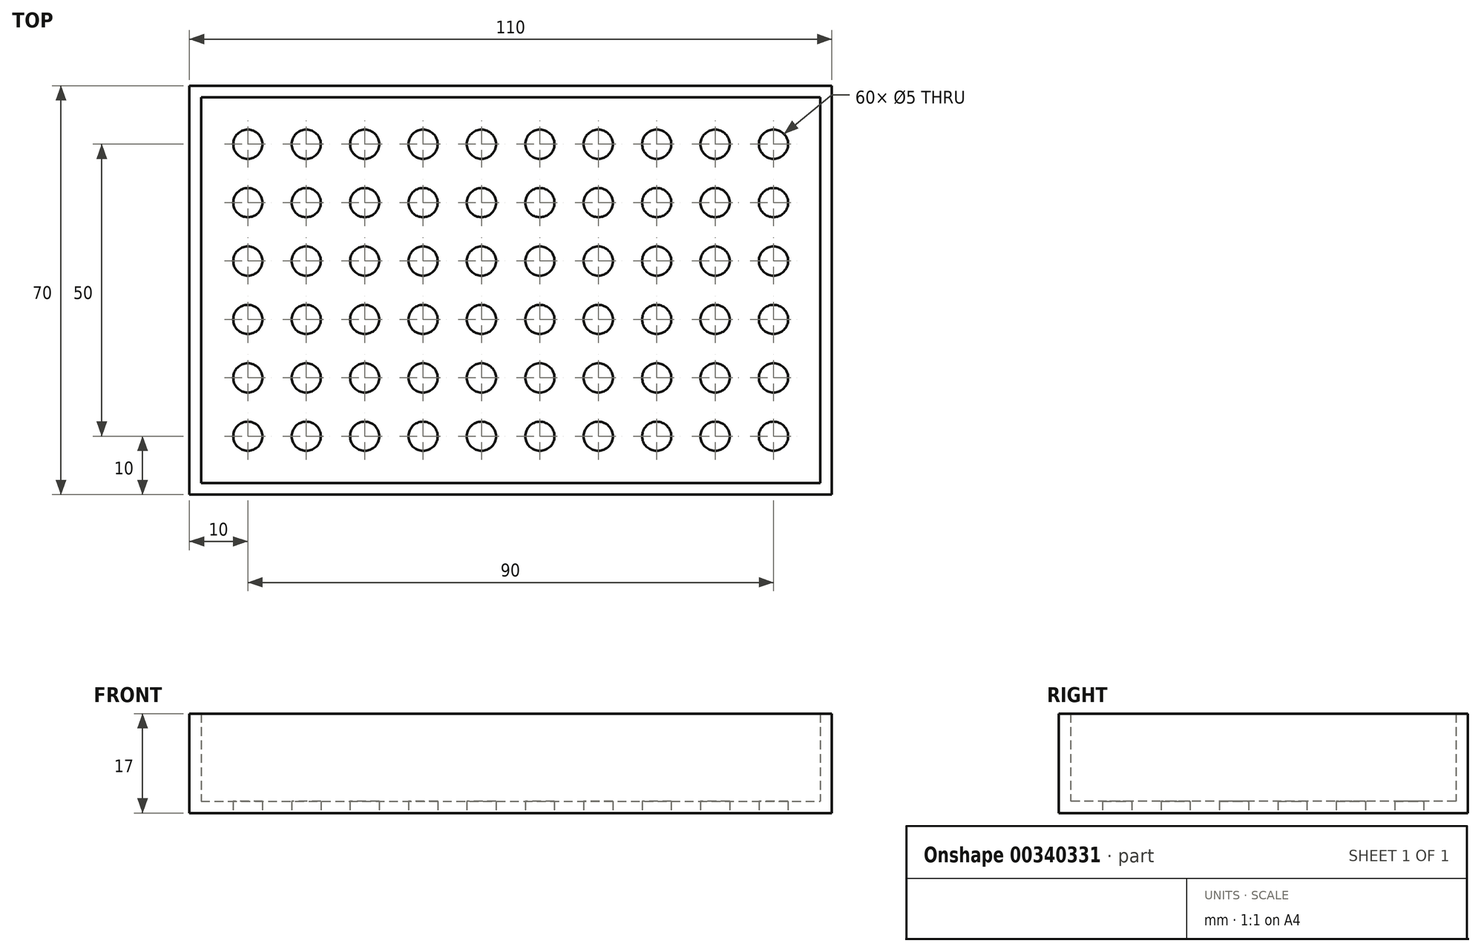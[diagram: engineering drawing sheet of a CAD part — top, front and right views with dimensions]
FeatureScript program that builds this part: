
annotation { "Feature Type Name" : "Feature", "Feature Type Description" : "" }
export const myFeature = defineFeature(function(context is Context, id is Id, definition is map)
    precondition{}
    {
        {
            var Q0;
            Q0=qCreatedBy(makeId("Top.planeOp"),FACE);
            var sketch = newSketch(context, id + "F0", { "sketchPlane" : qUnion([Q0])});
            skLineSegment(sketch, "E0.bottom", {"start": v(-55, 35) * mm, "end": v(55, 35) * mm});
            skLineSegment(sketch, "E0.top", {"start": v(-55, -35) * mm, "end": v(55, -35) * mm});
            skLineSegment(sketch, "E0.left", {"start": v(-55, 35) * mm, "end": v(-55, -35) * mm});
            skLineSegment(sketch, "E0.right", {"start": v(55, 35) * mm, "end": v(55, -35) * mm});
            skCircle(sketch, "E1.1.1.0", {"center": v(-45, -25) * mm, "radius": 2.5 * mm});
            skCircle(sketch, "E1.1.2.0", {"center": v(-45, -15) * mm, "radius": 2.5 * mm});
            skCircle(sketch, "E1.1.3.0", {"center": v(-45, -5) * mm, "radius": 2.5 * mm});
            skCircle(sketch, "E1.1.4.0", {"center": v(-45, 5) * mm, "radius": 2.5 * mm});
            skCircle(sketch, "E1.1.5.0", {"center": v(-45, 15) * mm, "radius": 2.5 * mm});
            skCircle(sketch, "E1.1.6.0", {"center": v(-45, 25) * mm, "radius": 2.5 * mm});
            skCircle(sketch, "E1.2.1.0", {"center": v(-35, -25) * mm, "radius": 2.5 * mm});
            skCircle(sketch, "E1.2.2.0", {"center": v(-35, -15) * mm, "radius": 2.5 * mm});
            skCircle(sketch, "E1.2.3.0", {"center": v(-35, -5) * mm, "radius": 2.5 * mm});
            skCircle(sketch, "E1.2.4.0", {"center": v(-35, 5) * mm, "radius": 2.5 * mm});
            skCircle(sketch, "E1.2.5.0", {"center": v(-35, 15) * mm, "radius": 2.5 * mm});
            skCircle(sketch, "E1.2.6.0", {"center": v(-35, 25) * mm, "radius": 2.5 * mm});
            skCircle(sketch, "E1.3.1.0", {"center": v(-25, -25) * mm, "radius": 2.5 * mm});
            skCircle(sketch, "E1.3.2.0", {"center": v(-25, -15) * mm, "radius": 2.5 * mm});
            skCircle(sketch, "E1.3.3.0", {"center": v(-25, -5) * mm, "radius": 2.5 * mm});
            skCircle(sketch, "E1.3.4.0", {"center": v(-25, 5) * mm, "radius": 2.5 * mm});
            skCircle(sketch, "E1.3.5.0", {"center": v(-25, 15) * mm, "radius": 2.5 * mm});
            skCircle(sketch, "E1.3.6.0", {"center": v(-25, 25) * mm, "radius": 2.5 * mm});
            skCircle(sketch, "E1.4.1.0", {"center": v(-15, -25) * mm, "radius": 2.5 * mm});
            skCircle(sketch, "E1.4.2.0", {"center": v(-15, -15) * mm, "radius": 2.5 * mm});
            skCircle(sketch, "E1.4.3.0", {"center": v(-15, -5) * mm, "radius": 2.5 * mm});
            skCircle(sketch, "E1.4.4.0", {"center": v(-15, 5) * mm, "radius": 2.5 * mm});
            skCircle(sketch, "E1.4.5.0", {"center": v(-15, 15) * mm, "radius": 2.5 * mm});
            skCircle(sketch, "E1.4.6.0", {"center": v(-15, 25) * mm, "radius": 2.5 * mm});
            skCircle(sketch, "E1.5.1.0", {"center": v(-5, -25) * mm, "radius": 2.5 * mm});
            skCircle(sketch, "E1.5.2.0", {"center": v(-5, -15) * mm, "radius": 2.5 * mm});
            skCircle(sketch, "E1.5.3.0", {"center": v(-5, -5) * mm, "radius": 2.5 * mm});
            skCircle(sketch, "E1.5.4.0", {"center": v(-5, 5) * mm, "radius": 2.5 * mm});
            skCircle(sketch, "E1.5.5.0", {"center": v(-5, 15) * mm, "radius": 2.5 * mm});
            skCircle(sketch, "E1.5.6.0", {"center": v(-5, 25) * mm, "radius": 2.5 * mm});
            skCircle(sketch, "E1.6.1.0", {"center": v(5, -25) * mm, "radius": 2.5 * mm});
            skCircle(sketch, "E1.6.2.0", {"center": v(5, -15) * mm, "radius": 2.5 * mm});
            skCircle(sketch, "E1.6.3.0", {"center": v(5, -5) * mm, "radius": 2.5 * mm});
            skCircle(sketch, "E1.6.4.0", {"center": v(5, 5) * mm, "radius": 2.5 * mm});
            skCircle(sketch, "E1.6.5.0", {"center": v(5, 15) * mm, "radius": 2.5 * mm});
            skCircle(sketch, "E1.6.6.0", {"center": v(5, 25) * mm, "radius": 2.5 * mm});
            skCircle(sketch, "E1.7.1.0", {"center": v(15, -25) * mm, "radius": 2.5 * mm});
            skCircle(sketch, "E1.7.2.0", {"center": v(15, -15) * mm, "radius": 2.5 * mm});
            skCircle(sketch, "E1.7.3.0", {"center": v(15, -5) * mm, "radius": 2.5 * mm});
            skCircle(sketch, "E1.7.4.0", {"center": v(15, 5) * mm, "radius": 2.5 * mm});
            skCircle(sketch, "E1.7.5.0", {"center": v(15, 15) * mm, "radius": 2.5 * mm});
            skCircle(sketch, "E1.7.6.0", {"center": v(15, 25) * mm, "radius": 2.5 * mm});
            skCircle(sketch, "E1.8.1.0", {"center": v(25, -25) * mm, "radius": 2.5 * mm});
            skCircle(sketch, "E1.8.2.0", {"center": v(25, -15) * mm, "radius": 2.5 * mm});
            skCircle(sketch, "E1.8.3.0", {"center": v(25, -5) * mm, "radius": 2.5 * mm});
            skCircle(sketch, "E1.8.4.0", {"center": v(25, 5) * mm, "radius": 2.5 * mm});
            skCircle(sketch, "E1.8.5.0", {"center": v(25, 15) * mm, "radius": 2.5 * mm});
            skCircle(sketch, "E1.8.6.0", {"center": v(25, 25) * mm, "radius": 2.5 * mm});
            skCircle(sketch, "E1.9.1.0", {"center": v(35, -25) * mm, "radius": 2.5 * mm});
            skCircle(sketch, "E1.9.2.0", {"center": v(35, -15) * mm, "radius": 2.5 * mm});
            skCircle(sketch, "E1.9.3.0", {"center": v(35, -5) * mm, "radius": 2.5 * mm});
            skCircle(sketch, "E1.9.4.0", {"center": v(35, 5) * mm, "radius": 2.5 * mm});
            skCircle(sketch, "E1.9.5.0", {"center": v(35, 15) * mm, "radius": 2.5 * mm});
            skCircle(sketch, "E1.9.6.0", {"center": v(35, 25) * mm, "radius": 2.5 * mm});
            skLineSegment(sketch, "E1.direction1", {"start": v(-55, -35) * mm, "end": v(-45, -35) * mm, "construction": true});
            skLineSegment(sketch, "E1.direction2", {"start": v(-55, -35) * mm, "end": v(-55, -25) * mm, "construction": true});
            skCircle(sketch, "E2.0.10.1", {"center": v(45, -25) * mm, "radius": 2.5 * mm});
            skCircle(sketch, "E2.0.10.2", {"center": v(45, -15) * mm, "radius": 2.5 * mm});
            skCircle(sketch, "E2.0.10.3", {"center": v(45, -5) * mm, "radius": 2.5 * mm});
            skCircle(sketch, "E2.0.10.4", {"center": v(45, 5) * mm, "radius": 2.5 * mm});
            skCircle(sketch, "E2.0.10.5", {"center": v(45, 15) * mm, "radius": 2.5 * mm});
            skCircle(sketch, "E2.0.10.6", {"center": v(45, 25) * mm, "radius": 2.5 * mm});
            skSolve(sketch);
        }
        {
            var Q0;
            Q0=makeQuery(id+"F0.imprint","IMPRINT",FACE,{"disambiguationData":[TD([[makeQuery(id+"F0.imprint","IMPRINT",EDGE,{"derivedFrom":sQuery(id+"F0.wireOp",EDGE,"E0.bottom")}),-1.0]])]});
            extrude(context, id + "F1", {"entities" : qUnion([Q0]), "depth" : 17 * mm});
        }
        {
            var Q0;
            Q0=makeQuery(id+"F1.opExtrude","CAP_FACE",FACE,{"disambiguationData":[OSD([sQuery(id+"F0.wireOp",EDGE,"E0.bottom"),sQuery(id+"F0.wireOp",EDGE,"E0.top"),sQuery(id+"F0.wireOp",EDGE,"E0.left"),sQuery(id+"F0.wireOp",EDGE,"E0.right"),sQuery(id+"F0.wireOp",EDGE,"E1.1.1.0"),sQuery(id+"F0.wireOp",EDGE,"E1.1.2.0"),sQuery(id+"F0.wireOp",EDGE,"E1.1.3.0"),sQuery(id+"F0.wireOp",EDGE,"E1.1.4.0"),sQuery(id+"F0.wireOp",EDGE,"E1.1.5.0"),sQuery(id+"F0.wireOp",EDGE,"E1.1.6.0"),sQuery(id+"F0.wireOp",EDGE,"E1.2.1.0"),sQuery(id+"F0.wireOp",EDGE,"E1.2.2.0"),sQuery(id+"F0.wireOp",EDGE,"E1.2.3.0"),sQuery(id+"F0.wireOp",EDGE,"E1.2.4.0"),sQuery(id+"F0.wireOp",EDGE,"E1.2.5.0"),sQuery(id+"F0.wireOp",EDGE,"E1.2.6.0"),sQuery(id+"F0.wireOp",EDGE,"E1.3.1.0"),sQuery(id+"F0.wireOp",EDGE,"E1.3.2.0"),sQuery(id+"F0.wireOp",EDGE,"E1.3.3.0"),sQuery(id+"F0.wireOp",EDGE,"E1.3.4.0"),sQuery(id+"F0.wireOp",EDGE,"E1.3.5.0"),sQuery(id+"F0.wireOp",EDGE,"E1.3.6.0"),sQuery(id+"F0.wireOp",EDGE,"E1.4.1.0"),sQuery(id+"F0.wireOp",EDGE,"E1.4.2.0"),sQuery(id+"F0.wireOp",EDGE,"E1.4.3.0"),sQuery(id+"F0.wireOp",EDGE,"E1.4.4.0"),sQuery(id+"F0.wireOp",EDGE,"E1.4.5.0"),sQuery(id+"F0.wireOp",EDGE,"E1.4.6.0"),sQuery(id+"F0.wireOp",EDGE,"E1.5.1.0"),sQuery(id+"F0.wireOp",EDGE,"E1.5.2.0"),sQuery(id+"F0.wireOp",EDGE,"E1.5.3.0"),sQuery(id+"F0.wireOp",EDGE,"E1.5.4.0"),sQuery(id+"F0.wireOp",EDGE,"E1.5.5.0"),sQuery(id+"F0.wireOp",EDGE,"E1.5.6.0"),sQuery(id+"F0.wireOp",EDGE,"E1.6.1.0"),sQuery(id+"F0.wireOp",EDGE,"E1.6.2.0"),sQuery(id+"F0.wireOp",EDGE,"E1.6.3.0"),sQuery(id+"F0.wireOp",EDGE,"E1.6.4.0"),sQuery(id+"F0.wireOp",EDGE,"E1.6.5.0"),sQuery(id+"F0.wireOp",EDGE,"E1.6.6.0"),sQuery(id+"F0.wireOp",EDGE,"E1.7.1.0"),sQuery(id+"F0.wireOp",EDGE,"E1.7.2.0"),sQuery(id+"F0.wireOp",EDGE,"E1.7.3.0"),sQuery(id+"F0.wireOp",EDGE,"E1.7.4.0"),sQuery(id+"F0.wireOp",EDGE,"E1.7.5.0"),sQuery(id+"F0.wireOp",EDGE,"E1.7.6.0"),sQuery(id+"F0.wireOp",EDGE,"E1.8.1.0"),sQuery(id+"F0.wireOp",EDGE,"E1.8.2.0"),sQuery(id+"F0.wireOp",EDGE,"E1.8.3.0"),sQuery(id+"F0.wireOp",EDGE,"E1.8.4.0"),sQuery(id+"F0.wireOp",EDGE,"E1.8.5.0"),sQuery(id+"F0.wireOp",EDGE,"E1.8.6.0"),sQuery(id+"F0.wireOp",EDGE,"E1.9.1.0"),sQuery(id+"F0.wireOp",EDGE,"E1.9.2.0"),sQuery(id+"F0.wireOp",EDGE,"E1.9.3.0"),sQuery(id+"F0.wireOp",EDGE,"E1.9.4.0"),sQuery(id+"F0.wireOp",EDGE,"E1.9.5.0"),sQuery(id+"F0.wireOp",EDGE,"E1.9.6.0"),sQuery(id+"F0.wireOp",EDGE,"E2.0.10.1"),sQuery(id+"F0.wireOp",EDGE,"E2.0.10.2"),sQuery(id+"F0.wireOp",EDGE,"E2.0.10.3"),sQuery(id+"F0.wireOp",EDGE,"E2.0.10.4"),sQuery(id+"F0.wireOp",EDGE,"E2.0.10.5"),sQuery(id+"F0.wireOp",EDGE,"E2.0.10.6")])],"isStart":false});
            shell(context, id + "F2", {"entities" : qUnion([Q0]), "thickness" : 2 * mm});
        }
        {
            var Q0;
            {var subQ0=sQuery(id+"F0.wireOp",EDGE,"E2.0.10.6");var subQ1=sQuery(id+"F0.wireOp",EDGE,"E2.0.10.5");var subQ2=sQuery(id+"F0.wireOp",EDGE,"E2.0.10.4");var subQ3=sQuery(id+"F0.wireOp",EDGE,"E2.0.10.3");var subQ4=sQuery(id+"F0.wireOp",EDGE,"E2.0.10.2");var subQ5=sQuery(id+"F0.wireOp",EDGE,"E2.0.10.1");var subQ6=sQuery(id+"F0.wireOp",EDGE,"E1.9.6.0");var subQ7=sQuery(id+"F0.wireOp",EDGE,"E1.9.5.0");var subQ8=sQuery(id+"F0.wireOp",EDGE,"E1.9.4.0");var subQ9=sQuery(id+"F0.wireOp",EDGE,"E1.9.3.0");var subQ10=sQuery(id+"F0.wireOp",EDGE,"E1.9.2.0");var subQ11=sQuery(id+"F0.wireOp",EDGE,"E1.9.1.0");var subQ12=sQuery(id+"F0.wireOp",EDGE,"E1.8.6.0");var subQ13=sQuery(id+"F0.wireOp",EDGE,"E1.8.5.0");var subQ14=sQuery(id+"F0.wireOp",EDGE,"E1.8.4.0");var subQ15=sQuery(id+"F0.wireOp",EDGE,"E1.8.3.0");var subQ16=sQuery(id+"F0.wireOp",EDGE,"E1.8.2.0");var subQ17=sQuery(id+"F0.wireOp",EDGE,"E1.8.1.0");var subQ18=sQuery(id+"F0.wireOp",EDGE,"E1.7.6.0");var subQ19=sQuery(id+"F0.wireOp",EDGE,"E1.7.5.0");var subQ20=sQuery(id+"F0.wireOp",EDGE,"E1.7.4.0");var subQ21=sQuery(id+"F0.wireOp",EDGE,"E1.7.3.0");var subQ22=sQuery(id+"F0.wireOp",EDGE,"E1.7.2.0");var subQ23=sQuery(id+"F0.wireOp",EDGE,"E1.7.1.0");var subQ24=sQuery(id+"F0.wireOp",EDGE,"E1.6.6.0");var subQ25=sQuery(id+"F0.wireOp",EDGE,"E1.6.5.0");var subQ26=sQuery(id+"F0.wireOp",EDGE,"E1.6.4.0");var subQ27=sQuery(id+"F0.wireOp",EDGE,"E1.6.3.0");var subQ28=sQuery(id+"F0.wireOp",EDGE,"E1.6.2.0");var subQ29=sQuery(id+"F0.wireOp",EDGE,"E1.6.1.0");var subQ30=sQuery(id+"F0.wireOp",EDGE,"E1.5.6.0");var subQ31=sQuery(id+"F0.wireOp",EDGE,"E1.5.5.0");var subQ32=sQuery(id+"F0.wireOp",EDGE,"E1.5.4.0");var subQ33=sQuery(id+"F0.wireOp",EDGE,"E1.5.3.0");var subQ34=sQuery(id+"F0.wireOp",EDGE,"E1.5.2.0");var subQ35=sQuery(id+"F0.wireOp",EDGE,"E1.5.1.0");var subQ36=sQuery(id+"F0.wireOp",EDGE,"E1.4.6.0");var subQ37=sQuery(id+"F0.wireOp",EDGE,"E1.4.5.0");var subQ38=sQuery(id+"F0.wireOp",EDGE,"E1.4.4.0");var subQ39=sQuery(id+"F0.wireOp",EDGE,"E1.4.3.0");var subQ40=sQuery(id+"F0.wireOp",EDGE,"E1.4.2.0");var subQ41=sQuery(id+"F0.wireOp",EDGE,"E1.4.1.0");var subQ42=sQuery(id+"F0.wireOp",EDGE,"E1.3.6.0");var subQ43=sQuery(id+"F0.wireOp",EDGE,"E1.3.5.0");var subQ44=sQuery(id+"F0.wireOp",EDGE,"E1.3.4.0");var subQ45=sQuery(id+"F0.wireOp",EDGE,"E1.3.3.0");var subQ46=sQuery(id+"F0.wireOp",EDGE,"E1.3.2.0");var subQ47=sQuery(id+"F0.wireOp",EDGE,"E1.3.1.0");var subQ48=sQuery(id+"F0.wireOp",EDGE,"E1.2.6.0");var subQ49=sQuery(id+"F0.wireOp",EDGE,"E1.2.5.0");var subQ50=sQuery(id+"F0.wireOp",EDGE,"E1.2.4.0");var subQ51=sQuery(id+"F0.wireOp",EDGE,"E1.2.3.0");var subQ52=sQuery(id+"F0.wireOp",EDGE,"E1.2.2.0");var subQ53=sQuery(id+"F0.wireOp",EDGE,"E1.2.1.0");var subQ54=sQuery(id+"F0.wireOp",EDGE,"E1.1.6.0");var subQ55=sQuery(id+"F0.wireOp",EDGE,"E1.1.5.0");var subQ56=sQuery(id+"F0.wireOp",EDGE,"E1.1.4.0");var subQ57=sQuery(id+"F0.wireOp",EDGE,"E1.1.3.0");var subQ58=sQuery(id+"F0.wireOp",EDGE,"E1.1.2.0");var subQ59=sQuery(id+"F0.wireOp",EDGE,"E1.1.1.0");var subQ60=sQuery(id+"F0.wireOp",EDGE,"E0.right");var subQ61=sQuery(id+"F0.wireOp",EDGE,"E0.left");var subQ62=sQuery(id+"F0.wireOp",EDGE,"E0.top");var subQ63=sQuery(id+"F0.wireOp",EDGE,"E0.bottom");Q0=makeQuery(id+"F2.opShell","OFFSET_FACE",FACE,{"disambiguationData":[OSD([subQ63,subQ62,subQ61,subQ60,subQ59,subQ58,subQ57,subQ56,subQ55,subQ54,subQ53,subQ52,subQ51,subQ50,subQ49,subQ48,subQ47,subQ46,subQ45,subQ44,subQ43,subQ42,subQ41,subQ40,subQ39,subQ38,subQ37,subQ36,subQ35,subQ34,subQ33,subQ32,subQ31,subQ30,subQ29,subQ28,subQ27,subQ26,subQ25,subQ24,subQ23,subQ22,subQ21,subQ20,subQ19,subQ18,subQ17,subQ16,subQ15,subQ14,subQ13,subQ12,subQ11,subQ10,subQ9,subQ8,subQ7,subQ6,subQ5,subQ4,subQ3,subQ2,subQ1,subQ0]),TDD([makeQuery(id+"F1.opExtrude","CAP_FACE",FACE,{"disambiguationData":[OSD([subQ63,subQ62,subQ61,subQ60,subQ59,subQ58,subQ57,subQ56,subQ55,subQ54,subQ53,subQ52,subQ51,subQ50,subQ49,subQ48,subQ47,subQ46,subQ45,subQ44,subQ43,subQ42,subQ41,subQ40,subQ39,subQ38,subQ37,subQ36,subQ35,subQ34,subQ33,subQ32,subQ31,subQ30,subQ29,subQ28,subQ27,subQ26,subQ25,subQ24,subQ23,subQ22,subQ21,subQ20,subQ19,subQ18,subQ17,subQ16,subQ15,subQ14,subQ13,subQ12,subQ11,subQ10,subQ9,subQ8,subQ7,subQ6,subQ5,subQ4,subQ3,subQ2,subQ1,subQ0])],"isStart":false})]),OD(5.0)]});}
            var Q1;
            {var subQ0=sQuery(id+"F0.wireOp",EDGE,"E2.0.10.6");var subQ1=sQuery(id+"F0.wireOp",EDGE,"E2.0.10.5");var subQ2=sQuery(id+"F0.wireOp",EDGE,"E2.0.10.4");var subQ3=sQuery(id+"F0.wireOp",EDGE,"E2.0.10.3");var subQ4=sQuery(id+"F0.wireOp",EDGE,"E2.0.10.2");var subQ5=sQuery(id+"F0.wireOp",EDGE,"E2.0.10.1");var subQ6=sQuery(id+"F0.wireOp",EDGE,"E1.9.6.0");var subQ7=sQuery(id+"F0.wireOp",EDGE,"E1.9.5.0");var subQ8=sQuery(id+"F0.wireOp",EDGE,"E1.9.4.0");var subQ9=sQuery(id+"F0.wireOp",EDGE,"E1.9.3.0");var subQ10=sQuery(id+"F0.wireOp",EDGE,"E1.9.2.0");var subQ11=sQuery(id+"F0.wireOp",EDGE,"E1.9.1.0");var subQ12=sQuery(id+"F0.wireOp",EDGE,"E1.8.6.0");var subQ13=sQuery(id+"F0.wireOp",EDGE,"E1.8.5.0");var subQ14=sQuery(id+"F0.wireOp",EDGE,"E1.8.4.0");var subQ15=sQuery(id+"F0.wireOp",EDGE,"E1.8.3.0");var subQ16=sQuery(id+"F0.wireOp",EDGE,"E1.8.2.0");var subQ17=sQuery(id+"F0.wireOp",EDGE,"E1.8.1.0");var subQ18=sQuery(id+"F0.wireOp",EDGE,"E1.7.6.0");var subQ19=sQuery(id+"F0.wireOp",EDGE,"E1.7.5.0");var subQ20=sQuery(id+"F0.wireOp",EDGE,"E1.7.4.0");var subQ21=sQuery(id+"F0.wireOp",EDGE,"E1.7.3.0");var subQ22=sQuery(id+"F0.wireOp",EDGE,"E1.7.2.0");var subQ23=sQuery(id+"F0.wireOp",EDGE,"E1.7.1.0");var subQ24=sQuery(id+"F0.wireOp",EDGE,"E1.6.6.0");var subQ25=sQuery(id+"F0.wireOp",EDGE,"E1.6.5.0");var subQ26=sQuery(id+"F0.wireOp",EDGE,"E1.6.4.0");var subQ27=sQuery(id+"F0.wireOp",EDGE,"E1.6.3.0");var subQ28=sQuery(id+"F0.wireOp",EDGE,"E1.6.2.0");var subQ29=sQuery(id+"F0.wireOp",EDGE,"E1.6.1.0");var subQ30=sQuery(id+"F0.wireOp",EDGE,"E1.5.6.0");var subQ31=sQuery(id+"F0.wireOp",EDGE,"E1.5.5.0");var subQ32=sQuery(id+"F0.wireOp",EDGE,"E1.5.4.0");var subQ33=sQuery(id+"F0.wireOp",EDGE,"E1.5.3.0");var subQ34=sQuery(id+"F0.wireOp",EDGE,"E1.5.2.0");var subQ35=sQuery(id+"F0.wireOp",EDGE,"E1.5.1.0");var subQ36=sQuery(id+"F0.wireOp",EDGE,"E1.4.6.0");var subQ37=sQuery(id+"F0.wireOp",EDGE,"E1.4.5.0");var subQ38=sQuery(id+"F0.wireOp",EDGE,"E1.4.4.0");var subQ39=sQuery(id+"F0.wireOp",EDGE,"E1.4.3.0");var subQ40=sQuery(id+"F0.wireOp",EDGE,"E1.4.2.0");var subQ41=sQuery(id+"F0.wireOp",EDGE,"E1.4.1.0");var subQ42=sQuery(id+"F0.wireOp",EDGE,"E1.3.6.0");var subQ43=sQuery(id+"F0.wireOp",EDGE,"E1.3.5.0");var subQ44=sQuery(id+"F0.wireOp",EDGE,"E1.3.4.0");var subQ45=sQuery(id+"F0.wireOp",EDGE,"E1.3.3.0");var subQ46=sQuery(id+"F0.wireOp",EDGE,"E1.3.2.0");var subQ47=sQuery(id+"F0.wireOp",EDGE,"E1.3.1.0");var subQ48=sQuery(id+"F0.wireOp",EDGE,"E1.2.6.0");var subQ49=sQuery(id+"F0.wireOp",EDGE,"E1.2.5.0");var subQ50=sQuery(id+"F0.wireOp",EDGE,"E1.2.4.0");var subQ51=sQuery(id+"F0.wireOp",EDGE,"E1.2.3.0");var subQ52=sQuery(id+"F0.wireOp",EDGE,"E1.2.2.0");var subQ53=sQuery(id+"F0.wireOp",EDGE,"E1.2.1.0");var subQ54=sQuery(id+"F0.wireOp",EDGE,"E1.1.6.0");var subQ55=sQuery(id+"F0.wireOp",EDGE,"E1.1.5.0");var subQ56=sQuery(id+"F0.wireOp",EDGE,"E1.1.4.0");var subQ57=sQuery(id+"F0.wireOp",EDGE,"E1.1.3.0");var subQ58=sQuery(id+"F0.wireOp",EDGE,"E1.1.2.0");var subQ59=sQuery(id+"F0.wireOp",EDGE,"E1.1.1.0");var subQ60=sQuery(id+"F0.wireOp",EDGE,"E0.right");var subQ61=sQuery(id+"F0.wireOp",EDGE,"E0.left");var subQ62=sQuery(id+"F0.wireOp",EDGE,"E0.top");var subQ63=sQuery(id+"F0.wireOp",EDGE,"E0.bottom");Q1=makeQuery(id+"F2.opShell","OFFSET_FACE",FACE,{"disambiguationData":[OSD([subQ63,subQ62,subQ61,subQ60,subQ59,subQ58,subQ57,subQ56,subQ55,subQ54,subQ53,subQ52,subQ51,subQ50,subQ49,subQ48,subQ47,subQ46,subQ45,subQ44,subQ43,subQ42,subQ41,subQ40,subQ39,subQ38,subQ37,subQ36,subQ35,subQ34,subQ33,subQ32,subQ31,subQ30,subQ29,subQ28,subQ27,subQ26,subQ25,subQ24,subQ23,subQ22,subQ21,subQ20,subQ19,subQ18,subQ17,subQ16,subQ15,subQ14,subQ13,subQ12,subQ11,subQ10,subQ9,subQ8,subQ7,subQ6,subQ5,subQ4,subQ3,subQ2,subQ1,subQ0]),TDD([makeQuery(id+"F1.opExtrude","CAP_FACE",FACE,{"disambiguationData":[OSD([subQ63,subQ62,subQ61,subQ60,subQ59,subQ58,subQ57,subQ56,subQ55,subQ54,subQ53,subQ52,subQ51,subQ50,subQ49,subQ48,subQ47,subQ46,subQ45,subQ44,subQ43,subQ42,subQ41,subQ40,subQ39,subQ38,subQ37,subQ36,subQ35,subQ34,subQ33,subQ32,subQ31,subQ30,subQ29,subQ28,subQ27,subQ26,subQ25,subQ24,subQ23,subQ22,subQ21,subQ20,subQ19,subQ18,subQ17,subQ16,subQ15,subQ14,subQ13,subQ12,subQ11,subQ10,subQ9,subQ8,subQ7,subQ6,subQ5,subQ4,subQ3,subQ2,subQ1,subQ0])],"isStart":false})]),OD(11.0)]});}
            var Q2;
            {var subQ0=sQuery(id+"F0.wireOp",EDGE,"E2.0.10.6");var subQ1=sQuery(id+"F0.wireOp",EDGE,"E2.0.10.5");var subQ2=sQuery(id+"F0.wireOp",EDGE,"E2.0.10.4");var subQ3=sQuery(id+"F0.wireOp",EDGE,"E2.0.10.3");var subQ4=sQuery(id+"F0.wireOp",EDGE,"E2.0.10.2");var subQ5=sQuery(id+"F0.wireOp",EDGE,"E2.0.10.1");var subQ6=sQuery(id+"F0.wireOp",EDGE,"E1.9.6.0");var subQ7=sQuery(id+"F0.wireOp",EDGE,"E1.9.5.0");var subQ8=sQuery(id+"F0.wireOp",EDGE,"E1.9.4.0");var subQ9=sQuery(id+"F0.wireOp",EDGE,"E1.9.3.0");var subQ10=sQuery(id+"F0.wireOp",EDGE,"E1.9.2.0");var subQ11=sQuery(id+"F0.wireOp",EDGE,"E1.9.1.0");var subQ12=sQuery(id+"F0.wireOp",EDGE,"E1.8.6.0");var subQ13=sQuery(id+"F0.wireOp",EDGE,"E1.8.5.0");var subQ14=sQuery(id+"F0.wireOp",EDGE,"E1.8.4.0");var subQ15=sQuery(id+"F0.wireOp",EDGE,"E1.8.3.0");var subQ16=sQuery(id+"F0.wireOp",EDGE,"E1.8.2.0");var subQ17=sQuery(id+"F0.wireOp",EDGE,"E1.8.1.0");var subQ18=sQuery(id+"F0.wireOp",EDGE,"E1.7.6.0");var subQ19=sQuery(id+"F0.wireOp",EDGE,"E1.7.5.0");var subQ20=sQuery(id+"F0.wireOp",EDGE,"E1.7.4.0");var subQ21=sQuery(id+"F0.wireOp",EDGE,"E1.7.3.0");var subQ22=sQuery(id+"F0.wireOp",EDGE,"E1.7.2.0");var subQ23=sQuery(id+"F0.wireOp",EDGE,"E1.7.1.0");var subQ24=sQuery(id+"F0.wireOp",EDGE,"E1.6.6.0");var subQ25=sQuery(id+"F0.wireOp",EDGE,"E1.6.5.0");var subQ26=sQuery(id+"F0.wireOp",EDGE,"E1.6.4.0");var subQ27=sQuery(id+"F0.wireOp",EDGE,"E1.6.3.0");var subQ28=sQuery(id+"F0.wireOp",EDGE,"E1.6.2.0");var subQ29=sQuery(id+"F0.wireOp",EDGE,"E1.6.1.0");var subQ30=sQuery(id+"F0.wireOp",EDGE,"E1.5.6.0");var subQ31=sQuery(id+"F0.wireOp",EDGE,"E1.5.5.0");var subQ32=sQuery(id+"F0.wireOp",EDGE,"E1.5.4.0");var subQ33=sQuery(id+"F0.wireOp",EDGE,"E1.5.3.0");var subQ34=sQuery(id+"F0.wireOp",EDGE,"E1.5.2.0");var subQ35=sQuery(id+"F0.wireOp",EDGE,"E1.5.1.0");var subQ36=sQuery(id+"F0.wireOp",EDGE,"E1.4.6.0");var subQ37=sQuery(id+"F0.wireOp",EDGE,"E1.4.5.0");var subQ38=sQuery(id+"F0.wireOp",EDGE,"E1.4.4.0");var subQ39=sQuery(id+"F0.wireOp",EDGE,"E1.4.3.0");var subQ40=sQuery(id+"F0.wireOp",EDGE,"E1.4.2.0");var subQ41=sQuery(id+"F0.wireOp",EDGE,"E1.4.1.0");var subQ42=sQuery(id+"F0.wireOp",EDGE,"E1.3.6.0");var subQ43=sQuery(id+"F0.wireOp",EDGE,"E1.3.5.0");var subQ44=sQuery(id+"F0.wireOp",EDGE,"E1.3.4.0");var subQ45=sQuery(id+"F0.wireOp",EDGE,"E1.3.3.0");var subQ46=sQuery(id+"F0.wireOp",EDGE,"E1.3.2.0");var subQ47=sQuery(id+"F0.wireOp",EDGE,"E1.3.1.0");var subQ48=sQuery(id+"F0.wireOp",EDGE,"E1.2.6.0");var subQ49=sQuery(id+"F0.wireOp",EDGE,"E1.2.5.0");var subQ50=sQuery(id+"F0.wireOp",EDGE,"E1.2.4.0");var subQ51=sQuery(id+"F0.wireOp",EDGE,"E1.2.3.0");var subQ52=sQuery(id+"F0.wireOp",EDGE,"E1.2.2.0");var subQ53=sQuery(id+"F0.wireOp",EDGE,"E1.2.1.0");var subQ54=sQuery(id+"F0.wireOp",EDGE,"E1.1.6.0");var subQ55=sQuery(id+"F0.wireOp",EDGE,"E1.1.5.0");var subQ56=sQuery(id+"F0.wireOp",EDGE,"E1.1.4.0");var subQ57=sQuery(id+"F0.wireOp",EDGE,"E1.1.3.0");var subQ58=sQuery(id+"F0.wireOp",EDGE,"E1.1.2.0");var subQ59=sQuery(id+"F0.wireOp",EDGE,"E1.1.1.0");var subQ60=sQuery(id+"F0.wireOp",EDGE,"E0.right");var subQ61=sQuery(id+"F0.wireOp",EDGE,"E0.left");var subQ62=sQuery(id+"F0.wireOp",EDGE,"E0.top");var subQ63=sQuery(id+"F0.wireOp",EDGE,"E0.bottom");Q2=makeQuery(id+"F2.opShell","OFFSET_FACE",FACE,{"disambiguationData":[OSD([subQ63,subQ62,subQ61,subQ60,subQ59,subQ58,subQ57,subQ56,subQ55,subQ54,subQ53,subQ52,subQ51,subQ50,subQ49,subQ48,subQ47,subQ46,subQ45,subQ44,subQ43,subQ42,subQ41,subQ40,subQ39,subQ38,subQ37,subQ36,subQ35,subQ34,subQ33,subQ32,subQ31,subQ30,subQ29,subQ28,subQ27,subQ26,subQ25,subQ24,subQ23,subQ22,subQ21,subQ20,subQ19,subQ18,subQ17,subQ16,subQ15,subQ14,subQ13,subQ12,subQ11,subQ10,subQ9,subQ8,subQ7,subQ6,subQ5,subQ4,subQ3,subQ2,subQ1,subQ0]),TDD([makeQuery(id+"F1.opExtrude","CAP_FACE",FACE,{"disambiguationData":[OSD([subQ63,subQ62,subQ61,subQ60,subQ59,subQ58,subQ57,subQ56,subQ55,subQ54,subQ53,subQ52,subQ51,subQ50,subQ49,subQ48,subQ47,subQ46,subQ45,subQ44,subQ43,subQ42,subQ41,subQ40,subQ39,subQ38,subQ37,subQ36,subQ35,subQ34,subQ33,subQ32,subQ31,subQ30,subQ29,subQ28,subQ27,subQ26,subQ25,subQ24,subQ23,subQ22,subQ21,subQ20,subQ19,subQ18,subQ17,subQ16,subQ15,subQ14,subQ13,subQ12,subQ11,subQ10,subQ9,subQ8,subQ7,subQ6,subQ5,subQ4,subQ3,subQ2,subQ1,subQ0])],"isStart":false})]),OD(17.0)]});}
            var Q3;
            {var subQ0=sQuery(id+"F0.wireOp",EDGE,"E2.0.10.6");var subQ1=sQuery(id+"F0.wireOp",EDGE,"E2.0.10.5");var subQ2=sQuery(id+"F0.wireOp",EDGE,"E2.0.10.4");var subQ3=sQuery(id+"F0.wireOp",EDGE,"E2.0.10.3");var subQ4=sQuery(id+"F0.wireOp",EDGE,"E2.0.10.2");var subQ5=sQuery(id+"F0.wireOp",EDGE,"E2.0.10.1");var subQ6=sQuery(id+"F0.wireOp",EDGE,"E1.9.6.0");var subQ7=sQuery(id+"F0.wireOp",EDGE,"E1.9.5.0");var subQ8=sQuery(id+"F0.wireOp",EDGE,"E1.9.4.0");var subQ9=sQuery(id+"F0.wireOp",EDGE,"E1.9.3.0");var subQ10=sQuery(id+"F0.wireOp",EDGE,"E1.9.2.0");var subQ11=sQuery(id+"F0.wireOp",EDGE,"E1.9.1.0");var subQ12=sQuery(id+"F0.wireOp",EDGE,"E1.8.6.0");var subQ13=sQuery(id+"F0.wireOp",EDGE,"E1.8.5.0");var subQ14=sQuery(id+"F0.wireOp",EDGE,"E1.8.4.0");var subQ15=sQuery(id+"F0.wireOp",EDGE,"E1.8.3.0");var subQ16=sQuery(id+"F0.wireOp",EDGE,"E1.8.2.0");var subQ17=sQuery(id+"F0.wireOp",EDGE,"E1.8.1.0");var subQ18=sQuery(id+"F0.wireOp",EDGE,"E1.7.6.0");var subQ19=sQuery(id+"F0.wireOp",EDGE,"E1.7.5.0");var subQ20=sQuery(id+"F0.wireOp",EDGE,"E1.7.4.0");var subQ21=sQuery(id+"F0.wireOp",EDGE,"E1.7.3.0");var subQ22=sQuery(id+"F0.wireOp",EDGE,"E1.7.2.0");var subQ23=sQuery(id+"F0.wireOp",EDGE,"E1.7.1.0");var subQ24=sQuery(id+"F0.wireOp",EDGE,"E1.6.6.0");var subQ25=sQuery(id+"F0.wireOp",EDGE,"E1.6.5.0");var subQ26=sQuery(id+"F0.wireOp",EDGE,"E1.6.4.0");var subQ27=sQuery(id+"F0.wireOp",EDGE,"E1.6.3.0");var subQ28=sQuery(id+"F0.wireOp",EDGE,"E1.6.2.0");var subQ29=sQuery(id+"F0.wireOp",EDGE,"E1.6.1.0");var subQ30=sQuery(id+"F0.wireOp",EDGE,"E1.5.6.0");var subQ31=sQuery(id+"F0.wireOp",EDGE,"E1.5.5.0");var subQ32=sQuery(id+"F0.wireOp",EDGE,"E1.5.4.0");var subQ33=sQuery(id+"F0.wireOp",EDGE,"E1.5.3.0");var subQ34=sQuery(id+"F0.wireOp",EDGE,"E1.5.2.0");var subQ35=sQuery(id+"F0.wireOp",EDGE,"E1.5.1.0");var subQ36=sQuery(id+"F0.wireOp",EDGE,"E1.4.6.0");var subQ37=sQuery(id+"F0.wireOp",EDGE,"E1.4.5.0");var subQ38=sQuery(id+"F0.wireOp",EDGE,"E1.4.4.0");var subQ39=sQuery(id+"F0.wireOp",EDGE,"E1.4.3.0");var subQ40=sQuery(id+"F0.wireOp",EDGE,"E1.4.2.0");var subQ41=sQuery(id+"F0.wireOp",EDGE,"E1.4.1.0");var subQ42=sQuery(id+"F0.wireOp",EDGE,"E1.3.6.0");var subQ43=sQuery(id+"F0.wireOp",EDGE,"E1.3.5.0");var subQ44=sQuery(id+"F0.wireOp",EDGE,"E1.3.4.0");var subQ45=sQuery(id+"F0.wireOp",EDGE,"E1.3.3.0");var subQ46=sQuery(id+"F0.wireOp",EDGE,"E1.3.2.0");var subQ47=sQuery(id+"F0.wireOp",EDGE,"E1.3.1.0");var subQ48=sQuery(id+"F0.wireOp",EDGE,"E1.2.6.0");var subQ49=sQuery(id+"F0.wireOp",EDGE,"E1.2.5.0");var subQ50=sQuery(id+"F0.wireOp",EDGE,"E1.2.4.0");var subQ51=sQuery(id+"F0.wireOp",EDGE,"E1.2.3.0");var subQ52=sQuery(id+"F0.wireOp",EDGE,"E1.2.2.0");var subQ53=sQuery(id+"F0.wireOp",EDGE,"E1.2.1.0");var subQ54=sQuery(id+"F0.wireOp",EDGE,"E1.1.6.0");var subQ55=sQuery(id+"F0.wireOp",EDGE,"E1.1.5.0");var subQ56=sQuery(id+"F0.wireOp",EDGE,"E1.1.4.0");var subQ57=sQuery(id+"F0.wireOp",EDGE,"E1.1.3.0");var subQ58=sQuery(id+"F0.wireOp",EDGE,"E1.1.2.0");var subQ59=sQuery(id+"F0.wireOp",EDGE,"E1.1.1.0");var subQ60=sQuery(id+"F0.wireOp",EDGE,"E0.right");var subQ61=sQuery(id+"F0.wireOp",EDGE,"E0.left");var subQ62=sQuery(id+"F0.wireOp",EDGE,"E0.top");var subQ63=sQuery(id+"F0.wireOp",EDGE,"E0.bottom");Q3=makeQuery(id+"F2.opShell","OFFSET_FACE",FACE,{"disambiguationData":[OSD([subQ63,subQ62,subQ61,subQ60,subQ59,subQ58,subQ57,subQ56,subQ55,subQ54,subQ53,subQ52,subQ51,subQ50,subQ49,subQ48,subQ47,subQ46,subQ45,subQ44,subQ43,subQ42,subQ41,subQ40,subQ39,subQ38,subQ37,subQ36,subQ35,subQ34,subQ33,subQ32,subQ31,subQ30,subQ29,subQ28,subQ27,subQ26,subQ25,subQ24,subQ23,subQ22,subQ21,subQ20,subQ19,subQ18,subQ17,subQ16,subQ15,subQ14,subQ13,subQ12,subQ11,subQ10,subQ9,subQ8,subQ7,subQ6,subQ5,subQ4,subQ3,subQ2,subQ1,subQ0]),TDD([makeQuery(id+"F1.opExtrude","CAP_FACE",FACE,{"disambiguationData":[OSD([subQ63,subQ62,subQ61,subQ60,subQ59,subQ58,subQ57,subQ56,subQ55,subQ54,subQ53,subQ52,subQ51,subQ50,subQ49,subQ48,subQ47,subQ46,subQ45,subQ44,subQ43,subQ42,subQ41,subQ40,subQ39,subQ38,subQ37,subQ36,subQ35,subQ34,subQ33,subQ32,subQ31,subQ30,subQ29,subQ28,subQ27,subQ26,subQ25,subQ24,subQ23,subQ22,subQ21,subQ20,subQ19,subQ18,subQ17,subQ16,subQ15,subQ14,subQ13,subQ12,subQ11,subQ10,subQ9,subQ8,subQ7,subQ6,subQ5,subQ4,subQ3,subQ2,subQ1,subQ0])],"isStart":false})]),OD(23.0)]});}
            var Q4;
            {var subQ0=sQuery(id+"F0.wireOp",EDGE,"E2.0.10.6");var subQ1=sQuery(id+"F0.wireOp",EDGE,"E2.0.10.5");var subQ2=sQuery(id+"F0.wireOp",EDGE,"E2.0.10.4");var subQ3=sQuery(id+"F0.wireOp",EDGE,"E2.0.10.3");var subQ4=sQuery(id+"F0.wireOp",EDGE,"E2.0.10.2");var subQ5=sQuery(id+"F0.wireOp",EDGE,"E2.0.10.1");var subQ6=sQuery(id+"F0.wireOp",EDGE,"E1.9.6.0");var subQ7=sQuery(id+"F0.wireOp",EDGE,"E1.9.5.0");var subQ8=sQuery(id+"F0.wireOp",EDGE,"E1.9.4.0");var subQ9=sQuery(id+"F0.wireOp",EDGE,"E1.9.3.0");var subQ10=sQuery(id+"F0.wireOp",EDGE,"E1.9.2.0");var subQ11=sQuery(id+"F0.wireOp",EDGE,"E1.9.1.0");var subQ12=sQuery(id+"F0.wireOp",EDGE,"E1.8.6.0");var subQ13=sQuery(id+"F0.wireOp",EDGE,"E1.8.5.0");var subQ14=sQuery(id+"F0.wireOp",EDGE,"E1.8.4.0");var subQ15=sQuery(id+"F0.wireOp",EDGE,"E1.8.3.0");var subQ16=sQuery(id+"F0.wireOp",EDGE,"E1.8.2.0");var subQ17=sQuery(id+"F0.wireOp",EDGE,"E1.8.1.0");var subQ18=sQuery(id+"F0.wireOp",EDGE,"E1.7.6.0");var subQ19=sQuery(id+"F0.wireOp",EDGE,"E1.7.5.0");var subQ20=sQuery(id+"F0.wireOp",EDGE,"E1.7.4.0");var subQ21=sQuery(id+"F0.wireOp",EDGE,"E1.7.3.0");var subQ22=sQuery(id+"F0.wireOp",EDGE,"E1.7.2.0");var subQ23=sQuery(id+"F0.wireOp",EDGE,"E1.7.1.0");var subQ24=sQuery(id+"F0.wireOp",EDGE,"E1.6.6.0");var subQ25=sQuery(id+"F0.wireOp",EDGE,"E1.6.5.0");var subQ26=sQuery(id+"F0.wireOp",EDGE,"E1.6.4.0");var subQ27=sQuery(id+"F0.wireOp",EDGE,"E1.6.3.0");var subQ28=sQuery(id+"F0.wireOp",EDGE,"E1.6.2.0");var subQ29=sQuery(id+"F0.wireOp",EDGE,"E1.6.1.0");var subQ30=sQuery(id+"F0.wireOp",EDGE,"E1.5.6.0");var subQ31=sQuery(id+"F0.wireOp",EDGE,"E1.5.5.0");var subQ32=sQuery(id+"F0.wireOp",EDGE,"E1.5.4.0");var subQ33=sQuery(id+"F0.wireOp",EDGE,"E1.5.3.0");var subQ34=sQuery(id+"F0.wireOp",EDGE,"E1.5.2.0");var subQ35=sQuery(id+"F0.wireOp",EDGE,"E1.5.1.0");var subQ36=sQuery(id+"F0.wireOp",EDGE,"E1.4.6.0");var subQ37=sQuery(id+"F0.wireOp",EDGE,"E1.4.5.0");var subQ38=sQuery(id+"F0.wireOp",EDGE,"E1.4.4.0");var subQ39=sQuery(id+"F0.wireOp",EDGE,"E1.4.3.0");var subQ40=sQuery(id+"F0.wireOp",EDGE,"E1.4.2.0");var subQ41=sQuery(id+"F0.wireOp",EDGE,"E1.4.1.0");var subQ42=sQuery(id+"F0.wireOp",EDGE,"E1.3.6.0");var subQ43=sQuery(id+"F0.wireOp",EDGE,"E1.3.5.0");var subQ44=sQuery(id+"F0.wireOp",EDGE,"E1.3.4.0");var subQ45=sQuery(id+"F0.wireOp",EDGE,"E1.3.3.0");var subQ46=sQuery(id+"F0.wireOp",EDGE,"E1.3.2.0");var subQ47=sQuery(id+"F0.wireOp",EDGE,"E1.3.1.0");var subQ48=sQuery(id+"F0.wireOp",EDGE,"E1.2.6.0");var subQ49=sQuery(id+"F0.wireOp",EDGE,"E1.2.5.0");var subQ50=sQuery(id+"F0.wireOp",EDGE,"E1.2.4.0");var subQ51=sQuery(id+"F0.wireOp",EDGE,"E1.2.3.0");var subQ52=sQuery(id+"F0.wireOp",EDGE,"E1.2.2.0");var subQ53=sQuery(id+"F0.wireOp",EDGE,"E1.2.1.0");var subQ54=sQuery(id+"F0.wireOp",EDGE,"E1.1.6.0");var subQ55=sQuery(id+"F0.wireOp",EDGE,"E1.1.5.0");var subQ56=sQuery(id+"F0.wireOp",EDGE,"E1.1.4.0");var subQ57=sQuery(id+"F0.wireOp",EDGE,"E1.1.3.0");var subQ58=sQuery(id+"F0.wireOp",EDGE,"E1.1.2.0");var subQ59=sQuery(id+"F0.wireOp",EDGE,"E1.1.1.0");var subQ60=sQuery(id+"F0.wireOp",EDGE,"E0.right");var subQ61=sQuery(id+"F0.wireOp",EDGE,"E0.left");var subQ62=sQuery(id+"F0.wireOp",EDGE,"E0.top");var subQ63=sQuery(id+"F0.wireOp",EDGE,"E0.bottom");Q4=makeQuery(id+"F2.opShell","OFFSET_FACE",FACE,{"disambiguationData":[OSD([subQ63,subQ62,subQ61,subQ60,subQ59,subQ58,subQ57,subQ56,subQ55,subQ54,subQ53,subQ52,subQ51,subQ50,subQ49,subQ48,subQ47,subQ46,subQ45,subQ44,subQ43,subQ42,subQ41,subQ40,subQ39,subQ38,subQ37,subQ36,subQ35,subQ34,subQ33,subQ32,subQ31,subQ30,subQ29,subQ28,subQ27,subQ26,subQ25,subQ24,subQ23,subQ22,subQ21,subQ20,subQ19,subQ18,subQ17,subQ16,subQ15,subQ14,subQ13,subQ12,subQ11,subQ10,subQ9,subQ8,subQ7,subQ6,subQ5,subQ4,subQ3,subQ2,subQ1,subQ0]),TDD([makeQuery(id+"F1.opExtrude","CAP_FACE",FACE,{"disambiguationData":[OSD([subQ63,subQ62,subQ61,subQ60,subQ59,subQ58,subQ57,subQ56,subQ55,subQ54,subQ53,subQ52,subQ51,subQ50,subQ49,subQ48,subQ47,subQ46,subQ45,subQ44,subQ43,subQ42,subQ41,subQ40,subQ39,subQ38,subQ37,subQ36,subQ35,subQ34,subQ33,subQ32,subQ31,subQ30,subQ29,subQ28,subQ27,subQ26,subQ25,subQ24,subQ23,subQ22,subQ21,subQ20,subQ19,subQ18,subQ17,subQ16,subQ15,subQ14,subQ13,subQ12,subQ11,subQ10,subQ9,subQ8,subQ7,subQ6,subQ5,subQ4,subQ3,subQ2,subQ1,subQ0])],"isStart":false})]),OD(29.0)]});}
            var Q5;
            {var subQ0=sQuery(id+"F0.wireOp",EDGE,"E2.0.10.6");var subQ1=sQuery(id+"F0.wireOp",EDGE,"E2.0.10.5");var subQ2=sQuery(id+"F0.wireOp",EDGE,"E2.0.10.4");var subQ3=sQuery(id+"F0.wireOp",EDGE,"E2.0.10.3");var subQ4=sQuery(id+"F0.wireOp",EDGE,"E2.0.10.2");var subQ5=sQuery(id+"F0.wireOp",EDGE,"E2.0.10.1");var subQ6=sQuery(id+"F0.wireOp",EDGE,"E1.9.6.0");var subQ7=sQuery(id+"F0.wireOp",EDGE,"E1.9.5.0");var subQ8=sQuery(id+"F0.wireOp",EDGE,"E1.9.4.0");var subQ9=sQuery(id+"F0.wireOp",EDGE,"E1.9.3.0");var subQ10=sQuery(id+"F0.wireOp",EDGE,"E1.9.2.0");var subQ11=sQuery(id+"F0.wireOp",EDGE,"E1.9.1.0");var subQ12=sQuery(id+"F0.wireOp",EDGE,"E1.8.6.0");var subQ13=sQuery(id+"F0.wireOp",EDGE,"E1.8.5.0");var subQ14=sQuery(id+"F0.wireOp",EDGE,"E1.8.4.0");var subQ15=sQuery(id+"F0.wireOp",EDGE,"E1.8.3.0");var subQ16=sQuery(id+"F0.wireOp",EDGE,"E1.8.2.0");var subQ17=sQuery(id+"F0.wireOp",EDGE,"E1.8.1.0");var subQ18=sQuery(id+"F0.wireOp",EDGE,"E1.7.6.0");var subQ19=sQuery(id+"F0.wireOp",EDGE,"E1.7.5.0");var subQ20=sQuery(id+"F0.wireOp",EDGE,"E1.7.4.0");var subQ21=sQuery(id+"F0.wireOp",EDGE,"E1.7.3.0");var subQ22=sQuery(id+"F0.wireOp",EDGE,"E1.7.2.0");var subQ23=sQuery(id+"F0.wireOp",EDGE,"E1.7.1.0");var subQ24=sQuery(id+"F0.wireOp",EDGE,"E1.6.6.0");var subQ25=sQuery(id+"F0.wireOp",EDGE,"E1.6.5.0");var subQ26=sQuery(id+"F0.wireOp",EDGE,"E1.6.4.0");var subQ27=sQuery(id+"F0.wireOp",EDGE,"E1.6.3.0");var subQ28=sQuery(id+"F0.wireOp",EDGE,"E1.6.2.0");var subQ29=sQuery(id+"F0.wireOp",EDGE,"E1.6.1.0");var subQ30=sQuery(id+"F0.wireOp",EDGE,"E1.5.6.0");var subQ31=sQuery(id+"F0.wireOp",EDGE,"E1.5.5.0");var subQ32=sQuery(id+"F0.wireOp",EDGE,"E1.5.4.0");var subQ33=sQuery(id+"F0.wireOp",EDGE,"E1.5.3.0");var subQ34=sQuery(id+"F0.wireOp",EDGE,"E1.5.2.0");var subQ35=sQuery(id+"F0.wireOp",EDGE,"E1.5.1.0");var subQ36=sQuery(id+"F0.wireOp",EDGE,"E1.4.6.0");var subQ37=sQuery(id+"F0.wireOp",EDGE,"E1.4.5.0");var subQ38=sQuery(id+"F0.wireOp",EDGE,"E1.4.4.0");var subQ39=sQuery(id+"F0.wireOp",EDGE,"E1.4.3.0");var subQ40=sQuery(id+"F0.wireOp",EDGE,"E1.4.2.0");var subQ41=sQuery(id+"F0.wireOp",EDGE,"E1.4.1.0");var subQ42=sQuery(id+"F0.wireOp",EDGE,"E1.3.6.0");var subQ43=sQuery(id+"F0.wireOp",EDGE,"E1.3.5.0");var subQ44=sQuery(id+"F0.wireOp",EDGE,"E1.3.4.0");var subQ45=sQuery(id+"F0.wireOp",EDGE,"E1.3.3.0");var subQ46=sQuery(id+"F0.wireOp",EDGE,"E1.3.2.0");var subQ47=sQuery(id+"F0.wireOp",EDGE,"E1.3.1.0");var subQ48=sQuery(id+"F0.wireOp",EDGE,"E1.2.6.0");var subQ49=sQuery(id+"F0.wireOp",EDGE,"E1.2.5.0");var subQ50=sQuery(id+"F0.wireOp",EDGE,"E1.2.4.0");var subQ51=sQuery(id+"F0.wireOp",EDGE,"E1.2.3.0");var subQ52=sQuery(id+"F0.wireOp",EDGE,"E1.2.2.0");var subQ53=sQuery(id+"F0.wireOp",EDGE,"E1.2.1.0");var subQ54=sQuery(id+"F0.wireOp",EDGE,"E1.1.6.0");var subQ55=sQuery(id+"F0.wireOp",EDGE,"E1.1.5.0");var subQ56=sQuery(id+"F0.wireOp",EDGE,"E1.1.4.0");var subQ57=sQuery(id+"F0.wireOp",EDGE,"E1.1.3.0");var subQ58=sQuery(id+"F0.wireOp",EDGE,"E1.1.2.0");var subQ59=sQuery(id+"F0.wireOp",EDGE,"E1.1.1.0");var subQ60=sQuery(id+"F0.wireOp",EDGE,"E0.right");var subQ61=sQuery(id+"F0.wireOp",EDGE,"E0.left");var subQ62=sQuery(id+"F0.wireOp",EDGE,"E0.top");var subQ63=sQuery(id+"F0.wireOp",EDGE,"E0.bottom");Q5=makeQuery(id+"F2.opShell","OFFSET_FACE",FACE,{"disambiguationData":[OSD([subQ63,subQ62,subQ61,subQ60,subQ59,subQ58,subQ57,subQ56,subQ55,subQ54,subQ53,subQ52,subQ51,subQ50,subQ49,subQ48,subQ47,subQ46,subQ45,subQ44,subQ43,subQ42,subQ41,subQ40,subQ39,subQ38,subQ37,subQ36,subQ35,subQ34,subQ33,subQ32,subQ31,subQ30,subQ29,subQ28,subQ27,subQ26,subQ25,subQ24,subQ23,subQ22,subQ21,subQ20,subQ19,subQ18,subQ17,subQ16,subQ15,subQ14,subQ13,subQ12,subQ11,subQ10,subQ9,subQ8,subQ7,subQ6,subQ5,subQ4,subQ3,subQ2,subQ1,subQ0]),TDD([makeQuery(id+"F1.opExtrude","CAP_FACE",FACE,{"disambiguationData":[OSD([subQ63,subQ62,subQ61,subQ60,subQ59,subQ58,subQ57,subQ56,subQ55,subQ54,subQ53,subQ52,subQ51,subQ50,subQ49,subQ48,subQ47,subQ46,subQ45,subQ44,subQ43,subQ42,subQ41,subQ40,subQ39,subQ38,subQ37,subQ36,subQ35,subQ34,subQ33,subQ32,subQ31,subQ30,subQ29,subQ28,subQ27,subQ26,subQ25,subQ24,subQ23,subQ22,subQ21,subQ20,subQ19,subQ18,subQ17,subQ16,subQ15,subQ14,subQ13,subQ12,subQ11,subQ10,subQ9,subQ8,subQ7,subQ6,subQ5,subQ4,subQ3,subQ2,subQ1,subQ0])],"isStart":false})]),OD(35.0)]});}
            var Q6;
            {var subQ0=sQuery(id+"F0.wireOp",EDGE,"E2.0.10.6");var subQ1=sQuery(id+"F0.wireOp",EDGE,"E2.0.10.5");var subQ2=sQuery(id+"F0.wireOp",EDGE,"E2.0.10.4");var subQ3=sQuery(id+"F0.wireOp",EDGE,"E2.0.10.3");var subQ4=sQuery(id+"F0.wireOp",EDGE,"E2.0.10.2");var subQ5=sQuery(id+"F0.wireOp",EDGE,"E2.0.10.1");var subQ6=sQuery(id+"F0.wireOp",EDGE,"E1.9.6.0");var subQ7=sQuery(id+"F0.wireOp",EDGE,"E1.9.5.0");var subQ8=sQuery(id+"F0.wireOp",EDGE,"E1.9.4.0");var subQ9=sQuery(id+"F0.wireOp",EDGE,"E1.9.3.0");var subQ10=sQuery(id+"F0.wireOp",EDGE,"E1.9.2.0");var subQ11=sQuery(id+"F0.wireOp",EDGE,"E1.9.1.0");var subQ12=sQuery(id+"F0.wireOp",EDGE,"E1.8.6.0");var subQ13=sQuery(id+"F0.wireOp",EDGE,"E1.8.5.0");var subQ14=sQuery(id+"F0.wireOp",EDGE,"E1.8.4.0");var subQ15=sQuery(id+"F0.wireOp",EDGE,"E1.8.3.0");var subQ16=sQuery(id+"F0.wireOp",EDGE,"E1.8.2.0");var subQ17=sQuery(id+"F0.wireOp",EDGE,"E1.8.1.0");var subQ18=sQuery(id+"F0.wireOp",EDGE,"E1.7.6.0");var subQ19=sQuery(id+"F0.wireOp",EDGE,"E1.7.5.0");var subQ20=sQuery(id+"F0.wireOp",EDGE,"E1.7.4.0");var subQ21=sQuery(id+"F0.wireOp",EDGE,"E1.7.3.0");var subQ22=sQuery(id+"F0.wireOp",EDGE,"E1.7.2.0");var subQ23=sQuery(id+"F0.wireOp",EDGE,"E1.7.1.0");var subQ24=sQuery(id+"F0.wireOp",EDGE,"E1.6.6.0");var subQ25=sQuery(id+"F0.wireOp",EDGE,"E1.6.5.0");var subQ26=sQuery(id+"F0.wireOp",EDGE,"E1.6.4.0");var subQ27=sQuery(id+"F0.wireOp",EDGE,"E1.6.3.0");var subQ28=sQuery(id+"F0.wireOp",EDGE,"E1.6.2.0");var subQ29=sQuery(id+"F0.wireOp",EDGE,"E1.6.1.0");var subQ30=sQuery(id+"F0.wireOp",EDGE,"E1.5.6.0");var subQ31=sQuery(id+"F0.wireOp",EDGE,"E1.5.5.0");var subQ32=sQuery(id+"F0.wireOp",EDGE,"E1.5.4.0");var subQ33=sQuery(id+"F0.wireOp",EDGE,"E1.5.3.0");var subQ34=sQuery(id+"F0.wireOp",EDGE,"E1.5.2.0");var subQ35=sQuery(id+"F0.wireOp",EDGE,"E1.5.1.0");var subQ36=sQuery(id+"F0.wireOp",EDGE,"E1.4.6.0");var subQ37=sQuery(id+"F0.wireOp",EDGE,"E1.4.5.0");var subQ38=sQuery(id+"F0.wireOp",EDGE,"E1.4.4.0");var subQ39=sQuery(id+"F0.wireOp",EDGE,"E1.4.3.0");var subQ40=sQuery(id+"F0.wireOp",EDGE,"E1.4.2.0");var subQ41=sQuery(id+"F0.wireOp",EDGE,"E1.4.1.0");var subQ42=sQuery(id+"F0.wireOp",EDGE,"E1.3.6.0");var subQ43=sQuery(id+"F0.wireOp",EDGE,"E1.3.5.0");var subQ44=sQuery(id+"F0.wireOp",EDGE,"E1.3.4.0");var subQ45=sQuery(id+"F0.wireOp",EDGE,"E1.3.3.0");var subQ46=sQuery(id+"F0.wireOp",EDGE,"E1.3.2.0");var subQ47=sQuery(id+"F0.wireOp",EDGE,"E1.3.1.0");var subQ48=sQuery(id+"F0.wireOp",EDGE,"E1.2.6.0");var subQ49=sQuery(id+"F0.wireOp",EDGE,"E1.2.5.0");var subQ50=sQuery(id+"F0.wireOp",EDGE,"E1.2.4.0");var subQ51=sQuery(id+"F0.wireOp",EDGE,"E1.2.3.0");var subQ52=sQuery(id+"F0.wireOp",EDGE,"E1.2.2.0");var subQ53=sQuery(id+"F0.wireOp",EDGE,"E1.2.1.0");var subQ54=sQuery(id+"F0.wireOp",EDGE,"E1.1.6.0");var subQ55=sQuery(id+"F0.wireOp",EDGE,"E1.1.5.0");var subQ56=sQuery(id+"F0.wireOp",EDGE,"E1.1.4.0");var subQ57=sQuery(id+"F0.wireOp",EDGE,"E1.1.3.0");var subQ58=sQuery(id+"F0.wireOp",EDGE,"E1.1.2.0");var subQ59=sQuery(id+"F0.wireOp",EDGE,"E1.1.1.0");var subQ60=sQuery(id+"F0.wireOp",EDGE,"E0.right");var subQ61=sQuery(id+"F0.wireOp",EDGE,"E0.left");var subQ62=sQuery(id+"F0.wireOp",EDGE,"E0.top");var subQ63=sQuery(id+"F0.wireOp",EDGE,"E0.bottom");Q6=makeQuery(id+"F2.opShell","OFFSET_FACE",FACE,{"disambiguationData":[OSD([subQ63,subQ62,subQ61,subQ60,subQ59,subQ58,subQ57,subQ56,subQ55,subQ54,subQ53,subQ52,subQ51,subQ50,subQ49,subQ48,subQ47,subQ46,subQ45,subQ44,subQ43,subQ42,subQ41,subQ40,subQ39,subQ38,subQ37,subQ36,subQ35,subQ34,subQ33,subQ32,subQ31,subQ30,subQ29,subQ28,subQ27,subQ26,subQ25,subQ24,subQ23,subQ22,subQ21,subQ20,subQ19,subQ18,subQ17,subQ16,subQ15,subQ14,subQ13,subQ12,subQ11,subQ10,subQ9,subQ8,subQ7,subQ6,subQ5,subQ4,subQ3,subQ2,subQ1,subQ0]),TDD([makeQuery(id+"F1.opExtrude","CAP_FACE",FACE,{"disambiguationData":[OSD([subQ63,subQ62,subQ61,subQ60,subQ59,subQ58,subQ57,subQ56,subQ55,subQ54,subQ53,subQ52,subQ51,subQ50,subQ49,subQ48,subQ47,subQ46,subQ45,subQ44,subQ43,subQ42,subQ41,subQ40,subQ39,subQ38,subQ37,subQ36,subQ35,subQ34,subQ33,subQ32,subQ31,subQ30,subQ29,subQ28,subQ27,subQ26,subQ25,subQ24,subQ23,subQ22,subQ21,subQ20,subQ19,subQ18,subQ17,subQ16,subQ15,subQ14,subQ13,subQ12,subQ11,subQ10,subQ9,subQ8,subQ7,subQ6,subQ5,subQ4,subQ3,subQ2,subQ1,subQ0])],"isStart":false})]),OD(41.0)]});}
            var Q7;
            {var subQ0=sQuery(id+"F0.wireOp",EDGE,"E2.0.10.6");var subQ1=sQuery(id+"F0.wireOp",EDGE,"E2.0.10.5");var subQ2=sQuery(id+"F0.wireOp",EDGE,"E2.0.10.4");var subQ3=sQuery(id+"F0.wireOp",EDGE,"E2.0.10.3");var subQ4=sQuery(id+"F0.wireOp",EDGE,"E2.0.10.2");var subQ5=sQuery(id+"F0.wireOp",EDGE,"E2.0.10.1");var subQ6=sQuery(id+"F0.wireOp",EDGE,"E1.9.6.0");var subQ7=sQuery(id+"F0.wireOp",EDGE,"E1.9.5.0");var subQ8=sQuery(id+"F0.wireOp",EDGE,"E1.9.4.0");var subQ9=sQuery(id+"F0.wireOp",EDGE,"E1.9.3.0");var subQ10=sQuery(id+"F0.wireOp",EDGE,"E1.9.2.0");var subQ11=sQuery(id+"F0.wireOp",EDGE,"E1.9.1.0");var subQ12=sQuery(id+"F0.wireOp",EDGE,"E1.8.6.0");var subQ13=sQuery(id+"F0.wireOp",EDGE,"E1.8.5.0");var subQ14=sQuery(id+"F0.wireOp",EDGE,"E1.8.4.0");var subQ15=sQuery(id+"F0.wireOp",EDGE,"E1.8.3.0");var subQ16=sQuery(id+"F0.wireOp",EDGE,"E1.8.2.0");var subQ17=sQuery(id+"F0.wireOp",EDGE,"E1.8.1.0");var subQ18=sQuery(id+"F0.wireOp",EDGE,"E1.7.6.0");var subQ19=sQuery(id+"F0.wireOp",EDGE,"E1.7.5.0");var subQ20=sQuery(id+"F0.wireOp",EDGE,"E1.7.4.0");var subQ21=sQuery(id+"F0.wireOp",EDGE,"E1.7.3.0");var subQ22=sQuery(id+"F0.wireOp",EDGE,"E1.7.2.0");var subQ23=sQuery(id+"F0.wireOp",EDGE,"E1.7.1.0");var subQ24=sQuery(id+"F0.wireOp",EDGE,"E1.6.6.0");var subQ25=sQuery(id+"F0.wireOp",EDGE,"E1.6.5.0");var subQ26=sQuery(id+"F0.wireOp",EDGE,"E1.6.4.0");var subQ27=sQuery(id+"F0.wireOp",EDGE,"E1.6.3.0");var subQ28=sQuery(id+"F0.wireOp",EDGE,"E1.6.2.0");var subQ29=sQuery(id+"F0.wireOp",EDGE,"E1.6.1.0");var subQ30=sQuery(id+"F0.wireOp",EDGE,"E1.5.6.0");var subQ31=sQuery(id+"F0.wireOp",EDGE,"E1.5.5.0");var subQ32=sQuery(id+"F0.wireOp",EDGE,"E1.5.4.0");var subQ33=sQuery(id+"F0.wireOp",EDGE,"E1.5.3.0");var subQ34=sQuery(id+"F0.wireOp",EDGE,"E1.5.2.0");var subQ35=sQuery(id+"F0.wireOp",EDGE,"E1.5.1.0");var subQ36=sQuery(id+"F0.wireOp",EDGE,"E1.4.6.0");var subQ37=sQuery(id+"F0.wireOp",EDGE,"E1.4.5.0");var subQ38=sQuery(id+"F0.wireOp",EDGE,"E1.4.4.0");var subQ39=sQuery(id+"F0.wireOp",EDGE,"E1.4.3.0");var subQ40=sQuery(id+"F0.wireOp",EDGE,"E1.4.2.0");var subQ41=sQuery(id+"F0.wireOp",EDGE,"E1.4.1.0");var subQ42=sQuery(id+"F0.wireOp",EDGE,"E1.3.6.0");var subQ43=sQuery(id+"F0.wireOp",EDGE,"E1.3.5.0");var subQ44=sQuery(id+"F0.wireOp",EDGE,"E1.3.4.0");var subQ45=sQuery(id+"F0.wireOp",EDGE,"E1.3.3.0");var subQ46=sQuery(id+"F0.wireOp",EDGE,"E1.3.2.0");var subQ47=sQuery(id+"F0.wireOp",EDGE,"E1.3.1.0");var subQ48=sQuery(id+"F0.wireOp",EDGE,"E1.2.6.0");var subQ49=sQuery(id+"F0.wireOp",EDGE,"E1.2.5.0");var subQ50=sQuery(id+"F0.wireOp",EDGE,"E1.2.4.0");var subQ51=sQuery(id+"F0.wireOp",EDGE,"E1.2.3.0");var subQ52=sQuery(id+"F0.wireOp",EDGE,"E1.2.2.0");var subQ53=sQuery(id+"F0.wireOp",EDGE,"E1.2.1.0");var subQ54=sQuery(id+"F0.wireOp",EDGE,"E1.1.6.0");var subQ55=sQuery(id+"F0.wireOp",EDGE,"E1.1.5.0");var subQ56=sQuery(id+"F0.wireOp",EDGE,"E1.1.4.0");var subQ57=sQuery(id+"F0.wireOp",EDGE,"E1.1.3.0");var subQ58=sQuery(id+"F0.wireOp",EDGE,"E1.1.2.0");var subQ59=sQuery(id+"F0.wireOp",EDGE,"E1.1.1.0");var subQ60=sQuery(id+"F0.wireOp",EDGE,"E0.right");var subQ61=sQuery(id+"F0.wireOp",EDGE,"E0.left");var subQ62=sQuery(id+"F0.wireOp",EDGE,"E0.top");var subQ63=sQuery(id+"F0.wireOp",EDGE,"E0.bottom");Q7=makeQuery(id+"F2.opShell","OFFSET_FACE",FACE,{"disambiguationData":[OSD([subQ63,subQ62,subQ61,subQ60,subQ59,subQ58,subQ57,subQ56,subQ55,subQ54,subQ53,subQ52,subQ51,subQ50,subQ49,subQ48,subQ47,subQ46,subQ45,subQ44,subQ43,subQ42,subQ41,subQ40,subQ39,subQ38,subQ37,subQ36,subQ35,subQ34,subQ33,subQ32,subQ31,subQ30,subQ29,subQ28,subQ27,subQ26,subQ25,subQ24,subQ23,subQ22,subQ21,subQ20,subQ19,subQ18,subQ17,subQ16,subQ15,subQ14,subQ13,subQ12,subQ11,subQ10,subQ9,subQ8,subQ7,subQ6,subQ5,subQ4,subQ3,subQ2,subQ1,subQ0]),TDD([makeQuery(id+"F1.opExtrude","CAP_FACE",FACE,{"disambiguationData":[OSD([subQ63,subQ62,subQ61,subQ60,subQ59,subQ58,subQ57,subQ56,subQ55,subQ54,subQ53,subQ52,subQ51,subQ50,subQ49,subQ48,subQ47,subQ46,subQ45,subQ44,subQ43,subQ42,subQ41,subQ40,subQ39,subQ38,subQ37,subQ36,subQ35,subQ34,subQ33,subQ32,subQ31,subQ30,subQ29,subQ28,subQ27,subQ26,subQ25,subQ24,subQ23,subQ22,subQ21,subQ20,subQ19,subQ18,subQ17,subQ16,subQ15,subQ14,subQ13,subQ12,subQ11,subQ10,subQ9,subQ8,subQ7,subQ6,subQ5,subQ4,subQ3,subQ2,subQ1,subQ0])],"isStart":false})]),OD(47.0)]});}
            var Q8;
            {var subQ0=sQuery(id+"F0.wireOp",EDGE,"E2.0.10.6");var subQ1=sQuery(id+"F0.wireOp",EDGE,"E2.0.10.5");var subQ2=sQuery(id+"F0.wireOp",EDGE,"E2.0.10.4");var subQ3=sQuery(id+"F0.wireOp",EDGE,"E2.0.10.3");var subQ4=sQuery(id+"F0.wireOp",EDGE,"E2.0.10.2");var subQ5=sQuery(id+"F0.wireOp",EDGE,"E2.0.10.1");var subQ6=sQuery(id+"F0.wireOp",EDGE,"E1.9.6.0");var subQ7=sQuery(id+"F0.wireOp",EDGE,"E1.9.5.0");var subQ8=sQuery(id+"F0.wireOp",EDGE,"E1.9.4.0");var subQ9=sQuery(id+"F0.wireOp",EDGE,"E1.9.3.0");var subQ10=sQuery(id+"F0.wireOp",EDGE,"E1.9.2.0");var subQ11=sQuery(id+"F0.wireOp",EDGE,"E1.9.1.0");var subQ12=sQuery(id+"F0.wireOp",EDGE,"E1.8.6.0");var subQ13=sQuery(id+"F0.wireOp",EDGE,"E1.8.5.0");var subQ14=sQuery(id+"F0.wireOp",EDGE,"E1.8.4.0");var subQ15=sQuery(id+"F0.wireOp",EDGE,"E1.8.3.0");var subQ16=sQuery(id+"F0.wireOp",EDGE,"E1.8.2.0");var subQ17=sQuery(id+"F0.wireOp",EDGE,"E1.8.1.0");var subQ18=sQuery(id+"F0.wireOp",EDGE,"E1.7.6.0");var subQ19=sQuery(id+"F0.wireOp",EDGE,"E1.7.5.0");var subQ20=sQuery(id+"F0.wireOp",EDGE,"E1.7.4.0");var subQ21=sQuery(id+"F0.wireOp",EDGE,"E1.7.3.0");var subQ22=sQuery(id+"F0.wireOp",EDGE,"E1.7.2.0");var subQ23=sQuery(id+"F0.wireOp",EDGE,"E1.7.1.0");var subQ24=sQuery(id+"F0.wireOp",EDGE,"E1.6.6.0");var subQ25=sQuery(id+"F0.wireOp",EDGE,"E1.6.5.0");var subQ26=sQuery(id+"F0.wireOp",EDGE,"E1.6.4.0");var subQ27=sQuery(id+"F0.wireOp",EDGE,"E1.6.3.0");var subQ28=sQuery(id+"F0.wireOp",EDGE,"E1.6.2.0");var subQ29=sQuery(id+"F0.wireOp",EDGE,"E1.6.1.0");var subQ30=sQuery(id+"F0.wireOp",EDGE,"E1.5.6.0");var subQ31=sQuery(id+"F0.wireOp",EDGE,"E1.5.5.0");var subQ32=sQuery(id+"F0.wireOp",EDGE,"E1.5.4.0");var subQ33=sQuery(id+"F0.wireOp",EDGE,"E1.5.3.0");var subQ34=sQuery(id+"F0.wireOp",EDGE,"E1.5.2.0");var subQ35=sQuery(id+"F0.wireOp",EDGE,"E1.5.1.0");var subQ36=sQuery(id+"F0.wireOp",EDGE,"E1.4.6.0");var subQ37=sQuery(id+"F0.wireOp",EDGE,"E1.4.5.0");var subQ38=sQuery(id+"F0.wireOp",EDGE,"E1.4.4.0");var subQ39=sQuery(id+"F0.wireOp",EDGE,"E1.4.3.0");var subQ40=sQuery(id+"F0.wireOp",EDGE,"E1.4.2.0");var subQ41=sQuery(id+"F0.wireOp",EDGE,"E1.4.1.0");var subQ42=sQuery(id+"F0.wireOp",EDGE,"E1.3.6.0");var subQ43=sQuery(id+"F0.wireOp",EDGE,"E1.3.5.0");var subQ44=sQuery(id+"F0.wireOp",EDGE,"E1.3.4.0");var subQ45=sQuery(id+"F0.wireOp",EDGE,"E1.3.3.0");var subQ46=sQuery(id+"F0.wireOp",EDGE,"E1.3.2.0");var subQ47=sQuery(id+"F0.wireOp",EDGE,"E1.3.1.0");var subQ48=sQuery(id+"F0.wireOp",EDGE,"E1.2.6.0");var subQ49=sQuery(id+"F0.wireOp",EDGE,"E1.2.5.0");var subQ50=sQuery(id+"F0.wireOp",EDGE,"E1.2.4.0");var subQ51=sQuery(id+"F0.wireOp",EDGE,"E1.2.3.0");var subQ52=sQuery(id+"F0.wireOp",EDGE,"E1.2.2.0");var subQ53=sQuery(id+"F0.wireOp",EDGE,"E1.2.1.0");var subQ54=sQuery(id+"F0.wireOp",EDGE,"E1.1.6.0");var subQ55=sQuery(id+"F0.wireOp",EDGE,"E1.1.5.0");var subQ56=sQuery(id+"F0.wireOp",EDGE,"E1.1.4.0");var subQ57=sQuery(id+"F0.wireOp",EDGE,"E1.1.3.0");var subQ58=sQuery(id+"F0.wireOp",EDGE,"E1.1.2.0");var subQ59=sQuery(id+"F0.wireOp",EDGE,"E1.1.1.0");var subQ60=sQuery(id+"F0.wireOp",EDGE,"E0.right");var subQ61=sQuery(id+"F0.wireOp",EDGE,"E0.left");var subQ62=sQuery(id+"F0.wireOp",EDGE,"E0.top");var subQ63=sQuery(id+"F0.wireOp",EDGE,"E0.bottom");Q8=makeQuery(id+"F2.opShell","OFFSET_FACE",FACE,{"disambiguationData":[OSD([subQ63,subQ62,subQ61,subQ60,subQ59,subQ58,subQ57,subQ56,subQ55,subQ54,subQ53,subQ52,subQ51,subQ50,subQ49,subQ48,subQ47,subQ46,subQ45,subQ44,subQ43,subQ42,subQ41,subQ40,subQ39,subQ38,subQ37,subQ36,subQ35,subQ34,subQ33,subQ32,subQ31,subQ30,subQ29,subQ28,subQ27,subQ26,subQ25,subQ24,subQ23,subQ22,subQ21,subQ20,subQ19,subQ18,subQ17,subQ16,subQ15,subQ14,subQ13,subQ12,subQ11,subQ10,subQ9,subQ8,subQ7,subQ6,subQ5,subQ4,subQ3,subQ2,subQ1,subQ0]),TDD([makeQuery(id+"F1.opExtrude","CAP_FACE",FACE,{"disambiguationData":[OSD([subQ63,subQ62,subQ61,subQ60,subQ59,subQ58,subQ57,subQ56,subQ55,subQ54,subQ53,subQ52,subQ51,subQ50,subQ49,subQ48,subQ47,subQ46,subQ45,subQ44,subQ43,subQ42,subQ41,subQ40,subQ39,subQ38,subQ37,subQ36,subQ35,subQ34,subQ33,subQ32,subQ31,subQ30,subQ29,subQ28,subQ27,subQ26,subQ25,subQ24,subQ23,subQ22,subQ21,subQ20,subQ19,subQ18,subQ17,subQ16,subQ15,subQ14,subQ13,subQ12,subQ11,subQ10,subQ9,subQ8,subQ7,subQ6,subQ5,subQ4,subQ3,subQ2,subQ1,subQ0])],"isStart":false})]),OD(53.0)]});}
            var Q9;
            {var subQ0=sQuery(id+"F0.wireOp",EDGE,"E2.0.10.6");var subQ1=sQuery(id+"F0.wireOp",EDGE,"E2.0.10.5");var subQ2=sQuery(id+"F0.wireOp",EDGE,"E2.0.10.4");var subQ3=sQuery(id+"F0.wireOp",EDGE,"E2.0.10.3");var subQ4=sQuery(id+"F0.wireOp",EDGE,"E2.0.10.2");var subQ5=sQuery(id+"F0.wireOp",EDGE,"E2.0.10.1");var subQ6=sQuery(id+"F0.wireOp",EDGE,"E1.9.6.0");var subQ7=sQuery(id+"F0.wireOp",EDGE,"E1.9.5.0");var subQ8=sQuery(id+"F0.wireOp",EDGE,"E1.9.4.0");var subQ9=sQuery(id+"F0.wireOp",EDGE,"E1.9.3.0");var subQ10=sQuery(id+"F0.wireOp",EDGE,"E1.9.2.0");var subQ11=sQuery(id+"F0.wireOp",EDGE,"E1.9.1.0");var subQ12=sQuery(id+"F0.wireOp",EDGE,"E1.8.6.0");var subQ13=sQuery(id+"F0.wireOp",EDGE,"E1.8.5.0");var subQ14=sQuery(id+"F0.wireOp",EDGE,"E1.8.4.0");var subQ15=sQuery(id+"F0.wireOp",EDGE,"E1.8.3.0");var subQ16=sQuery(id+"F0.wireOp",EDGE,"E1.8.2.0");var subQ17=sQuery(id+"F0.wireOp",EDGE,"E1.8.1.0");var subQ18=sQuery(id+"F0.wireOp",EDGE,"E1.7.6.0");var subQ19=sQuery(id+"F0.wireOp",EDGE,"E1.7.5.0");var subQ20=sQuery(id+"F0.wireOp",EDGE,"E1.7.4.0");var subQ21=sQuery(id+"F0.wireOp",EDGE,"E1.7.3.0");var subQ22=sQuery(id+"F0.wireOp",EDGE,"E1.7.2.0");var subQ23=sQuery(id+"F0.wireOp",EDGE,"E1.7.1.0");var subQ24=sQuery(id+"F0.wireOp",EDGE,"E1.6.6.0");var subQ25=sQuery(id+"F0.wireOp",EDGE,"E1.6.5.0");var subQ26=sQuery(id+"F0.wireOp",EDGE,"E1.6.4.0");var subQ27=sQuery(id+"F0.wireOp",EDGE,"E1.6.3.0");var subQ28=sQuery(id+"F0.wireOp",EDGE,"E1.6.2.0");var subQ29=sQuery(id+"F0.wireOp",EDGE,"E1.6.1.0");var subQ30=sQuery(id+"F0.wireOp",EDGE,"E1.5.6.0");var subQ31=sQuery(id+"F0.wireOp",EDGE,"E1.5.5.0");var subQ32=sQuery(id+"F0.wireOp",EDGE,"E1.5.4.0");var subQ33=sQuery(id+"F0.wireOp",EDGE,"E1.5.3.0");var subQ34=sQuery(id+"F0.wireOp",EDGE,"E1.5.2.0");var subQ35=sQuery(id+"F0.wireOp",EDGE,"E1.5.1.0");var subQ36=sQuery(id+"F0.wireOp",EDGE,"E1.4.6.0");var subQ37=sQuery(id+"F0.wireOp",EDGE,"E1.4.5.0");var subQ38=sQuery(id+"F0.wireOp",EDGE,"E1.4.4.0");var subQ39=sQuery(id+"F0.wireOp",EDGE,"E1.4.3.0");var subQ40=sQuery(id+"F0.wireOp",EDGE,"E1.4.2.0");var subQ41=sQuery(id+"F0.wireOp",EDGE,"E1.4.1.0");var subQ42=sQuery(id+"F0.wireOp",EDGE,"E1.3.6.0");var subQ43=sQuery(id+"F0.wireOp",EDGE,"E1.3.5.0");var subQ44=sQuery(id+"F0.wireOp",EDGE,"E1.3.4.0");var subQ45=sQuery(id+"F0.wireOp",EDGE,"E1.3.3.0");var subQ46=sQuery(id+"F0.wireOp",EDGE,"E1.3.2.0");var subQ47=sQuery(id+"F0.wireOp",EDGE,"E1.3.1.0");var subQ48=sQuery(id+"F0.wireOp",EDGE,"E1.2.6.0");var subQ49=sQuery(id+"F0.wireOp",EDGE,"E1.2.5.0");var subQ50=sQuery(id+"F0.wireOp",EDGE,"E1.2.4.0");var subQ51=sQuery(id+"F0.wireOp",EDGE,"E1.2.3.0");var subQ52=sQuery(id+"F0.wireOp",EDGE,"E1.2.2.0");var subQ53=sQuery(id+"F0.wireOp",EDGE,"E1.2.1.0");var subQ54=sQuery(id+"F0.wireOp",EDGE,"E1.1.6.0");var subQ55=sQuery(id+"F0.wireOp",EDGE,"E1.1.5.0");var subQ56=sQuery(id+"F0.wireOp",EDGE,"E1.1.4.0");var subQ57=sQuery(id+"F0.wireOp",EDGE,"E1.1.3.0");var subQ58=sQuery(id+"F0.wireOp",EDGE,"E1.1.2.0");var subQ59=sQuery(id+"F0.wireOp",EDGE,"E1.1.1.0");var subQ60=sQuery(id+"F0.wireOp",EDGE,"E0.right");var subQ61=sQuery(id+"F0.wireOp",EDGE,"E0.left");var subQ62=sQuery(id+"F0.wireOp",EDGE,"E0.top");var subQ63=sQuery(id+"F0.wireOp",EDGE,"E0.bottom");Q9=makeQuery(id+"F2.opShell","OFFSET_FACE",FACE,{"disambiguationData":[OSD([subQ63,subQ62,subQ61,subQ60,subQ59,subQ58,subQ57,subQ56,subQ55,subQ54,subQ53,subQ52,subQ51,subQ50,subQ49,subQ48,subQ47,subQ46,subQ45,subQ44,subQ43,subQ42,subQ41,subQ40,subQ39,subQ38,subQ37,subQ36,subQ35,subQ34,subQ33,subQ32,subQ31,subQ30,subQ29,subQ28,subQ27,subQ26,subQ25,subQ24,subQ23,subQ22,subQ21,subQ20,subQ19,subQ18,subQ17,subQ16,subQ15,subQ14,subQ13,subQ12,subQ11,subQ10,subQ9,subQ8,subQ7,subQ6,subQ5,subQ4,subQ3,subQ2,subQ1,subQ0]),TDD([makeQuery(id+"F1.opExtrude","CAP_FACE",FACE,{"disambiguationData":[OSD([subQ63,subQ62,subQ61,subQ60,subQ59,subQ58,subQ57,subQ56,subQ55,subQ54,subQ53,subQ52,subQ51,subQ50,subQ49,subQ48,subQ47,subQ46,subQ45,subQ44,subQ43,subQ42,subQ41,subQ40,subQ39,subQ38,subQ37,subQ36,subQ35,subQ34,subQ33,subQ32,subQ31,subQ30,subQ29,subQ28,subQ27,subQ26,subQ25,subQ24,subQ23,subQ22,subQ21,subQ20,subQ19,subQ18,subQ17,subQ16,subQ15,subQ14,subQ13,subQ12,subQ11,subQ10,subQ9,subQ8,subQ7,subQ6,subQ5,subQ4,subQ3,subQ2,subQ1,subQ0])],"isStart":false})]),OD(59.0)]});}
            var Q10;
            {var subQ0=sQuery(id+"F0.wireOp",EDGE,"E2.0.10.6");var subQ1=sQuery(id+"F0.wireOp",EDGE,"E2.0.10.5");var subQ2=sQuery(id+"F0.wireOp",EDGE,"E2.0.10.4");var subQ3=sQuery(id+"F0.wireOp",EDGE,"E2.0.10.3");var subQ4=sQuery(id+"F0.wireOp",EDGE,"E2.0.10.2");var subQ5=sQuery(id+"F0.wireOp",EDGE,"E2.0.10.1");var subQ6=sQuery(id+"F0.wireOp",EDGE,"E1.9.6.0");var subQ7=sQuery(id+"F0.wireOp",EDGE,"E1.9.5.0");var subQ8=sQuery(id+"F0.wireOp",EDGE,"E1.9.4.0");var subQ9=sQuery(id+"F0.wireOp",EDGE,"E1.9.3.0");var subQ10=sQuery(id+"F0.wireOp",EDGE,"E1.9.2.0");var subQ11=sQuery(id+"F0.wireOp",EDGE,"E1.9.1.0");var subQ12=sQuery(id+"F0.wireOp",EDGE,"E1.8.6.0");var subQ13=sQuery(id+"F0.wireOp",EDGE,"E1.8.5.0");var subQ14=sQuery(id+"F0.wireOp",EDGE,"E1.8.4.0");var subQ15=sQuery(id+"F0.wireOp",EDGE,"E1.8.3.0");var subQ16=sQuery(id+"F0.wireOp",EDGE,"E1.8.2.0");var subQ17=sQuery(id+"F0.wireOp",EDGE,"E1.8.1.0");var subQ18=sQuery(id+"F0.wireOp",EDGE,"E1.7.6.0");var subQ19=sQuery(id+"F0.wireOp",EDGE,"E1.7.5.0");var subQ20=sQuery(id+"F0.wireOp",EDGE,"E1.7.4.0");var subQ21=sQuery(id+"F0.wireOp",EDGE,"E1.7.3.0");var subQ22=sQuery(id+"F0.wireOp",EDGE,"E1.7.2.0");var subQ23=sQuery(id+"F0.wireOp",EDGE,"E1.7.1.0");var subQ24=sQuery(id+"F0.wireOp",EDGE,"E1.6.6.0");var subQ25=sQuery(id+"F0.wireOp",EDGE,"E1.6.5.0");var subQ26=sQuery(id+"F0.wireOp",EDGE,"E1.6.4.0");var subQ27=sQuery(id+"F0.wireOp",EDGE,"E1.6.3.0");var subQ28=sQuery(id+"F0.wireOp",EDGE,"E1.6.2.0");var subQ29=sQuery(id+"F0.wireOp",EDGE,"E1.6.1.0");var subQ30=sQuery(id+"F0.wireOp",EDGE,"E1.5.6.0");var subQ31=sQuery(id+"F0.wireOp",EDGE,"E1.5.5.0");var subQ32=sQuery(id+"F0.wireOp",EDGE,"E1.5.4.0");var subQ33=sQuery(id+"F0.wireOp",EDGE,"E1.5.3.0");var subQ34=sQuery(id+"F0.wireOp",EDGE,"E1.5.2.0");var subQ35=sQuery(id+"F0.wireOp",EDGE,"E1.5.1.0");var subQ36=sQuery(id+"F0.wireOp",EDGE,"E1.4.6.0");var subQ37=sQuery(id+"F0.wireOp",EDGE,"E1.4.5.0");var subQ38=sQuery(id+"F0.wireOp",EDGE,"E1.4.4.0");var subQ39=sQuery(id+"F0.wireOp",EDGE,"E1.4.3.0");var subQ40=sQuery(id+"F0.wireOp",EDGE,"E1.4.2.0");var subQ41=sQuery(id+"F0.wireOp",EDGE,"E1.4.1.0");var subQ42=sQuery(id+"F0.wireOp",EDGE,"E1.3.6.0");var subQ43=sQuery(id+"F0.wireOp",EDGE,"E1.3.5.0");var subQ44=sQuery(id+"F0.wireOp",EDGE,"E1.3.4.0");var subQ45=sQuery(id+"F0.wireOp",EDGE,"E1.3.3.0");var subQ46=sQuery(id+"F0.wireOp",EDGE,"E1.3.2.0");var subQ47=sQuery(id+"F0.wireOp",EDGE,"E1.3.1.0");var subQ48=sQuery(id+"F0.wireOp",EDGE,"E1.2.6.0");var subQ49=sQuery(id+"F0.wireOp",EDGE,"E1.2.5.0");var subQ50=sQuery(id+"F0.wireOp",EDGE,"E1.2.4.0");var subQ51=sQuery(id+"F0.wireOp",EDGE,"E1.2.3.0");var subQ52=sQuery(id+"F0.wireOp",EDGE,"E1.2.2.0");var subQ53=sQuery(id+"F0.wireOp",EDGE,"E1.2.1.0");var subQ54=sQuery(id+"F0.wireOp",EDGE,"E1.1.6.0");var subQ55=sQuery(id+"F0.wireOp",EDGE,"E1.1.5.0");var subQ56=sQuery(id+"F0.wireOp",EDGE,"E1.1.4.0");var subQ57=sQuery(id+"F0.wireOp",EDGE,"E1.1.3.0");var subQ58=sQuery(id+"F0.wireOp",EDGE,"E1.1.2.0");var subQ59=sQuery(id+"F0.wireOp",EDGE,"E1.1.1.0");var subQ60=sQuery(id+"F0.wireOp",EDGE,"E0.right");var subQ61=sQuery(id+"F0.wireOp",EDGE,"E0.left");var subQ62=sQuery(id+"F0.wireOp",EDGE,"E0.top");var subQ63=sQuery(id+"F0.wireOp",EDGE,"E0.bottom");Q10=makeQuery(id+"F2.opShell","OFFSET_FACE",FACE,{"disambiguationData":[OSD([subQ63,subQ62,subQ61,subQ60,subQ59,subQ58,subQ57,subQ56,subQ55,subQ54,subQ53,subQ52,subQ51,subQ50,subQ49,subQ48,subQ47,subQ46,subQ45,subQ44,subQ43,subQ42,subQ41,subQ40,subQ39,subQ38,subQ37,subQ36,subQ35,subQ34,subQ33,subQ32,subQ31,subQ30,subQ29,subQ28,subQ27,subQ26,subQ25,subQ24,subQ23,subQ22,subQ21,subQ20,subQ19,subQ18,subQ17,subQ16,subQ15,subQ14,subQ13,subQ12,subQ11,subQ10,subQ9,subQ8,subQ7,subQ6,subQ5,subQ4,subQ3,subQ2,subQ1,subQ0]),TDD([makeQuery(id+"F1.opExtrude","CAP_FACE",FACE,{"disambiguationData":[OSD([subQ63,subQ62,subQ61,subQ60,subQ59,subQ58,subQ57,subQ56,subQ55,subQ54,subQ53,subQ52,subQ51,subQ50,subQ49,subQ48,subQ47,subQ46,subQ45,subQ44,subQ43,subQ42,subQ41,subQ40,subQ39,subQ38,subQ37,subQ36,subQ35,subQ34,subQ33,subQ32,subQ31,subQ30,subQ29,subQ28,subQ27,subQ26,subQ25,subQ24,subQ23,subQ22,subQ21,subQ20,subQ19,subQ18,subQ17,subQ16,subQ15,subQ14,subQ13,subQ12,subQ11,subQ10,subQ9,subQ8,subQ7,subQ6,subQ5,subQ4,subQ3,subQ2,subQ1,subQ0])],"isStart":false})]),OD(58.0)]});}
            var Q11;
            {var subQ0=sQuery(id+"F0.wireOp",EDGE,"E2.0.10.6");var subQ1=sQuery(id+"F0.wireOp",EDGE,"E2.0.10.5");var subQ2=sQuery(id+"F0.wireOp",EDGE,"E2.0.10.4");var subQ3=sQuery(id+"F0.wireOp",EDGE,"E2.0.10.3");var subQ4=sQuery(id+"F0.wireOp",EDGE,"E2.0.10.2");var subQ5=sQuery(id+"F0.wireOp",EDGE,"E2.0.10.1");var subQ6=sQuery(id+"F0.wireOp",EDGE,"E1.9.6.0");var subQ7=sQuery(id+"F0.wireOp",EDGE,"E1.9.5.0");var subQ8=sQuery(id+"F0.wireOp",EDGE,"E1.9.4.0");var subQ9=sQuery(id+"F0.wireOp",EDGE,"E1.9.3.0");var subQ10=sQuery(id+"F0.wireOp",EDGE,"E1.9.2.0");var subQ11=sQuery(id+"F0.wireOp",EDGE,"E1.9.1.0");var subQ12=sQuery(id+"F0.wireOp",EDGE,"E1.8.6.0");var subQ13=sQuery(id+"F0.wireOp",EDGE,"E1.8.5.0");var subQ14=sQuery(id+"F0.wireOp",EDGE,"E1.8.4.0");var subQ15=sQuery(id+"F0.wireOp",EDGE,"E1.8.3.0");var subQ16=sQuery(id+"F0.wireOp",EDGE,"E1.8.2.0");var subQ17=sQuery(id+"F0.wireOp",EDGE,"E1.8.1.0");var subQ18=sQuery(id+"F0.wireOp",EDGE,"E1.7.6.0");var subQ19=sQuery(id+"F0.wireOp",EDGE,"E1.7.5.0");var subQ20=sQuery(id+"F0.wireOp",EDGE,"E1.7.4.0");var subQ21=sQuery(id+"F0.wireOp",EDGE,"E1.7.3.0");var subQ22=sQuery(id+"F0.wireOp",EDGE,"E1.7.2.0");var subQ23=sQuery(id+"F0.wireOp",EDGE,"E1.7.1.0");var subQ24=sQuery(id+"F0.wireOp",EDGE,"E1.6.6.0");var subQ25=sQuery(id+"F0.wireOp",EDGE,"E1.6.5.0");var subQ26=sQuery(id+"F0.wireOp",EDGE,"E1.6.4.0");var subQ27=sQuery(id+"F0.wireOp",EDGE,"E1.6.3.0");var subQ28=sQuery(id+"F0.wireOp",EDGE,"E1.6.2.0");var subQ29=sQuery(id+"F0.wireOp",EDGE,"E1.6.1.0");var subQ30=sQuery(id+"F0.wireOp",EDGE,"E1.5.6.0");var subQ31=sQuery(id+"F0.wireOp",EDGE,"E1.5.5.0");var subQ32=sQuery(id+"F0.wireOp",EDGE,"E1.5.4.0");var subQ33=sQuery(id+"F0.wireOp",EDGE,"E1.5.3.0");var subQ34=sQuery(id+"F0.wireOp",EDGE,"E1.5.2.0");var subQ35=sQuery(id+"F0.wireOp",EDGE,"E1.5.1.0");var subQ36=sQuery(id+"F0.wireOp",EDGE,"E1.4.6.0");var subQ37=sQuery(id+"F0.wireOp",EDGE,"E1.4.5.0");var subQ38=sQuery(id+"F0.wireOp",EDGE,"E1.4.4.0");var subQ39=sQuery(id+"F0.wireOp",EDGE,"E1.4.3.0");var subQ40=sQuery(id+"F0.wireOp",EDGE,"E1.4.2.0");var subQ41=sQuery(id+"F0.wireOp",EDGE,"E1.4.1.0");var subQ42=sQuery(id+"F0.wireOp",EDGE,"E1.3.6.0");var subQ43=sQuery(id+"F0.wireOp",EDGE,"E1.3.5.0");var subQ44=sQuery(id+"F0.wireOp",EDGE,"E1.3.4.0");var subQ45=sQuery(id+"F0.wireOp",EDGE,"E1.3.3.0");var subQ46=sQuery(id+"F0.wireOp",EDGE,"E1.3.2.0");var subQ47=sQuery(id+"F0.wireOp",EDGE,"E1.3.1.0");var subQ48=sQuery(id+"F0.wireOp",EDGE,"E1.2.6.0");var subQ49=sQuery(id+"F0.wireOp",EDGE,"E1.2.5.0");var subQ50=sQuery(id+"F0.wireOp",EDGE,"E1.2.4.0");var subQ51=sQuery(id+"F0.wireOp",EDGE,"E1.2.3.0");var subQ52=sQuery(id+"F0.wireOp",EDGE,"E1.2.2.0");var subQ53=sQuery(id+"F0.wireOp",EDGE,"E1.2.1.0");var subQ54=sQuery(id+"F0.wireOp",EDGE,"E1.1.6.0");var subQ55=sQuery(id+"F0.wireOp",EDGE,"E1.1.5.0");var subQ56=sQuery(id+"F0.wireOp",EDGE,"E1.1.4.0");var subQ57=sQuery(id+"F0.wireOp",EDGE,"E1.1.3.0");var subQ58=sQuery(id+"F0.wireOp",EDGE,"E1.1.2.0");var subQ59=sQuery(id+"F0.wireOp",EDGE,"E1.1.1.0");var subQ60=sQuery(id+"F0.wireOp",EDGE,"E0.right");var subQ61=sQuery(id+"F0.wireOp",EDGE,"E0.left");var subQ62=sQuery(id+"F0.wireOp",EDGE,"E0.top");var subQ63=sQuery(id+"F0.wireOp",EDGE,"E0.bottom");Q11=makeQuery(id+"F2.opShell","OFFSET_FACE",FACE,{"disambiguationData":[OSD([subQ63,subQ62,subQ61,subQ60,subQ59,subQ58,subQ57,subQ56,subQ55,subQ54,subQ53,subQ52,subQ51,subQ50,subQ49,subQ48,subQ47,subQ46,subQ45,subQ44,subQ43,subQ42,subQ41,subQ40,subQ39,subQ38,subQ37,subQ36,subQ35,subQ34,subQ33,subQ32,subQ31,subQ30,subQ29,subQ28,subQ27,subQ26,subQ25,subQ24,subQ23,subQ22,subQ21,subQ20,subQ19,subQ18,subQ17,subQ16,subQ15,subQ14,subQ13,subQ12,subQ11,subQ10,subQ9,subQ8,subQ7,subQ6,subQ5,subQ4,subQ3,subQ2,subQ1,subQ0]),TDD([makeQuery(id+"F1.opExtrude","CAP_FACE",FACE,{"disambiguationData":[OSD([subQ63,subQ62,subQ61,subQ60,subQ59,subQ58,subQ57,subQ56,subQ55,subQ54,subQ53,subQ52,subQ51,subQ50,subQ49,subQ48,subQ47,subQ46,subQ45,subQ44,subQ43,subQ42,subQ41,subQ40,subQ39,subQ38,subQ37,subQ36,subQ35,subQ34,subQ33,subQ32,subQ31,subQ30,subQ29,subQ28,subQ27,subQ26,subQ25,subQ24,subQ23,subQ22,subQ21,subQ20,subQ19,subQ18,subQ17,subQ16,subQ15,subQ14,subQ13,subQ12,subQ11,subQ10,subQ9,subQ8,subQ7,subQ6,subQ5,subQ4,subQ3,subQ2,subQ1,subQ0])],"isStart":false})]),OD(52.0)]});}
            var Q12;
            {var subQ0=sQuery(id+"F0.wireOp",EDGE,"E2.0.10.6");var subQ1=sQuery(id+"F0.wireOp",EDGE,"E2.0.10.5");var subQ2=sQuery(id+"F0.wireOp",EDGE,"E2.0.10.4");var subQ3=sQuery(id+"F0.wireOp",EDGE,"E2.0.10.3");var subQ4=sQuery(id+"F0.wireOp",EDGE,"E2.0.10.2");var subQ5=sQuery(id+"F0.wireOp",EDGE,"E2.0.10.1");var subQ6=sQuery(id+"F0.wireOp",EDGE,"E1.9.6.0");var subQ7=sQuery(id+"F0.wireOp",EDGE,"E1.9.5.0");var subQ8=sQuery(id+"F0.wireOp",EDGE,"E1.9.4.0");var subQ9=sQuery(id+"F0.wireOp",EDGE,"E1.9.3.0");var subQ10=sQuery(id+"F0.wireOp",EDGE,"E1.9.2.0");var subQ11=sQuery(id+"F0.wireOp",EDGE,"E1.9.1.0");var subQ12=sQuery(id+"F0.wireOp",EDGE,"E1.8.6.0");var subQ13=sQuery(id+"F0.wireOp",EDGE,"E1.8.5.0");var subQ14=sQuery(id+"F0.wireOp",EDGE,"E1.8.4.0");var subQ15=sQuery(id+"F0.wireOp",EDGE,"E1.8.3.0");var subQ16=sQuery(id+"F0.wireOp",EDGE,"E1.8.2.0");var subQ17=sQuery(id+"F0.wireOp",EDGE,"E1.8.1.0");var subQ18=sQuery(id+"F0.wireOp",EDGE,"E1.7.6.0");var subQ19=sQuery(id+"F0.wireOp",EDGE,"E1.7.5.0");var subQ20=sQuery(id+"F0.wireOp",EDGE,"E1.7.4.0");var subQ21=sQuery(id+"F0.wireOp",EDGE,"E1.7.3.0");var subQ22=sQuery(id+"F0.wireOp",EDGE,"E1.7.2.0");var subQ23=sQuery(id+"F0.wireOp",EDGE,"E1.7.1.0");var subQ24=sQuery(id+"F0.wireOp",EDGE,"E1.6.6.0");var subQ25=sQuery(id+"F0.wireOp",EDGE,"E1.6.5.0");var subQ26=sQuery(id+"F0.wireOp",EDGE,"E1.6.4.0");var subQ27=sQuery(id+"F0.wireOp",EDGE,"E1.6.3.0");var subQ28=sQuery(id+"F0.wireOp",EDGE,"E1.6.2.0");var subQ29=sQuery(id+"F0.wireOp",EDGE,"E1.6.1.0");var subQ30=sQuery(id+"F0.wireOp",EDGE,"E1.5.6.0");var subQ31=sQuery(id+"F0.wireOp",EDGE,"E1.5.5.0");var subQ32=sQuery(id+"F0.wireOp",EDGE,"E1.5.4.0");var subQ33=sQuery(id+"F0.wireOp",EDGE,"E1.5.3.0");var subQ34=sQuery(id+"F0.wireOp",EDGE,"E1.5.2.0");var subQ35=sQuery(id+"F0.wireOp",EDGE,"E1.5.1.0");var subQ36=sQuery(id+"F0.wireOp",EDGE,"E1.4.6.0");var subQ37=sQuery(id+"F0.wireOp",EDGE,"E1.4.5.0");var subQ38=sQuery(id+"F0.wireOp",EDGE,"E1.4.4.0");var subQ39=sQuery(id+"F0.wireOp",EDGE,"E1.4.3.0");var subQ40=sQuery(id+"F0.wireOp",EDGE,"E1.4.2.0");var subQ41=sQuery(id+"F0.wireOp",EDGE,"E1.4.1.0");var subQ42=sQuery(id+"F0.wireOp",EDGE,"E1.3.6.0");var subQ43=sQuery(id+"F0.wireOp",EDGE,"E1.3.5.0");var subQ44=sQuery(id+"F0.wireOp",EDGE,"E1.3.4.0");var subQ45=sQuery(id+"F0.wireOp",EDGE,"E1.3.3.0");var subQ46=sQuery(id+"F0.wireOp",EDGE,"E1.3.2.0");var subQ47=sQuery(id+"F0.wireOp",EDGE,"E1.3.1.0");var subQ48=sQuery(id+"F0.wireOp",EDGE,"E1.2.6.0");var subQ49=sQuery(id+"F0.wireOp",EDGE,"E1.2.5.0");var subQ50=sQuery(id+"F0.wireOp",EDGE,"E1.2.4.0");var subQ51=sQuery(id+"F0.wireOp",EDGE,"E1.2.3.0");var subQ52=sQuery(id+"F0.wireOp",EDGE,"E1.2.2.0");var subQ53=sQuery(id+"F0.wireOp",EDGE,"E1.2.1.0");var subQ54=sQuery(id+"F0.wireOp",EDGE,"E1.1.6.0");var subQ55=sQuery(id+"F0.wireOp",EDGE,"E1.1.5.0");var subQ56=sQuery(id+"F0.wireOp",EDGE,"E1.1.4.0");var subQ57=sQuery(id+"F0.wireOp",EDGE,"E1.1.3.0");var subQ58=sQuery(id+"F0.wireOp",EDGE,"E1.1.2.0");var subQ59=sQuery(id+"F0.wireOp",EDGE,"E1.1.1.0");var subQ60=sQuery(id+"F0.wireOp",EDGE,"E0.right");var subQ61=sQuery(id+"F0.wireOp",EDGE,"E0.left");var subQ62=sQuery(id+"F0.wireOp",EDGE,"E0.top");var subQ63=sQuery(id+"F0.wireOp",EDGE,"E0.bottom");Q12=makeQuery(id+"F2.opShell","OFFSET_FACE",FACE,{"disambiguationData":[OSD([subQ63,subQ62,subQ61,subQ60,subQ59,subQ58,subQ57,subQ56,subQ55,subQ54,subQ53,subQ52,subQ51,subQ50,subQ49,subQ48,subQ47,subQ46,subQ45,subQ44,subQ43,subQ42,subQ41,subQ40,subQ39,subQ38,subQ37,subQ36,subQ35,subQ34,subQ33,subQ32,subQ31,subQ30,subQ29,subQ28,subQ27,subQ26,subQ25,subQ24,subQ23,subQ22,subQ21,subQ20,subQ19,subQ18,subQ17,subQ16,subQ15,subQ14,subQ13,subQ12,subQ11,subQ10,subQ9,subQ8,subQ7,subQ6,subQ5,subQ4,subQ3,subQ2,subQ1,subQ0]),TDD([makeQuery(id+"F1.opExtrude","CAP_FACE",FACE,{"disambiguationData":[OSD([subQ63,subQ62,subQ61,subQ60,subQ59,subQ58,subQ57,subQ56,subQ55,subQ54,subQ53,subQ52,subQ51,subQ50,subQ49,subQ48,subQ47,subQ46,subQ45,subQ44,subQ43,subQ42,subQ41,subQ40,subQ39,subQ38,subQ37,subQ36,subQ35,subQ34,subQ33,subQ32,subQ31,subQ30,subQ29,subQ28,subQ27,subQ26,subQ25,subQ24,subQ23,subQ22,subQ21,subQ20,subQ19,subQ18,subQ17,subQ16,subQ15,subQ14,subQ13,subQ12,subQ11,subQ10,subQ9,subQ8,subQ7,subQ6,subQ5,subQ4,subQ3,subQ2,subQ1,subQ0])],"isStart":false})]),OD(46.0)]});}
            var Q13;
            {var subQ0=sQuery(id+"F0.wireOp",EDGE,"E2.0.10.6");var subQ1=sQuery(id+"F0.wireOp",EDGE,"E2.0.10.5");var subQ2=sQuery(id+"F0.wireOp",EDGE,"E2.0.10.4");var subQ3=sQuery(id+"F0.wireOp",EDGE,"E2.0.10.3");var subQ4=sQuery(id+"F0.wireOp",EDGE,"E2.0.10.2");var subQ5=sQuery(id+"F0.wireOp",EDGE,"E2.0.10.1");var subQ6=sQuery(id+"F0.wireOp",EDGE,"E1.9.6.0");var subQ7=sQuery(id+"F0.wireOp",EDGE,"E1.9.5.0");var subQ8=sQuery(id+"F0.wireOp",EDGE,"E1.9.4.0");var subQ9=sQuery(id+"F0.wireOp",EDGE,"E1.9.3.0");var subQ10=sQuery(id+"F0.wireOp",EDGE,"E1.9.2.0");var subQ11=sQuery(id+"F0.wireOp",EDGE,"E1.9.1.0");var subQ12=sQuery(id+"F0.wireOp",EDGE,"E1.8.6.0");var subQ13=sQuery(id+"F0.wireOp",EDGE,"E1.8.5.0");var subQ14=sQuery(id+"F0.wireOp",EDGE,"E1.8.4.0");var subQ15=sQuery(id+"F0.wireOp",EDGE,"E1.8.3.0");var subQ16=sQuery(id+"F0.wireOp",EDGE,"E1.8.2.0");var subQ17=sQuery(id+"F0.wireOp",EDGE,"E1.8.1.0");var subQ18=sQuery(id+"F0.wireOp",EDGE,"E1.7.6.0");var subQ19=sQuery(id+"F0.wireOp",EDGE,"E1.7.5.0");var subQ20=sQuery(id+"F0.wireOp",EDGE,"E1.7.4.0");var subQ21=sQuery(id+"F0.wireOp",EDGE,"E1.7.3.0");var subQ22=sQuery(id+"F0.wireOp",EDGE,"E1.7.2.0");var subQ23=sQuery(id+"F0.wireOp",EDGE,"E1.7.1.0");var subQ24=sQuery(id+"F0.wireOp",EDGE,"E1.6.6.0");var subQ25=sQuery(id+"F0.wireOp",EDGE,"E1.6.5.0");var subQ26=sQuery(id+"F0.wireOp",EDGE,"E1.6.4.0");var subQ27=sQuery(id+"F0.wireOp",EDGE,"E1.6.3.0");var subQ28=sQuery(id+"F0.wireOp",EDGE,"E1.6.2.0");var subQ29=sQuery(id+"F0.wireOp",EDGE,"E1.6.1.0");var subQ30=sQuery(id+"F0.wireOp",EDGE,"E1.5.6.0");var subQ31=sQuery(id+"F0.wireOp",EDGE,"E1.5.5.0");var subQ32=sQuery(id+"F0.wireOp",EDGE,"E1.5.4.0");var subQ33=sQuery(id+"F0.wireOp",EDGE,"E1.5.3.0");var subQ34=sQuery(id+"F0.wireOp",EDGE,"E1.5.2.0");var subQ35=sQuery(id+"F0.wireOp",EDGE,"E1.5.1.0");var subQ36=sQuery(id+"F0.wireOp",EDGE,"E1.4.6.0");var subQ37=sQuery(id+"F0.wireOp",EDGE,"E1.4.5.0");var subQ38=sQuery(id+"F0.wireOp",EDGE,"E1.4.4.0");var subQ39=sQuery(id+"F0.wireOp",EDGE,"E1.4.3.0");var subQ40=sQuery(id+"F0.wireOp",EDGE,"E1.4.2.0");var subQ41=sQuery(id+"F0.wireOp",EDGE,"E1.4.1.0");var subQ42=sQuery(id+"F0.wireOp",EDGE,"E1.3.6.0");var subQ43=sQuery(id+"F0.wireOp",EDGE,"E1.3.5.0");var subQ44=sQuery(id+"F0.wireOp",EDGE,"E1.3.4.0");var subQ45=sQuery(id+"F0.wireOp",EDGE,"E1.3.3.0");var subQ46=sQuery(id+"F0.wireOp",EDGE,"E1.3.2.0");var subQ47=sQuery(id+"F0.wireOp",EDGE,"E1.3.1.0");var subQ48=sQuery(id+"F0.wireOp",EDGE,"E1.2.6.0");var subQ49=sQuery(id+"F0.wireOp",EDGE,"E1.2.5.0");var subQ50=sQuery(id+"F0.wireOp",EDGE,"E1.2.4.0");var subQ51=sQuery(id+"F0.wireOp",EDGE,"E1.2.3.0");var subQ52=sQuery(id+"F0.wireOp",EDGE,"E1.2.2.0");var subQ53=sQuery(id+"F0.wireOp",EDGE,"E1.2.1.0");var subQ54=sQuery(id+"F0.wireOp",EDGE,"E1.1.6.0");var subQ55=sQuery(id+"F0.wireOp",EDGE,"E1.1.5.0");var subQ56=sQuery(id+"F0.wireOp",EDGE,"E1.1.4.0");var subQ57=sQuery(id+"F0.wireOp",EDGE,"E1.1.3.0");var subQ58=sQuery(id+"F0.wireOp",EDGE,"E1.1.2.0");var subQ59=sQuery(id+"F0.wireOp",EDGE,"E1.1.1.0");var subQ60=sQuery(id+"F0.wireOp",EDGE,"E0.right");var subQ61=sQuery(id+"F0.wireOp",EDGE,"E0.left");var subQ62=sQuery(id+"F0.wireOp",EDGE,"E0.top");var subQ63=sQuery(id+"F0.wireOp",EDGE,"E0.bottom");Q13=makeQuery(id+"F2.opShell","OFFSET_FACE",FACE,{"disambiguationData":[OSD([subQ63,subQ62,subQ61,subQ60,subQ59,subQ58,subQ57,subQ56,subQ55,subQ54,subQ53,subQ52,subQ51,subQ50,subQ49,subQ48,subQ47,subQ46,subQ45,subQ44,subQ43,subQ42,subQ41,subQ40,subQ39,subQ38,subQ37,subQ36,subQ35,subQ34,subQ33,subQ32,subQ31,subQ30,subQ29,subQ28,subQ27,subQ26,subQ25,subQ24,subQ23,subQ22,subQ21,subQ20,subQ19,subQ18,subQ17,subQ16,subQ15,subQ14,subQ13,subQ12,subQ11,subQ10,subQ9,subQ8,subQ7,subQ6,subQ5,subQ4,subQ3,subQ2,subQ1,subQ0]),TDD([makeQuery(id+"F1.opExtrude","CAP_FACE",FACE,{"disambiguationData":[OSD([subQ63,subQ62,subQ61,subQ60,subQ59,subQ58,subQ57,subQ56,subQ55,subQ54,subQ53,subQ52,subQ51,subQ50,subQ49,subQ48,subQ47,subQ46,subQ45,subQ44,subQ43,subQ42,subQ41,subQ40,subQ39,subQ38,subQ37,subQ36,subQ35,subQ34,subQ33,subQ32,subQ31,subQ30,subQ29,subQ28,subQ27,subQ26,subQ25,subQ24,subQ23,subQ22,subQ21,subQ20,subQ19,subQ18,subQ17,subQ16,subQ15,subQ14,subQ13,subQ12,subQ11,subQ10,subQ9,subQ8,subQ7,subQ6,subQ5,subQ4,subQ3,subQ2,subQ1,subQ0])],"isStart":false})]),OD(40.0)]});}
            var Q14;
            {var subQ0=sQuery(id+"F0.wireOp",EDGE,"E2.0.10.6");var subQ1=sQuery(id+"F0.wireOp",EDGE,"E2.0.10.5");var subQ2=sQuery(id+"F0.wireOp",EDGE,"E2.0.10.4");var subQ3=sQuery(id+"F0.wireOp",EDGE,"E2.0.10.3");var subQ4=sQuery(id+"F0.wireOp",EDGE,"E2.0.10.2");var subQ5=sQuery(id+"F0.wireOp",EDGE,"E2.0.10.1");var subQ6=sQuery(id+"F0.wireOp",EDGE,"E1.9.6.0");var subQ7=sQuery(id+"F0.wireOp",EDGE,"E1.9.5.0");var subQ8=sQuery(id+"F0.wireOp",EDGE,"E1.9.4.0");var subQ9=sQuery(id+"F0.wireOp",EDGE,"E1.9.3.0");var subQ10=sQuery(id+"F0.wireOp",EDGE,"E1.9.2.0");var subQ11=sQuery(id+"F0.wireOp",EDGE,"E1.9.1.0");var subQ12=sQuery(id+"F0.wireOp",EDGE,"E1.8.6.0");var subQ13=sQuery(id+"F0.wireOp",EDGE,"E1.8.5.0");var subQ14=sQuery(id+"F0.wireOp",EDGE,"E1.8.4.0");var subQ15=sQuery(id+"F0.wireOp",EDGE,"E1.8.3.0");var subQ16=sQuery(id+"F0.wireOp",EDGE,"E1.8.2.0");var subQ17=sQuery(id+"F0.wireOp",EDGE,"E1.8.1.0");var subQ18=sQuery(id+"F0.wireOp",EDGE,"E1.7.6.0");var subQ19=sQuery(id+"F0.wireOp",EDGE,"E1.7.5.0");var subQ20=sQuery(id+"F0.wireOp",EDGE,"E1.7.4.0");var subQ21=sQuery(id+"F0.wireOp",EDGE,"E1.7.3.0");var subQ22=sQuery(id+"F0.wireOp",EDGE,"E1.7.2.0");var subQ23=sQuery(id+"F0.wireOp",EDGE,"E1.7.1.0");var subQ24=sQuery(id+"F0.wireOp",EDGE,"E1.6.6.0");var subQ25=sQuery(id+"F0.wireOp",EDGE,"E1.6.5.0");var subQ26=sQuery(id+"F0.wireOp",EDGE,"E1.6.4.0");var subQ27=sQuery(id+"F0.wireOp",EDGE,"E1.6.3.0");var subQ28=sQuery(id+"F0.wireOp",EDGE,"E1.6.2.0");var subQ29=sQuery(id+"F0.wireOp",EDGE,"E1.6.1.0");var subQ30=sQuery(id+"F0.wireOp",EDGE,"E1.5.6.0");var subQ31=sQuery(id+"F0.wireOp",EDGE,"E1.5.5.0");var subQ32=sQuery(id+"F0.wireOp",EDGE,"E1.5.4.0");var subQ33=sQuery(id+"F0.wireOp",EDGE,"E1.5.3.0");var subQ34=sQuery(id+"F0.wireOp",EDGE,"E1.5.2.0");var subQ35=sQuery(id+"F0.wireOp",EDGE,"E1.5.1.0");var subQ36=sQuery(id+"F0.wireOp",EDGE,"E1.4.6.0");var subQ37=sQuery(id+"F0.wireOp",EDGE,"E1.4.5.0");var subQ38=sQuery(id+"F0.wireOp",EDGE,"E1.4.4.0");var subQ39=sQuery(id+"F0.wireOp",EDGE,"E1.4.3.0");var subQ40=sQuery(id+"F0.wireOp",EDGE,"E1.4.2.0");var subQ41=sQuery(id+"F0.wireOp",EDGE,"E1.4.1.0");var subQ42=sQuery(id+"F0.wireOp",EDGE,"E1.3.6.0");var subQ43=sQuery(id+"F0.wireOp",EDGE,"E1.3.5.0");var subQ44=sQuery(id+"F0.wireOp",EDGE,"E1.3.4.0");var subQ45=sQuery(id+"F0.wireOp",EDGE,"E1.3.3.0");var subQ46=sQuery(id+"F0.wireOp",EDGE,"E1.3.2.0");var subQ47=sQuery(id+"F0.wireOp",EDGE,"E1.3.1.0");var subQ48=sQuery(id+"F0.wireOp",EDGE,"E1.2.6.0");var subQ49=sQuery(id+"F0.wireOp",EDGE,"E1.2.5.0");var subQ50=sQuery(id+"F0.wireOp",EDGE,"E1.2.4.0");var subQ51=sQuery(id+"F0.wireOp",EDGE,"E1.2.3.0");var subQ52=sQuery(id+"F0.wireOp",EDGE,"E1.2.2.0");var subQ53=sQuery(id+"F0.wireOp",EDGE,"E1.2.1.0");var subQ54=sQuery(id+"F0.wireOp",EDGE,"E1.1.6.0");var subQ55=sQuery(id+"F0.wireOp",EDGE,"E1.1.5.0");var subQ56=sQuery(id+"F0.wireOp",EDGE,"E1.1.4.0");var subQ57=sQuery(id+"F0.wireOp",EDGE,"E1.1.3.0");var subQ58=sQuery(id+"F0.wireOp",EDGE,"E1.1.2.0");var subQ59=sQuery(id+"F0.wireOp",EDGE,"E1.1.1.0");var subQ60=sQuery(id+"F0.wireOp",EDGE,"E0.right");var subQ61=sQuery(id+"F0.wireOp",EDGE,"E0.left");var subQ62=sQuery(id+"F0.wireOp",EDGE,"E0.top");var subQ63=sQuery(id+"F0.wireOp",EDGE,"E0.bottom");Q14=makeQuery(id+"F2.opShell","OFFSET_FACE",FACE,{"disambiguationData":[OSD([subQ63,subQ62,subQ61,subQ60,subQ59,subQ58,subQ57,subQ56,subQ55,subQ54,subQ53,subQ52,subQ51,subQ50,subQ49,subQ48,subQ47,subQ46,subQ45,subQ44,subQ43,subQ42,subQ41,subQ40,subQ39,subQ38,subQ37,subQ36,subQ35,subQ34,subQ33,subQ32,subQ31,subQ30,subQ29,subQ28,subQ27,subQ26,subQ25,subQ24,subQ23,subQ22,subQ21,subQ20,subQ19,subQ18,subQ17,subQ16,subQ15,subQ14,subQ13,subQ12,subQ11,subQ10,subQ9,subQ8,subQ7,subQ6,subQ5,subQ4,subQ3,subQ2,subQ1,subQ0]),TDD([makeQuery(id+"F1.opExtrude","CAP_FACE",FACE,{"disambiguationData":[OSD([subQ63,subQ62,subQ61,subQ60,subQ59,subQ58,subQ57,subQ56,subQ55,subQ54,subQ53,subQ52,subQ51,subQ50,subQ49,subQ48,subQ47,subQ46,subQ45,subQ44,subQ43,subQ42,subQ41,subQ40,subQ39,subQ38,subQ37,subQ36,subQ35,subQ34,subQ33,subQ32,subQ31,subQ30,subQ29,subQ28,subQ27,subQ26,subQ25,subQ24,subQ23,subQ22,subQ21,subQ20,subQ19,subQ18,subQ17,subQ16,subQ15,subQ14,subQ13,subQ12,subQ11,subQ10,subQ9,subQ8,subQ7,subQ6,subQ5,subQ4,subQ3,subQ2,subQ1,subQ0])],"isStart":false})]),OD(34.0)]});}
            var Q15;
            {var subQ0=sQuery(id+"F0.wireOp",EDGE,"E2.0.10.6");var subQ1=sQuery(id+"F0.wireOp",EDGE,"E2.0.10.5");var subQ2=sQuery(id+"F0.wireOp",EDGE,"E2.0.10.4");var subQ3=sQuery(id+"F0.wireOp",EDGE,"E2.0.10.3");var subQ4=sQuery(id+"F0.wireOp",EDGE,"E2.0.10.2");var subQ5=sQuery(id+"F0.wireOp",EDGE,"E2.0.10.1");var subQ6=sQuery(id+"F0.wireOp",EDGE,"E1.9.6.0");var subQ7=sQuery(id+"F0.wireOp",EDGE,"E1.9.5.0");var subQ8=sQuery(id+"F0.wireOp",EDGE,"E1.9.4.0");var subQ9=sQuery(id+"F0.wireOp",EDGE,"E1.9.3.0");var subQ10=sQuery(id+"F0.wireOp",EDGE,"E1.9.2.0");var subQ11=sQuery(id+"F0.wireOp",EDGE,"E1.9.1.0");var subQ12=sQuery(id+"F0.wireOp",EDGE,"E1.8.6.0");var subQ13=sQuery(id+"F0.wireOp",EDGE,"E1.8.5.0");var subQ14=sQuery(id+"F0.wireOp",EDGE,"E1.8.4.0");var subQ15=sQuery(id+"F0.wireOp",EDGE,"E1.8.3.0");var subQ16=sQuery(id+"F0.wireOp",EDGE,"E1.8.2.0");var subQ17=sQuery(id+"F0.wireOp",EDGE,"E1.8.1.0");var subQ18=sQuery(id+"F0.wireOp",EDGE,"E1.7.6.0");var subQ19=sQuery(id+"F0.wireOp",EDGE,"E1.7.5.0");var subQ20=sQuery(id+"F0.wireOp",EDGE,"E1.7.4.0");var subQ21=sQuery(id+"F0.wireOp",EDGE,"E1.7.3.0");var subQ22=sQuery(id+"F0.wireOp",EDGE,"E1.7.2.0");var subQ23=sQuery(id+"F0.wireOp",EDGE,"E1.7.1.0");var subQ24=sQuery(id+"F0.wireOp",EDGE,"E1.6.6.0");var subQ25=sQuery(id+"F0.wireOp",EDGE,"E1.6.5.0");var subQ26=sQuery(id+"F0.wireOp",EDGE,"E1.6.4.0");var subQ27=sQuery(id+"F0.wireOp",EDGE,"E1.6.3.0");var subQ28=sQuery(id+"F0.wireOp",EDGE,"E1.6.2.0");var subQ29=sQuery(id+"F0.wireOp",EDGE,"E1.6.1.0");var subQ30=sQuery(id+"F0.wireOp",EDGE,"E1.5.6.0");var subQ31=sQuery(id+"F0.wireOp",EDGE,"E1.5.5.0");var subQ32=sQuery(id+"F0.wireOp",EDGE,"E1.5.4.0");var subQ33=sQuery(id+"F0.wireOp",EDGE,"E1.5.3.0");var subQ34=sQuery(id+"F0.wireOp",EDGE,"E1.5.2.0");var subQ35=sQuery(id+"F0.wireOp",EDGE,"E1.5.1.0");var subQ36=sQuery(id+"F0.wireOp",EDGE,"E1.4.6.0");var subQ37=sQuery(id+"F0.wireOp",EDGE,"E1.4.5.0");var subQ38=sQuery(id+"F0.wireOp",EDGE,"E1.4.4.0");var subQ39=sQuery(id+"F0.wireOp",EDGE,"E1.4.3.0");var subQ40=sQuery(id+"F0.wireOp",EDGE,"E1.4.2.0");var subQ41=sQuery(id+"F0.wireOp",EDGE,"E1.4.1.0");var subQ42=sQuery(id+"F0.wireOp",EDGE,"E1.3.6.0");var subQ43=sQuery(id+"F0.wireOp",EDGE,"E1.3.5.0");var subQ44=sQuery(id+"F0.wireOp",EDGE,"E1.3.4.0");var subQ45=sQuery(id+"F0.wireOp",EDGE,"E1.3.3.0");var subQ46=sQuery(id+"F0.wireOp",EDGE,"E1.3.2.0");var subQ47=sQuery(id+"F0.wireOp",EDGE,"E1.3.1.0");var subQ48=sQuery(id+"F0.wireOp",EDGE,"E1.2.6.0");var subQ49=sQuery(id+"F0.wireOp",EDGE,"E1.2.5.0");var subQ50=sQuery(id+"F0.wireOp",EDGE,"E1.2.4.0");var subQ51=sQuery(id+"F0.wireOp",EDGE,"E1.2.3.0");var subQ52=sQuery(id+"F0.wireOp",EDGE,"E1.2.2.0");var subQ53=sQuery(id+"F0.wireOp",EDGE,"E1.2.1.0");var subQ54=sQuery(id+"F0.wireOp",EDGE,"E1.1.6.0");var subQ55=sQuery(id+"F0.wireOp",EDGE,"E1.1.5.0");var subQ56=sQuery(id+"F0.wireOp",EDGE,"E1.1.4.0");var subQ57=sQuery(id+"F0.wireOp",EDGE,"E1.1.3.0");var subQ58=sQuery(id+"F0.wireOp",EDGE,"E1.1.2.0");var subQ59=sQuery(id+"F0.wireOp",EDGE,"E1.1.1.0");var subQ60=sQuery(id+"F0.wireOp",EDGE,"E0.right");var subQ61=sQuery(id+"F0.wireOp",EDGE,"E0.left");var subQ62=sQuery(id+"F0.wireOp",EDGE,"E0.top");var subQ63=sQuery(id+"F0.wireOp",EDGE,"E0.bottom");Q15=makeQuery(id+"F2.opShell","OFFSET_FACE",FACE,{"disambiguationData":[OSD([subQ63,subQ62,subQ61,subQ60,subQ59,subQ58,subQ57,subQ56,subQ55,subQ54,subQ53,subQ52,subQ51,subQ50,subQ49,subQ48,subQ47,subQ46,subQ45,subQ44,subQ43,subQ42,subQ41,subQ40,subQ39,subQ38,subQ37,subQ36,subQ35,subQ34,subQ33,subQ32,subQ31,subQ30,subQ29,subQ28,subQ27,subQ26,subQ25,subQ24,subQ23,subQ22,subQ21,subQ20,subQ19,subQ18,subQ17,subQ16,subQ15,subQ14,subQ13,subQ12,subQ11,subQ10,subQ9,subQ8,subQ7,subQ6,subQ5,subQ4,subQ3,subQ2,subQ1,subQ0]),TDD([makeQuery(id+"F1.opExtrude","CAP_FACE",FACE,{"disambiguationData":[OSD([subQ63,subQ62,subQ61,subQ60,subQ59,subQ58,subQ57,subQ56,subQ55,subQ54,subQ53,subQ52,subQ51,subQ50,subQ49,subQ48,subQ47,subQ46,subQ45,subQ44,subQ43,subQ42,subQ41,subQ40,subQ39,subQ38,subQ37,subQ36,subQ35,subQ34,subQ33,subQ32,subQ31,subQ30,subQ29,subQ28,subQ27,subQ26,subQ25,subQ24,subQ23,subQ22,subQ21,subQ20,subQ19,subQ18,subQ17,subQ16,subQ15,subQ14,subQ13,subQ12,subQ11,subQ10,subQ9,subQ8,subQ7,subQ6,subQ5,subQ4,subQ3,subQ2,subQ1,subQ0])],"isStart":false})]),OD(28.0)]});}
            var Q16;
            {var subQ0=sQuery(id+"F0.wireOp",EDGE,"E2.0.10.6");var subQ1=sQuery(id+"F0.wireOp",EDGE,"E2.0.10.5");var subQ2=sQuery(id+"F0.wireOp",EDGE,"E2.0.10.4");var subQ3=sQuery(id+"F0.wireOp",EDGE,"E2.0.10.3");var subQ4=sQuery(id+"F0.wireOp",EDGE,"E2.0.10.2");var subQ5=sQuery(id+"F0.wireOp",EDGE,"E2.0.10.1");var subQ6=sQuery(id+"F0.wireOp",EDGE,"E1.9.6.0");var subQ7=sQuery(id+"F0.wireOp",EDGE,"E1.9.5.0");var subQ8=sQuery(id+"F0.wireOp",EDGE,"E1.9.4.0");var subQ9=sQuery(id+"F0.wireOp",EDGE,"E1.9.3.0");var subQ10=sQuery(id+"F0.wireOp",EDGE,"E1.9.2.0");var subQ11=sQuery(id+"F0.wireOp",EDGE,"E1.9.1.0");var subQ12=sQuery(id+"F0.wireOp",EDGE,"E1.8.6.0");var subQ13=sQuery(id+"F0.wireOp",EDGE,"E1.8.5.0");var subQ14=sQuery(id+"F0.wireOp",EDGE,"E1.8.4.0");var subQ15=sQuery(id+"F0.wireOp",EDGE,"E1.8.3.0");var subQ16=sQuery(id+"F0.wireOp",EDGE,"E1.8.2.0");var subQ17=sQuery(id+"F0.wireOp",EDGE,"E1.8.1.0");var subQ18=sQuery(id+"F0.wireOp",EDGE,"E1.7.6.0");var subQ19=sQuery(id+"F0.wireOp",EDGE,"E1.7.5.0");var subQ20=sQuery(id+"F0.wireOp",EDGE,"E1.7.4.0");var subQ21=sQuery(id+"F0.wireOp",EDGE,"E1.7.3.0");var subQ22=sQuery(id+"F0.wireOp",EDGE,"E1.7.2.0");var subQ23=sQuery(id+"F0.wireOp",EDGE,"E1.7.1.0");var subQ24=sQuery(id+"F0.wireOp",EDGE,"E1.6.6.0");var subQ25=sQuery(id+"F0.wireOp",EDGE,"E1.6.5.0");var subQ26=sQuery(id+"F0.wireOp",EDGE,"E1.6.4.0");var subQ27=sQuery(id+"F0.wireOp",EDGE,"E1.6.3.0");var subQ28=sQuery(id+"F0.wireOp",EDGE,"E1.6.2.0");var subQ29=sQuery(id+"F0.wireOp",EDGE,"E1.6.1.0");var subQ30=sQuery(id+"F0.wireOp",EDGE,"E1.5.6.0");var subQ31=sQuery(id+"F0.wireOp",EDGE,"E1.5.5.0");var subQ32=sQuery(id+"F0.wireOp",EDGE,"E1.5.4.0");var subQ33=sQuery(id+"F0.wireOp",EDGE,"E1.5.3.0");var subQ34=sQuery(id+"F0.wireOp",EDGE,"E1.5.2.0");var subQ35=sQuery(id+"F0.wireOp",EDGE,"E1.5.1.0");var subQ36=sQuery(id+"F0.wireOp",EDGE,"E1.4.6.0");var subQ37=sQuery(id+"F0.wireOp",EDGE,"E1.4.5.0");var subQ38=sQuery(id+"F0.wireOp",EDGE,"E1.4.4.0");var subQ39=sQuery(id+"F0.wireOp",EDGE,"E1.4.3.0");var subQ40=sQuery(id+"F0.wireOp",EDGE,"E1.4.2.0");var subQ41=sQuery(id+"F0.wireOp",EDGE,"E1.4.1.0");var subQ42=sQuery(id+"F0.wireOp",EDGE,"E1.3.6.0");var subQ43=sQuery(id+"F0.wireOp",EDGE,"E1.3.5.0");var subQ44=sQuery(id+"F0.wireOp",EDGE,"E1.3.4.0");var subQ45=sQuery(id+"F0.wireOp",EDGE,"E1.3.3.0");var subQ46=sQuery(id+"F0.wireOp",EDGE,"E1.3.2.0");var subQ47=sQuery(id+"F0.wireOp",EDGE,"E1.3.1.0");var subQ48=sQuery(id+"F0.wireOp",EDGE,"E1.2.6.0");var subQ49=sQuery(id+"F0.wireOp",EDGE,"E1.2.5.0");var subQ50=sQuery(id+"F0.wireOp",EDGE,"E1.2.4.0");var subQ51=sQuery(id+"F0.wireOp",EDGE,"E1.2.3.0");var subQ52=sQuery(id+"F0.wireOp",EDGE,"E1.2.2.0");var subQ53=sQuery(id+"F0.wireOp",EDGE,"E1.2.1.0");var subQ54=sQuery(id+"F0.wireOp",EDGE,"E1.1.6.0");var subQ55=sQuery(id+"F0.wireOp",EDGE,"E1.1.5.0");var subQ56=sQuery(id+"F0.wireOp",EDGE,"E1.1.4.0");var subQ57=sQuery(id+"F0.wireOp",EDGE,"E1.1.3.0");var subQ58=sQuery(id+"F0.wireOp",EDGE,"E1.1.2.0");var subQ59=sQuery(id+"F0.wireOp",EDGE,"E1.1.1.0");var subQ60=sQuery(id+"F0.wireOp",EDGE,"E0.right");var subQ61=sQuery(id+"F0.wireOp",EDGE,"E0.left");var subQ62=sQuery(id+"F0.wireOp",EDGE,"E0.top");var subQ63=sQuery(id+"F0.wireOp",EDGE,"E0.bottom");Q16=makeQuery(id+"F2.opShell","OFFSET_FACE",FACE,{"disambiguationData":[OSD([subQ63,subQ62,subQ61,subQ60,subQ59,subQ58,subQ57,subQ56,subQ55,subQ54,subQ53,subQ52,subQ51,subQ50,subQ49,subQ48,subQ47,subQ46,subQ45,subQ44,subQ43,subQ42,subQ41,subQ40,subQ39,subQ38,subQ37,subQ36,subQ35,subQ34,subQ33,subQ32,subQ31,subQ30,subQ29,subQ28,subQ27,subQ26,subQ25,subQ24,subQ23,subQ22,subQ21,subQ20,subQ19,subQ18,subQ17,subQ16,subQ15,subQ14,subQ13,subQ12,subQ11,subQ10,subQ9,subQ8,subQ7,subQ6,subQ5,subQ4,subQ3,subQ2,subQ1,subQ0]),TDD([makeQuery(id+"F1.opExtrude","CAP_FACE",FACE,{"disambiguationData":[OSD([subQ63,subQ62,subQ61,subQ60,subQ59,subQ58,subQ57,subQ56,subQ55,subQ54,subQ53,subQ52,subQ51,subQ50,subQ49,subQ48,subQ47,subQ46,subQ45,subQ44,subQ43,subQ42,subQ41,subQ40,subQ39,subQ38,subQ37,subQ36,subQ35,subQ34,subQ33,subQ32,subQ31,subQ30,subQ29,subQ28,subQ27,subQ26,subQ25,subQ24,subQ23,subQ22,subQ21,subQ20,subQ19,subQ18,subQ17,subQ16,subQ15,subQ14,subQ13,subQ12,subQ11,subQ10,subQ9,subQ8,subQ7,subQ6,subQ5,subQ4,subQ3,subQ2,subQ1,subQ0])],"isStart":false})]),OD(22.0)]});}
            var Q17;
            {var subQ0=sQuery(id+"F0.wireOp",EDGE,"E2.0.10.6");var subQ1=sQuery(id+"F0.wireOp",EDGE,"E2.0.10.5");var subQ2=sQuery(id+"F0.wireOp",EDGE,"E2.0.10.4");var subQ3=sQuery(id+"F0.wireOp",EDGE,"E2.0.10.3");var subQ4=sQuery(id+"F0.wireOp",EDGE,"E2.0.10.2");var subQ5=sQuery(id+"F0.wireOp",EDGE,"E2.0.10.1");var subQ6=sQuery(id+"F0.wireOp",EDGE,"E1.9.6.0");var subQ7=sQuery(id+"F0.wireOp",EDGE,"E1.9.5.0");var subQ8=sQuery(id+"F0.wireOp",EDGE,"E1.9.4.0");var subQ9=sQuery(id+"F0.wireOp",EDGE,"E1.9.3.0");var subQ10=sQuery(id+"F0.wireOp",EDGE,"E1.9.2.0");var subQ11=sQuery(id+"F0.wireOp",EDGE,"E1.9.1.0");var subQ12=sQuery(id+"F0.wireOp",EDGE,"E1.8.6.0");var subQ13=sQuery(id+"F0.wireOp",EDGE,"E1.8.5.0");var subQ14=sQuery(id+"F0.wireOp",EDGE,"E1.8.4.0");var subQ15=sQuery(id+"F0.wireOp",EDGE,"E1.8.3.0");var subQ16=sQuery(id+"F0.wireOp",EDGE,"E1.8.2.0");var subQ17=sQuery(id+"F0.wireOp",EDGE,"E1.8.1.0");var subQ18=sQuery(id+"F0.wireOp",EDGE,"E1.7.6.0");var subQ19=sQuery(id+"F0.wireOp",EDGE,"E1.7.5.0");var subQ20=sQuery(id+"F0.wireOp",EDGE,"E1.7.4.0");var subQ21=sQuery(id+"F0.wireOp",EDGE,"E1.7.3.0");var subQ22=sQuery(id+"F0.wireOp",EDGE,"E1.7.2.0");var subQ23=sQuery(id+"F0.wireOp",EDGE,"E1.7.1.0");var subQ24=sQuery(id+"F0.wireOp",EDGE,"E1.6.6.0");var subQ25=sQuery(id+"F0.wireOp",EDGE,"E1.6.5.0");var subQ26=sQuery(id+"F0.wireOp",EDGE,"E1.6.4.0");var subQ27=sQuery(id+"F0.wireOp",EDGE,"E1.6.3.0");var subQ28=sQuery(id+"F0.wireOp",EDGE,"E1.6.2.0");var subQ29=sQuery(id+"F0.wireOp",EDGE,"E1.6.1.0");var subQ30=sQuery(id+"F0.wireOp",EDGE,"E1.5.6.0");var subQ31=sQuery(id+"F0.wireOp",EDGE,"E1.5.5.0");var subQ32=sQuery(id+"F0.wireOp",EDGE,"E1.5.4.0");var subQ33=sQuery(id+"F0.wireOp",EDGE,"E1.5.3.0");var subQ34=sQuery(id+"F0.wireOp",EDGE,"E1.5.2.0");var subQ35=sQuery(id+"F0.wireOp",EDGE,"E1.5.1.0");var subQ36=sQuery(id+"F0.wireOp",EDGE,"E1.4.6.0");var subQ37=sQuery(id+"F0.wireOp",EDGE,"E1.4.5.0");var subQ38=sQuery(id+"F0.wireOp",EDGE,"E1.4.4.0");var subQ39=sQuery(id+"F0.wireOp",EDGE,"E1.4.3.0");var subQ40=sQuery(id+"F0.wireOp",EDGE,"E1.4.2.0");var subQ41=sQuery(id+"F0.wireOp",EDGE,"E1.4.1.0");var subQ42=sQuery(id+"F0.wireOp",EDGE,"E1.3.6.0");var subQ43=sQuery(id+"F0.wireOp",EDGE,"E1.3.5.0");var subQ44=sQuery(id+"F0.wireOp",EDGE,"E1.3.4.0");var subQ45=sQuery(id+"F0.wireOp",EDGE,"E1.3.3.0");var subQ46=sQuery(id+"F0.wireOp",EDGE,"E1.3.2.0");var subQ47=sQuery(id+"F0.wireOp",EDGE,"E1.3.1.0");var subQ48=sQuery(id+"F0.wireOp",EDGE,"E1.2.6.0");var subQ49=sQuery(id+"F0.wireOp",EDGE,"E1.2.5.0");var subQ50=sQuery(id+"F0.wireOp",EDGE,"E1.2.4.0");var subQ51=sQuery(id+"F0.wireOp",EDGE,"E1.2.3.0");var subQ52=sQuery(id+"F0.wireOp",EDGE,"E1.2.2.0");var subQ53=sQuery(id+"F0.wireOp",EDGE,"E1.2.1.0");var subQ54=sQuery(id+"F0.wireOp",EDGE,"E1.1.6.0");var subQ55=sQuery(id+"F0.wireOp",EDGE,"E1.1.5.0");var subQ56=sQuery(id+"F0.wireOp",EDGE,"E1.1.4.0");var subQ57=sQuery(id+"F0.wireOp",EDGE,"E1.1.3.0");var subQ58=sQuery(id+"F0.wireOp",EDGE,"E1.1.2.0");var subQ59=sQuery(id+"F0.wireOp",EDGE,"E1.1.1.0");var subQ60=sQuery(id+"F0.wireOp",EDGE,"E0.right");var subQ61=sQuery(id+"F0.wireOp",EDGE,"E0.left");var subQ62=sQuery(id+"F0.wireOp",EDGE,"E0.top");var subQ63=sQuery(id+"F0.wireOp",EDGE,"E0.bottom");Q17=makeQuery(id+"F2.opShell","OFFSET_FACE",FACE,{"disambiguationData":[OSD([subQ63,subQ62,subQ61,subQ60,subQ59,subQ58,subQ57,subQ56,subQ55,subQ54,subQ53,subQ52,subQ51,subQ50,subQ49,subQ48,subQ47,subQ46,subQ45,subQ44,subQ43,subQ42,subQ41,subQ40,subQ39,subQ38,subQ37,subQ36,subQ35,subQ34,subQ33,subQ32,subQ31,subQ30,subQ29,subQ28,subQ27,subQ26,subQ25,subQ24,subQ23,subQ22,subQ21,subQ20,subQ19,subQ18,subQ17,subQ16,subQ15,subQ14,subQ13,subQ12,subQ11,subQ10,subQ9,subQ8,subQ7,subQ6,subQ5,subQ4,subQ3,subQ2,subQ1,subQ0]),TDD([makeQuery(id+"F1.opExtrude","CAP_FACE",FACE,{"disambiguationData":[OSD([subQ63,subQ62,subQ61,subQ60,subQ59,subQ58,subQ57,subQ56,subQ55,subQ54,subQ53,subQ52,subQ51,subQ50,subQ49,subQ48,subQ47,subQ46,subQ45,subQ44,subQ43,subQ42,subQ41,subQ40,subQ39,subQ38,subQ37,subQ36,subQ35,subQ34,subQ33,subQ32,subQ31,subQ30,subQ29,subQ28,subQ27,subQ26,subQ25,subQ24,subQ23,subQ22,subQ21,subQ20,subQ19,subQ18,subQ17,subQ16,subQ15,subQ14,subQ13,subQ12,subQ11,subQ10,subQ9,subQ8,subQ7,subQ6,subQ5,subQ4,subQ3,subQ2,subQ1,subQ0])],"isStart":false})]),OD(16.0)]});}
            var Q18;
            {var subQ0=sQuery(id+"F0.wireOp",EDGE,"E2.0.10.6");var subQ1=sQuery(id+"F0.wireOp",EDGE,"E2.0.10.5");var subQ2=sQuery(id+"F0.wireOp",EDGE,"E2.0.10.4");var subQ3=sQuery(id+"F0.wireOp",EDGE,"E2.0.10.3");var subQ4=sQuery(id+"F0.wireOp",EDGE,"E2.0.10.2");var subQ5=sQuery(id+"F0.wireOp",EDGE,"E2.0.10.1");var subQ6=sQuery(id+"F0.wireOp",EDGE,"E1.9.6.0");var subQ7=sQuery(id+"F0.wireOp",EDGE,"E1.9.5.0");var subQ8=sQuery(id+"F0.wireOp",EDGE,"E1.9.4.0");var subQ9=sQuery(id+"F0.wireOp",EDGE,"E1.9.3.0");var subQ10=sQuery(id+"F0.wireOp",EDGE,"E1.9.2.0");var subQ11=sQuery(id+"F0.wireOp",EDGE,"E1.9.1.0");var subQ12=sQuery(id+"F0.wireOp",EDGE,"E1.8.6.0");var subQ13=sQuery(id+"F0.wireOp",EDGE,"E1.8.5.0");var subQ14=sQuery(id+"F0.wireOp",EDGE,"E1.8.4.0");var subQ15=sQuery(id+"F0.wireOp",EDGE,"E1.8.3.0");var subQ16=sQuery(id+"F0.wireOp",EDGE,"E1.8.2.0");var subQ17=sQuery(id+"F0.wireOp",EDGE,"E1.8.1.0");var subQ18=sQuery(id+"F0.wireOp",EDGE,"E1.7.6.0");var subQ19=sQuery(id+"F0.wireOp",EDGE,"E1.7.5.0");var subQ20=sQuery(id+"F0.wireOp",EDGE,"E1.7.4.0");var subQ21=sQuery(id+"F0.wireOp",EDGE,"E1.7.3.0");var subQ22=sQuery(id+"F0.wireOp",EDGE,"E1.7.2.0");var subQ23=sQuery(id+"F0.wireOp",EDGE,"E1.7.1.0");var subQ24=sQuery(id+"F0.wireOp",EDGE,"E1.6.6.0");var subQ25=sQuery(id+"F0.wireOp",EDGE,"E1.6.5.0");var subQ26=sQuery(id+"F0.wireOp",EDGE,"E1.6.4.0");var subQ27=sQuery(id+"F0.wireOp",EDGE,"E1.6.3.0");var subQ28=sQuery(id+"F0.wireOp",EDGE,"E1.6.2.0");var subQ29=sQuery(id+"F0.wireOp",EDGE,"E1.6.1.0");var subQ30=sQuery(id+"F0.wireOp",EDGE,"E1.5.6.0");var subQ31=sQuery(id+"F0.wireOp",EDGE,"E1.5.5.0");var subQ32=sQuery(id+"F0.wireOp",EDGE,"E1.5.4.0");var subQ33=sQuery(id+"F0.wireOp",EDGE,"E1.5.3.0");var subQ34=sQuery(id+"F0.wireOp",EDGE,"E1.5.2.0");var subQ35=sQuery(id+"F0.wireOp",EDGE,"E1.5.1.0");var subQ36=sQuery(id+"F0.wireOp",EDGE,"E1.4.6.0");var subQ37=sQuery(id+"F0.wireOp",EDGE,"E1.4.5.0");var subQ38=sQuery(id+"F0.wireOp",EDGE,"E1.4.4.0");var subQ39=sQuery(id+"F0.wireOp",EDGE,"E1.4.3.0");var subQ40=sQuery(id+"F0.wireOp",EDGE,"E1.4.2.0");var subQ41=sQuery(id+"F0.wireOp",EDGE,"E1.4.1.0");var subQ42=sQuery(id+"F0.wireOp",EDGE,"E1.3.6.0");var subQ43=sQuery(id+"F0.wireOp",EDGE,"E1.3.5.0");var subQ44=sQuery(id+"F0.wireOp",EDGE,"E1.3.4.0");var subQ45=sQuery(id+"F0.wireOp",EDGE,"E1.3.3.0");var subQ46=sQuery(id+"F0.wireOp",EDGE,"E1.3.2.0");var subQ47=sQuery(id+"F0.wireOp",EDGE,"E1.3.1.0");var subQ48=sQuery(id+"F0.wireOp",EDGE,"E1.2.6.0");var subQ49=sQuery(id+"F0.wireOp",EDGE,"E1.2.5.0");var subQ50=sQuery(id+"F0.wireOp",EDGE,"E1.2.4.0");var subQ51=sQuery(id+"F0.wireOp",EDGE,"E1.2.3.0");var subQ52=sQuery(id+"F0.wireOp",EDGE,"E1.2.2.0");var subQ53=sQuery(id+"F0.wireOp",EDGE,"E1.2.1.0");var subQ54=sQuery(id+"F0.wireOp",EDGE,"E1.1.6.0");var subQ55=sQuery(id+"F0.wireOp",EDGE,"E1.1.5.0");var subQ56=sQuery(id+"F0.wireOp",EDGE,"E1.1.4.0");var subQ57=sQuery(id+"F0.wireOp",EDGE,"E1.1.3.0");var subQ58=sQuery(id+"F0.wireOp",EDGE,"E1.1.2.0");var subQ59=sQuery(id+"F0.wireOp",EDGE,"E1.1.1.0");var subQ60=sQuery(id+"F0.wireOp",EDGE,"E0.right");var subQ61=sQuery(id+"F0.wireOp",EDGE,"E0.left");var subQ62=sQuery(id+"F0.wireOp",EDGE,"E0.top");var subQ63=sQuery(id+"F0.wireOp",EDGE,"E0.bottom");Q18=makeQuery(id+"F2.opShell","OFFSET_FACE",FACE,{"disambiguationData":[OSD([subQ63,subQ62,subQ61,subQ60,subQ59,subQ58,subQ57,subQ56,subQ55,subQ54,subQ53,subQ52,subQ51,subQ50,subQ49,subQ48,subQ47,subQ46,subQ45,subQ44,subQ43,subQ42,subQ41,subQ40,subQ39,subQ38,subQ37,subQ36,subQ35,subQ34,subQ33,subQ32,subQ31,subQ30,subQ29,subQ28,subQ27,subQ26,subQ25,subQ24,subQ23,subQ22,subQ21,subQ20,subQ19,subQ18,subQ17,subQ16,subQ15,subQ14,subQ13,subQ12,subQ11,subQ10,subQ9,subQ8,subQ7,subQ6,subQ5,subQ4,subQ3,subQ2,subQ1,subQ0]),TDD([makeQuery(id+"F1.opExtrude","CAP_FACE",FACE,{"disambiguationData":[OSD([subQ63,subQ62,subQ61,subQ60,subQ59,subQ58,subQ57,subQ56,subQ55,subQ54,subQ53,subQ52,subQ51,subQ50,subQ49,subQ48,subQ47,subQ46,subQ45,subQ44,subQ43,subQ42,subQ41,subQ40,subQ39,subQ38,subQ37,subQ36,subQ35,subQ34,subQ33,subQ32,subQ31,subQ30,subQ29,subQ28,subQ27,subQ26,subQ25,subQ24,subQ23,subQ22,subQ21,subQ20,subQ19,subQ18,subQ17,subQ16,subQ15,subQ14,subQ13,subQ12,subQ11,subQ10,subQ9,subQ8,subQ7,subQ6,subQ5,subQ4,subQ3,subQ2,subQ1,subQ0])],"isStart":false})]),OD(10.0)]});}
            var Q19;
            {var subQ0=sQuery(id+"F0.wireOp",EDGE,"E2.0.10.6");var subQ1=sQuery(id+"F0.wireOp",EDGE,"E2.0.10.5");var subQ2=sQuery(id+"F0.wireOp",EDGE,"E2.0.10.4");var subQ3=sQuery(id+"F0.wireOp",EDGE,"E2.0.10.3");var subQ4=sQuery(id+"F0.wireOp",EDGE,"E2.0.10.2");var subQ5=sQuery(id+"F0.wireOp",EDGE,"E2.0.10.1");var subQ6=sQuery(id+"F0.wireOp",EDGE,"E1.9.6.0");var subQ7=sQuery(id+"F0.wireOp",EDGE,"E1.9.5.0");var subQ8=sQuery(id+"F0.wireOp",EDGE,"E1.9.4.0");var subQ9=sQuery(id+"F0.wireOp",EDGE,"E1.9.3.0");var subQ10=sQuery(id+"F0.wireOp",EDGE,"E1.9.2.0");var subQ11=sQuery(id+"F0.wireOp",EDGE,"E1.9.1.0");var subQ12=sQuery(id+"F0.wireOp",EDGE,"E1.8.6.0");var subQ13=sQuery(id+"F0.wireOp",EDGE,"E1.8.5.0");var subQ14=sQuery(id+"F0.wireOp",EDGE,"E1.8.4.0");var subQ15=sQuery(id+"F0.wireOp",EDGE,"E1.8.3.0");var subQ16=sQuery(id+"F0.wireOp",EDGE,"E1.8.2.0");var subQ17=sQuery(id+"F0.wireOp",EDGE,"E1.8.1.0");var subQ18=sQuery(id+"F0.wireOp",EDGE,"E1.7.6.0");var subQ19=sQuery(id+"F0.wireOp",EDGE,"E1.7.5.0");var subQ20=sQuery(id+"F0.wireOp",EDGE,"E1.7.4.0");var subQ21=sQuery(id+"F0.wireOp",EDGE,"E1.7.3.0");var subQ22=sQuery(id+"F0.wireOp",EDGE,"E1.7.2.0");var subQ23=sQuery(id+"F0.wireOp",EDGE,"E1.7.1.0");var subQ24=sQuery(id+"F0.wireOp",EDGE,"E1.6.6.0");var subQ25=sQuery(id+"F0.wireOp",EDGE,"E1.6.5.0");var subQ26=sQuery(id+"F0.wireOp",EDGE,"E1.6.4.0");var subQ27=sQuery(id+"F0.wireOp",EDGE,"E1.6.3.0");var subQ28=sQuery(id+"F0.wireOp",EDGE,"E1.6.2.0");var subQ29=sQuery(id+"F0.wireOp",EDGE,"E1.6.1.0");var subQ30=sQuery(id+"F0.wireOp",EDGE,"E1.5.6.0");var subQ31=sQuery(id+"F0.wireOp",EDGE,"E1.5.5.0");var subQ32=sQuery(id+"F0.wireOp",EDGE,"E1.5.4.0");var subQ33=sQuery(id+"F0.wireOp",EDGE,"E1.5.3.0");var subQ34=sQuery(id+"F0.wireOp",EDGE,"E1.5.2.0");var subQ35=sQuery(id+"F0.wireOp",EDGE,"E1.5.1.0");var subQ36=sQuery(id+"F0.wireOp",EDGE,"E1.4.6.0");var subQ37=sQuery(id+"F0.wireOp",EDGE,"E1.4.5.0");var subQ38=sQuery(id+"F0.wireOp",EDGE,"E1.4.4.0");var subQ39=sQuery(id+"F0.wireOp",EDGE,"E1.4.3.0");var subQ40=sQuery(id+"F0.wireOp",EDGE,"E1.4.2.0");var subQ41=sQuery(id+"F0.wireOp",EDGE,"E1.4.1.0");var subQ42=sQuery(id+"F0.wireOp",EDGE,"E1.3.6.0");var subQ43=sQuery(id+"F0.wireOp",EDGE,"E1.3.5.0");var subQ44=sQuery(id+"F0.wireOp",EDGE,"E1.3.4.0");var subQ45=sQuery(id+"F0.wireOp",EDGE,"E1.3.3.0");var subQ46=sQuery(id+"F0.wireOp",EDGE,"E1.3.2.0");var subQ47=sQuery(id+"F0.wireOp",EDGE,"E1.3.1.0");var subQ48=sQuery(id+"F0.wireOp",EDGE,"E1.2.6.0");var subQ49=sQuery(id+"F0.wireOp",EDGE,"E1.2.5.0");var subQ50=sQuery(id+"F0.wireOp",EDGE,"E1.2.4.0");var subQ51=sQuery(id+"F0.wireOp",EDGE,"E1.2.3.0");var subQ52=sQuery(id+"F0.wireOp",EDGE,"E1.2.2.0");var subQ53=sQuery(id+"F0.wireOp",EDGE,"E1.2.1.0");var subQ54=sQuery(id+"F0.wireOp",EDGE,"E1.1.6.0");var subQ55=sQuery(id+"F0.wireOp",EDGE,"E1.1.5.0");var subQ56=sQuery(id+"F0.wireOp",EDGE,"E1.1.4.0");var subQ57=sQuery(id+"F0.wireOp",EDGE,"E1.1.3.0");var subQ58=sQuery(id+"F0.wireOp",EDGE,"E1.1.2.0");var subQ59=sQuery(id+"F0.wireOp",EDGE,"E1.1.1.0");var subQ60=sQuery(id+"F0.wireOp",EDGE,"E0.right");var subQ61=sQuery(id+"F0.wireOp",EDGE,"E0.left");var subQ62=sQuery(id+"F0.wireOp",EDGE,"E0.top");var subQ63=sQuery(id+"F0.wireOp",EDGE,"E0.bottom");Q19=makeQuery(id+"F2.opShell","OFFSET_FACE",FACE,{"disambiguationData":[OSD([subQ63,subQ62,subQ61,subQ60,subQ59,subQ58,subQ57,subQ56,subQ55,subQ54,subQ53,subQ52,subQ51,subQ50,subQ49,subQ48,subQ47,subQ46,subQ45,subQ44,subQ43,subQ42,subQ41,subQ40,subQ39,subQ38,subQ37,subQ36,subQ35,subQ34,subQ33,subQ32,subQ31,subQ30,subQ29,subQ28,subQ27,subQ26,subQ25,subQ24,subQ23,subQ22,subQ21,subQ20,subQ19,subQ18,subQ17,subQ16,subQ15,subQ14,subQ13,subQ12,subQ11,subQ10,subQ9,subQ8,subQ7,subQ6,subQ5,subQ4,subQ3,subQ2,subQ1,subQ0]),TDD([makeQuery(id+"F1.opExtrude","CAP_FACE",FACE,{"disambiguationData":[OSD([subQ63,subQ62,subQ61,subQ60,subQ59,subQ58,subQ57,subQ56,subQ55,subQ54,subQ53,subQ52,subQ51,subQ50,subQ49,subQ48,subQ47,subQ46,subQ45,subQ44,subQ43,subQ42,subQ41,subQ40,subQ39,subQ38,subQ37,subQ36,subQ35,subQ34,subQ33,subQ32,subQ31,subQ30,subQ29,subQ28,subQ27,subQ26,subQ25,subQ24,subQ23,subQ22,subQ21,subQ20,subQ19,subQ18,subQ17,subQ16,subQ15,subQ14,subQ13,subQ12,subQ11,subQ10,subQ9,subQ8,subQ7,subQ6,subQ5,subQ4,subQ3,subQ2,subQ1,subQ0])],"isStart":false})]),OD(4.0)]});}
            var Q20;
            {var subQ0=sQuery(id+"F0.wireOp",EDGE,"E2.0.10.6");var subQ1=sQuery(id+"F0.wireOp",EDGE,"E2.0.10.5");var subQ2=sQuery(id+"F0.wireOp",EDGE,"E2.0.10.4");var subQ3=sQuery(id+"F0.wireOp",EDGE,"E2.0.10.3");var subQ4=sQuery(id+"F0.wireOp",EDGE,"E2.0.10.2");var subQ5=sQuery(id+"F0.wireOp",EDGE,"E2.0.10.1");var subQ6=sQuery(id+"F0.wireOp",EDGE,"E1.9.6.0");var subQ7=sQuery(id+"F0.wireOp",EDGE,"E1.9.5.0");var subQ8=sQuery(id+"F0.wireOp",EDGE,"E1.9.4.0");var subQ9=sQuery(id+"F0.wireOp",EDGE,"E1.9.3.0");var subQ10=sQuery(id+"F0.wireOp",EDGE,"E1.9.2.0");var subQ11=sQuery(id+"F0.wireOp",EDGE,"E1.9.1.0");var subQ12=sQuery(id+"F0.wireOp",EDGE,"E1.8.6.0");var subQ13=sQuery(id+"F0.wireOp",EDGE,"E1.8.5.0");var subQ14=sQuery(id+"F0.wireOp",EDGE,"E1.8.4.0");var subQ15=sQuery(id+"F0.wireOp",EDGE,"E1.8.3.0");var subQ16=sQuery(id+"F0.wireOp",EDGE,"E1.8.2.0");var subQ17=sQuery(id+"F0.wireOp",EDGE,"E1.8.1.0");var subQ18=sQuery(id+"F0.wireOp",EDGE,"E1.7.6.0");var subQ19=sQuery(id+"F0.wireOp",EDGE,"E1.7.5.0");var subQ20=sQuery(id+"F0.wireOp",EDGE,"E1.7.4.0");var subQ21=sQuery(id+"F0.wireOp",EDGE,"E1.7.3.0");var subQ22=sQuery(id+"F0.wireOp",EDGE,"E1.7.2.0");var subQ23=sQuery(id+"F0.wireOp",EDGE,"E1.7.1.0");var subQ24=sQuery(id+"F0.wireOp",EDGE,"E1.6.6.0");var subQ25=sQuery(id+"F0.wireOp",EDGE,"E1.6.5.0");var subQ26=sQuery(id+"F0.wireOp",EDGE,"E1.6.4.0");var subQ27=sQuery(id+"F0.wireOp",EDGE,"E1.6.3.0");var subQ28=sQuery(id+"F0.wireOp",EDGE,"E1.6.2.0");var subQ29=sQuery(id+"F0.wireOp",EDGE,"E1.6.1.0");var subQ30=sQuery(id+"F0.wireOp",EDGE,"E1.5.6.0");var subQ31=sQuery(id+"F0.wireOp",EDGE,"E1.5.5.0");var subQ32=sQuery(id+"F0.wireOp",EDGE,"E1.5.4.0");var subQ33=sQuery(id+"F0.wireOp",EDGE,"E1.5.3.0");var subQ34=sQuery(id+"F0.wireOp",EDGE,"E1.5.2.0");var subQ35=sQuery(id+"F0.wireOp",EDGE,"E1.5.1.0");var subQ36=sQuery(id+"F0.wireOp",EDGE,"E1.4.6.0");var subQ37=sQuery(id+"F0.wireOp",EDGE,"E1.4.5.0");var subQ38=sQuery(id+"F0.wireOp",EDGE,"E1.4.4.0");var subQ39=sQuery(id+"F0.wireOp",EDGE,"E1.4.3.0");var subQ40=sQuery(id+"F0.wireOp",EDGE,"E1.4.2.0");var subQ41=sQuery(id+"F0.wireOp",EDGE,"E1.4.1.0");var subQ42=sQuery(id+"F0.wireOp",EDGE,"E1.3.6.0");var subQ43=sQuery(id+"F0.wireOp",EDGE,"E1.3.5.0");var subQ44=sQuery(id+"F0.wireOp",EDGE,"E1.3.4.0");var subQ45=sQuery(id+"F0.wireOp",EDGE,"E1.3.3.0");var subQ46=sQuery(id+"F0.wireOp",EDGE,"E1.3.2.0");var subQ47=sQuery(id+"F0.wireOp",EDGE,"E1.3.1.0");var subQ48=sQuery(id+"F0.wireOp",EDGE,"E1.2.6.0");var subQ49=sQuery(id+"F0.wireOp",EDGE,"E1.2.5.0");var subQ50=sQuery(id+"F0.wireOp",EDGE,"E1.2.4.0");var subQ51=sQuery(id+"F0.wireOp",EDGE,"E1.2.3.0");var subQ52=sQuery(id+"F0.wireOp",EDGE,"E1.2.2.0");var subQ53=sQuery(id+"F0.wireOp",EDGE,"E1.2.1.0");var subQ54=sQuery(id+"F0.wireOp",EDGE,"E1.1.6.0");var subQ55=sQuery(id+"F0.wireOp",EDGE,"E1.1.5.0");var subQ56=sQuery(id+"F0.wireOp",EDGE,"E1.1.4.0");var subQ57=sQuery(id+"F0.wireOp",EDGE,"E1.1.3.0");var subQ58=sQuery(id+"F0.wireOp",EDGE,"E1.1.2.0");var subQ59=sQuery(id+"F0.wireOp",EDGE,"E1.1.1.0");var subQ60=sQuery(id+"F0.wireOp",EDGE,"E0.right");var subQ61=sQuery(id+"F0.wireOp",EDGE,"E0.left");var subQ62=sQuery(id+"F0.wireOp",EDGE,"E0.top");var subQ63=sQuery(id+"F0.wireOp",EDGE,"E0.bottom");Q20=makeQuery(id+"F2.opShell","OFFSET_FACE",FACE,{"disambiguationData":[OSD([subQ63,subQ62,subQ61,subQ60,subQ59,subQ58,subQ57,subQ56,subQ55,subQ54,subQ53,subQ52,subQ51,subQ50,subQ49,subQ48,subQ47,subQ46,subQ45,subQ44,subQ43,subQ42,subQ41,subQ40,subQ39,subQ38,subQ37,subQ36,subQ35,subQ34,subQ33,subQ32,subQ31,subQ30,subQ29,subQ28,subQ27,subQ26,subQ25,subQ24,subQ23,subQ22,subQ21,subQ20,subQ19,subQ18,subQ17,subQ16,subQ15,subQ14,subQ13,subQ12,subQ11,subQ10,subQ9,subQ8,subQ7,subQ6,subQ5,subQ4,subQ3,subQ2,subQ1,subQ0]),TDD([makeQuery(id+"F1.opExtrude","CAP_FACE",FACE,{"disambiguationData":[OSD([subQ63,subQ62,subQ61,subQ60,subQ59,subQ58,subQ57,subQ56,subQ55,subQ54,subQ53,subQ52,subQ51,subQ50,subQ49,subQ48,subQ47,subQ46,subQ45,subQ44,subQ43,subQ42,subQ41,subQ40,subQ39,subQ38,subQ37,subQ36,subQ35,subQ34,subQ33,subQ32,subQ31,subQ30,subQ29,subQ28,subQ27,subQ26,subQ25,subQ24,subQ23,subQ22,subQ21,subQ20,subQ19,subQ18,subQ17,subQ16,subQ15,subQ14,subQ13,subQ12,subQ11,subQ10,subQ9,subQ8,subQ7,subQ6,subQ5,subQ4,subQ3,subQ2,subQ1,subQ0])],"isStart":false})]),OD(3.0)]});}
            var Q21;
            {var subQ0=sQuery(id+"F0.wireOp",EDGE,"E2.0.10.6");var subQ1=sQuery(id+"F0.wireOp",EDGE,"E2.0.10.5");var subQ2=sQuery(id+"F0.wireOp",EDGE,"E2.0.10.4");var subQ3=sQuery(id+"F0.wireOp",EDGE,"E2.0.10.3");var subQ4=sQuery(id+"F0.wireOp",EDGE,"E2.0.10.2");var subQ5=sQuery(id+"F0.wireOp",EDGE,"E2.0.10.1");var subQ6=sQuery(id+"F0.wireOp",EDGE,"E1.9.6.0");var subQ7=sQuery(id+"F0.wireOp",EDGE,"E1.9.5.0");var subQ8=sQuery(id+"F0.wireOp",EDGE,"E1.9.4.0");var subQ9=sQuery(id+"F0.wireOp",EDGE,"E1.9.3.0");var subQ10=sQuery(id+"F0.wireOp",EDGE,"E1.9.2.0");var subQ11=sQuery(id+"F0.wireOp",EDGE,"E1.9.1.0");var subQ12=sQuery(id+"F0.wireOp",EDGE,"E1.8.6.0");var subQ13=sQuery(id+"F0.wireOp",EDGE,"E1.8.5.0");var subQ14=sQuery(id+"F0.wireOp",EDGE,"E1.8.4.0");var subQ15=sQuery(id+"F0.wireOp",EDGE,"E1.8.3.0");var subQ16=sQuery(id+"F0.wireOp",EDGE,"E1.8.2.0");var subQ17=sQuery(id+"F0.wireOp",EDGE,"E1.8.1.0");var subQ18=sQuery(id+"F0.wireOp",EDGE,"E1.7.6.0");var subQ19=sQuery(id+"F0.wireOp",EDGE,"E1.7.5.0");var subQ20=sQuery(id+"F0.wireOp",EDGE,"E1.7.4.0");var subQ21=sQuery(id+"F0.wireOp",EDGE,"E1.7.3.0");var subQ22=sQuery(id+"F0.wireOp",EDGE,"E1.7.2.0");var subQ23=sQuery(id+"F0.wireOp",EDGE,"E1.7.1.0");var subQ24=sQuery(id+"F0.wireOp",EDGE,"E1.6.6.0");var subQ25=sQuery(id+"F0.wireOp",EDGE,"E1.6.5.0");var subQ26=sQuery(id+"F0.wireOp",EDGE,"E1.6.4.0");var subQ27=sQuery(id+"F0.wireOp",EDGE,"E1.6.3.0");var subQ28=sQuery(id+"F0.wireOp",EDGE,"E1.6.2.0");var subQ29=sQuery(id+"F0.wireOp",EDGE,"E1.6.1.0");var subQ30=sQuery(id+"F0.wireOp",EDGE,"E1.5.6.0");var subQ31=sQuery(id+"F0.wireOp",EDGE,"E1.5.5.0");var subQ32=sQuery(id+"F0.wireOp",EDGE,"E1.5.4.0");var subQ33=sQuery(id+"F0.wireOp",EDGE,"E1.5.3.0");var subQ34=sQuery(id+"F0.wireOp",EDGE,"E1.5.2.0");var subQ35=sQuery(id+"F0.wireOp",EDGE,"E1.5.1.0");var subQ36=sQuery(id+"F0.wireOp",EDGE,"E1.4.6.0");var subQ37=sQuery(id+"F0.wireOp",EDGE,"E1.4.5.0");var subQ38=sQuery(id+"F0.wireOp",EDGE,"E1.4.4.0");var subQ39=sQuery(id+"F0.wireOp",EDGE,"E1.4.3.0");var subQ40=sQuery(id+"F0.wireOp",EDGE,"E1.4.2.0");var subQ41=sQuery(id+"F0.wireOp",EDGE,"E1.4.1.0");var subQ42=sQuery(id+"F0.wireOp",EDGE,"E1.3.6.0");var subQ43=sQuery(id+"F0.wireOp",EDGE,"E1.3.5.0");var subQ44=sQuery(id+"F0.wireOp",EDGE,"E1.3.4.0");var subQ45=sQuery(id+"F0.wireOp",EDGE,"E1.3.3.0");var subQ46=sQuery(id+"F0.wireOp",EDGE,"E1.3.2.0");var subQ47=sQuery(id+"F0.wireOp",EDGE,"E1.3.1.0");var subQ48=sQuery(id+"F0.wireOp",EDGE,"E1.2.6.0");var subQ49=sQuery(id+"F0.wireOp",EDGE,"E1.2.5.0");var subQ50=sQuery(id+"F0.wireOp",EDGE,"E1.2.4.0");var subQ51=sQuery(id+"F0.wireOp",EDGE,"E1.2.3.0");var subQ52=sQuery(id+"F0.wireOp",EDGE,"E1.2.2.0");var subQ53=sQuery(id+"F0.wireOp",EDGE,"E1.2.1.0");var subQ54=sQuery(id+"F0.wireOp",EDGE,"E1.1.6.0");var subQ55=sQuery(id+"F0.wireOp",EDGE,"E1.1.5.0");var subQ56=sQuery(id+"F0.wireOp",EDGE,"E1.1.4.0");var subQ57=sQuery(id+"F0.wireOp",EDGE,"E1.1.3.0");var subQ58=sQuery(id+"F0.wireOp",EDGE,"E1.1.2.0");var subQ59=sQuery(id+"F0.wireOp",EDGE,"E1.1.1.0");var subQ60=sQuery(id+"F0.wireOp",EDGE,"E0.right");var subQ61=sQuery(id+"F0.wireOp",EDGE,"E0.left");var subQ62=sQuery(id+"F0.wireOp",EDGE,"E0.top");var subQ63=sQuery(id+"F0.wireOp",EDGE,"E0.bottom");Q21=makeQuery(id+"F2.opShell","OFFSET_FACE",FACE,{"disambiguationData":[OSD([subQ63,subQ62,subQ61,subQ60,subQ59,subQ58,subQ57,subQ56,subQ55,subQ54,subQ53,subQ52,subQ51,subQ50,subQ49,subQ48,subQ47,subQ46,subQ45,subQ44,subQ43,subQ42,subQ41,subQ40,subQ39,subQ38,subQ37,subQ36,subQ35,subQ34,subQ33,subQ32,subQ31,subQ30,subQ29,subQ28,subQ27,subQ26,subQ25,subQ24,subQ23,subQ22,subQ21,subQ20,subQ19,subQ18,subQ17,subQ16,subQ15,subQ14,subQ13,subQ12,subQ11,subQ10,subQ9,subQ8,subQ7,subQ6,subQ5,subQ4,subQ3,subQ2,subQ1,subQ0]),TDD([makeQuery(id+"F1.opExtrude","CAP_FACE",FACE,{"disambiguationData":[OSD([subQ63,subQ62,subQ61,subQ60,subQ59,subQ58,subQ57,subQ56,subQ55,subQ54,subQ53,subQ52,subQ51,subQ50,subQ49,subQ48,subQ47,subQ46,subQ45,subQ44,subQ43,subQ42,subQ41,subQ40,subQ39,subQ38,subQ37,subQ36,subQ35,subQ34,subQ33,subQ32,subQ31,subQ30,subQ29,subQ28,subQ27,subQ26,subQ25,subQ24,subQ23,subQ22,subQ21,subQ20,subQ19,subQ18,subQ17,subQ16,subQ15,subQ14,subQ13,subQ12,subQ11,subQ10,subQ9,subQ8,subQ7,subQ6,subQ5,subQ4,subQ3,subQ2,subQ1,subQ0])],"isStart":false})]),OD(9.0)]});}
            var Q22;
            {var subQ0=sQuery(id+"F0.wireOp",EDGE,"E2.0.10.6");var subQ1=sQuery(id+"F0.wireOp",EDGE,"E2.0.10.5");var subQ2=sQuery(id+"F0.wireOp",EDGE,"E2.0.10.4");var subQ3=sQuery(id+"F0.wireOp",EDGE,"E2.0.10.3");var subQ4=sQuery(id+"F0.wireOp",EDGE,"E2.0.10.2");var subQ5=sQuery(id+"F0.wireOp",EDGE,"E2.0.10.1");var subQ6=sQuery(id+"F0.wireOp",EDGE,"E1.9.6.0");var subQ7=sQuery(id+"F0.wireOp",EDGE,"E1.9.5.0");var subQ8=sQuery(id+"F0.wireOp",EDGE,"E1.9.4.0");var subQ9=sQuery(id+"F0.wireOp",EDGE,"E1.9.3.0");var subQ10=sQuery(id+"F0.wireOp",EDGE,"E1.9.2.0");var subQ11=sQuery(id+"F0.wireOp",EDGE,"E1.9.1.0");var subQ12=sQuery(id+"F0.wireOp",EDGE,"E1.8.6.0");var subQ13=sQuery(id+"F0.wireOp",EDGE,"E1.8.5.0");var subQ14=sQuery(id+"F0.wireOp",EDGE,"E1.8.4.0");var subQ15=sQuery(id+"F0.wireOp",EDGE,"E1.8.3.0");var subQ16=sQuery(id+"F0.wireOp",EDGE,"E1.8.2.0");var subQ17=sQuery(id+"F0.wireOp",EDGE,"E1.8.1.0");var subQ18=sQuery(id+"F0.wireOp",EDGE,"E1.7.6.0");var subQ19=sQuery(id+"F0.wireOp",EDGE,"E1.7.5.0");var subQ20=sQuery(id+"F0.wireOp",EDGE,"E1.7.4.0");var subQ21=sQuery(id+"F0.wireOp",EDGE,"E1.7.3.0");var subQ22=sQuery(id+"F0.wireOp",EDGE,"E1.7.2.0");var subQ23=sQuery(id+"F0.wireOp",EDGE,"E1.7.1.0");var subQ24=sQuery(id+"F0.wireOp",EDGE,"E1.6.6.0");var subQ25=sQuery(id+"F0.wireOp",EDGE,"E1.6.5.0");var subQ26=sQuery(id+"F0.wireOp",EDGE,"E1.6.4.0");var subQ27=sQuery(id+"F0.wireOp",EDGE,"E1.6.3.0");var subQ28=sQuery(id+"F0.wireOp",EDGE,"E1.6.2.0");var subQ29=sQuery(id+"F0.wireOp",EDGE,"E1.6.1.0");var subQ30=sQuery(id+"F0.wireOp",EDGE,"E1.5.6.0");var subQ31=sQuery(id+"F0.wireOp",EDGE,"E1.5.5.0");var subQ32=sQuery(id+"F0.wireOp",EDGE,"E1.5.4.0");var subQ33=sQuery(id+"F0.wireOp",EDGE,"E1.5.3.0");var subQ34=sQuery(id+"F0.wireOp",EDGE,"E1.5.2.0");var subQ35=sQuery(id+"F0.wireOp",EDGE,"E1.5.1.0");var subQ36=sQuery(id+"F0.wireOp",EDGE,"E1.4.6.0");var subQ37=sQuery(id+"F0.wireOp",EDGE,"E1.4.5.0");var subQ38=sQuery(id+"F0.wireOp",EDGE,"E1.4.4.0");var subQ39=sQuery(id+"F0.wireOp",EDGE,"E1.4.3.0");var subQ40=sQuery(id+"F0.wireOp",EDGE,"E1.4.2.0");var subQ41=sQuery(id+"F0.wireOp",EDGE,"E1.4.1.0");var subQ42=sQuery(id+"F0.wireOp",EDGE,"E1.3.6.0");var subQ43=sQuery(id+"F0.wireOp",EDGE,"E1.3.5.0");var subQ44=sQuery(id+"F0.wireOp",EDGE,"E1.3.4.0");var subQ45=sQuery(id+"F0.wireOp",EDGE,"E1.3.3.0");var subQ46=sQuery(id+"F0.wireOp",EDGE,"E1.3.2.0");var subQ47=sQuery(id+"F0.wireOp",EDGE,"E1.3.1.0");var subQ48=sQuery(id+"F0.wireOp",EDGE,"E1.2.6.0");var subQ49=sQuery(id+"F0.wireOp",EDGE,"E1.2.5.0");var subQ50=sQuery(id+"F0.wireOp",EDGE,"E1.2.4.0");var subQ51=sQuery(id+"F0.wireOp",EDGE,"E1.2.3.0");var subQ52=sQuery(id+"F0.wireOp",EDGE,"E1.2.2.0");var subQ53=sQuery(id+"F0.wireOp",EDGE,"E1.2.1.0");var subQ54=sQuery(id+"F0.wireOp",EDGE,"E1.1.6.0");var subQ55=sQuery(id+"F0.wireOp",EDGE,"E1.1.5.0");var subQ56=sQuery(id+"F0.wireOp",EDGE,"E1.1.4.0");var subQ57=sQuery(id+"F0.wireOp",EDGE,"E1.1.3.0");var subQ58=sQuery(id+"F0.wireOp",EDGE,"E1.1.2.0");var subQ59=sQuery(id+"F0.wireOp",EDGE,"E1.1.1.0");var subQ60=sQuery(id+"F0.wireOp",EDGE,"E0.right");var subQ61=sQuery(id+"F0.wireOp",EDGE,"E0.left");var subQ62=sQuery(id+"F0.wireOp",EDGE,"E0.top");var subQ63=sQuery(id+"F0.wireOp",EDGE,"E0.bottom");Q22=makeQuery(id+"F2.opShell","OFFSET_FACE",FACE,{"disambiguationData":[OSD([subQ63,subQ62,subQ61,subQ60,subQ59,subQ58,subQ57,subQ56,subQ55,subQ54,subQ53,subQ52,subQ51,subQ50,subQ49,subQ48,subQ47,subQ46,subQ45,subQ44,subQ43,subQ42,subQ41,subQ40,subQ39,subQ38,subQ37,subQ36,subQ35,subQ34,subQ33,subQ32,subQ31,subQ30,subQ29,subQ28,subQ27,subQ26,subQ25,subQ24,subQ23,subQ22,subQ21,subQ20,subQ19,subQ18,subQ17,subQ16,subQ15,subQ14,subQ13,subQ12,subQ11,subQ10,subQ9,subQ8,subQ7,subQ6,subQ5,subQ4,subQ3,subQ2,subQ1,subQ0]),TDD([makeQuery(id+"F1.opExtrude","CAP_FACE",FACE,{"disambiguationData":[OSD([subQ63,subQ62,subQ61,subQ60,subQ59,subQ58,subQ57,subQ56,subQ55,subQ54,subQ53,subQ52,subQ51,subQ50,subQ49,subQ48,subQ47,subQ46,subQ45,subQ44,subQ43,subQ42,subQ41,subQ40,subQ39,subQ38,subQ37,subQ36,subQ35,subQ34,subQ33,subQ32,subQ31,subQ30,subQ29,subQ28,subQ27,subQ26,subQ25,subQ24,subQ23,subQ22,subQ21,subQ20,subQ19,subQ18,subQ17,subQ16,subQ15,subQ14,subQ13,subQ12,subQ11,subQ10,subQ9,subQ8,subQ7,subQ6,subQ5,subQ4,subQ3,subQ2,subQ1,subQ0])],"isStart":false})]),OD(15.0)]});}
            var Q23;
            {var subQ0=sQuery(id+"F0.wireOp",EDGE,"E2.0.10.6");var subQ1=sQuery(id+"F0.wireOp",EDGE,"E2.0.10.5");var subQ2=sQuery(id+"F0.wireOp",EDGE,"E2.0.10.4");var subQ3=sQuery(id+"F0.wireOp",EDGE,"E2.0.10.3");var subQ4=sQuery(id+"F0.wireOp",EDGE,"E2.0.10.2");var subQ5=sQuery(id+"F0.wireOp",EDGE,"E2.0.10.1");var subQ6=sQuery(id+"F0.wireOp",EDGE,"E1.9.6.0");var subQ7=sQuery(id+"F0.wireOp",EDGE,"E1.9.5.0");var subQ8=sQuery(id+"F0.wireOp",EDGE,"E1.9.4.0");var subQ9=sQuery(id+"F0.wireOp",EDGE,"E1.9.3.0");var subQ10=sQuery(id+"F0.wireOp",EDGE,"E1.9.2.0");var subQ11=sQuery(id+"F0.wireOp",EDGE,"E1.9.1.0");var subQ12=sQuery(id+"F0.wireOp",EDGE,"E1.8.6.0");var subQ13=sQuery(id+"F0.wireOp",EDGE,"E1.8.5.0");var subQ14=sQuery(id+"F0.wireOp",EDGE,"E1.8.4.0");var subQ15=sQuery(id+"F0.wireOp",EDGE,"E1.8.3.0");var subQ16=sQuery(id+"F0.wireOp",EDGE,"E1.8.2.0");var subQ17=sQuery(id+"F0.wireOp",EDGE,"E1.8.1.0");var subQ18=sQuery(id+"F0.wireOp",EDGE,"E1.7.6.0");var subQ19=sQuery(id+"F0.wireOp",EDGE,"E1.7.5.0");var subQ20=sQuery(id+"F0.wireOp",EDGE,"E1.7.4.0");var subQ21=sQuery(id+"F0.wireOp",EDGE,"E1.7.3.0");var subQ22=sQuery(id+"F0.wireOp",EDGE,"E1.7.2.0");var subQ23=sQuery(id+"F0.wireOp",EDGE,"E1.7.1.0");var subQ24=sQuery(id+"F0.wireOp",EDGE,"E1.6.6.0");var subQ25=sQuery(id+"F0.wireOp",EDGE,"E1.6.5.0");var subQ26=sQuery(id+"F0.wireOp",EDGE,"E1.6.4.0");var subQ27=sQuery(id+"F0.wireOp",EDGE,"E1.6.3.0");var subQ28=sQuery(id+"F0.wireOp",EDGE,"E1.6.2.0");var subQ29=sQuery(id+"F0.wireOp",EDGE,"E1.6.1.0");var subQ30=sQuery(id+"F0.wireOp",EDGE,"E1.5.6.0");var subQ31=sQuery(id+"F0.wireOp",EDGE,"E1.5.5.0");var subQ32=sQuery(id+"F0.wireOp",EDGE,"E1.5.4.0");var subQ33=sQuery(id+"F0.wireOp",EDGE,"E1.5.3.0");var subQ34=sQuery(id+"F0.wireOp",EDGE,"E1.5.2.0");var subQ35=sQuery(id+"F0.wireOp",EDGE,"E1.5.1.0");var subQ36=sQuery(id+"F0.wireOp",EDGE,"E1.4.6.0");var subQ37=sQuery(id+"F0.wireOp",EDGE,"E1.4.5.0");var subQ38=sQuery(id+"F0.wireOp",EDGE,"E1.4.4.0");var subQ39=sQuery(id+"F0.wireOp",EDGE,"E1.4.3.0");var subQ40=sQuery(id+"F0.wireOp",EDGE,"E1.4.2.0");var subQ41=sQuery(id+"F0.wireOp",EDGE,"E1.4.1.0");var subQ42=sQuery(id+"F0.wireOp",EDGE,"E1.3.6.0");var subQ43=sQuery(id+"F0.wireOp",EDGE,"E1.3.5.0");var subQ44=sQuery(id+"F0.wireOp",EDGE,"E1.3.4.0");var subQ45=sQuery(id+"F0.wireOp",EDGE,"E1.3.3.0");var subQ46=sQuery(id+"F0.wireOp",EDGE,"E1.3.2.0");var subQ47=sQuery(id+"F0.wireOp",EDGE,"E1.3.1.0");var subQ48=sQuery(id+"F0.wireOp",EDGE,"E1.2.6.0");var subQ49=sQuery(id+"F0.wireOp",EDGE,"E1.2.5.0");var subQ50=sQuery(id+"F0.wireOp",EDGE,"E1.2.4.0");var subQ51=sQuery(id+"F0.wireOp",EDGE,"E1.2.3.0");var subQ52=sQuery(id+"F0.wireOp",EDGE,"E1.2.2.0");var subQ53=sQuery(id+"F0.wireOp",EDGE,"E1.2.1.0");var subQ54=sQuery(id+"F0.wireOp",EDGE,"E1.1.6.0");var subQ55=sQuery(id+"F0.wireOp",EDGE,"E1.1.5.0");var subQ56=sQuery(id+"F0.wireOp",EDGE,"E1.1.4.0");var subQ57=sQuery(id+"F0.wireOp",EDGE,"E1.1.3.0");var subQ58=sQuery(id+"F0.wireOp",EDGE,"E1.1.2.0");var subQ59=sQuery(id+"F0.wireOp",EDGE,"E1.1.1.0");var subQ60=sQuery(id+"F0.wireOp",EDGE,"E0.right");var subQ61=sQuery(id+"F0.wireOp",EDGE,"E0.left");var subQ62=sQuery(id+"F0.wireOp",EDGE,"E0.top");var subQ63=sQuery(id+"F0.wireOp",EDGE,"E0.bottom");Q23=makeQuery(id+"F2.opShell","OFFSET_FACE",FACE,{"disambiguationData":[OSD([subQ63,subQ62,subQ61,subQ60,subQ59,subQ58,subQ57,subQ56,subQ55,subQ54,subQ53,subQ52,subQ51,subQ50,subQ49,subQ48,subQ47,subQ46,subQ45,subQ44,subQ43,subQ42,subQ41,subQ40,subQ39,subQ38,subQ37,subQ36,subQ35,subQ34,subQ33,subQ32,subQ31,subQ30,subQ29,subQ28,subQ27,subQ26,subQ25,subQ24,subQ23,subQ22,subQ21,subQ20,subQ19,subQ18,subQ17,subQ16,subQ15,subQ14,subQ13,subQ12,subQ11,subQ10,subQ9,subQ8,subQ7,subQ6,subQ5,subQ4,subQ3,subQ2,subQ1,subQ0]),TDD([makeQuery(id+"F1.opExtrude","CAP_FACE",FACE,{"disambiguationData":[OSD([subQ63,subQ62,subQ61,subQ60,subQ59,subQ58,subQ57,subQ56,subQ55,subQ54,subQ53,subQ52,subQ51,subQ50,subQ49,subQ48,subQ47,subQ46,subQ45,subQ44,subQ43,subQ42,subQ41,subQ40,subQ39,subQ38,subQ37,subQ36,subQ35,subQ34,subQ33,subQ32,subQ31,subQ30,subQ29,subQ28,subQ27,subQ26,subQ25,subQ24,subQ23,subQ22,subQ21,subQ20,subQ19,subQ18,subQ17,subQ16,subQ15,subQ14,subQ13,subQ12,subQ11,subQ10,subQ9,subQ8,subQ7,subQ6,subQ5,subQ4,subQ3,subQ2,subQ1,subQ0])],"isStart":false})]),OD(21.0)]});}
            var Q24;
            {var subQ0=sQuery(id+"F0.wireOp",EDGE,"E2.0.10.6");var subQ1=sQuery(id+"F0.wireOp",EDGE,"E2.0.10.5");var subQ2=sQuery(id+"F0.wireOp",EDGE,"E2.0.10.4");var subQ3=sQuery(id+"F0.wireOp",EDGE,"E2.0.10.3");var subQ4=sQuery(id+"F0.wireOp",EDGE,"E2.0.10.2");var subQ5=sQuery(id+"F0.wireOp",EDGE,"E2.0.10.1");var subQ6=sQuery(id+"F0.wireOp",EDGE,"E1.9.6.0");var subQ7=sQuery(id+"F0.wireOp",EDGE,"E1.9.5.0");var subQ8=sQuery(id+"F0.wireOp",EDGE,"E1.9.4.0");var subQ9=sQuery(id+"F0.wireOp",EDGE,"E1.9.3.0");var subQ10=sQuery(id+"F0.wireOp",EDGE,"E1.9.2.0");var subQ11=sQuery(id+"F0.wireOp",EDGE,"E1.9.1.0");var subQ12=sQuery(id+"F0.wireOp",EDGE,"E1.8.6.0");var subQ13=sQuery(id+"F0.wireOp",EDGE,"E1.8.5.0");var subQ14=sQuery(id+"F0.wireOp",EDGE,"E1.8.4.0");var subQ15=sQuery(id+"F0.wireOp",EDGE,"E1.8.3.0");var subQ16=sQuery(id+"F0.wireOp",EDGE,"E1.8.2.0");var subQ17=sQuery(id+"F0.wireOp",EDGE,"E1.8.1.0");var subQ18=sQuery(id+"F0.wireOp",EDGE,"E1.7.6.0");var subQ19=sQuery(id+"F0.wireOp",EDGE,"E1.7.5.0");var subQ20=sQuery(id+"F0.wireOp",EDGE,"E1.7.4.0");var subQ21=sQuery(id+"F0.wireOp",EDGE,"E1.7.3.0");var subQ22=sQuery(id+"F0.wireOp",EDGE,"E1.7.2.0");var subQ23=sQuery(id+"F0.wireOp",EDGE,"E1.7.1.0");var subQ24=sQuery(id+"F0.wireOp",EDGE,"E1.6.6.0");var subQ25=sQuery(id+"F0.wireOp",EDGE,"E1.6.5.0");var subQ26=sQuery(id+"F0.wireOp",EDGE,"E1.6.4.0");var subQ27=sQuery(id+"F0.wireOp",EDGE,"E1.6.3.0");var subQ28=sQuery(id+"F0.wireOp",EDGE,"E1.6.2.0");var subQ29=sQuery(id+"F0.wireOp",EDGE,"E1.6.1.0");var subQ30=sQuery(id+"F0.wireOp",EDGE,"E1.5.6.0");var subQ31=sQuery(id+"F0.wireOp",EDGE,"E1.5.5.0");var subQ32=sQuery(id+"F0.wireOp",EDGE,"E1.5.4.0");var subQ33=sQuery(id+"F0.wireOp",EDGE,"E1.5.3.0");var subQ34=sQuery(id+"F0.wireOp",EDGE,"E1.5.2.0");var subQ35=sQuery(id+"F0.wireOp",EDGE,"E1.5.1.0");var subQ36=sQuery(id+"F0.wireOp",EDGE,"E1.4.6.0");var subQ37=sQuery(id+"F0.wireOp",EDGE,"E1.4.5.0");var subQ38=sQuery(id+"F0.wireOp",EDGE,"E1.4.4.0");var subQ39=sQuery(id+"F0.wireOp",EDGE,"E1.4.3.0");var subQ40=sQuery(id+"F0.wireOp",EDGE,"E1.4.2.0");var subQ41=sQuery(id+"F0.wireOp",EDGE,"E1.4.1.0");var subQ42=sQuery(id+"F0.wireOp",EDGE,"E1.3.6.0");var subQ43=sQuery(id+"F0.wireOp",EDGE,"E1.3.5.0");var subQ44=sQuery(id+"F0.wireOp",EDGE,"E1.3.4.0");var subQ45=sQuery(id+"F0.wireOp",EDGE,"E1.3.3.0");var subQ46=sQuery(id+"F0.wireOp",EDGE,"E1.3.2.0");var subQ47=sQuery(id+"F0.wireOp",EDGE,"E1.3.1.0");var subQ48=sQuery(id+"F0.wireOp",EDGE,"E1.2.6.0");var subQ49=sQuery(id+"F0.wireOp",EDGE,"E1.2.5.0");var subQ50=sQuery(id+"F0.wireOp",EDGE,"E1.2.4.0");var subQ51=sQuery(id+"F0.wireOp",EDGE,"E1.2.3.0");var subQ52=sQuery(id+"F0.wireOp",EDGE,"E1.2.2.0");var subQ53=sQuery(id+"F0.wireOp",EDGE,"E1.2.1.0");var subQ54=sQuery(id+"F0.wireOp",EDGE,"E1.1.6.0");var subQ55=sQuery(id+"F0.wireOp",EDGE,"E1.1.5.0");var subQ56=sQuery(id+"F0.wireOp",EDGE,"E1.1.4.0");var subQ57=sQuery(id+"F0.wireOp",EDGE,"E1.1.3.0");var subQ58=sQuery(id+"F0.wireOp",EDGE,"E1.1.2.0");var subQ59=sQuery(id+"F0.wireOp",EDGE,"E1.1.1.0");var subQ60=sQuery(id+"F0.wireOp",EDGE,"E0.right");var subQ61=sQuery(id+"F0.wireOp",EDGE,"E0.left");var subQ62=sQuery(id+"F0.wireOp",EDGE,"E0.top");var subQ63=sQuery(id+"F0.wireOp",EDGE,"E0.bottom");Q24=makeQuery(id+"F2.opShell","OFFSET_FACE",FACE,{"disambiguationData":[OSD([subQ63,subQ62,subQ61,subQ60,subQ59,subQ58,subQ57,subQ56,subQ55,subQ54,subQ53,subQ52,subQ51,subQ50,subQ49,subQ48,subQ47,subQ46,subQ45,subQ44,subQ43,subQ42,subQ41,subQ40,subQ39,subQ38,subQ37,subQ36,subQ35,subQ34,subQ33,subQ32,subQ31,subQ30,subQ29,subQ28,subQ27,subQ26,subQ25,subQ24,subQ23,subQ22,subQ21,subQ20,subQ19,subQ18,subQ17,subQ16,subQ15,subQ14,subQ13,subQ12,subQ11,subQ10,subQ9,subQ8,subQ7,subQ6,subQ5,subQ4,subQ3,subQ2,subQ1,subQ0]),TDD([makeQuery(id+"F1.opExtrude","CAP_FACE",FACE,{"disambiguationData":[OSD([subQ63,subQ62,subQ61,subQ60,subQ59,subQ58,subQ57,subQ56,subQ55,subQ54,subQ53,subQ52,subQ51,subQ50,subQ49,subQ48,subQ47,subQ46,subQ45,subQ44,subQ43,subQ42,subQ41,subQ40,subQ39,subQ38,subQ37,subQ36,subQ35,subQ34,subQ33,subQ32,subQ31,subQ30,subQ29,subQ28,subQ27,subQ26,subQ25,subQ24,subQ23,subQ22,subQ21,subQ20,subQ19,subQ18,subQ17,subQ16,subQ15,subQ14,subQ13,subQ12,subQ11,subQ10,subQ9,subQ8,subQ7,subQ6,subQ5,subQ4,subQ3,subQ2,subQ1,subQ0])],"isStart":false})]),OD(27.0)]});}
            var Q25;
            {var subQ0=sQuery(id+"F0.wireOp",EDGE,"E2.0.10.6");var subQ1=sQuery(id+"F0.wireOp",EDGE,"E2.0.10.5");var subQ2=sQuery(id+"F0.wireOp",EDGE,"E2.0.10.4");var subQ3=sQuery(id+"F0.wireOp",EDGE,"E2.0.10.3");var subQ4=sQuery(id+"F0.wireOp",EDGE,"E2.0.10.2");var subQ5=sQuery(id+"F0.wireOp",EDGE,"E2.0.10.1");var subQ6=sQuery(id+"F0.wireOp",EDGE,"E1.9.6.0");var subQ7=sQuery(id+"F0.wireOp",EDGE,"E1.9.5.0");var subQ8=sQuery(id+"F0.wireOp",EDGE,"E1.9.4.0");var subQ9=sQuery(id+"F0.wireOp",EDGE,"E1.9.3.0");var subQ10=sQuery(id+"F0.wireOp",EDGE,"E1.9.2.0");var subQ11=sQuery(id+"F0.wireOp",EDGE,"E1.9.1.0");var subQ12=sQuery(id+"F0.wireOp",EDGE,"E1.8.6.0");var subQ13=sQuery(id+"F0.wireOp",EDGE,"E1.8.5.0");var subQ14=sQuery(id+"F0.wireOp",EDGE,"E1.8.4.0");var subQ15=sQuery(id+"F0.wireOp",EDGE,"E1.8.3.0");var subQ16=sQuery(id+"F0.wireOp",EDGE,"E1.8.2.0");var subQ17=sQuery(id+"F0.wireOp",EDGE,"E1.8.1.0");var subQ18=sQuery(id+"F0.wireOp",EDGE,"E1.7.6.0");var subQ19=sQuery(id+"F0.wireOp",EDGE,"E1.7.5.0");var subQ20=sQuery(id+"F0.wireOp",EDGE,"E1.7.4.0");var subQ21=sQuery(id+"F0.wireOp",EDGE,"E1.7.3.0");var subQ22=sQuery(id+"F0.wireOp",EDGE,"E1.7.2.0");var subQ23=sQuery(id+"F0.wireOp",EDGE,"E1.7.1.0");var subQ24=sQuery(id+"F0.wireOp",EDGE,"E1.6.6.0");var subQ25=sQuery(id+"F0.wireOp",EDGE,"E1.6.5.0");var subQ26=sQuery(id+"F0.wireOp",EDGE,"E1.6.4.0");var subQ27=sQuery(id+"F0.wireOp",EDGE,"E1.6.3.0");var subQ28=sQuery(id+"F0.wireOp",EDGE,"E1.6.2.0");var subQ29=sQuery(id+"F0.wireOp",EDGE,"E1.6.1.0");var subQ30=sQuery(id+"F0.wireOp",EDGE,"E1.5.6.0");var subQ31=sQuery(id+"F0.wireOp",EDGE,"E1.5.5.0");var subQ32=sQuery(id+"F0.wireOp",EDGE,"E1.5.4.0");var subQ33=sQuery(id+"F0.wireOp",EDGE,"E1.5.3.0");var subQ34=sQuery(id+"F0.wireOp",EDGE,"E1.5.2.0");var subQ35=sQuery(id+"F0.wireOp",EDGE,"E1.5.1.0");var subQ36=sQuery(id+"F0.wireOp",EDGE,"E1.4.6.0");var subQ37=sQuery(id+"F0.wireOp",EDGE,"E1.4.5.0");var subQ38=sQuery(id+"F0.wireOp",EDGE,"E1.4.4.0");var subQ39=sQuery(id+"F0.wireOp",EDGE,"E1.4.3.0");var subQ40=sQuery(id+"F0.wireOp",EDGE,"E1.4.2.0");var subQ41=sQuery(id+"F0.wireOp",EDGE,"E1.4.1.0");var subQ42=sQuery(id+"F0.wireOp",EDGE,"E1.3.6.0");var subQ43=sQuery(id+"F0.wireOp",EDGE,"E1.3.5.0");var subQ44=sQuery(id+"F0.wireOp",EDGE,"E1.3.4.0");var subQ45=sQuery(id+"F0.wireOp",EDGE,"E1.3.3.0");var subQ46=sQuery(id+"F0.wireOp",EDGE,"E1.3.2.0");var subQ47=sQuery(id+"F0.wireOp",EDGE,"E1.3.1.0");var subQ48=sQuery(id+"F0.wireOp",EDGE,"E1.2.6.0");var subQ49=sQuery(id+"F0.wireOp",EDGE,"E1.2.5.0");var subQ50=sQuery(id+"F0.wireOp",EDGE,"E1.2.4.0");var subQ51=sQuery(id+"F0.wireOp",EDGE,"E1.2.3.0");var subQ52=sQuery(id+"F0.wireOp",EDGE,"E1.2.2.0");var subQ53=sQuery(id+"F0.wireOp",EDGE,"E1.2.1.0");var subQ54=sQuery(id+"F0.wireOp",EDGE,"E1.1.6.0");var subQ55=sQuery(id+"F0.wireOp",EDGE,"E1.1.5.0");var subQ56=sQuery(id+"F0.wireOp",EDGE,"E1.1.4.0");var subQ57=sQuery(id+"F0.wireOp",EDGE,"E1.1.3.0");var subQ58=sQuery(id+"F0.wireOp",EDGE,"E1.1.2.0");var subQ59=sQuery(id+"F0.wireOp",EDGE,"E1.1.1.0");var subQ60=sQuery(id+"F0.wireOp",EDGE,"E0.right");var subQ61=sQuery(id+"F0.wireOp",EDGE,"E0.left");var subQ62=sQuery(id+"F0.wireOp",EDGE,"E0.top");var subQ63=sQuery(id+"F0.wireOp",EDGE,"E0.bottom");Q25=makeQuery(id+"F2.opShell","OFFSET_FACE",FACE,{"disambiguationData":[OSD([subQ63,subQ62,subQ61,subQ60,subQ59,subQ58,subQ57,subQ56,subQ55,subQ54,subQ53,subQ52,subQ51,subQ50,subQ49,subQ48,subQ47,subQ46,subQ45,subQ44,subQ43,subQ42,subQ41,subQ40,subQ39,subQ38,subQ37,subQ36,subQ35,subQ34,subQ33,subQ32,subQ31,subQ30,subQ29,subQ28,subQ27,subQ26,subQ25,subQ24,subQ23,subQ22,subQ21,subQ20,subQ19,subQ18,subQ17,subQ16,subQ15,subQ14,subQ13,subQ12,subQ11,subQ10,subQ9,subQ8,subQ7,subQ6,subQ5,subQ4,subQ3,subQ2,subQ1,subQ0]),TDD([makeQuery(id+"F1.opExtrude","CAP_FACE",FACE,{"disambiguationData":[OSD([subQ63,subQ62,subQ61,subQ60,subQ59,subQ58,subQ57,subQ56,subQ55,subQ54,subQ53,subQ52,subQ51,subQ50,subQ49,subQ48,subQ47,subQ46,subQ45,subQ44,subQ43,subQ42,subQ41,subQ40,subQ39,subQ38,subQ37,subQ36,subQ35,subQ34,subQ33,subQ32,subQ31,subQ30,subQ29,subQ28,subQ27,subQ26,subQ25,subQ24,subQ23,subQ22,subQ21,subQ20,subQ19,subQ18,subQ17,subQ16,subQ15,subQ14,subQ13,subQ12,subQ11,subQ10,subQ9,subQ8,subQ7,subQ6,subQ5,subQ4,subQ3,subQ2,subQ1,subQ0])],"isStart":false})]),OD(33.0)]});}
            var Q26;
            {var subQ0=sQuery(id+"F0.wireOp",EDGE,"E2.0.10.6");var subQ1=sQuery(id+"F0.wireOp",EDGE,"E2.0.10.5");var subQ2=sQuery(id+"F0.wireOp",EDGE,"E2.0.10.4");var subQ3=sQuery(id+"F0.wireOp",EDGE,"E2.0.10.3");var subQ4=sQuery(id+"F0.wireOp",EDGE,"E2.0.10.2");var subQ5=sQuery(id+"F0.wireOp",EDGE,"E2.0.10.1");var subQ6=sQuery(id+"F0.wireOp",EDGE,"E1.9.6.0");var subQ7=sQuery(id+"F0.wireOp",EDGE,"E1.9.5.0");var subQ8=sQuery(id+"F0.wireOp",EDGE,"E1.9.4.0");var subQ9=sQuery(id+"F0.wireOp",EDGE,"E1.9.3.0");var subQ10=sQuery(id+"F0.wireOp",EDGE,"E1.9.2.0");var subQ11=sQuery(id+"F0.wireOp",EDGE,"E1.9.1.0");var subQ12=sQuery(id+"F0.wireOp",EDGE,"E1.8.6.0");var subQ13=sQuery(id+"F0.wireOp",EDGE,"E1.8.5.0");var subQ14=sQuery(id+"F0.wireOp",EDGE,"E1.8.4.0");var subQ15=sQuery(id+"F0.wireOp",EDGE,"E1.8.3.0");var subQ16=sQuery(id+"F0.wireOp",EDGE,"E1.8.2.0");var subQ17=sQuery(id+"F0.wireOp",EDGE,"E1.8.1.0");var subQ18=sQuery(id+"F0.wireOp",EDGE,"E1.7.6.0");var subQ19=sQuery(id+"F0.wireOp",EDGE,"E1.7.5.0");var subQ20=sQuery(id+"F0.wireOp",EDGE,"E1.7.4.0");var subQ21=sQuery(id+"F0.wireOp",EDGE,"E1.7.3.0");var subQ22=sQuery(id+"F0.wireOp",EDGE,"E1.7.2.0");var subQ23=sQuery(id+"F0.wireOp",EDGE,"E1.7.1.0");var subQ24=sQuery(id+"F0.wireOp",EDGE,"E1.6.6.0");var subQ25=sQuery(id+"F0.wireOp",EDGE,"E1.6.5.0");var subQ26=sQuery(id+"F0.wireOp",EDGE,"E1.6.4.0");var subQ27=sQuery(id+"F0.wireOp",EDGE,"E1.6.3.0");var subQ28=sQuery(id+"F0.wireOp",EDGE,"E1.6.2.0");var subQ29=sQuery(id+"F0.wireOp",EDGE,"E1.6.1.0");var subQ30=sQuery(id+"F0.wireOp",EDGE,"E1.5.6.0");var subQ31=sQuery(id+"F0.wireOp",EDGE,"E1.5.5.0");var subQ32=sQuery(id+"F0.wireOp",EDGE,"E1.5.4.0");var subQ33=sQuery(id+"F0.wireOp",EDGE,"E1.5.3.0");var subQ34=sQuery(id+"F0.wireOp",EDGE,"E1.5.2.0");var subQ35=sQuery(id+"F0.wireOp",EDGE,"E1.5.1.0");var subQ36=sQuery(id+"F0.wireOp",EDGE,"E1.4.6.0");var subQ37=sQuery(id+"F0.wireOp",EDGE,"E1.4.5.0");var subQ38=sQuery(id+"F0.wireOp",EDGE,"E1.4.4.0");var subQ39=sQuery(id+"F0.wireOp",EDGE,"E1.4.3.0");var subQ40=sQuery(id+"F0.wireOp",EDGE,"E1.4.2.0");var subQ41=sQuery(id+"F0.wireOp",EDGE,"E1.4.1.0");var subQ42=sQuery(id+"F0.wireOp",EDGE,"E1.3.6.0");var subQ43=sQuery(id+"F0.wireOp",EDGE,"E1.3.5.0");var subQ44=sQuery(id+"F0.wireOp",EDGE,"E1.3.4.0");var subQ45=sQuery(id+"F0.wireOp",EDGE,"E1.3.3.0");var subQ46=sQuery(id+"F0.wireOp",EDGE,"E1.3.2.0");var subQ47=sQuery(id+"F0.wireOp",EDGE,"E1.3.1.0");var subQ48=sQuery(id+"F0.wireOp",EDGE,"E1.2.6.0");var subQ49=sQuery(id+"F0.wireOp",EDGE,"E1.2.5.0");var subQ50=sQuery(id+"F0.wireOp",EDGE,"E1.2.4.0");var subQ51=sQuery(id+"F0.wireOp",EDGE,"E1.2.3.0");var subQ52=sQuery(id+"F0.wireOp",EDGE,"E1.2.2.0");var subQ53=sQuery(id+"F0.wireOp",EDGE,"E1.2.1.0");var subQ54=sQuery(id+"F0.wireOp",EDGE,"E1.1.6.0");var subQ55=sQuery(id+"F0.wireOp",EDGE,"E1.1.5.0");var subQ56=sQuery(id+"F0.wireOp",EDGE,"E1.1.4.0");var subQ57=sQuery(id+"F0.wireOp",EDGE,"E1.1.3.0");var subQ58=sQuery(id+"F0.wireOp",EDGE,"E1.1.2.0");var subQ59=sQuery(id+"F0.wireOp",EDGE,"E1.1.1.0");var subQ60=sQuery(id+"F0.wireOp",EDGE,"E0.right");var subQ61=sQuery(id+"F0.wireOp",EDGE,"E0.left");var subQ62=sQuery(id+"F0.wireOp",EDGE,"E0.top");var subQ63=sQuery(id+"F0.wireOp",EDGE,"E0.bottom");Q26=makeQuery(id+"F2.opShell","OFFSET_FACE",FACE,{"disambiguationData":[OSD([subQ63,subQ62,subQ61,subQ60,subQ59,subQ58,subQ57,subQ56,subQ55,subQ54,subQ53,subQ52,subQ51,subQ50,subQ49,subQ48,subQ47,subQ46,subQ45,subQ44,subQ43,subQ42,subQ41,subQ40,subQ39,subQ38,subQ37,subQ36,subQ35,subQ34,subQ33,subQ32,subQ31,subQ30,subQ29,subQ28,subQ27,subQ26,subQ25,subQ24,subQ23,subQ22,subQ21,subQ20,subQ19,subQ18,subQ17,subQ16,subQ15,subQ14,subQ13,subQ12,subQ11,subQ10,subQ9,subQ8,subQ7,subQ6,subQ5,subQ4,subQ3,subQ2,subQ1,subQ0]),TDD([makeQuery(id+"F1.opExtrude","CAP_FACE",FACE,{"disambiguationData":[OSD([subQ63,subQ62,subQ61,subQ60,subQ59,subQ58,subQ57,subQ56,subQ55,subQ54,subQ53,subQ52,subQ51,subQ50,subQ49,subQ48,subQ47,subQ46,subQ45,subQ44,subQ43,subQ42,subQ41,subQ40,subQ39,subQ38,subQ37,subQ36,subQ35,subQ34,subQ33,subQ32,subQ31,subQ30,subQ29,subQ28,subQ27,subQ26,subQ25,subQ24,subQ23,subQ22,subQ21,subQ20,subQ19,subQ18,subQ17,subQ16,subQ15,subQ14,subQ13,subQ12,subQ11,subQ10,subQ9,subQ8,subQ7,subQ6,subQ5,subQ4,subQ3,subQ2,subQ1,subQ0])],"isStart":false})]),OD(39.0)]});}
            var Q27;
            {var subQ0=sQuery(id+"F0.wireOp",EDGE,"E2.0.10.6");var subQ1=sQuery(id+"F0.wireOp",EDGE,"E2.0.10.5");var subQ2=sQuery(id+"F0.wireOp",EDGE,"E2.0.10.4");var subQ3=sQuery(id+"F0.wireOp",EDGE,"E2.0.10.3");var subQ4=sQuery(id+"F0.wireOp",EDGE,"E2.0.10.2");var subQ5=sQuery(id+"F0.wireOp",EDGE,"E2.0.10.1");var subQ6=sQuery(id+"F0.wireOp",EDGE,"E1.9.6.0");var subQ7=sQuery(id+"F0.wireOp",EDGE,"E1.9.5.0");var subQ8=sQuery(id+"F0.wireOp",EDGE,"E1.9.4.0");var subQ9=sQuery(id+"F0.wireOp",EDGE,"E1.9.3.0");var subQ10=sQuery(id+"F0.wireOp",EDGE,"E1.9.2.0");var subQ11=sQuery(id+"F0.wireOp",EDGE,"E1.9.1.0");var subQ12=sQuery(id+"F0.wireOp",EDGE,"E1.8.6.0");var subQ13=sQuery(id+"F0.wireOp",EDGE,"E1.8.5.0");var subQ14=sQuery(id+"F0.wireOp",EDGE,"E1.8.4.0");var subQ15=sQuery(id+"F0.wireOp",EDGE,"E1.8.3.0");var subQ16=sQuery(id+"F0.wireOp",EDGE,"E1.8.2.0");var subQ17=sQuery(id+"F0.wireOp",EDGE,"E1.8.1.0");var subQ18=sQuery(id+"F0.wireOp",EDGE,"E1.7.6.0");var subQ19=sQuery(id+"F0.wireOp",EDGE,"E1.7.5.0");var subQ20=sQuery(id+"F0.wireOp",EDGE,"E1.7.4.0");var subQ21=sQuery(id+"F0.wireOp",EDGE,"E1.7.3.0");var subQ22=sQuery(id+"F0.wireOp",EDGE,"E1.7.2.0");var subQ23=sQuery(id+"F0.wireOp",EDGE,"E1.7.1.0");var subQ24=sQuery(id+"F0.wireOp",EDGE,"E1.6.6.0");var subQ25=sQuery(id+"F0.wireOp",EDGE,"E1.6.5.0");var subQ26=sQuery(id+"F0.wireOp",EDGE,"E1.6.4.0");var subQ27=sQuery(id+"F0.wireOp",EDGE,"E1.6.3.0");var subQ28=sQuery(id+"F0.wireOp",EDGE,"E1.6.2.0");var subQ29=sQuery(id+"F0.wireOp",EDGE,"E1.6.1.0");var subQ30=sQuery(id+"F0.wireOp",EDGE,"E1.5.6.0");var subQ31=sQuery(id+"F0.wireOp",EDGE,"E1.5.5.0");var subQ32=sQuery(id+"F0.wireOp",EDGE,"E1.5.4.0");var subQ33=sQuery(id+"F0.wireOp",EDGE,"E1.5.3.0");var subQ34=sQuery(id+"F0.wireOp",EDGE,"E1.5.2.0");var subQ35=sQuery(id+"F0.wireOp",EDGE,"E1.5.1.0");var subQ36=sQuery(id+"F0.wireOp",EDGE,"E1.4.6.0");var subQ37=sQuery(id+"F0.wireOp",EDGE,"E1.4.5.0");var subQ38=sQuery(id+"F0.wireOp",EDGE,"E1.4.4.0");var subQ39=sQuery(id+"F0.wireOp",EDGE,"E1.4.3.0");var subQ40=sQuery(id+"F0.wireOp",EDGE,"E1.4.2.0");var subQ41=sQuery(id+"F0.wireOp",EDGE,"E1.4.1.0");var subQ42=sQuery(id+"F0.wireOp",EDGE,"E1.3.6.0");var subQ43=sQuery(id+"F0.wireOp",EDGE,"E1.3.5.0");var subQ44=sQuery(id+"F0.wireOp",EDGE,"E1.3.4.0");var subQ45=sQuery(id+"F0.wireOp",EDGE,"E1.3.3.0");var subQ46=sQuery(id+"F0.wireOp",EDGE,"E1.3.2.0");var subQ47=sQuery(id+"F0.wireOp",EDGE,"E1.3.1.0");var subQ48=sQuery(id+"F0.wireOp",EDGE,"E1.2.6.0");var subQ49=sQuery(id+"F0.wireOp",EDGE,"E1.2.5.0");var subQ50=sQuery(id+"F0.wireOp",EDGE,"E1.2.4.0");var subQ51=sQuery(id+"F0.wireOp",EDGE,"E1.2.3.0");var subQ52=sQuery(id+"F0.wireOp",EDGE,"E1.2.2.0");var subQ53=sQuery(id+"F0.wireOp",EDGE,"E1.2.1.0");var subQ54=sQuery(id+"F0.wireOp",EDGE,"E1.1.6.0");var subQ55=sQuery(id+"F0.wireOp",EDGE,"E1.1.5.0");var subQ56=sQuery(id+"F0.wireOp",EDGE,"E1.1.4.0");var subQ57=sQuery(id+"F0.wireOp",EDGE,"E1.1.3.0");var subQ58=sQuery(id+"F0.wireOp",EDGE,"E1.1.2.0");var subQ59=sQuery(id+"F0.wireOp",EDGE,"E1.1.1.0");var subQ60=sQuery(id+"F0.wireOp",EDGE,"E0.right");var subQ61=sQuery(id+"F0.wireOp",EDGE,"E0.left");var subQ62=sQuery(id+"F0.wireOp",EDGE,"E0.top");var subQ63=sQuery(id+"F0.wireOp",EDGE,"E0.bottom");Q27=makeQuery(id+"F2.opShell","OFFSET_FACE",FACE,{"disambiguationData":[OSD([subQ63,subQ62,subQ61,subQ60,subQ59,subQ58,subQ57,subQ56,subQ55,subQ54,subQ53,subQ52,subQ51,subQ50,subQ49,subQ48,subQ47,subQ46,subQ45,subQ44,subQ43,subQ42,subQ41,subQ40,subQ39,subQ38,subQ37,subQ36,subQ35,subQ34,subQ33,subQ32,subQ31,subQ30,subQ29,subQ28,subQ27,subQ26,subQ25,subQ24,subQ23,subQ22,subQ21,subQ20,subQ19,subQ18,subQ17,subQ16,subQ15,subQ14,subQ13,subQ12,subQ11,subQ10,subQ9,subQ8,subQ7,subQ6,subQ5,subQ4,subQ3,subQ2,subQ1,subQ0]),TDD([makeQuery(id+"F1.opExtrude","CAP_FACE",FACE,{"disambiguationData":[OSD([subQ63,subQ62,subQ61,subQ60,subQ59,subQ58,subQ57,subQ56,subQ55,subQ54,subQ53,subQ52,subQ51,subQ50,subQ49,subQ48,subQ47,subQ46,subQ45,subQ44,subQ43,subQ42,subQ41,subQ40,subQ39,subQ38,subQ37,subQ36,subQ35,subQ34,subQ33,subQ32,subQ31,subQ30,subQ29,subQ28,subQ27,subQ26,subQ25,subQ24,subQ23,subQ22,subQ21,subQ20,subQ19,subQ18,subQ17,subQ16,subQ15,subQ14,subQ13,subQ12,subQ11,subQ10,subQ9,subQ8,subQ7,subQ6,subQ5,subQ4,subQ3,subQ2,subQ1,subQ0])],"isStart":false})]),OD(45.0)]});}
            var Q28;
            {var subQ0=sQuery(id+"F0.wireOp",EDGE,"E2.0.10.6");var subQ1=sQuery(id+"F0.wireOp",EDGE,"E2.0.10.5");var subQ2=sQuery(id+"F0.wireOp",EDGE,"E2.0.10.4");var subQ3=sQuery(id+"F0.wireOp",EDGE,"E2.0.10.3");var subQ4=sQuery(id+"F0.wireOp",EDGE,"E2.0.10.2");var subQ5=sQuery(id+"F0.wireOp",EDGE,"E2.0.10.1");var subQ6=sQuery(id+"F0.wireOp",EDGE,"E1.9.6.0");var subQ7=sQuery(id+"F0.wireOp",EDGE,"E1.9.5.0");var subQ8=sQuery(id+"F0.wireOp",EDGE,"E1.9.4.0");var subQ9=sQuery(id+"F0.wireOp",EDGE,"E1.9.3.0");var subQ10=sQuery(id+"F0.wireOp",EDGE,"E1.9.2.0");var subQ11=sQuery(id+"F0.wireOp",EDGE,"E1.9.1.0");var subQ12=sQuery(id+"F0.wireOp",EDGE,"E1.8.6.0");var subQ13=sQuery(id+"F0.wireOp",EDGE,"E1.8.5.0");var subQ14=sQuery(id+"F0.wireOp",EDGE,"E1.8.4.0");var subQ15=sQuery(id+"F0.wireOp",EDGE,"E1.8.3.0");var subQ16=sQuery(id+"F0.wireOp",EDGE,"E1.8.2.0");var subQ17=sQuery(id+"F0.wireOp",EDGE,"E1.8.1.0");var subQ18=sQuery(id+"F0.wireOp",EDGE,"E1.7.6.0");var subQ19=sQuery(id+"F0.wireOp",EDGE,"E1.7.5.0");var subQ20=sQuery(id+"F0.wireOp",EDGE,"E1.7.4.0");var subQ21=sQuery(id+"F0.wireOp",EDGE,"E1.7.3.0");var subQ22=sQuery(id+"F0.wireOp",EDGE,"E1.7.2.0");var subQ23=sQuery(id+"F0.wireOp",EDGE,"E1.7.1.0");var subQ24=sQuery(id+"F0.wireOp",EDGE,"E1.6.6.0");var subQ25=sQuery(id+"F0.wireOp",EDGE,"E1.6.5.0");var subQ26=sQuery(id+"F0.wireOp",EDGE,"E1.6.4.0");var subQ27=sQuery(id+"F0.wireOp",EDGE,"E1.6.3.0");var subQ28=sQuery(id+"F0.wireOp",EDGE,"E1.6.2.0");var subQ29=sQuery(id+"F0.wireOp",EDGE,"E1.6.1.0");var subQ30=sQuery(id+"F0.wireOp",EDGE,"E1.5.6.0");var subQ31=sQuery(id+"F0.wireOp",EDGE,"E1.5.5.0");var subQ32=sQuery(id+"F0.wireOp",EDGE,"E1.5.4.0");var subQ33=sQuery(id+"F0.wireOp",EDGE,"E1.5.3.0");var subQ34=sQuery(id+"F0.wireOp",EDGE,"E1.5.2.0");var subQ35=sQuery(id+"F0.wireOp",EDGE,"E1.5.1.0");var subQ36=sQuery(id+"F0.wireOp",EDGE,"E1.4.6.0");var subQ37=sQuery(id+"F0.wireOp",EDGE,"E1.4.5.0");var subQ38=sQuery(id+"F0.wireOp",EDGE,"E1.4.4.0");var subQ39=sQuery(id+"F0.wireOp",EDGE,"E1.4.3.0");var subQ40=sQuery(id+"F0.wireOp",EDGE,"E1.4.2.0");var subQ41=sQuery(id+"F0.wireOp",EDGE,"E1.4.1.0");var subQ42=sQuery(id+"F0.wireOp",EDGE,"E1.3.6.0");var subQ43=sQuery(id+"F0.wireOp",EDGE,"E1.3.5.0");var subQ44=sQuery(id+"F0.wireOp",EDGE,"E1.3.4.0");var subQ45=sQuery(id+"F0.wireOp",EDGE,"E1.3.3.0");var subQ46=sQuery(id+"F0.wireOp",EDGE,"E1.3.2.0");var subQ47=sQuery(id+"F0.wireOp",EDGE,"E1.3.1.0");var subQ48=sQuery(id+"F0.wireOp",EDGE,"E1.2.6.0");var subQ49=sQuery(id+"F0.wireOp",EDGE,"E1.2.5.0");var subQ50=sQuery(id+"F0.wireOp",EDGE,"E1.2.4.0");var subQ51=sQuery(id+"F0.wireOp",EDGE,"E1.2.3.0");var subQ52=sQuery(id+"F0.wireOp",EDGE,"E1.2.2.0");var subQ53=sQuery(id+"F0.wireOp",EDGE,"E1.2.1.0");var subQ54=sQuery(id+"F0.wireOp",EDGE,"E1.1.6.0");var subQ55=sQuery(id+"F0.wireOp",EDGE,"E1.1.5.0");var subQ56=sQuery(id+"F0.wireOp",EDGE,"E1.1.4.0");var subQ57=sQuery(id+"F0.wireOp",EDGE,"E1.1.3.0");var subQ58=sQuery(id+"F0.wireOp",EDGE,"E1.1.2.0");var subQ59=sQuery(id+"F0.wireOp",EDGE,"E1.1.1.0");var subQ60=sQuery(id+"F0.wireOp",EDGE,"E0.right");var subQ61=sQuery(id+"F0.wireOp",EDGE,"E0.left");var subQ62=sQuery(id+"F0.wireOp",EDGE,"E0.top");var subQ63=sQuery(id+"F0.wireOp",EDGE,"E0.bottom");Q28=makeQuery(id+"F2.opShell","OFFSET_FACE",FACE,{"disambiguationData":[OSD([subQ63,subQ62,subQ61,subQ60,subQ59,subQ58,subQ57,subQ56,subQ55,subQ54,subQ53,subQ52,subQ51,subQ50,subQ49,subQ48,subQ47,subQ46,subQ45,subQ44,subQ43,subQ42,subQ41,subQ40,subQ39,subQ38,subQ37,subQ36,subQ35,subQ34,subQ33,subQ32,subQ31,subQ30,subQ29,subQ28,subQ27,subQ26,subQ25,subQ24,subQ23,subQ22,subQ21,subQ20,subQ19,subQ18,subQ17,subQ16,subQ15,subQ14,subQ13,subQ12,subQ11,subQ10,subQ9,subQ8,subQ7,subQ6,subQ5,subQ4,subQ3,subQ2,subQ1,subQ0]),TDD([makeQuery(id+"F1.opExtrude","CAP_FACE",FACE,{"disambiguationData":[OSD([subQ63,subQ62,subQ61,subQ60,subQ59,subQ58,subQ57,subQ56,subQ55,subQ54,subQ53,subQ52,subQ51,subQ50,subQ49,subQ48,subQ47,subQ46,subQ45,subQ44,subQ43,subQ42,subQ41,subQ40,subQ39,subQ38,subQ37,subQ36,subQ35,subQ34,subQ33,subQ32,subQ31,subQ30,subQ29,subQ28,subQ27,subQ26,subQ25,subQ24,subQ23,subQ22,subQ21,subQ20,subQ19,subQ18,subQ17,subQ16,subQ15,subQ14,subQ13,subQ12,subQ11,subQ10,subQ9,subQ8,subQ7,subQ6,subQ5,subQ4,subQ3,subQ2,subQ1,subQ0])],"isStart":false})]),OD(51.0)]});}
            var Q29;
            {var subQ0=sQuery(id+"F0.wireOp",EDGE,"E2.0.10.6");var subQ1=sQuery(id+"F0.wireOp",EDGE,"E2.0.10.5");var subQ2=sQuery(id+"F0.wireOp",EDGE,"E2.0.10.4");var subQ3=sQuery(id+"F0.wireOp",EDGE,"E2.0.10.3");var subQ4=sQuery(id+"F0.wireOp",EDGE,"E2.0.10.2");var subQ5=sQuery(id+"F0.wireOp",EDGE,"E2.0.10.1");var subQ6=sQuery(id+"F0.wireOp",EDGE,"E1.9.6.0");var subQ7=sQuery(id+"F0.wireOp",EDGE,"E1.9.5.0");var subQ8=sQuery(id+"F0.wireOp",EDGE,"E1.9.4.0");var subQ9=sQuery(id+"F0.wireOp",EDGE,"E1.9.3.0");var subQ10=sQuery(id+"F0.wireOp",EDGE,"E1.9.2.0");var subQ11=sQuery(id+"F0.wireOp",EDGE,"E1.9.1.0");var subQ12=sQuery(id+"F0.wireOp",EDGE,"E1.8.6.0");var subQ13=sQuery(id+"F0.wireOp",EDGE,"E1.8.5.0");var subQ14=sQuery(id+"F0.wireOp",EDGE,"E1.8.4.0");var subQ15=sQuery(id+"F0.wireOp",EDGE,"E1.8.3.0");var subQ16=sQuery(id+"F0.wireOp",EDGE,"E1.8.2.0");var subQ17=sQuery(id+"F0.wireOp",EDGE,"E1.8.1.0");var subQ18=sQuery(id+"F0.wireOp",EDGE,"E1.7.6.0");var subQ19=sQuery(id+"F0.wireOp",EDGE,"E1.7.5.0");var subQ20=sQuery(id+"F0.wireOp",EDGE,"E1.7.4.0");var subQ21=sQuery(id+"F0.wireOp",EDGE,"E1.7.3.0");var subQ22=sQuery(id+"F0.wireOp",EDGE,"E1.7.2.0");var subQ23=sQuery(id+"F0.wireOp",EDGE,"E1.7.1.0");var subQ24=sQuery(id+"F0.wireOp",EDGE,"E1.6.6.0");var subQ25=sQuery(id+"F0.wireOp",EDGE,"E1.6.5.0");var subQ26=sQuery(id+"F0.wireOp",EDGE,"E1.6.4.0");var subQ27=sQuery(id+"F0.wireOp",EDGE,"E1.6.3.0");var subQ28=sQuery(id+"F0.wireOp",EDGE,"E1.6.2.0");var subQ29=sQuery(id+"F0.wireOp",EDGE,"E1.6.1.0");var subQ30=sQuery(id+"F0.wireOp",EDGE,"E1.5.6.0");var subQ31=sQuery(id+"F0.wireOp",EDGE,"E1.5.5.0");var subQ32=sQuery(id+"F0.wireOp",EDGE,"E1.5.4.0");var subQ33=sQuery(id+"F0.wireOp",EDGE,"E1.5.3.0");var subQ34=sQuery(id+"F0.wireOp",EDGE,"E1.5.2.0");var subQ35=sQuery(id+"F0.wireOp",EDGE,"E1.5.1.0");var subQ36=sQuery(id+"F0.wireOp",EDGE,"E1.4.6.0");var subQ37=sQuery(id+"F0.wireOp",EDGE,"E1.4.5.0");var subQ38=sQuery(id+"F0.wireOp",EDGE,"E1.4.4.0");var subQ39=sQuery(id+"F0.wireOp",EDGE,"E1.4.3.0");var subQ40=sQuery(id+"F0.wireOp",EDGE,"E1.4.2.0");var subQ41=sQuery(id+"F0.wireOp",EDGE,"E1.4.1.0");var subQ42=sQuery(id+"F0.wireOp",EDGE,"E1.3.6.0");var subQ43=sQuery(id+"F0.wireOp",EDGE,"E1.3.5.0");var subQ44=sQuery(id+"F0.wireOp",EDGE,"E1.3.4.0");var subQ45=sQuery(id+"F0.wireOp",EDGE,"E1.3.3.0");var subQ46=sQuery(id+"F0.wireOp",EDGE,"E1.3.2.0");var subQ47=sQuery(id+"F0.wireOp",EDGE,"E1.3.1.0");var subQ48=sQuery(id+"F0.wireOp",EDGE,"E1.2.6.0");var subQ49=sQuery(id+"F0.wireOp",EDGE,"E1.2.5.0");var subQ50=sQuery(id+"F0.wireOp",EDGE,"E1.2.4.0");var subQ51=sQuery(id+"F0.wireOp",EDGE,"E1.2.3.0");var subQ52=sQuery(id+"F0.wireOp",EDGE,"E1.2.2.0");var subQ53=sQuery(id+"F0.wireOp",EDGE,"E1.2.1.0");var subQ54=sQuery(id+"F0.wireOp",EDGE,"E1.1.6.0");var subQ55=sQuery(id+"F0.wireOp",EDGE,"E1.1.5.0");var subQ56=sQuery(id+"F0.wireOp",EDGE,"E1.1.4.0");var subQ57=sQuery(id+"F0.wireOp",EDGE,"E1.1.3.0");var subQ58=sQuery(id+"F0.wireOp",EDGE,"E1.1.2.0");var subQ59=sQuery(id+"F0.wireOp",EDGE,"E1.1.1.0");var subQ60=sQuery(id+"F0.wireOp",EDGE,"E0.right");var subQ61=sQuery(id+"F0.wireOp",EDGE,"E0.left");var subQ62=sQuery(id+"F0.wireOp",EDGE,"E0.top");var subQ63=sQuery(id+"F0.wireOp",EDGE,"E0.bottom");Q29=makeQuery(id+"F2.opShell","OFFSET_FACE",FACE,{"disambiguationData":[OSD([subQ63,subQ62,subQ61,subQ60,subQ59,subQ58,subQ57,subQ56,subQ55,subQ54,subQ53,subQ52,subQ51,subQ50,subQ49,subQ48,subQ47,subQ46,subQ45,subQ44,subQ43,subQ42,subQ41,subQ40,subQ39,subQ38,subQ37,subQ36,subQ35,subQ34,subQ33,subQ32,subQ31,subQ30,subQ29,subQ28,subQ27,subQ26,subQ25,subQ24,subQ23,subQ22,subQ21,subQ20,subQ19,subQ18,subQ17,subQ16,subQ15,subQ14,subQ13,subQ12,subQ11,subQ10,subQ9,subQ8,subQ7,subQ6,subQ5,subQ4,subQ3,subQ2,subQ1,subQ0]),TDD([makeQuery(id+"F1.opExtrude","CAP_FACE",FACE,{"disambiguationData":[OSD([subQ63,subQ62,subQ61,subQ60,subQ59,subQ58,subQ57,subQ56,subQ55,subQ54,subQ53,subQ52,subQ51,subQ50,subQ49,subQ48,subQ47,subQ46,subQ45,subQ44,subQ43,subQ42,subQ41,subQ40,subQ39,subQ38,subQ37,subQ36,subQ35,subQ34,subQ33,subQ32,subQ31,subQ30,subQ29,subQ28,subQ27,subQ26,subQ25,subQ24,subQ23,subQ22,subQ21,subQ20,subQ19,subQ18,subQ17,subQ16,subQ15,subQ14,subQ13,subQ12,subQ11,subQ10,subQ9,subQ8,subQ7,subQ6,subQ5,subQ4,subQ3,subQ2,subQ1,subQ0])],"isStart":false})]),OD(57.0)]});}
            var Q30;
            {var subQ0=sQuery(id+"F0.wireOp",EDGE,"E2.0.10.6");var subQ1=sQuery(id+"F0.wireOp",EDGE,"E2.0.10.5");var subQ2=sQuery(id+"F0.wireOp",EDGE,"E2.0.10.4");var subQ3=sQuery(id+"F0.wireOp",EDGE,"E2.0.10.3");var subQ4=sQuery(id+"F0.wireOp",EDGE,"E2.0.10.2");var subQ5=sQuery(id+"F0.wireOp",EDGE,"E2.0.10.1");var subQ6=sQuery(id+"F0.wireOp",EDGE,"E1.9.6.0");var subQ7=sQuery(id+"F0.wireOp",EDGE,"E1.9.5.0");var subQ8=sQuery(id+"F0.wireOp",EDGE,"E1.9.4.0");var subQ9=sQuery(id+"F0.wireOp",EDGE,"E1.9.3.0");var subQ10=sQuery(id+"F0.wireOp",EDGE,"E1.9.2.0");var subQ11=sQuery(id+"F0.wireOp",EDGE,"E1.9.1.0");var subQ12=sQuery(id+"F0.wireOp",EDGE,"E1.8.6.0");var subQ13=sQuery(id+"F0.wireOp",EDGE,"E1.8.5.0");var subQ14=sQuery(id+"F0.wireOp",EDGE,"E1.8.4.0");var subQ15=sQuery(id+"F0.wireOp",EDGE,"E1.8.3.0");var subQ16=sQuery(id+"F0.wireOp",EDGE,"E1.8.2.0");var subQ17=sQuery(id+"F0.wireOp",EDGE,"E1.8.1.0");var subQ18=sQuery(id+"F0.wireOp",EDGE,"E1.7.6.0");var subQ19=sQuery(id+"F0.wireOp",EDGE,"E1.7.5.0");var subQ20=sQuery(id+"F0.wireOp",EDGE,"E1.7.4.0");var subQ21=sQuery(id+"F0.wireOp",EDGE,"E1.7.3.0");var subQ22=sQuery(id+"F0.wireOp",EDGE,"E1.7.2.0");var subQ23=sQuery(id+"F0.wireOp",EDGE,"E1.7.1.0");var subQ24=sQuery(id+"F0.wireOp",EDGE,"E1.6.6.0");var subQ25=sQuery(id+"F0.wireOp",EDGE,"E1.6.5.0");var subQ26=sQuery(id+"F0.wireOp",EDGE,"E1.6.4.0");var subQ27=sQuery(id+"F0.wireOp",EDGE,"E1.6.3.0");var subQ28=sQuery(id+"F0.wireOp",EDGE,"E1.6.2.0");var subQ29=sQuery(id+"F0.wireOp",EDGE,"E1.6.1.0");var subQ30=sQuery(id+"F0.wireOp",EDGE,"E1.5.6.0");var subQ31=sQuery(id+"F0.wireOp",EDGE,"E1.5.5.0");var subQ32=sQuery(id+"F0.wireOp",EDGE,"E1.5.4.0");var subQ33=sQuery(id+"F0.wireOp",EDGE,"E1.5.3.0");var subQ34=sQuery(id+"F0.wireOp",EDGE,"E1.5.2.0");var subQ35=sQuery(id+"F0.wireOp",EDGE,"E1.5.1.0");var subQ36=sQuery(id+"F0.wireOp",EDGE,"E1.4.6.0");var subQ37=sQuery(id+"F0.wireOp",EDGE,"E1.4.5.0");var subQ38=sQuery(id+"F0.wireOp",EDGE,"E1.4.4.0");var subQ39=sQuery(id+"F0.wireOp",EDGE,"E1.4.3.0");var subQ40=sQuery(id+"F0.wireOp",EDGE,"E1.4.2.0");var subQ41=sQuery(id+"F0.wireOp",EDGE,"E1.4.1.0");var subQ42=sQuery(id+"F0.wireOp",EDGE,"E1.3.6.0");var subQ43=sQuery(id+"F0.wireOp",EDGE,"E1.3.5.0");var subQ44=sQuery(id+"F0.wireOp",EDGE,"E1.3.4.0");var subQ45=sQuery(id+"F0.wireOp",EDGE,"E1.3.3.0");var subQ46=sQuery(id+"F0.wireOp",EDGE,"E1.3.2.0");var subQ47=sQuery(id+"F0.wireOp",EDGE,"E1.3.1.0");var subQ48=sQuery(id+"F0.wireOp",EDGE,"E1.2.6.0");var subQ49=sQuery(id+"F0.wireOp",EDGE,"E1.2.5.0");var subQ50=sQuery(id+"F0.wireOp",EDGE,"E1.2.4.0");var subQ51=sQuery(id+"F0.wireOp",EDGE,"E1.2.3.0");var subQ52=sQuery(id+"F0.wireOp",EDGE,"E1.2.2.0");var subQ53=sQuery(id+"F0.wireOp",EDGE,"E1.2.1.0");var subQ54=sQuery(id+"F0.wireOp",EDGE,"E1.1.6.0");var subQ55=sQuery(id+"F0.wireOp",EDGE,"E1.1.5.0");var subQ56=sQuery(id+"F0.wireOp",EDGE,"E1.1.4.0");var subQ57=sQuery(id+"F0.wireOp",EDGE,"E1.1.3.0");var subQ58=sQuery(id+"F0.wireOp",EDGE,"E1.1.2.0");var subQ59=sQuery(id+"F0.wireOp",EDGE,"E1.1.1.0");var subQ60=sQuery(id+"F0.wireOp",EDGE,"E0.right");var subQ61=sQuery(id+"F0.wireOp",EDGE,"E0.left");var subQ62=sQuery(id+"F0.wireOp",EDGE,"E0.top");var subQ63=sQuery(id+"F0.wireOp",EDGE,"E0.bottom");Q30=makeQuery(id+"F2.opShell","OFFSET_FACE",FACE,{"disambiguationData":[OSD([subQ63,subQ62,subQ61,subQ60,subQ59,subQ58,subQ57,subQ56,subQ55,subQ54,subQ53,subQ52,subQ51,subQ50,subQ49,subQ48,subQ47,subQ46,subQ45,subQ44,subQ43,subQ42,subQ41,subQ40,subQ39,subQ38,subQ37,subQ36,subQ35,subQ34,subQ33,subQ32,subQ31,subQ30,subQ29,subQ28,subQ27,subQ26,subQ25,subQ24,subQ23,subQ22,subQ21,subQ20,subQ19,subQ18,subQ17,subQ16,subQ15,subQ14,subQ13,subQ12,subQ11,subQ10,subQ9,subQ8,subQ7,subQ6,subQ5,subQ4,subQ3,subQ2,subQ1,subQ0]),TDD([makeQuery(id+"F1.opExtrude","CAP_FACE",FACE,{"disambiguationData":[OSD([subQ63,subQ62,subQ61,subQ60,subQ59,subQ58,subQ57,subQ56,subQ55,subQ54,subQ53,subQ52,subQ51,subQ50,subQ49,subQ48,subQ47,subQ46,subQ45,subQ44,subQ43,subQ42,subQ41,subQ40,subQ39,subQ38,subQ37,subQ36,subQ35,subQ34,subQ33,subQ32,subQ31,subQ30,subQ29,subQ28,subQ27,subQ26,subQ25,subQ24,subQ23,subQ22,subQ21,subQ20,subQ19,subQ18,subQ17,subQ16,subQ15,subQ14,subQ13,subQ12,subQ11,subQ10,subQ9,subQ8,subQ7,subQ6,subQ5,subQ4,subQ3,subQ2,subQ1,subQ0])],"isStart":false})]),OD(56.0)]});}
            var Q31;
            {var subQ0=sQuery(id+"F0.wireOp",EDGE,"E2.0.10.6");var subQ1=sQuery(id+"F0.wireOp",EDGE,"E2.0.10.5");var subQ2=sQuery(id+"F0.wireOp",EDGE,"E2.0.10.4");var subQ3=sQuery(id+"F0.wireOp",EDGE,"E2.0.10.3");var subQ4=sQuery(id+"F0.wireOp",EDGE,"E2.0.10.2");var subQ5=sQuery(id+"F0.wireOp",EDGE,"E2.0.10.1");var subQ6=sQuery(id+"F0.wireOp",EDGE,"E1.9.6.0");var subQ7=sQuery(id+"F0.wireOp",EDGE,"E1.9.5.0");var subQ8=sQuery(id+"F0.wireOp",EDGE,"E1.9.4.0");var subQ9=sQuery(id+"F0.wireOp",EDGE,"E1.9.3.0");var subQ10=sQuery(id+"F0.wireOp",EDGE,"E1.9.2.0");var subQ11=sQuery(id+"F0.wireOp",EDGE,"E1.9.1.0");var subQ12=sQuery(id+"F0.wireOp",EDGE,"E1.8.6.0");var subQ13=sQuery(id+"F0.wireOp",EDGE,"E1.8.5.0");var subQ14=sQuery(id+"F0.wireOp",EDGE,"E1.8.4.0");var subQ15=sQuery(id+"F0.wireOp",EDGE,"E1.8.3.0");var subQ16=sQuery(id+"F0.wireOp",EDGE,"E1.8.2.0");var subQ17=sQuery(id+"F0.wireOp",EDGE,"E1.8.1.0");var subQ18=sQuery(id+"F0.wireOp",EDGE,"E1.7.6.0");var subQ19=sQuery(id+"F0.wireOp",EDGE,"E1.7.5.0");var subQ20=sQuery(id+"F0.wireOp",EDGE,"E1.7.4.0");var subQ21=sQuery(id+"F0.wireOp",EDGE,"E1.7.3.0");var subQ22=sQuery(id+"F0.wireOp",EDGE,"E1.7.2.0");var subQ23=sQuery(id+"F0.wireOp",EDGE,"E1.7.1.0");var subQ24=sQuery(id+"F0.wireOp",EDGE,"E1.6.6.0");var subQ25=sQuery(id+"F0.wireOp",EDGE,"E1.6.5.0");var subQ26=sQuery(id+"F0.wireOp",EDGE,"E1.6.4.0");var subQ27=sQuery(id+"F0.wireOp",EDGE,"E1.6.3.0");var subQ28=sQuery(id+"F0.wireOp",EDGE,"E1.6.2.0");var subQ29=sQuery(id+"F0.wireOp",EDGE,"E1.6.1.0");var subQ30=sQuery(id+"F0.wireOp",EDGE,"E1.5.6.0");var subQ31=sQuery(id+"F0.wireOp",EDGE,"E1.5.5.0");var subQ32=sQuery(id+"F0.wireOp",EDGE,"E1.5.4.0");var subQ33=sQuery(id+"F0.wireOp",EDGE,"E1.5.3.0");var subQ34=sQuery(id+"F0.wireOp",EDGE,"E1.5.2.0");var subQ35=sQuery(id+"F0.wireOp",EDGE,"E1.5.1.0");var subQ36=sQuery(id+"F0.wireOp",EDGE,"E1.4.6.0");var subQ37=sQuery(id+"F0.wireOp",EDGE,"E1.4.5.0");var subQ38=sQuery(id+"F0.wireOp",EDGE,"E1.4.4.0");var subQ39=sQuery(id+"F0.wireOp",EDGE,"E1.4.3.0");var subQ40=sQuery(id+"F0.wireOp",EDGE,"E1.4.2.0");var subQ41=sQuery(id+"F0.wireOp",EDGE,"E1.4.1.0");var subQ42=sQuery(id+"F0.wireOp",EDGE,"E1.3.6.0");var subQ43=sQuery(id+"F0.wireOp",EDGE,"E1.3.5.0");var subQ44=sQuery(id+"F0.wireOp",EDGE,"E1.3.4.0");var subQ45=sQuery(id+"F0.wireOp",EDGE,"E1.3.3.0");var subQ46=sQuery(id+"F0.wireOp",EDGE,"E1.3.2.0");var subQ47=sQuery(id+"F0.wireOp",EDGE,"E1.3.1.0");var subQ48=sQuery(id+"F0.wireOp",EDGE,"E1.2.6.0");var subQ49=sQuery(id+"F0.wireOp",EDGE,"E1.2.5.0");var subQ50=sQuery(id+"F0.wireOp",EDGE,"E1.2.4.0");var subQ51=sQuery(id+"F0.wireOp",EDGE,"E1.2.3.0");var subQ52=sQuery(id+"F0.wireOp",EDGE,"E1.2.2.0");var subQ53=sQuery(id+"F0.wireOp",EDGE,"E1.2.1.0");var subQ54=sQuery(id+"F0.wireOp",EDGE,"E1.1.6.0");var subQ55=sQuery(id+"F0.wireOp",EDGE,"E1.1.5.0");var subQ56=sQuery(id+"F0.wireOp",EDGE,"E1.1.4.0");var subQ57=sQuery(id+"F0.wireOp",EDGE,"E1.1.3.0");var subQ58=sQuery(id+"F0.wireOp",EDGE,"E1.1.2.0");var subQ59=sQuery(id+"F0.wireOp",EDGE,"E1.1.1.0");var subQ60=sQuery(id+"F0.wireOp",EDGE,"E0.right");var subQ61=sQuery(id+"F0.wireOp",EDGE,"E0.left");var subQ62=sQuery(id+"F0.wireOp",EDGE,"E0.top");var subQ63=sQuery(id+"F0.wireOp",EDGE,"E0.bottom");Q31=makeQuery(id+"F2.opShell","OFFSET_FACE",FACE,{"disambiguationData":[OSD([subQ63,subQ62,subQ61,subQ60,subQ59,subQ58,subQ57,subQ56,subQ55,subQ54,subQ53,subQ52,subQ51,subQ50,subQ49,subQ48,subQ47,subQ46,subQ45,subQ44,subQ43,subQ42,subQ41,subQ40,subQ39,subQ38,subQ37,subQ36,subQ35,subQ34,subQ33,subQ32,subQ31,subQ30,subQ29,subQ28,subQ27,subQ26,subQ25,subQ24,subQ23,subQ22,subQ21,subQ20,subQ19,subQ18,subQ17,subQ16,subQ15,subQ14,subQ13,subQ12,subQ11,subQ10,subQ9,subQ8,subQ7,subQ6,subQ5,subQ4,subQ3,subQ2,subQ1,subQ0]),TDD([makeQuery(id+"F1.opExtrude","CAP_FACE",FACE,{"disambiguationData":[OSD([subQ63,subQ62,subQ61,subQ60,subQ59,subQ58,subQ57,subQ56,subQ55,subQ54,subQ53,subQ52,subQ51,subQ50,subQ49,subQ48,subQ47,subQ46,subQ45,subQ44,subQ43,subQ42,subQ41,subQ40,subQ39,subQ38,subQ37,subQ36,subQ35,subQ34,subQ33,subQ32,subQ31,subQ30,subQ29,subQ28,subQ27,subQ26,subQ25,subQ24,subQ23,subQ22,subQ21,subQ20,subQ19,subQ18,subQ17,subQ16,subQ15,subQ14,subQ13,subQ12,subQ11,subQ10,subQ9,subQ8,subQ7,subQ6,subQ5,subQ4,subQ3,subQ2,subQ1,subQ0])],"isStart":false})]),OD(50.0)]});}
            var Q32;
            {var subQ0=sQuery(id+"F0.wireOp",EDGE,"E2.0.10.6");var subQ1=sQuery(id+"F0.wireOp",EDGE,"E2.0.10.5");var subQ2=sQuery(id+"F0.wireOp",EDGE,"E2.0.10.4");var subQ3=sQuery(id+"F0.wireOp",EDGE,"E2.0.10.3");var subQ4=sQuery(id+"F0.wireOp",EDGE,"E2.0.10.2");var subQ5=sQuery(id+"F0.wireOp",EDGE,"E2.0.10.1");var subQ6=sQuery(id+"F0.wireOp",EDGE,"E1.9.6.0");var subQ7=sQuery(id+"F0.wireOp",EDGE,"E1.9.5.0");var subQ8=sQuery(id+"F0.wireOp",EDGE,"E1.9.4.0");var subQ9=sQuery(id+"F0.wireOp",EDGE,"E1.9.3.0");var subQ10=sQuery(id+"F0.wireOp",EDGE,"E1.9.2.0");var subQ11=sQuery(id+"F0.wireOp",EDGE,"E1.9.1.0");var subQ12=sQuery(id+"F0.wireOp",EDGE,"E1.8.6.0");var subQ13=sQuery(id+"F0.wireOp",EDGE,"E1.8.5.0");var subQ14=sQuery(id+"F0.wireOp",EDGE,"E1.8.4.0");var subQ15=sQuery(id+"F0.wireOp",EDGE,"E1.8.3.0");var subQ16=sQuery(id+"F0.wireOp",EDGE,"E1.8.2.0");var subQ17=sQuery(id+"F0.wireOp",EDGE,"E1.8.1.0");var subQ18=sQuery(id+"F0.wireOp",EDGE,"E1.7.6.0");var subQ19=sQuery(id+"F0.wireOp",EDGE,"E1.7.5.0");var subQ20=sQuery(id+"F0.wireOp",EDGE,"E1.7.4.0");var subQ21=sQuery(id+"F0.wireOp",EDGE,"E1.7.3.0");var subQ22=sQuery(id+"F0.wireOp",EDGE,"E1.7.2.0");var subQ23=sQuery(id+"F0.wireOp",EDGE,"E1.7.1.0");var subQ24=sQuery(id+"F0.wireOp",EDGE,"E1.6.6.0");var subQ25=sQuery(id+"F0.wireOp",EDGE,"E1.6.5.0");var subQ26=sQuery(id+"F0.wireOp",EDGE,"E1.6.4.0");var subQ27=sQuery(id+"F0.wireOp",EDGE,"E1.6.3.0");var subQ28=sQuery(id+"F0.wireOp",EDGE,"E1.6.2.0");var subQ29=sQuery(id+"F0.wireOp",EDGE,"E1.6.1.0");var subQ30=sQuery(id+"F0.wireOp",EDGE,"E1.5.6.0");var subQ31=sQuery(id+"F0.wireOp",EDGE,"E1.5.5.0");var subQ32=sQuery(id+"F0.wireOp",EDGE,"E1.5.4.0");var subQ33=sQuery(id+"F0.wireOp",EDGE,"E1.5.3.0");var subQ34=sQuery(id+"F0.wireOp",EDGE,"E1.5.2.0");var subQ35=sQuery(id+"F0.wireOp",EDGE,"E1.5.1.0");var subQ36=sQuery(id+"F0.wireOp",EDGE,"E1.4.6.0");var subQ37=sQuery(id+"F0.wireOp",EDGE,"E1.4.5.0");var subQ38=sQuery(id+"F0.wireOp",EDGE,"E1.4.4.0");var subQ39=sQuery(id+"F0.wireOp",EDGE,"E1.4.3.0");var subQ40=sQuery(id+"F0.wireOp",EDGE,"E1.4.2.0");var subQ41=sQuery(id+"F0.wireOp",EDGE,"E1.4.1.0");var subQ42=sQuery(id+"F0.wireOp",EDGE,"E1.3.6.0");var subQ43=sQuery(id+"F0.wireOp",EDGE,"E1.3.5.0");var subQ44=sQuery(id+"F0.wireOp",EDGE,"E1.3.4.0");var subQ45=sQuery(id+"F0.wireOp",EDGE,"E1.3.3.0");var subQ46=sQuery(id+"F0.wireOp",EDGE,"E1.3.2.0");var subQ47=sQuery(id+"F0.wireOp",EDGE,"E1.3.1.0");var subQ48=sQuery(id+"F0.wireOp",EDGE,"E1.2.6.0");var subQ49=sQuery(id+"F0.wireOp",EDGE,"E1.2.5.0");var subQ50=sQuery(id+"F0.wireOp",EDGE,"E1.2.4.0");var subQ51=sQuery(id+"F0.wireOp",EDGE,"E1.2.3.0");var subQ52=sQuery(id+"F0.wireOp",EDGE,"E1.2.2.0");var subQ53=sQuery(id+"F0.wireOp",EDGE,"E1.2.1.0");var subQ54=sQuery(id+"F0.wireOp",EDGE,"E1.1.6.0");var subQ55=sQuery(id+"F0.wireOp",EDGE,"E1.1.5.0");var subQ56=sQuery(id+"F0.wireOp",EDGE,"E1.1.4.0");var subQ57=sQuery(id+"F0.wireOp",EDGE,"E1.1.3.0");var subQ58=sQuery(id+"F0.wireOp",EDGE,"E1.1.2.0");var subQ59=sQuery(id+"F0.wireOp",EDGE,"E1.1.1.0");var subQ60=sQuery(id+"F0.wireOp",EDGE,"E0.right");var subQ61=sQuery(id+"F0.wireOp",EDGE,"E0.left");var subQ62=sQuery(id+"F0.wireOp",EDGE,"E0.top");var subQ63=sQuery(id+"F0.wireOp",EDGE,"E0.bottom");Q32=makeQuery(id+"F2.opShell","OFFSET_FACE",FACE,{"disambiguationData":[OSD([subQ63,subQ62,subQ61,subQ60,subQ59,subQ58,subQ57,subQ56,subQ55,subQ54,subQ53,subQ52,subQ51,subQ50,subQ49,subQ48,subQ47,subQ46,subQ45,subQ44,subQ43,subQ42,subQ41,subQ40,subQ39,subQ38,subQ37,subQ36,subQ35,subQ34,subQ33,subQ32,subQ31,subQ30,subQ29,subQ28,subQ27,subQ26,subQ25,subQ24,subQ23,subQ22,subQ21,subQ20,subQ19,subQ18,subQ17,subQ16,subQ15,subQ14,subQ13,subQ12,subQ11,subQ10,subQ9,subQ8,subQ7,subQ6,subQ5,subQ4,subQ3,subQ2,subQ1,subQ0]),TDD([makeQuery(id+"F1.opExtrude","CAP_FACE",FACE,{"disambiguationData":[OSD([subQ63,subQ62,subQ61,subQ60,subQ59,subQ58,subQ57,subQ56,subQ55,subQ54,subQ53,subQ52,subQ51,subQ50,subQ49,subQ48,subQ47,subQ46,subQ45,subQ44,subQ43,subQ42,subQ41,subQ40,subQ39,subQ38,subQ37,subQ36,subQ35,subQ34,subQ33,subQ32,subQ31,subQ30,subQ29,subQ28,subQ27,subQ26,subQ25,subQ24,subQ23,subQ22,subQ21,subQ20,subQ19,subQ18,subQ17,subQ16,subQ15,subQ14,subQ13,subQ12,subQ11,subQ10,subQ9,subQ8,subQ7,subQ6,subQ5,subQ4,subQ3,subQ2,subQ1,subQ0])],"isStart":false})]),OD(44.0)]});}
            var Q33;
            {var subQ0=sQuery(id+"F0.wireOp",EDGE,"E2.0.10.6");var subQ1=sQuery(id+"F0.wireOp",EDGE,"E2.0.10.5");var subQ2=sQuery(id+"F0.wireOp",EDGE,"E2.0.10.4");var subQ3=sQuery(id+"F0.wireOp",EDGE,"E2.0.10.3");var subQ4=sQuery(id+"F0.wireOp",EDGE,"E2.0.10.2");var subQ5=sQuery(id+"F0.wireOp",EDGE,"E2.0.10.1");var subQ6=sQuery(id+"F0.wireOp",EDGE,"E1.9.6.0");var subQ7=sQuery(id+"F0.wireOp",EDGE,"E1.9.5.0");var subQ8=sQuery(id+"F0.wireOp",EDGE,"E1.9.4.0");var subQ9=sQuery(id+"F0.wireOp",EDGE,"E1.9.3.0");var subQ10=sQuery(id+"F0.wireOp",EDGE,"E1.9.2.0");var subQ11=sQuery(id+"F0.wireOp",EDGE,"E1.9.1.0");var subQ12=sQuery(id+"F0.wireOp",EDGE,"E1.8.6.0");var subQ13=sQuery(id+"F0.wireOp",EDGE,"E1.8.5.0");var subQ14=sQuery(id+"F0.wireOp",EDGE,"E1.8.4.0");var subQ15=sQuery(id+"F0.wireOp",EDGE,"E1.8.3.0");var subQ16=sQuery(id+"F0.wireOp",EDGE,"E1.8.2.0");var subQ17=sQuery(id+"F0.wireOp",EDGE,"E1.8.1.0");var subQ18=sQuery(id+"F0.wireOp",EDGE,"E1.7.6.0");var subQ19=sQuery(id+"F0.wireOp",EDGE,"E1.7.5.0");var subQ20=sQuery(id+"F0.wireOp",EDGE,"E1.7.4.0");var subQ21=sQuery(id+"F0.wireOp",EDGE,"E1.7.3.0");var subQ22=sQuery(id+"F0.wireOp",EDGE,"E1.7.2.0");var subQ23=sQuery(id+"F0.wireOp",EDGE,"E1.7.1.0");var subQ24=sQuery(id+"F0.wireOp",EDGE,"E1.6.6.0");var subQ25=sQuery(id+"F0.wireOp",EDGE,"E1.6.5.0");var subQ26=sQuery(id+"F0.wireOp",EDGE,"E1.6.4.0");var subQ27=sQuery(id+"F0.wireOp",EDGE,"E1.6.3.0");var subQ28=sQuery(id+"F0.wireOp",EDGE,"E1.6.2.0");var subQ29=sQuery(id+"F0.wireOp",EDGE,"E1.6.1.0");var subQ30=sQuery(id+"F0.wireOp",EDGE,"E1.5.6.0");var subQ31=sQuery(id+"F0.wireOp",EDGE,"E1.5.5.0");var subQ32=sQuery(id+"F0.wireOp",EDGE,"E1.5.4.0");var subQ33=sQuery(id+"F0.wireOp",EDGE,"E1.5.3.0");var subQ34=sQuery(id+"F0.wireOp",EDGE,"E1.5.2.0");var subQ35=sQuery(id+"F0.wireOp",EDGE,"E1.5.1.0");var subQ36=sQuery(id+"F0.wireOp",EDGE,"E1.4.6.0");var subQ37=sQuery(id+"F0.wireOp",EDGE,"E1.4.5.0");var subQ38=sQuery(id+"F0.wireOp",EDGE,"E1.4.4.0");var subQ39=sQuery(id+"F0.wireOp",EDGE,"E1.4.3.0");var subQ40=sQuery(id+"F0.wireOp",EDGE,"E1.4.2.0");var subQ41=sQuery(id+"F0.wireOp",EDGE,"E1.4.1.0");var subQ42=sQuery(id+"F0.wireOp",EDGE,"E1.3.6.0");var subQ43=sQuery(id+"F0.wireOp",EDGE,"E1.3.5.0");var subQ44=sQuery(id+"F0.wireOp",EDGE,"E1.3.4.0");var subQ45=sQuery(id+"F0.wireOp",EDGE,"E1.3.3.0");var subQ46=sQuery(id+"F0.wireOp",EDGE,"E1.3.2.0");var subQ47=sQuery(id+"F0.wireOp",EDGE,"E1.3.1.0");var subQ48=sQuery(id+"F0.wireOp",EDGE,"E1.2.6.0");var subQ49=sQuery(id+"F0.wireOp",EDGE,"E1.2.5.0");var subQ50=sQuery(id+"F0.wireOp",EDGE,"E1.2.4.0");var subQ51=sQuery(id+"F0.wireOp",EDGE,"E1.2.3.0");var subQ52=sQuery(id+"F0.wireOp",EDGE,"E1.2.2.0");var subQ53=sQuery(id+"F0.wireOp",EDGE,"E1.2.1.0");var subQ54=sQuery(id+"F0.wireOp",EDGE,"E1.1.6.0");var subQ55=sQuery(id+"F0.wireOp",EDGE,"E1.1.5.0");var subQ56=sQuery(id+"F0.wireOp",EDGE,"E1.1.4.0");var subQ57=sQuery(id+"F0.wireOp",EDGE,"E1.1.3.0");var subQ58=sQuery(id+"F0.wireOp",EDGE,"E1.1.2.0");var subQ59=sQuery(id+"F0.wireOp",EDGE,"E1.1.1.0");var subQ60=sQuery(id+"F0.wireOp",EDGE,"E0.right");var subQ61=sQuery(id+"F0.wireOp",EDGE,"E0.left");var subQ62=sQuery(id+"F0.wireOp",EDGE,"E0.top");var subQ63=sQuery(id+"F0.wireOp",EDGE,"E0.bottom");Q33=makeQuery(id+"F2.opShell","OFFSET_FACE",FACE,{"disambiguationData":[OSD([subQ63,subQ62,subQ61,subQ60,subQ59,subQ58,subQ57,subQ56,subQ55,subQ54,subQ53,subQ52,subQ51,subQ50,subQ49,subQ48,subQ47,subQ46,subQ45,subQ44,subQ43,subQ42,subQ41,subQ40,subQ39,subQ38,subQ37,subQ36,subQ35,subQ34,subQ33,subQ32,subQ31,subQ30,subQ29,subQ28,subQ27,subQ26,subQ25,subQ24,subQ23,subQ22,subQ21,subQ20,subQ19,subQ18,subQ17,subQ16,subQ15,subQ14,subQ13,subQ12,subQ11,subQ10,subQ9,subQ8,subQ7,subQ6,subQ5,subQ4,subQ3,subQ2,subQ1,subQ0]),TDD([makeQuery(id+"F1.opExtrude","CAP_FACE",FACE,{"disambiguationData":[OSD([subQ63,subQ62,subQ61,subQ60,subQ59,subQ58,subQ57,subQ56,subQ55,subQ54,subQ53,subQ52,subQ51,subQ50,subQ49,subQ48,subQ47,subQ46,subQ45,subQ44,subQ43,subQ42,subQ41,subQ40,subQ39,subQ38,subQ37,subQ36,subQ35,subQ34,subQ33,subQ32,subQ31,subQ30,subQ29,subQ28,subQ27,subQ26,subQ25,subQ24,subQ23,subQ22,subQ21,subQ20,subQ19,subQ18,subQ17,subQ16,subQ15,subQ14,subQ13,subQ12,subQ11,subQ10,subQ9,subQ8,subQ7,subQ6,subQ5,subQ4,subQ3,subQ2,subQ1,subQ0])],"isStart":false})]),OD(38.0)]});}
            var Q34;
            {var subQ0=sQuery(id+"F0.wireOp",EDGE,"E2.0.10.6");var subQ1=sQuery(id+"F0.wireOp",EDGE,"E2.0.10.5");var subQ2=sQuery(id+"F0.wireOp",EDGE,"E2.0.10.4");var subQ3=sQuery(id+"F0.wireOp",EDGE,"E2.0.10.3");var subQ4=sQuery(id+"F0.wireOp",EDGE,"E2.0.10.2");var subQ5=sQuery(id+"F0.wireOp",EDGE,"E2.0.10.1");var subQ6=sQuery(id+"F0.wireOp",EDGE,"E1.9.6.0");var subQ7=sQuery(id+"F0.wireOp",EDGE,"E1.9.5.0");var subQ8=sQuery(id+"F0.wireOp",EDGE,"E1.9.4.0");var subQ9=sQuery(id+"F0.wireOp",EDGE,"E1.9.3.0");var subQ10=sQuery(id+"F0.wireOp",EDGE,"E1.9.2.0");var subQ11=sQuery(id+"F0.wireOp",EDGE,"E1.9.1.0");var subQ12=sQuery(id+"F0.wireOp",EDGE,"E1.8.6.0");var subQ13=sQuery(id+"F0.wireOp",EDGE,"E1.8.5.0");var subQ14=sQuery(id+"F0.wireOp",EDGE,"E1.8.4.0");var subQ15=sQuery(id+"F0.wireOp",EDGE,"E1.8.3.0");var subQ16=sQuery(id+"F0.wireOp",EDGE,"E1.8.2.0");var subQ17=sQuery(id+"F0.wireOp",EDGE,"E1.8.1.0");var subQ18=sQuery(id+"F0.wireOp",EDGE,"E1.7.6.0");var subQ19=sQuery(id+"F0.wireOp",EDGE,"E1.7.5.0");var subQ20=sQuery(id+"F0.wireOp",EDGE,"E1.7.4.0");var subQ21=sQuery(id+"F0.wireOp",EDGE,"E1.7.3.0");var subQ22=sQuery(id+"F0.wireOp",EDGE,"E1.7.2.0");var subQ23=sQuery(id+"F0.wireOp",EDGE,"E1.7.1.0");var subQ24=sQuery(id+"F0.wireOp",EDGE,"E1.6.6.0");var subQ25=sQuery(id+"F0.wireOp",EDGE,"E1.6.5.0");var subQ26=sQuery(id+"F0.wireOp",EDGE,"E1.6.4.0");var subQ27=sQuery(id+"F0.wireOp",EDGE,"E1.6.3.0");var subQ28=sQuery(id+"F0.wireOp",EDGE,"E1.6.2.0");var subQ29=sQuery(id+"F0.wireOp",EDGE,"E1.6.1.0");var subQ30=sQuery(id+"F0.wireOp",EDGE,"E1.5.6.0");var subQ31=sQuery(id+"F0.wireOp",EDGE,"E1.5.5.0");var subQ32=sQuery(id+"F0.wireOp",EDGE,"E1.5.4.0");var subQ33=sQuery(id+"F0.wireOp",EDGE,"E1.5.3.0");var subQ34=sQuery(id+"F0.wireOp",EDGE,"E1.5.2.0");var subQ35=sQuery(id+"F0.wireOp",EDGE,"E1.5.1.0");var subQ36=sQuery(id+"F0.wireOp",EDGE,"E1.4.6.0");var subQ37=sQuery(id+"F0.wireOp",EDGE,"E1.4.5.0");var subQ38=sQuery(id+"F0.wireOp",EDGE,"E1.4.4.0");var subQ39=sQuery(id+"F0.wireOp",EDGE,"E1.4.3.0");var subQ40=sQuery(id+"F0.wireOp",EDGE,"E1.4.2.0");var subQ41=sQuery(id+"F0.wireOp",EDGE,"E1.4.1.0");var subQ42=sQuery(id+"F0.wireOp",EDGE,"E1.3.6.0");var subQ43=sQuery(id+"F0.wireOp",EDGE,"E1.3.5.0");var subQ44=sQuery(id+"F0.wireOp",EDGE,"E1.3.4.0");var subQ45=sQuery(id+"F0.wireOp",EDGE,"E1.3.3.0");var subQ46=sQuery(id+"F0.wireOp",EDGE,"E1.3.2.0");var subQ47=sQuery(id+"F0.wireOp",EDGE,"E1.3.1.0");var subQ48=sQuery(id+"F0.wireOp",EDGE,"E1.2.6.0");var subQ49=sQuery(id+"F0.wireOp",EDGE,"E1.2.5.0");var subQ50=sQuery(id+"F0.wireOp",EDGE,"E1.2.4.0");var subQ51=sQuery(id+"F0.wireOp",EDGE,"E1.2.3.0");var subQ52=sQuery(id+"F0.wireOp",EDGE,"E1.2.2.0");var subQ53=sQuery(id+"F0.wireOp",EDGE,"E1.2.1.0");var subQ54=sQuery(id+"F0.wireOp",EDGE,"E1.1.6.0");var subQ55=sQuery(id+"F0.wireOp",EDGE,"E1.1.5.0");var subQ56=sQuery(id+"F0.wireOp",EDGE,"E1.1.4.0");var subQ57=sQuery(id+"F0.wireOp",EDGE,"E1.1.3.0");var subQ58=sQuery(id+"F0.wireOp",EDGE,"E1.1.2.0");var subQ59=sQuery(id+"F0.wireOp",EDGE,"E1.1.1.0");var subQ60=sQuery(id+"F0.wireOp",EDGE,"E0.right");var subQ61=sQuery(id+"F0.wireOp",EDGE,"E0.left");var subQ62=sQuery(id+"F0.wireOp",EDGE,"E0.top");var subQ63=sQuery(id+"F0.wireOp",EDGE,"E0.bottom");Q34=makeQuery(id+"F2.opShell","OFFSET_FACE",FACE,{"disambiguationData":[OSD([subQ63,subQ62,subQ61,subQ60,subQ59,subQ58,subQ57,subQ56,subQ55,subQ54,subQ53,subQ52,subQ51,subQ50,subQ49,subQ48,subQ47,subQ46,subQ45,subQ44,subQ43,subQ42,subQ41,subQ40,subQ39,subQ38,subQ37,subQ36,subQ35,subQ34,subQ33,subQ32,subQ31,subQ30,subQ29,subQ28,subQ27,subQ26,subQ25,subQ24,subQ23,subQ22,subQ21,subQ20,subQ19,subQ18,subQ17,subQ16,subQ15,subQ14,subQ13,subQ12,subQ11,subQ10,subQ9,subQ8,subQ7,subQ6,subQ5,subQ4,subQ3,subQ2,subQ1,subQ0]),TDD([makeQuery(id+"F1.opExtrude","CAP_FACE",FACE,{"disambiguationData":[OSD([subQ63,subQ62,subQ61,subQ60,subQ59,subQ58,subQ57,subQ56,subQ55,subQ54,subQ53,subQ52,subQ51,subQ50,subQ49,subQ48,subQ47,subQ46,subQ45,subQ44,subQ43,subQ42,subQ41,subQ40,subQ39,subQ38,subQ37,subQ36,subQ35,subQ34,subQ33,subQ32,subQ31,subQ30,subQ29,subQ28,subQ27,subQ26,subQ25,subQ24,subQ23,subQ22,subQ21,subQ20,subQ19,subQ18,subQ17,subQ16,subQ15,subQ14,subQ13,subQ12,subQ11,subQ10,subQ9,subQ8,subQ7,subQ6,subQ5,subQ4,subQ3,subQ2,subQ1,subQ0])],"isStart":false})]),OD(32.0)]});}
            var Q35;
            {var subQ0=sQuery(id+"F0.wireOp",EDGE,"E2.0.10.6");var subQ1=sQuery(id+"F0.wireOp",EDGE,"E2.0.10.5");var subQ2=sQuery(id+"F0.wireOp",EDGE,"E2.0.10.4");var subQ3=sQuery(id+"F0.wireOp",EDGE,"E2.0.10.3");var subQ4=sQuery(id+"F0.wireOp",EDGE,"E2.0.10.2");var subQ5=sQuery(id+"F0.wireOp",EDGE,"E2.0.10.1");var subQ6=sQuery(id+"F0.wireOp",EDGE,"E1.9.6.0");var subQ7=sQuery(id+"F0.wireOp",EDGE,"E1.9.5.0");var subQ8=sQuery(id+"F0.wireOp",EDGE,"E1.9.4.0");var subQ9=sQuery(id+"F0.wireOp",EDGE,"E1.9.3.0");var subQ10=sQuery(id+"F0.wireOp",EDGE,"E1.9.2.0");var subQ11=sQuery(id+"F0.wireOp",EDGE,"E1.9.1.0");var subQ12=sQuery(id+"F0.wireOp",EDGE,"E1.8.6.0");var subQ13=sQuery(id+"F0.wireOp",EDGE,"E1.8.5.0");var subQ14=sQuery(id+"F0.wireOp",EDGE,"E1.8.4.0");var subQ15=sQuery(id+"F0.wireOp",EDGE,"E1.8.3.0");var subQ16=sQuery(id+"F0.wireOp",EDGE,"E1.8.2.0");var subQ17=sQuery(id+"F0.wireOp",EDGE,"E1.8.1.0");var subQ18=sQuery(id+"F0.wireOp",EDGE,"E1.7.6.0");var subQ19=sQuery(id+"F0.wireOp",EDGE,"E1.7.5.0");var subQ20=sQuery(id+"F0.wireOp",EDGE,"E1.7.4.0");var subQ21=sQuery(id+"F0.wireOp",EDGE,"E1.7.3.0");var subQ22=sQuery(id+"F0.wireOp",EDGE,"E1.7.2.0");var subQ23=sQuery(id+"F0.wireOp",EDGE,"E1.7.1.0");var subQ24=sQuery(id+"F0.wireOp",EDGE,"E1.6.6.0");var subQ25=sQuery(id+"F0.wireOp",EDGE,"E1.6.5.0");var subQ26=sQuery(id+"F0.wireOp",EDGE,"E1.6.4.0");var subQ27=sQuery(id+"F0.wireOp",EDGE,"E1.6.3.0");var subQ28=sQuery(id+"F0.wireOp",EDGE,"E1.6.2.0");var subQ29=sQuery(id+"F0.wireOp",EDGE,"E1.6.1.0");var subQ30=sQuery(id+"F0.wireOp",EDGE,"E1.5.6.0");var subQ31=sQuery(id+"F0.wireOp",EDGE,"E1.5.5.0");var subQ32=sQuery(id+"F0.wireOp",EDGE,"E1.5.4.0");var subQ33=sQuery(id+"F0.wireOp",EDGE,"E1.5.3.0");var subQ34=sQuery(id+"F0.wireOp",EDGE,"E1.5.2.0");var subQ35=sQuery(id+"F0.wireOp",EDGE,"E1.5.1.0");var subQ36=sQuery(id+"F0.wireOp",EDGE,"E1.4.6.0");var subQ37=sQuery(id+"F0.wireOp",EDGE,"E1.4.5.0");var subQ38=sQuery(id+"F0.wireOp",EDGE,"E1.4.4.0");var subQ39=sQuery(id+"F0.wireOp",EDGE,"E1.4.3.0");var subQ40=sQuery(id+"F0.wireOp",EDGE,"E1.4.2.0");var subQ41=sQuery(id+"F0.wireOp",EDGE,"E1.4.1.0");var subQ42=sQuery(id+"F0.wireOp",EDGE,"E1.3.6.0");var subQ43=sQuery(id+"F0.wireOp",EDGE,"E1.3.5.0");var subQ44=sQuery(id+"F0.wireOp",EDGE,"E1.3.4.0");var subQ45=sQuery(id+"F0.wireOp",EDGE,"E1.3.3.0");var subQ46=sQuery(id+"F0.wireOp",EDGE,"E1.3.2.0");var subQ47=sQuery(id+"F0.wireOp",EDGE,"E1.3.1.0");var subQ48=sQuery(id+"F0.wireOp",EDGE,"E1.2.6.0");var subQ49=sQuery(id+"F0.wireOp",EDGE,"E1.2.5.0");var subQ50=sQuery(id+"F0.wireOp",EDGE,"E1.2.4.0");var subQ51=sQuery(id+"F0.wireOp",EDGE,"E1.2.3.0");var subQ52=sQuery(id+"F0.wireOp",EDGE,"E1.2.2.0");var subQ53=sQuery(id+"F0.wireOp",EDGE,"E1.2.1.0");var subQ54=sQuery(id+"F0.wireOp",EDGE,"E1.1.6.0");var subQ55=sQuery(id+"F0.wireOp",EDGE,"E1.1.5.0");var subQ56=sQuery(id+"F0.wireOp",EDGE,"E1.1.4.0");var subQ57=sQuery(id+"F0.wireOp",EDGE,"E1.1.3.0");var subQ58=sQuery(id+"F0.wireOp",EDGE,"E1.1.2.0");var subQ59=sQuery(id+"F0.wireOp",EDGE,"E1.1.1.0");var subQ60=sQuery(id+"F0.wireOp",EDGE,"E0.right");var subQ61=sQuery(id+"F0.wireOp",EDGE,"E0.left");var subQ62=sQuery(id+"F0.wireOp",EDGE,"E0.top");var subQ63=sQuery(id+"F0.wireOp",EDGE,"E0.bottom");Q35=makeQuery(id+"F2.opShell","OFFSET_FACE",FACE,{"disambiguationData":[OSD([subQ63,subQ62,subQ61,subQ60,subQ59,subQ58,subQ57,subQ56,subQ55,subQ54,subQ53,subQ52,subQ51,subQ50,subQ49,subQ48,subQ47,subQ46,subQ45,subQ44,subQ43,subQ42,subQ41,subQ40,subQ39,subQ38,subQ37,subQ36,subQ35,subQ34,subQ33,subQ32,subQ31,subQ30,subQ29,subQ28,subQ27,subQ26,subQ25,subQ24,subQ23,subQ22,subQ21,subQ20,subQ19,subQ18,subQ17,subQ16,subQ15,subQ14,subQ13,subQ12,subQ11,subQ10,subQ9,subQ8,subQ7,subQ6,subQ5,subQ4,subQ3,subQ2,subQ1,subQ0]),TDD([makeQuery(id+"F1.opExtrude","CAP_FACE",FACE,{"disambiguationData":[OSD([subQ63,subQ62,subQ61,subQ60,subQ59,subQ58,subQ57,subQ56,subQ55,subQ54,subQ53,subQ52,subQ51,subQ50,subQ49,subQ48,subQ47,subQ46,subQ45,subQ44,subQ43,subQ42,subQ41,subQ40,subQ39,subQ38,subQ37,subQ36,subQ35,subQ34,subQ33,subQ32,subQ31,subQ30,subQ29,subQ28,subQ27,subQ26,subQ25,subQ24,subQ23,subQ22,subQ21,subQ20,subQ19,subQ18,subQ17,subQ16,subQ15,subQ14,subQ13,subQ12,subQ11,subQ10,subQ9,subQ8,subQ7,subQ6,subQ5,subQ4,subQ3,subQ2,subQ1,subQ0])],"isStart":false})]),OD(26.0)]});}
            var Q36;
            {var subQ0=sQuery(id+"F0.wireOp",EDGE,"E2.0.10.6");var subQ1=sQuery(id+"F0.wireOp",EDGE,"E2.0.10.5");var subQ2=sQuery(id+"F0.wireOp",EDGE,"E2.0.10.4");var subQ3=sQuery(id+"F0.wireOp",EDGE,"E2.0.10.3");var subQ4=sQuery(id+"F0.wireOp",EDGE,"E2.0.10.2");var subQ5=sQuery(id+"F0.wireOp",EDGE,"E2.0.10.1");var subQ6=sQuery(id+"F0.wireOp",EDGE,"E1.9.6.0");var subQ7=sQuery(id+"F0.wireOp",EDGE,"E1.9.5.0");var subQ8=sQuery(id+"F0.wireOp",EDGE,"E1.9.4.0");var subQ9=sQuery(id+"F0.wireOp",EDGE,"E1.9.3.0");var subQ10=sQuery(id+"F0.wireOp",EDGE,"E1.9.2.0");var subQ11=sQuery(id+"F0.wireOp",EDGE,"E1.9.1.0");var subQ12=sQuery(id+"F0.wireOp",EDGE,"E1.8.6.0");var subQ13=sQuery(id+"F0.wireOp",EDGE,"E1.8.5.0");var subQ14=sQuery(id+"F0.wireOp",EDGE,"E1.8.4.0");var subQ15=sQuery(id+"F0.wireOp",EDGE,"E1.8.3.0");var subQ16=sQuery(id+"F0.wireOp",EDGE,"E1.8.2.0");var subQ17=sQuery(id+"F0.wireOp",EDGE,"E1.8.1.0");var subQ18=sQuery(id+"F0.wireOp",EDGE,"E1.7.6.0");var subQ19=sQuery(id+"F0.wireOp",EDGE,"E1.7.5.0");var subQ20=sQuery(id+"F0.wireOp",EDGE,"E1.7.4.0");var subQ21=sQuery(id+"F0.wireOp",EDGE,"E1.7.3.0");var subQ22=sQuery(id+"F0.wireOp",EDGE,"E1.7.2.0");var subQ23=sQuery(id+"F0.wireOp",EDGE,"E1.7.1.0");var subQ24=sQuery(id+"F0.wireOp",EDGE,"E1.6.6.0");var subQ25=sQuery(id+"F0.wireOp",EDGE,"E1.6.5.0");var subQ26=sQuery(id+"F0.wireOp",EDGE,"E1.6.4.0");var subQ27=sQuery(id+"F0.wireOp",EDGE,"E1.6.3.0");var subQ28=sQuery(id+"F0.wireOp",EDGE,"E1.6.2.0");var subQ29=sQuery(id+"F0.wireOp",EDGE,"E1.6.1.0");var subQ30=sQuery(id+"F0.wireOp",EDGE,"E1.5.6.0");var subQ31=sQuery(id+"F0.wireOp",EDGE,"E1.5.5.0");var subQ32=sQuery(id+"F0.wireOp",EDGE,"E1.5.4.0");var subQ33=sQuery(id+"F0.wireOp",EDGE,"E1.5.3.0");var subQ34=sQuery(id+"F0.wireOp",EDGE,"E1.5.2.0");var subQ35=sQuery(id+"F0.wireOp",EDGE,"E1.5.1.0");var subQ36=sQuery(id+"F0.wireOp",EDGE,"E1.4.6.0");var subQ37=sQuery(id+"F0.wireOp",EDGE,"E1.4.5.0");var subQ38=sQuery(id+"F0.wireOp",EDGE,"E1.4.4.0");var subQ39=sQuery(id+"F0.wireOp",EDGE,"E1.4.3.0");var subQ40=sQuery(id+"F0.wireOp",EDGE,"E1.4.2.0");var subQ41=sQuery(id+"F0.wireOp",EDGE,"E1.4.1.0");var subQ42=sQuery(id+"F0.wireOp",EDGE,"E1.3.6.0");var subQ43=sQuery(id+"F0.wireOp",EDGE,"E1.3.5.0");var subQ44=sQuery(id+"F0.wireOp",EDGE,"E1.3.4.0");var subQ45=sQuery(id+"F0.wireOp",EDGE,"E1.3.3.0");var subQ46=sQuery(id+"F0.wireOp",EDGE,"E1.3.2.0");var subQ47=sQuery(id+"F0.wireOp",EDGE,"E1.3.1.0");var subQ48=sQuery(id+"F0.wireOp",EDGE,"E1.2.6.0");var subQ49=sQuery(id+"F0.wireOp",EDGE,"E1.2.5.0");var subQ50=sQuery(id+"F0.wireOp",EDGE,"E1.2.4.0");var subQ51=sQuery(id+"F0.wireOp",EDGE,"E1.2.3.0");var subQ52=sQuery(id+"F0.wireOp",EDGE,"E1.2.2.0");var subQ53=sQuery(id+"F0.wireOp",EDGE,"E1.2.1.0");var subQ54=sQuery(id+"F0.wireOp",EDGE,"E1.1.6.0");var subQ55=sQuery(id+"F0.wireOp",EDGE,"E1.1.5.0");var subQ56=sQuery(id+"F0.wireOp",EDGE,"E1.1.4.0");var subQ57=sQuery(id+"F0.wireOp",EDGE,"E1.1.3.0");var subQ58=sQuery(id+"F0.wireOp",EDGE,"E1.1.2.0");var subQ59=sQuery(id+"F0.wireOp",EDGE,"E1.1.1.0");var subQ60=sQuery(id+"F0.wireOp",EDGE,"E0.right");var subQ61=sQuery(id+"F0.wireOp",EDGE,"E0.left");var subQ62=sQuery(id+"F0.wireOp",EDGE,"E0.top");var subQ63=sQuery(id+"F0.wireOp",EDGE,"E0.bottom");Q36=makeQuery(id+"F2.opShell","OFFSET_FACE",FACE,{"disambiguationData":[OSD([subQ63,subQ62,subQ61,subQ60,subQ59,subQ58,subQ57,subQ56,subQ55,subQ54,subQ53,subQ52,subQ51,subQ50,subQ49,subQ48,subQ47,subQ46,subQ45,subQ44,subQ43,subQ42,subQ41,subQ40,subQ39,subQ38,subQ37,subQ36,subQ35,subQ34,subQ33,subQ32,subQ31,subQ30,subQ29,subQ28,subQ27,subQ26,subQ25,subQ24,subQ23,subQ22,subQ21,subQ20,subQ19,subQ18,subQ17,subQ16,subQ15,subQ14,subQ13,subQ12,subQ11,subQ10,subQ9,subQ8,subQ7,subQ6,subQ5,subQ4,subQ3,subQ2,subQ1,subQ0]),TDD([makeQuery(id+"F1.opExtrude","CAP_FACE",FACE,{"disambiguationData":[OSD([subQ63,subQ62,subQ61,subQ60,subQ59,subQ58,subQ57,subQ56,subQ55,subQ54,subQ53,subQ52,subQ51,subQ50,subQ49,subQ48,subQ47,subQ46,subQ45,subQ44,subQ43,subQ42,subQ41,subQ40,subQ39,subQ38,subQ37,subQ36,subQ35,subQ34,subQ33,subQ32,subQ31,subQ30,subQ29,subQ28,subQ27,subQ26,subQ25,subQ24,subQ23,subQ22,subQ21,subQ20,subQ19,subQ18,subQ17,subQ16,subQ15,subQ14,subQ13,subQ12,subQ11,subQ10,subQ9,subQ8,subQ7,subQ6,subQ5,subQ4,subQ3,subQ2,subQ1,subQ0])],"isStart":false})]),OD(20.0)]});}
            var Q37;
            {var subQ0=sQuery(id+"F0.wireOp",EDGE,"E2.0.10.6");var subQ1=sQuery(id+"F0.wireOp",EDGE,"E2.0.10.5");var subQ2=sQuery(id+"F0.wireOp",EDGE,"E2.0.10.4");var subQ3=sQuery(id+"F0.wireOp",EDGE,"E2.0.10.3");var subQ4=sQuery(id+"F0.wireOp",EDGE,"E2.0.10.2");var subQ5=sQuery(id+"F0.wireOp",EDGE,"E2.0.10.1");var subQ6=sQuery(id+"F0.wireOp",EDGE,"E1.9.6.0");var subQ7=sQuery(id+"F0.wireOp",EDGE,"E1.9.5.0");var subQ8=sQuery(id+"F0.wireOp",EDGE,"E1.9.4.0");var subQ9=sQuery(id+"F0.wireOp",EDGE,"E1.9.3.0");var subQ10=sQuery(id+"F0.wireOp",EDGE,"E1.9.2.0");var subQ11=sQuery(id+"F0.wireOp",EDGE,"E1.9.1.0");var subQ12=sQuery(id+"F0.wireOp",EDGE,"E1.8.6.0");var subQ13=sQuery(id+"F0.wireOp",EDGE,"E1.8.5.0");var subQ14=sQuery(id+"F0.wireOp",EDGE,"E1.8.4.0");var subQ15=sQuery(id+"F0.wireOp",EDGE,"E1.8.3.0");var subQ16=sQuery(id+"F0.wireOp",EDGE,"E1.8.2.0");var subQ17=sQuery(id+"F0.wireOp",EDGE,"E1.8.1.0");var subQ18=sQuery(id+"F0.wireOp",EDGE,"E1.7.6.0");var subQ19=sQuery(id+"F0.wireOp",EDGE,"E1.7.5.0");var subQ20=sQuery(id+"F0.wireOp",EDGE,"E1.7.4.0");var subQ21=sQuery(id+"F0.wireOp",EDGE,"E1.7.3.0");var subQ22=sQuery(id+"F0.wireOp",EDGE,"E1.7.2.0");var subQ23=sQuery(id+"F0.wireOp",EDGE,"E1.7.1.0");var subQ24=sQuery(id+"F0.wireOp",EDGE,"E1.6.6.0");var subQ25=sQuery(id+"F0.wireOp",EDGE,"E1.6.5.0");var subQ26=sQuery(id+"F0.wireOp",EDGE,"E1.6.4.0");var subQ27=sQuery(id+"F0.wireOp",EDGE,"E1.6.3.0");var subQ28=sQuery(id+"F0.wireOp",EDGE,"E1.6.2.0");var subQ29=sQuery(id+"F0.wireOp",EDGE,"E1.6.1.0");var subQ30=sQuery(id+"F0.wireOp",EDGE,"E1.5.6.0");var subQ31=sQuery(id+"F0.wireOp",EDGE,"E1.5.5.0");var subQ32=sQuery(id+"F0.wireOp",EDGE,"E1.5.4.0");var subQ33=sQuery(id+"F0.wireOp",EDGE,"E1.5.3.0");var subQ34=sQuery(id+"F0.wireOp",EDGE,"E1.5.2.0");var subQ35=sQuery(id+"F0.wireOp",EDGE,"E1.5.1.0");var subQ36=sQuery(id+"F0.wireOp",EDGE,"E1.4.6.0");var subQ37=sQuery(id+"F0.wireOp",EDGE,"E1.4.5.0");var subQ38=sQuery(id+"F0.wireOp",EDGE,"E1.4.4.0");var subQ39=sQuery(id+"F0.wireOp",EDGE,"E1.4.3.0");var subQ40=sQuery(id+"F0.wireOp",EDGE,"E1.4.2.0");var subQ41=sQuery(id+"F0.wireOp",EDGE,"E1.4.1.0");var subQ42=sQuery(id+"F0.wireOp",EDGE,"E1.3.6.0");var subQ43=sQuery(id+"F0.wireOp",EDGE,"E1.3.5.0");var subQ44=sQuery(id+"F0.wireOp",EDGE,"E1.3.4.0");var subQ45=sQuery(id+"F0.wireOp",EDGE,"E1.3.3.0");var subQ46=sQuery(id+"F0.wireOp",EDGE,"E1.3.2.0");var subQ47=sQuery(id+"F0.wireOp",EDGE,"E1.3.1.0");var subQ48=sQuery(id+"F0.wireOp",EDGE,"E1.2.6.0");var subQ49=sQuery(id+"F0.wireOp",EDGE,"E1.2.5.0");var subQ50=sQuery(id+"F0.wireOp",EDGE,"E1.2.4.0");var subQ51=sQuery(id+"F0.wireOp",EDGE,"E1.2.3.0");var subQ52=sQuery(id+"F0.wireOp",EDGE,"E1.2.2.0");var subQ53=sQuery(id+"F0.wireOp",EDGE,"E1.2.1.0");var subQ54=sQuery(id+"F0.wireOp",EDGE,"E1.1.6.0");var subQ55=sQuery(id+"F0.wireOp",EDGE,"E1.1.5.0");var subQ56=sQuery(id+"F0.wireOp",EDGE,"E1.1.4.0");var subQ57=sQuery(id+"F0.wireOp",EDGE,"E1.1.3.0");var subQ58=sQuery(id+"F0.wireOp",EDGE,"E1.1.2.0");var subQ59=sQuery(id+"F0.wireOp",EDGE,"E1.1.1.0");var subQ60=sQuery(id+"F0.wireOp",EDGE,"E0.right");var subQ61=sQuery(id+"F0.wireOp",EDGE,"E0.left");var subQ62=sQuery(id+"F0.wireOp",EDGE,"E0.top");var subQ63=sQuery(id+"F0.wireOp",EDGE,"E0.bottom");Q37=makeQuery(id+"F2.opShell","OFFSET_FACE",FACE,{"disambiguationData":[OSD([subQ63,subQ62,subQ61,subQ60,subQ59,subQ58,subQ57,subQ56,subQ55,subQ54,subQ53,subQ52,subQ51,subQ50,subQ49,subQ48,subQ47,subQ46,subQ45,subQ44,subQ43,subQ42,subQ41,subQ40,subQ39,subQ38,subQ37,subQ36,subQ35,subQ34,subQ33,subQ32,subQ31,subQ30,subQ29,subQ28,subQ27,subQ26,subQ25,subQ24,subQ23,subQ22,subQ21,subQ20,subQ19,subQ18,subQ17,subQ16,subQ15,subQ14,subQ13,subQ12,subQ11,subQ10,subQ9,subQ8,subQ7,subQ6,subQ5,subQ4,subQ3,subQ2,subQ1,subQ0]),TDD([makeQuery(id+"F1.opExtrude","CAP_FACE",FACE,{"disambiguationData":[OSD([subQ63,subQ62,subQ61,subQ60,subQ59,subQ58,subQ57,subQ56,subQ55,subQ54,subQ53,subQ52,subQ51,subQ50,subQ49,subQ48,subQ47,subQ46,subQ45,subQ44,subQ43,subQ42,subQ41,subQ40,subQ39,subQ38,subQ37,subQ36,subQ35,subQ34,subQ33,subQ32,subQ31,subQ30,subQ29,subQ28,subQ27,subQ26,subQ25,subQ24,subQ23,subQ22,subQ21,subQ20,subQ19,subQ18,subQ17,subQ16,subQ15,subQ14,subQ13,subQ12,subQ11,subQ10,subQ9,subQ8,subQ7,subQ6,subQ5,subQ4,subQ3,subQ2,subQ1,subQ0])],"isStart":false})]),OD(8.0)]});}
            var Q38;
            {var subQ0=sQuery(id+"F0.wireOp",EDGE,"E2.0.10.6");var subQ1=sQuery(id+"F0.wireOp",EDGE,"E2.0.10.5");var subQ2=sQuery(id+"F0.wireOp",EDGE,"E2.0.10.4");var subQ3=sQuery(id+"F0.wireOp",EDGE,"E2.0.10.3");var subQ4=sQuery(id+"F0.wireOp",EDGE,"E2.0.10.2");var subQ5=sQuery(id+"F0.wireOp",EDGE,"E2.0.10.1");var subQ6=sQuery(id+"F0.wireOp",EDGE,"E1.9.6.0");var subQ7=sQuery(id+"F0.wireOp",EDGE,"E1.9.5.0");var subQ8=sQuery(id+"F0.wireOp",EDGE,"E1.9.4.0");var subQ9=sQuery(id+"F0.wireOp",EDGE,"E1.9.3.0");var subQ10=sQuery(id+"F0.wireOp",EDGE,"E1.9.2.0");var subQ11=sQuery(id+"F0.wireOp",EDGE,"E1.9.1.0");var subQ12=sQuery(id+"F0.wireOp",EDGE,"E1.8.6.0");var subQ13=sQuery(id+"F0.wireOp",EDGE,"E1.8.5.0");var subQ14=sQuery(id+"F0.wireOp",EDGE,"E1.8.4.0");var subQ15=sQuery(id+"F0.wireOp",EDGE,"E1.8.3.0");var subQ16=sQuery(id+"F0.wireOp",EDGE,"E1.8.2.0");var subQ17=sQuery(id+"F0.wireOp",EDGE,"E1.8.1.0");var subQ18=sQuery(id+"F0.wireOp",EDGE,"E1.7.6.0");var subQ19=sQuery(id+"F0.wireOp",EDGE,"E1.7.5.0");var subQ20=sQuery(id+"F0.wireOp",EDGE,"E1.7.4.0");var subQ21=sQuery(id+"F0.wireOp",EDGE,"E1.7.3.0");var subQ22=sQuery(id+"F0.wireOp",EDGE,"E1.7.2.0");var subQ23=sQuery(id+"F0.wireOp",EDGE,"E1.7.1.0");var subQ24=sQuery(id+"F0.wireOp",EDGE,"E1.6.6.0");var subQ25=sQuery(id+"F0.wireOp",EDGE,"E1.6.5.0");var subQ26=sQuery(id+"F0.wireOp",EDGE,"E1.6.4.0");var subQ27=sQuery(id+"F0.wireOp",EDGE,"E1.6.3.0");var subQ28=sQuery(id+"F0.wireOp",EDGE,"E1.6.2.0");var subQ29=sQuery(id+"F0.wireOp",EDGE,"E1.6.1.0");var subQ30=sQuery(id+"F0.wireOp",EDGE,"E1.5.6.0");var subQ31=sQuery(id+"F0.wireOp",EDGE,"E1.5.5.0");var subQ32=sQuery(id+"F0.wireOp",EDGE,"E1.5.4.0");var subQ33=sQuery(id+"F0.wireOp",EDGE,"E1.5.3.0");var subQ34=sQuery(id+"F0.wireOp",EDGE,"E1.5.2.0");var subQ35=sQuery(id+"F0.wireOp",EDGE,"E1.5.1.0");var subQ36=sQuery(id+"F0.wireOp",EDGE,"E1.4.6.0");var subQ37=sQuery(id+"F0.wireOp",EDGE,"E1.4.5.0");var subQ38=sQuery(id+"F0.wireOp",EDGE,"E1.4.4.0");var subQ39=sQuery(id+"F0.wireOp",EDGE,"E1.4.3.0");var subQ40=sQuery(id+"F0.wireOp",EDGE,"E1.4.2.0");var subQ41=sQuery(id+"F0.wireOp",EDGE,"E1.4.1.0");var subQ42=sQuery(id+"F0.wireOp",EDGE,"E1.3.6.0");var subQ43=sQuery(id+"F0.wireOp",EDGE,"E1.3.5.0");var subQ44=sQuery(id+"F0.wireOp",EDGE,"E1.3.4.0");var subQ45=sQuery(id+"F0.wireOp",EDGE,"E1.3.3.0");var subQ46=sQuery(id+"F0.wireOp",EDGE,"E1.3.2.0");var subQ47=sQuery(id+"F0.wireOp",EDGE,"E1.3.1.0");var subQ48=sQuery(id+"F0.wireOp",EDGE,"E1.2.6.0");var subQ49=sQuery(id+"F0.wireOp",EDGE,"E1.2.5.0");var subQ50=sQuery(id+"F0.wireOp",EDGE,"E1.2.4.0");var subQ51=sQuery(id+"F0.wireOp",EDGE,"E1.2.3.0");var subQ52=sQuery(id+"F0.wireOp",EDGE,"E1.2.2.0");var subQ53=sQuery(id+"F0.wireOp",EDGE,"E1.2.1.0");var subQ54=sQuery(id+"F0.wireOp",EDGE,"E1.1.6.0");var subQ55=sQuery(id+"F0.wireOp",EDGE,"E1.1.5.0");var subQ56=sQuery(id+"F0.wireOp",EDGE,"E1.1.4.0");var subQ57=sQuery(id+"F0.wireOp",EDGE,"E1.1.3.0");var subQ58=sQuery(id+"F0.wireOp",EDGE,"E1.1.2.0");var subQ59=sQuery(id+"F0.wireOp",EDGE,"E1.1.1.0");var subQ60=sQuery(id+"F0.wireOp",EDGE,"E0.right");var subQ61=sQuery(id+"F0.wireOp",EDGE,"E0.left");var subQ62=sQuery(id+"F0.wireOp",EDGE,"E0.top");var subQ63=sQuery(id+"F0.wireOp",EDGE,"E0.bottom");Q38=makeQuery(id+"F2.opShell","OFFSET_FACE",FACE,{"disambiguationData":[OSD([subQ63,subQ62,subQ61,subQ60,subQ59,subQ58,subQ57,subQ56,subQ55,subQ54,subQ53,subQ52,subQ51,subQ50,subQ49,subQ48,subQ47,subQ46,subQ45,subQ44,subQ43,subQ42,subQ41,subQ40,subQ39,subQ38,subQ37,subQ36,subQ35,subQ34,subQ33,subQ32,subQ31,subQ30,subQ29,subQ28,subQ27,subQ26,subQ25,subQ24,subQ23,subQ22,subQ21,subQ20,subQ19,subQ18,subQ17,subQ16,subQ15,subQ14,subQ13,subQ12,subQ11,subQ10,subQ9,subQ8,subQ7,subQ6,subQ5,subQ4,subQ3,subQ2,subQ1,subQ0]),TDD([makeQuery(id+"F1.opExtrude","CAP_FACE",FACE,{"disambiguationData":[OSD([subQ63,subQ62,subQ61,subQ60,subQ59,subQ58,subQ57,subQ56,subQ55,subQ54,subQ53,subQ52,subQ51,subQ50,subQ49,subQ48,subQ47,subQ46,subQ45,subQ44,subQ43,subQ42,subQ41,subQ40,subQ39,subQ38,subQ37,subQ36,subQ35,subQ34,subQ33,subQ32,subQ31,subQ30,subQ29,subQ28,subQ27,subQ26,subQ25,subQ24,subQ23,subQ22,subQ21,subQ20,subQ19,subQ18,subQ17,subQ16,subQ15,subQ14,subQ13,subQ12,subQ11,subQ10,subQ9,subQ8,subQ7,subQ6,subQ5,subQ4,subQ3,subQ2,subQ1,subQ0])],"isStart":false})]),OD(2.0)]});}
            var Q39;
            {var subQ0=sQuery(id+"F0.wireOp",EDGE,"E2.0.10.6");var subQ1=sQuery(id+"F0.wireOp",EDGE,"E2.0.10.5");var subQ2=sQuery(id+"F0.wireOp",EDGE,"E2.0.10.4");var subQ3=sQuery(id+"F0.wireOp",EDGE,"E2.0.10.3");var subQ4=sQuery(id+"F0.wireOp",EDGE,"E2.0.10.2");var subQ5=sQuery(id+"F0.wireOp",EDGE,"E2.0.10.1");var subQ6=sQuery(id+"F0.wireOp",EDGE,"E1.9.6.0");var subQ7=sQuery(id+"F0.wireOp",EDGE,"E1.9.5.0");var subQ8=sQuery(id+"F0.wireOp",EDGE,"E1.9.4.0");var subQ9=sQuery(id+"F0.wireOp",EDGE,"E1.9.3.0");var subQ10=sQuery(id+"F0.wireOp",EDGE,"E1.9.2.0");var subQ11=sQuery(id+"F0.wireOp",EDGE,"E1.9.1.0");var subQ12=sQuery(id+"F0.wireOp",EDGE,"E1.8.6.0");var subQ13=sQuery(id+"F0.wireOp",EDGE,"E1.8.5.0");var subQ14=sQuery(id+"F0.wireOp",EDGE,"E1.8.4.0");var subQ15=sQuery(id+"F0.wireOp",EDGE,"E1.8.3.0");var subQ16=sQuery(id+"F0.wireOp",EDGE,"E1.8.2.0");var subQ17=sQuery(id+"F0.wireOp",EDGE,"E1.8.1.0");var subQ18=sQuery(id+"F0.wireOp",EDGE,"E1.7.6.0");var subQ19=sQuery(id+"F0.wireOp",EDGE,"E1.7.5.0");var subQ20=sQuery(id+"F0.wireOp",EDGE,"E1.7.4.0");var subQ21=sQuery(id+"F0.wireOp",EDGE,"E1.7.3.0");var subQ22=sQuery(id+"F0.wireOp",EDGE,"E1.7.2.0");var subQ23=sQuery(id+"F0.wireOp",EDGE,"E1.7.1.0");var subQ24=sQuery(id+"F0.wireOp",EDGE,"E1.6.6.0");var subQ25=sQuery(id+"F0.wireOp",EDGE,"E1.6.5.0");var subQ26=sQuery(id+"F0.wireOp",EDGE,"E1.6.4.0");var subQ27=sQuery(id+"F0.wireOp",EDGE,"E1.6.3.0");var subQ28=sQuery(id+"F0.wireOp",EDGE,"E1.6.2.0");var subQ29=sQuery(id+"F0.wireOp",EDGE,"E1.6.1.0");var subQ30=sQuery(id+"F0.wireOp",EDGE,"E1.5.6.0");var subQ31=sQuery(id+"F0.wireOp",EDGE,"E1.5.5.0");var subQ32=sQuery(id+"F0.wireOp",EDGE,"E1.5.4.0");var subQ33=sQuery(id+"F0.wireOp",EDGE,"E1.5.3.0");var subQ34=sQuery(id+"F0.wireOp",EDGE,"E1.5.2.0");var subQ35=sQuery(id+"F0.wireOp",EDGE,"E1.5.1.0");var subQ36=sQuery(id+"F0.wireOp",EDGE,"E1.4.6.0");var subQ37=sQuery(id+"F0.wireOp",EDGE,"E1.4.5.0");var subQ38=sQuery(id+"F0.wireOp",EDGE,"E1.4.4.0");var subQ39=sQuery(id+"F0.wireOp",EDGE,"E1.4.3.0");var subQ40=sQuery(id+"F0.wireOp",EDGE,"E1.4.2.0");var subQ41=sQuery(id+"F0.wireOp",EDGE,"E1.4.1.0");var subQ42=sQuery(id+"F0.wireOp",EDGE,"E1.3.6.0");var subQ43=sQuery(id+"F0.wireOp",EDGE,"E1.3.5.0");var subQ44=sQuery(id+"F0.wireOp",EDGE,"E1.3.4.0");var subQ45=sQuery(id+"F0.wireOp",EDGE,"E1.3.3.0");var subQ46=sQuery(id+"F0.wireOp",EDGE,"E1.3.2.0");var subQ47=sQuery(id+"F0.wireOp",EDGE,"E1.3.1.0");var subQ48=sQuery(id+"F0.wireOp",EDGE,"E1.2.6.0");var subQ49=sQuery(id+"F0.wireOp",EDGE,"E1.2.5.0");var subQ50=sQuery(id+"F0.wireOp",EDGE,"E1.2.4.0");var subQ51=sQuery(id+"F0.wireOp",EDGE,"E1.2.3.0");var subQ52=sQuery(id+"F0.wireOp",EDGE,"E1.2.2.0");var subQ53=sQuery(id+"F0.wireOp",EDGE,"E1.2.1.0");var subQ54=sQuery(id+"F0.wireOp",EDGE,"E1.1.6.0");var subQ55=sQuery(id+"F0.wireOp",EDGE,"E1.1.5.0");var subQ56=sQuery(id+"F0.wireOp",EDGE,"E1.1.4.0");var subQ57=sQuery(id+"F0.wireOp",EDGE,"E1.1.3.0");var subQ58=sQuery(id+"F0.wireOp",EDGE,"E1.1.2.0");var subQ59=sQuery(id+"F0.wireOp",EDGE,"E1.1.1.0");var subQ60=sQuery(id+"F0.wireOp",EDGE,"E0.right");var subQ61=sQuery(id+"F0.wireOp",EDGE,"E0.left");var subQ62=sQuery(id+"F0.wireOp",EDGE,"E0.top");var subQ63=sQuery(id+"F0.wireOp",EDGE,"E0.bottom");Q39=makeQuery(id+"F2.opShell","OFFSET_FACE",FACE,{"disambiguationData":[OSD([subQ63,subQ62,subQ61,subQ60,subQ59,subQ58,subQ57,subQ56,subQ55,subQ54,subQ53,subQ52,subQ51,subQ50,subQ49,subQ48,subQ47,subQ46,subQ45,subQ44,subQ43,subQ42,subQ41,subQ40,subQ39,subQ38,subQ37,subQ36,subQ35,subQ34,subQ33,subQ32,subQ31,subQ30,subQ29,subQ28,subQ27,subQ26,subQ25,subQ24,subQ23,subQ22,subQ21,subQ20,subQ19,subQ18,subQ17,subQ16,subQ15,subQ14,subQ13,subQ12,subQ11,subQ10,subQ9,subQ8,subQ7,subQ6,subQ5,subQ4,subQ3,subQ2,subQ1,subQ0]),TDD([makeQuery(id+"F1.opExtrude","CAP_FACE",FACE,{"disambiguationData":[OSD([subQ63,subQ62,subQ61,subQ60,subQ59,subQ58,subQ57,subQ56,subQ55,subQ54,subQ53,subQ52,subQ51,subQ50,subQ49,subQ48,subQ47,subQ46,subQ45,subQ44,subQ43,subQ42,subQ41,subQ40,subQ39,subQ38,subQ37,subQ36,subQ35,subQ34,subQ33,subQ32,subQ31,subQ30,subQ29,subQ28,subQ27,subQ26,subQ25,subQ24,subQ23,subQ22,subQ21,subQ20,subQ19,subQ18,subQ17,subQ16,subQ15,subQ14,subQ13,subQ12,subQ11,subQ10,subQ9,subQ8,subQ7,subQ6,subQ5,subQ4,subQ3,subQ2,subQ1,subQ0])],"isStart":false})]),OD(1.0)]});}
            var Q40;
            {var subQ0=sQuery(id+"F0.wireOp",EDGE,"E2.0.10.6");var subQ1=sQuery(id+"F0.wireOp",EDGE,"E2.0.10.5");var subQ2=sQuery(id+"F0.wireOp",EDGE,"E2.0.10.4");var subQ3=sQuery(id+"F0.wireOp",EDGE,"E2.0.10.3");var subQ4=sQuery(id+"F0.wireOp",EDGE,"E2.0.10.2");var subQ5=sQuery(id+"F0.wireOp",EDGE,"E2.0.10.1");var subQ6=sQuery(id+"F0.wireOp",EDGE,"E1.9.6.0");var subQ7=sQuery(id+"F0.wireOp",EDGE,"E1.9.5.0");var subQ8=sQuery(id+"F0.wireOp",EDGE,"E1.9.4.0");var subQ9=sQuery(id+"F0.wireOp",EDGE,"E1.9.3.0");var subQ10=sQuery(id+"F0.wireOp",EDGE,"E1.9.2.0");var subQ11=sQuery(id+"F0.wireOp",EDGE,"E1.9.1.0");var subQ12=sQuery(id+"F0.wireOp",EDGE,"E1.8.6.0");var subQ13=sQuery(id+"F0.wireOp",EDGE,"E1.8.5.0");var subQ14=sQuery(id+"F0.wireOp",EDGE,"E1.8.4.0");var subQ15=sQuery(id+"F0.wireOp",EDGE,"E1.8.3.0");var subQ16=sQuery(id+"F0.wireOp",EDGE,"E1.8.2.0");var subQ17=sQuery(id+"F0.wireOp",EDGE,"E1.8.1.0");var subQ18=sQuery(id+"F0.wireOp",EDGE,"E1.7.6.0");var subQ19=sQuery(id+"F0.wireOp",EDGE,"E1.7.5.0");var subQ20=sQuery(id+"F0.wireOp",EDGE,"E1.7.4.0");var subQ21=sQuery(id+"F0.wireOp",EDGE,"E1.7.3.0");var subQ22=sQuery(id+"F0.wireOp",EDGE,"E1.7.2.0");var subQ23=sQuery(id+"F0.wireOp",EDGE,"E1.7.1.0");var subQ24=sQuery(id+"F0.wireOp",EDGE,"E1.6.6.0");var subQ25=sQuery(id+"F0.wireOp",EDGE,"E1.6.5.0");var subQ26=sQuery(id+"F0.wireOp",EDGE,"E1.6.4.0");var subQ27=sQuery(id+"F0.wireOp",EDGE,"E1.6.3.0");var subQ28=sQuery(id+"F0.wireOp",EDGE,"E1.6.2.0");var subQ29=sQuery(id+"F0.wireOp",EDGE,"E1.6.1.0");var subQ30=sQuery(id+"F0.wireOp",EDGE,"E1.5.6.0");var subQ31=sQuery(id+"F0.wireOp",EDGE,"E1.5.5.0");var subQ32=sQuery(id+"F0.wireOp",EDGE,"E1.5.4.0");var subQ33=sQuery(id+"F0.wireOp",EDGE,"E1.5.3.0");var subQ34=sQuery(id+"F0.wireOp",EDGE,"E1.5.2.0");var subQ35=sQuery(id+"F0.wireOp",EDGE,"E1.5.1.0");var subQ36=sQuery(id+"F0.wireOp",EDGE,"E1.4.6.0");var subQ37=sQuery(id+"F0.wireOp",EDGE,"E1.4.5.0");var subQ38=sQuery(id+"F0.wireOp",EDGE,"E1.4.4.0");var subQ39=sQuery(id+"F0.wireOp",EDGE,"E1.4.3.0");var subQ40=sQuery(id+"F0.wireOp",EDGE,"E1.4.2.0");var subQ41=sQuery(id+"F0.wireOp",EDGE,"E1.4.1.0");var subQ42=sQuery(id+"F0.wireOp",EDGE,"E1.3.6.0");var subQ43=sQuery(id+"F0.wireOp",EDGE,"E1.3.5.0");var subQ44=sQuery(id+"F0.wireOp",EDGE,"E1.3.4.0");var subQ45=sQuery(id+"F0.wireOp",EDGE,"E1.3.3.0");var subQ46=sQuery(id+"F0.wireOp",EDGE,"E1.3.2.0");var subQ47=sQuery(id+"F0.wireOp",EDGE,"E1.3.1.0");var subQ48=sQuery(id+"F0.wireOp",EDGE,"E1.2.6.0");var subQ49=sQuery(id+"F0.wireOp",EDGE,"E1.2.5.0");var subQ50=sQuery(id+"F0.wireOp",EDGE,"E1.2.4.0");var subQ51=sQuery(id+"F0.wireOp",EDGE,"E1.2.3.0");var subQ52=sQuery(id+"F0.wireOp",EDGE,"E1.2.2.0");var subQ53=sQuery(id+"F0.wireOp",EDGE,"E1.2.1.0");var subQ54=sQuery(id+"F0.wireOp",EDGE,"E1.1.6.0");var subQ55=sQuery(id+"F0.wireOp",EDGE,"E1.1.5.0");var subQ56=sQuery(id+"F0.wireOp",EDGE,"E1.1.4.0");var subQ57=sQuery(id+"F0.wireOp",EDGE,"E1.1.3.0");var subQ58=sQuery(id+"F0.wireOp",EDGE,"E1.1.2.0");var subQ59=sQuery(id+"F0.wireOp",EDGE,"E1.1.1.0");var subQ60=sQuery(id+"F0.wireOp",EDGE,"E0.right");var subQ61=sQuery(id+"F0.wireOp",EDGE,"E0.left");var subQ62=sQuery(id+"F0.wireOp",EDGE,"E0.top");var subQ63=sQuery(id+"F0.wireOp",EDGE,"E0.bottom");Q40=makeQuery(id+"F2.opShell","OFFSET_FACE",FACE,{"disambiguationData":[OSD([subQ63,subQ62,subQ61,subQ60,subQ59,subQ58,subQ57,subQ56,subQ55,subQ54,subQ53,subQ52,subQ51,subQ50,subQ49,subQ48,subQ47,subQ46,subQ45,subQ44,subQ43,subQ42,subQ41,subQ40,subQ39,subQ38,subQ37,subQ36,subQ35,subQ34,subQ33,subQ32,subQ31,subQ30,subQ29,subQ28,subQ27,subQ26,subQ25,subQ24,subQ23,subQ22,subQ21,subQ20,subQ19,subQ18,subQ17,subQ16,subQ15,subQ14,subQ13,subQ12,subQ11,subQ10,subQ9,subQ8,subQ7,subQ6,subQ5,subQ4,subQ3,subQ2,subQ1,subQ0]),TDD([makeQuery(id+"F1.opExtrude","CAP_FACE",FACE,{"disambiguationData":[OSD([subQ63,subQ62,subQ61,subQ60,subQ59,subQ58,subQ57,subQ56,subQ55,subQ54,subQ53,subQ52,subQ51,subQ50,subQ49,subQ48,subQ47,subQ46,subQ45,subQ44,subQ43,subQ42,subQ41,subQ40,subQ39,subQ38,subQ37,subQ36,subQ35,subQ34,subQ33,subQ32,subQ31,subQ30,subQ29,subQ28,subQ27,subQ26,subQ25,subQ24,subQ23,subQ22,subQ21,subQ20,subQ19,subQ18,subQ17,subQ16,subQ15,subQ14,subQ13,subQ12,subQ11,subQ10,subQ9,subQ8,subQ7,subQ6,subQ5,subQ4,subQ3,subQ2,subQ1,subQ0])],"isStart":false})]),OD(13.0)]});}
            var Q41;
            {var subQ0=sQuery(id+"F0.wireOp",EDGE,"E2.0.10.6");var subQ1=sQuery(id+"F0.wireOp",EDGE,"E2.0.10.5");var subQ2=sQuery(id+"F0.wireOp",EDGE,"E2.0.10.4");var subQ3=sQuery(id+"F0.wireOp",EDGE,"E2.0.10.3");var subQ4=sQuery(id+"F0.wireOp",EDGE,"E2.0.10.2");var subQ5=sQuery(id+"F0.wireOp",EDGE,"E2.0.10.1");var subQ6=sQuery(id+"F0.wireOp",EDGE,"E1.9.6.0");var subQ7=sQuery(id+"F0.wireOp",EDGE,"E1.9.5.0");var subQ8=sQuery(id+"F0.wireOp",EDGE,"E1.9.4.0");var subQ9=sQuery(id+"F0.wireOp",EDGE,"E1.9.3.0");var subQ10=sQuery(id+"F0.wireOp",EDGE,"E1.9.2.0");var subQ11=sQuery(id+"F0.wireOp",EDGE,"E1.9.1.0");var subQ12=sQuery(id+"F0.wireOp",EDGE,"E1.8.6.0");var subQ13=sQuery(id+"F0.wireOp",EDGE,"E1.8.5.0");var subQ14=sQuery(id+"F0.wireOp",EDGE,"E1.8.4.0");var subQ15=sQuery(id+"F0.wireOp",EDGE,"E1.8.3.0");var subQ16=sQuery(id+"F0.wireOp",EDGE,"E1.8.2.0");var subQ17=sQuery(id+"F0.wireOp",EDGE,"E1.8.1.0");var subQ18=sQuery(id+"F0.wireOp",EDGE,"E1.7.6.0");var subQ19=sQuery(id+"F0.wireOp",EDGE,"E1.7.5.0");var subQ20=sQuery(id+"F0.wireOp",EDGE,"E1.7.4.0");var subQ21=sQuery(id+"F0.wireOp",EDGE,"E1.7.3.0");var subQ22=sQuery(id+"F0.wireOp",EDGE,"E1.7.2.0");var subQ23=sQuery(id+"F0.wireOp",EDGE,"E1.7.1.0");var subQ24=sQuery(id+"F0.wireOp",EDGE,"E1.6.6.0");var subQ25=sQuery(id+"F0.wireOp",EDGE,"E1.6.5.0");var subQ26=sQuery(id+"F0.wireOp",EDGE,"E1.6.4.0");var subQ27=sQuery(id+"F0.wireOp",EDGE,"E1.6.3.0");var subQ28=sQuery(id+"F0.wireOp",EDGE,"E1.6.2.0");var subQ29=sQuery(id+"F0.wireOp",EDGE,"E1.6.1.0");var subQ30=sQuery(id+"F0.wireOp",EDGE,"E1.5.6.0");var subQ31=sQuery(id+"F0.wireOp",EDGE,"E1.5.5.0");var subQ32=sQuery(id+"F0.wireOp",EDGE,"E1.5.4.0");var subQ33=sQuery(id+"F0.wireOp",EDGE,"E1.5.3.0");var subQ34=sQuery(id+"F0.wireOp",EDGE,"E1.5.2.0");var subQ35=sQuery(id+"F0.wireOp",EDGE,"E1.5.1.0");var subQ36=sQuery(id+"F0.wireOp",EDGE,"E1.4.6.0");var subQ37=sQuery(id+"F0.wireOp",EDGE,"E1.4.5.0");var subQ38=sQuery(id+"F0.wireOp",EDGE,"E1.4.4.0");var subQ39=sQuery(id+"F0.wireOp",EDGE,"E1.4.3.0");var subQ40=sQuery(id+"F0.wireOp",EDGE,"E1.4.2.0");var subQ41=sQuery(id+"F0.wireOp",EDGE,"E1.4.1.0");var subQ42=sQuery(id+"F0.wireOp",EDGE,"E1.3.6.0");var subQ43=sQuery(id+"F0.wireOp",EDGE,"E1.3.5.0");var subQ44=sQuery(id+"F0.wireOp",EDGE,"E1.3.4.0");var subQ45=sQuery(id+"F0.wireOp",EDGE,"E1.3.3.0");var subQ46=sQuery(id+"F0.wireOp",EDGE,"E1.3.2.0");var subQ47=sQuery(id+"F0.wireOp",EDGE,"E1.3.1.0");var subQ48=sQuery(id+"F0.wireOp",EDGE,"E1.2.6.0");var subQ49=sQuery(id+"F0.wireOp",EDGE,"E1.2.5.0");var subQ50=sQuery(id+"F0.wireOp",EDGE,"E1.2.4.0");var subQ51=sQuery(id+"F0.wireOp",EDGE,"E1.2.3.0");var subQ52=sQuery(id+"F0.wireOp",EDGE,"E1.2.2.0");var subQ53=sQuery(id+"F0.wireOp",EDGE,"E1.2.1.0");var subQ54=sQuery(id+"F0.wireOp",EDGE,"E1.1.6.0");var subQ55=sQuery(id+"F0.wireOp",EDGE,"E1.1.5.0");var subQ56=sQuery(id+"F0.wireOp",EDGE,"E1.1.4.0");var subQ57=sQuery(id+"F0.wireOp",EDGE,"E1.1.3.0");var subQ58=sQuery(id+"F0.wireOp",EDGE,"E1.1.2.0");var subQ59=sQuery(id+"F0.wireOp",EDGE,"E1.1.1.0");var subQ60=sQuery(id+"F0.wireOp",EDGE,"E0.right");var subQ61=sQuery(id+"F0.wireOp",EDGE,"E0.left");var subQ62=sQuery(id+"F0.wireOp",EDGE,"E0.top");var subQ63=sQuery(id+"F0.wireOp",EDGE,"E0.bottom");Q41=makeQuery(id+"F2.opShell","OFFSET_FACE",FACE,{"disambiguationData":[OSD([subQ63,subQ62,subQ61,subQ60,subQ59,subQ58,subQ57,subQ56,subQ55,subQ54,subQ53,subQ52,subQ51,subQ50,subQ49,subQ48,subQ47,subQ46,subQ45,subQ44,subQ43,subQ42,subQ41,subQ40,subQ39,subQ38,subQ37,subQ36,subQ35,subQ34,subQ33,subQ32,subQ31,subQ30,subQ29,subQ28,subQ27,subQ26,subQ25,subQ24,subQ23,subQ22,subQ21,subQ20,subQ19,subQ18,subQ17,subQ16,subQ15,subQ14,subQ13,subQ12,subQ11,subQ10,subQ9,subQ8,subQ7,subQ6,subQ5,subQ4,subQ3,subQ2,subQ1,subQ0]),TDD([makeQuery(id+"F1.opExtrude","CAP_FACE",FACE,{"disambiguationData":[OSD([subQ63,subQ62,subQ61,subQ60,subQ59,subQ58,subQ57,subQ56,subQ55,subQ54,subQ53,subQ52,subQ51,subQ50,subQ49,subQ48,subQ47,subQ46,subQ45,subQ44,subQ43,subQ42,subQ41,subQ40,subQ39,subQ38,subQ37,subQ36,subQ35,subQ34,subQ33,subQ32,subQ31,subQ30,subQ29,subQ28,subQ27,subQ26,subQ25,subQ24,subQ23,subQ22,subQ21,subQ20,subQ19,subQ18,subQ17,subQ16,subQ15,subQ14,subQ13,subQ12,subQ11,subQ10,subQ9,subQ8,subQ7,subQ6,subQ5,subQ4,subQ3,subQ2,subQ1,subQ0])],"isStart":false})]),OD(12.0)]});}
            var Q42;
            {var subQ0=sQuery(id+"F0.wireOp",EDGE,"E2.0.10.6");var subQ1=sQuery(id+"F0.wireOp",EDGE,"E2.0.10.5");var subQ2=sQuery(id+"F0.wireOp",EDGE,"E2.0.10.4");var subQ3=sQuery(id+"F0.wireOp",EDGE,"E2.0.10.3");var subQ4=sQuery(id+"F0.wireOp",EDGE,"E2.0.10.2");var subQ5=sQuery(id+"F0.wireOp",EDGE,"E2.0.10.1");var subQ6=sQuery(id+"F0.wireOp",EDGE,"E1.9.6.0");var subQ7=sQuery(id+"F0.wireOp",EDGE,"E1.9.5.0");var subQ8=sQuery(id+"F0.wireOp",EDGE,"E1.9.4.0");var subQ9=sQuery(id+"F0.wireOp",EDGE,"E1.9.3.0");var subQ10=sQuery(id+"F0.wireOp",EDGE,"E1.9.2.0");var subQ11=sQuery(id+"F0.wireOp",EDGE,"E1.9.1.0");var subQ12=sQuery(id+"F0.wireOp",EDGE,"E1.8.6.0");var subQ13=sQuery(id+"F0.wireOp",EDGE,"E1.8.5.0");var subQ14=sQuery(id+"F0.wireOp",EDGE,"E1.8.4.0");var subQ15=sQuery(id+"F0.wireOp",EDGE,"E1.8.3.0");var subQ16=sQuery(id+"F0.wireOp",EDGE,"E1.8.2.0");var subQ17=sQuery(id+"F0.wireOp",EDGE,"E1.8.1.0");var subQ18=sQuery(id+"F0.wireOp",EDGE,"E1.7.6.0");var subQ19=sQuery(id+"F0.wireOp",EDGE,"E1.7.5.0");var subQ20=sQuery(id+"F0.wireOp",EDGE,"E1.7.4.0");var subQ21=sQuery(id+"F0.wireOp",EDGE,"E1.7.3.0");var subQ22=sQuery(id+"F0.wireOp",EDGE,"E1.7.2.0");var subQ23=sQuery(id+"F0.wireOp",EDGE,"E1.7.1.0");var subQ24=sQuery(id+"F0.wireOp",EDGE,"E1.6.6.0");var subQ25=sQuery(id+"F0.wireOp",EDGE,"E1.6.5.0");var subQ26=sQuery(id+"F0.wireOp",EDGE,"E1.6.4.0");var subQ27=sQuery(id+"F0.wireOp",EDGE,"E1.6.3.0");var subQ28=sQuery(id+"F0.wireOp",EDGE,"E1.6.2.0");var subQ29=sQuery(id+"F0.wireOp",EDGE,"E1.6.1.0");var subQ30=sQuery(id+"F0.wireOp",EDGE,"E1.5.6.0");var subQ31=sQuery(id+"F0.wireOp",EDGE,"E1.5.5.0");var subQ32=sQuery(id+"F0.wireOp",EDGE,"E1.5.4.0");var subQ33=sQuery(id+"F0.wireOp",EDGE,"E1.5.3.0");var subQ34=sQuery(id+"F0.wireOp",EDGE,"E1.5.2.0");var subQ35=sQuery(id+"F0.wireOp",EDGE,"E1.5.1.0");var subQ36=sQuery(id+"F0.wireOp",EDGE,"E1.4.6.0");var subQ37=sQuery(id+"F0.wireOp",EDGE,"E1.4.5.0");var subQ38=sQuery(id+"F0.wireOp",EDGE,"E1.4.4.0");var subQ39=sQuery(id+"F0.wireOp",EDGE,"E1.4.3.0");var subQ40=sQuery(id+"F0.wireOp",EDGE,"E1.4.2.0");var subQ41=sQuery(id+"F0.wireOp",EDGE,"E1.4.1.0");var subQ42=sQuery(id+"F0.wireOp",EDGE,"E1.3.6.0");var subQ43=sQuery(id+"F0.wireOp",EDGE,"E1.3.5.0");var subQ44=sQuery(id+"F0.wireOp",EDGE,"E1.3.4.0");var subQ45=sQuery(id+"F0.wireOp",EDGE,"E1.3.3.0");var subQ46=sQuery(id+"F0.wireOp",EDGE,"E1.3.2.0");var subQ47=sQuery(id+"F0.wireOp",EDGE,"E1.3.1.0");var subQ48=sQuery(id+"F0.wireOp",EDGE,"E1.2.6.0");var subQ49=sQuery(id+"F0.wireOp",EDGE,"E1.2.5.0");var subQ50=sQuery(id+"F0.wireOp",EDGE,"E1.2.4.0");var subQ51=sQuery(id+"F0.wireOp",EDGE,"E1.2.3.0");var subQ52=sQuery(id+"F0.wireOp",EDGE,"E1.2.2.0");var subQ53=sQuery(id+"F0.wireOp",EDGE,"E1.2.1.0");var subQ54=sQuery(id+"F0.wireOp",EDGE,"E1.1.6.0");var subQ55=sQuery(id+"F0.wireOp",EDGE,"E1.1.5.0");var subQ56=sQuery(id+"F0.wireOp",EDGE,"E1.1.4.0");var subQ57=sQuery(id+"F0.wireOp",EDGE,"E1.1.3.0");var subQ58=sQuery(id+"F0.wireOp",EDGE,"E1.1.2.0");var subQ59=sQuery(id+"F0.wireOp",EDGE,"E1.1.1.0");var subQ60=sQuery(id+"F0.wireOp",EDGE,"E0.right");var subQ61=sQuery(id+"F0.wireOp",EDGE,"E0.left");var subQ62=sQuery(id+"F0.wireOp",EDGE,"E0.top");var subQ63=sQuery(id+"F0.wireOp",EDGE,"E0.bottom");Q42=makeQuery(id+"F2.opShell","OFFSET_FACE",FACE,{"disambiguationData":[OSD([subQ63,subQ62,subQ61,subQ60,subQ59,subQ58,subQ57,subQ56,subQ55,subQ54,subQ53,subQ52,subQ51,subQ50,subQ49,subQ48,subQ47,subQ46,subQ45,subQ44,subQ43,subQ42,subQ41,subQ40,subQ39,subQ38,subQ37,subQ36,subQ35,subQ34,subQ33,subQ32,subQ31,subQ30,subQ29,subQ28,subQ27,subQ26,subQ25,subQ24,subQ23,subQ22,subQ21,subQ20,subQ19,subQ18,subQ17,subQ16,subQ15,subQ14,subQ13,subQ12,subQ11,subQ10,subQ9,subQ8,subQ7,subQ6,subQ5,subQ4,subQ3,subQ2,subQ1,subQ0]),TDD([makeQuery(id+"F1.opExtrude","CAP_FACE",FACE,{"disambiguationData":[OSD([subQ63,subQ62,subQ61,subQ60,subQ59,subQ58,subQ57,subQ56,subQ55,subQ54,subQ53,subQ52,subQ51,subQ50,subQ49,subQ48,subQ47,subQ46,subQ45,subQ44,subQ43,subQ42,subQ41,subQ40,subQ39,subQ38,subQ37,subQ36,subQ35,subQ34,subQ33,subQ32,subQ31,subQ30,subQ29,subQ28,subQ27,subQ26,subQ25,subQ24,subQ23,subQ22,subQ21,subQ20,subQ19,subQ18,subQ17,subQ16,subQ15,subQ14,subQ13,subQ12,subQ11,subQ10,subQ9,subQ8,subQ7,subQ6,subQ5,subQ4,subQ3,subQ2,subQ1,subQ0])],"isStart":false})]),OD(6.0)]});}
            var Q43;
            {var subQ0=sQuery(id+"F0.wireOp",EDGE,"E2.0.10.6");var subQ1=sQuery(id+"F0.wireOp",EDGE,"E2.0.10.5");var subQ2=sQuery(id+"F0.wireOp",EDGE,"E2.0.10.4");var subQ3=sQuery(id+"F0.wireOp",EDGE,"E2.0.10.3");var subQ4=sQuery(id+"F0.wireOp",EDGE,"E2.0.10.2");var subQ5=sQuery(id+"F0.wireOp",EDGE,"E2.0.10.1");var subQ6=sQuery(id+"F0.wireOp",EDGE,"E1.9.6.0");var subQ7=sQuery(id+"F0.wireOp",EDGE,"E1.9.5.0");var subQ8=sQuery(id+"F0.wireOp",EDGE,"E1.9.4.0");var subQ9=sQuery(id+"F0.wireOp",EDGE,"E1.9.3.0");var subQ10=sQuery(id+"F0.wireOp",EDGE,"E1.9.2.0");var subQ11=sQuery(id+"F0.wireOp",EDGE,"E1.9.1.0");var subQ12=sQuery(id+"F0.wireOp",EDGE,"E1.8.6.0");var subQ13=sQuery(id+"F0.wireOp",EDGE,"E1.8.5.0");var subQ14=sQuery(id+"F0.wireOp",EDGE,"E1.8.4.0");var subQ15=sQuery(id+"F0.wireOp",EDGE,"E1.8.3.0");var subQ16=sQuery(id+"F0.wireOp",EDGE,"E1.8.2.0");var subQ17=sQuery(id+"F0.wireOp",EDGE,"E1.8.1.0");var subQ18=sQuery(id+"F0.wireOp",EDGE,"E1.7.6.0");var subQ19=sQuery(id+"F0.wireOp",EDGE,"E1.7.5.0");var subQ20=sQuery(id+"F0.wireOp",EDGE,"E1.7.4.0");var subQ21=sQuery(id+"F0.wireOp",EDGE,"E1.7.3.0");var subQ22=sQuery(id+"F0.wireOp",EDGE,"E1.7.2.0");var subQ23=sQuery(id+"F0.wireOp",EDGE,"E1.7.1.0");var subQ24=sQuery(id+"F0.wireOp",EDGE,"E1.6.6.0");var subQ25=sQuery(id+"F0.wireOp",EDGE,"E1.6.5.0");var subQ26=sQuery(id+"F0.wireOp",EDGE,"E1.6.4.0");var subQ27=sQuery(id+"F0.wireOp",EDGE,"E1.6.3.0");var subQ28=sQuery(id+"F0.wireOp",EDGE,"E1.6.2.0");var subQ29=sQuery(id+"F0.wireOp",EDGE,"E1.6.1.0");var subQ30=sQuery(id+"F0.wireOp",EDGE,"E1.5.6.0");var subQ31=sQuery(id+"F0.wireOp",EDGE,"E1.5.5.0");var subQ32=sQuery(id+"F0.wireOp",EDGE,"E1.5.4.0");var subQ33=sQuery(id+"F0.wireOp",EDGE,"E1.5.3.0");var subQ34=sQuery(id+"F0.wireOp",EDGE,"E1.5.2.0");var subQ35=sQuery(id+"F0.wireOp",EDGE,"E1.5.1.0");var subQ36=sQuery(id+"F0.wireOp",EDGE,"E1.4.6.0");var subQ37=sQuery(id+"F0.wireOp",EDGE,"E1.4.5.0");var subQ38=sQuery(id+"F0.wireOp",EDGE,"E1.4.4.0");var subQ39=sQuery(id+"F0.wireOp",EDGE,"E1.4.3.0");var subQ40=sQuery(id+"F0.wireOp",EDGE,"E1.4.2.0");var subQ41=sQuery(id+"F0.wireOp",EDGE,"E1.4.1.0");var subQ42=sQuery(id+"F0.wireOp",EDGE,"E1.3.6.0");var subQ43=sQuery(id+"F0.wireOp",EDGE,"E1.3.5.0");var subQ44=sQuery(id+"F0.wireOp",EDGE,"E1.3.4.0");var subQ45=sQuery(id+"F0.wireOp",EDGE,"E1.3.3.0");var subQ46=sQuery(id+"F0.wireOp",EDGE,"E1.3.2.0");var subQ47=sQuery(id+"F0.wireOp",EDGE,"E1.3.1.0");var subQ48=sQuery(id+"F0.wireOp",EDGE,"E1.2.6.0");var subQ49=sQuery(id+"F0.wireOp",EDGE,"E1.2.5.0");var subQ50=sQuery(id+"F0.wireOp",EDGE,"E1.2.4.0");var subQ51=sQuery(id+"F0.wireOp",EDGE,"E1.2.3.0");var subQ52=sQuery(id+"F0.wireOp",EDGE,"E1.2.2.0");var subQ53=sQuery(id+"F0.wireOp",EDGE,"E1.2.1.0");var subQ54=sQuery(id+"F0.wireOp",EDGE,"E1.1.6.0");var subQ55=sQuery(id+"F0.wireOp",EDGE,"E1.1.5.0");var subQ56=sQuery(id+"F0.wireOp",EDGE,"E1.1.4.0");var subQ57=sQuery(id+"F0.wireOp",EDGE,"E1.1.3.0");var subQ58=sQuery(id+"F0.wireOp",EDGE,"E1.1.2.0");var subQ59=sQuery(id+"F0.wireOp",EDGE,"E1.1.1.0");var subQ60=sQuery(id+"F0.wireOp",EDGE,"E0.right");var subQ61=sQuery(id+"F0.wireOp",EDGE,"E0.left");var subQ62=sQuery(id+"F0.wireOp",EDGE,"E0.top");var subQ63=sQuery(id+"F0.wireOp",EDGE,"E0.bottom");Q43=makeQuery(id+"F2.opShell","OFFSET_FACE",FACE,{"disambiguationData":[OSD([subQ63,subQ62,subQ61,subQ60,subQ59,subQ58,subQ57,subQ56,subQ55,subQ54,subQ53,subQ52,subQ51,subQ50,subQ49,subQ48,subQ47,subQ46,subQ45,subQ44,subQ43,subQ42,subQ41,subQ40,subQ39,subQ38,subQ37,subQ36,subQ35,subQ34,subQ33,subQ32,subQ31,subQ30,subQ29,subQ28,subQ27,subQ26,subQ25,subQ24,subQ23,subQ22,subQ21,subQ20,subQ19,subQ18,subQ17,subQ16,subQ15,subQ14,subQ13,subQ12,subQ11,subQ10,subQ9,subQ8,subQ7,subQ6,subQ5,subQ4,subQ3,subQ2,subQ1,subQ0]),TDD([makeQuery(id+"F1.opExtrude","CAP_FACE",FACE,{"disambiguationData":[OSD([subQ63,subQ62,subQ61,subQ60,subQ59,subQ58,subQ57,subQ56,subQ55,subQ54,subQ53,subQ52,subQ51,subQ50,subQ49,subQ48,subQ47,subQ46,subQ45,subQ44,subQ43,subQ42,subQ41,subQ40,subQ39,subQ38,subQ37,subQ36,subQ35,subQ34,subQ33,subQ32,subQ31,subQ30,subQ29,subQ28,subQ27,subQ26,subQ25,subQ24,subQ23,subQ22,subQ21,subQ20,subQ19,subQ18,subQ17,subQ16,subQ15,subQ14,subQ13,subQ12,subQ11,subQ10,subQ9,subQ8,subQ7,subQ6,subQ5,subQ4,subQ3,subQ2,subQ1,subQ0])],"isStart":false})]),OD(14.0)]});}
            var Q44;
            {var subQ0=sQuery(id+"F0.wireOp",EDGE,"E2.0.10.6");var subQ1=sQuery(id+"F0.wireOp",EDGE,"E2.0.10.5");var subQ2=sQuery(id+"F0.wireOp",EDGE,"E2.0.10.4");var subQ3=sQuery(id+"F0.wireOp",EDGE,"E2.0.10.3");var subQ4=sQuery(id+"F0.wireOp",EDGE,"E2.0.10.2");var subQ5=sQuery(id+"F0.wireOp",EDGE,"E2.0.10.1");var subQ6=sQuery(id+"F0.wireOp",EDGE,"E1.9.6.0");var subQ7=sQuery(id+"F0.wireOp",EDGE,"E1.9.5.0");var subQ8=sQuery(id+"F0.wireOp",EDGE,"E1.9.4.0");var subQ9=sQuery(id+"F0.wireOp",EDGE,"E1.9.3.0");var subQ10=sQuery(id+"F0.wireOp",EDGE,"E1.9.2.0");var subQ11=sQuery(id+"F0.wireOp",EDGE,"E1.9.1.0");var subQ12=sQuery(id+"F0.wireOp",EDGE,"E1.8.6.0");var subQ13=sQuery(id+"F0.wireOp",EDGE,"E1.8.5.0");var subQ14=sQuery(id+"F0.wireOp",EDGE,"E1.8.4.0");var subQ15=sQuery(id+"F0.wireOp",EDGE,"E1.8.3.0");var subQ16=sQuery(id+"F0.wireOp",EDGE,"E1.8.2.0");var subQ17=sQuery(id+"F0.wireOp",EDGE,"E1.8.1.0");var subQ18=sQuery(id+"F0.wireOp",EDGE,"E1.7.6.0");var subQ19=sQuery(id+"F0.wireOp",EDGE,"E1.7.5.0");var subQ20=sQuery(id+"F0.wireOp",EDGE,"E1.7.4.0");var subQ21=sQuery(id+"F0.wireOp",EDGE,"E1.7.3.0");var subQ22=sQuery(id+"F0.wireOp",EDGE,"E1.7.2.0");var subQ23=sQuery(id+"F0.wireOp",EDGE,"E1.7.1.0");var subQ24=sQuery(id+"F0.wireOp",EDGE,"E1.6.6.0");var subQ25=sQuery(id+"F0.wireOp",EDGE,"E1.6.5.0");var subQ26=sQuery(id+"F0.wireOp",EDGE,"E1.6.4.0");var subQ27=sQuery(id+"F0.wireOp",EDGE,"E1.6.3.0");var subQ28=sQuery(id+"F0.wireOp",EDGE,"E1.6.2.0");var subQ29=sQuery(id+"F0.wireOp",EDGE,"E1.6.1.0");var subQ30=sQuery(id+"F0.wireOp",EDGE,"E1.5.6.0");var subQ31=sQuery(id+"F0.wireOp",EDGE,"E1.5.5.0");var subQ32=sQuery(id+"F0.wireOp",EDGE,"E1.5.4.0");var subQ33=sQuery(id+"F0.wireOp",EDGE,"E1.5.3.0");var subQ34=sQuery(id+"F0.wireOp",EDGE,"E1.5.2.0");var subQ35=sQuery(id+"F0.wireOp",EDGE,"E1.5.1.0");var subQ36=sQuery(id+"F0.wireOp",EDGE,"E1.4.6.0");var subQ37=sQuery(id+"F0.wireOp",EDGE,"E1.4.5.0");var subQ38=sQuery(id+"F0.wireOp",EDGE,"E1.4.4.0");var subQ39=sQuery(id+"F0.wireOp",EDGE,"E1.4.3.0");var subQ40=sQuery(id+"F0.wireOp",EDGE,"E1.4.2.0");var subQ41=sQuery(id+"F0.wireOp",EDGE,"E1.4.1.0");var subQ42=sQuery(id+"F0.wireOp",EDGE,"E1.3.6.0");var subQ43=sQuery(id+"F0.wireOp",EDGE,"E1.3.5.0");var subQ44=sQuery(id+"F0.wireOp",EDGE,"E1.3.4.0");var subQ45=sQuery(id+"F0.wireOp",EDGE,"E1.3.3.0");var subQ46=sQuery(id+"F0.wireOp",EDGE,"E1.3.2.0");var subQ47=sQuery(id+"F0.wireOp",EDGE,"E1.3.1.0");var subQ48=sQuery(id+"F0.wireOp",EDGE,"E1.2.6.0");var subQ49=sQuery(id+"F0.wireOp",EDGE,"E1.2.5.0");var subQ50=sQuery(id+"F0.wireOp",EDGE,"E1.2.4.0");var subQ51=sQuery(id+"F0.wireOp",EDGE,"E1.2.3.0");var subQ52=sQuery(id+"F0.wireOp",EDGE,"E1.2.2.0");var subQ53=sQuery(id+"F0.wireOp",EDGE,"E1.2.1.0");var subQ54=sQuery(id+"F0.wireOp",EDGE,"E1.1.6.0");var subQ55=sQuery(id+"F0.wireOp",EDGE,"E1.1.5.0");var subQ56=sQuery(id+"F0.wireOp",EDGE,"E1.1.4.0");var subQ57=sQuery(id+"F0.wireOp",EDGE,"E1.1.3.0");var subQ58=sQuery(id+"F0.wireOp",EDGE,"E1.1.2.0");var subQ59=sQuery(id+"F0.wireOp",EDGE,"E1.1.1.0");var subQ60=sQuery(id+"F0.wireOp",EDGE,"E0.right");var subQ61=sQuery(id+"F0.wireOp",EDGE,"E0.left");var subQ62=sQuery(id+"F0.wireOp",EDGE,"E0.top");var subQ63=sQuery(id+"F0.wireOp",EDGE,"E0.bottom");Q44=makeQuery(id+"F2.opShell","OFFSET_FACE",FACE,{"disambiguationData":[OSD([subQ63,subQ62,subQ61,subQ60,subQ59,subQ58,subQ57,subQ56,subQ55,subQ54,subQ53,subQ52,subQ51,subQ50,subQ49,subQ48,subQ47,subQ46,subQ45,subQ44,subQ43,subQ42,subQ41,subQ40,subQ39,subQ38,subQ37,subQ36,subQ35,subQ34,subQ33,subQ32,subQ31,subQ30,subQ29,subQ28,subQ27,subQ26,subQ25,subQ24,subQ23,subQ22,subQ21,subQ20,subQ19,subQ18,subQ17,subQ16,subQ15,subQ14,subQ13,subQ12,subQ11,subQ10,subQ9,subQ8,subQ7,subQ6,subQ5,subQ4,subQ3,subQ2,subQ1,subQ0]),TDD([makeQuery(id+"F1.opExtrude","CAP_FACE",FACE,{"disambiguationData":[OSD([subQ63,subQ62,subQ61,subQ60,subQ59,subQ58,subQ57,subQ56,subQ55,subQ54,subQ53,subQ52,subQ51,subQ50,subQ49,subQ48,subQ47,subQ46,subQ45,subQ44,subQ43,subQ42,subQ41,subQ40,subQ39,subQ38,subQ37,subQ36,subQ35,subQ34,subQ33,subQ32,subQ31,subQ30,subQ29,subQ28,subQ27,subQ26,subQ25,subQ24,subQ23,subQ22,subQ21,subQ20,subQ19,subQ18,subQ17,subQ16,subQ15,subQ14,subQ13,subQ12,subQ11,subQ10,subQ9,subQ8,subQ7,subQ6,subQ5,subQ4,subQ3,subQ2,subQ1,subQ0])],"isStart":false})]),OD(7.0)]});}
            var Q45;
            {var subQ0=sQuery(id+"F0.wireOp",EDGE,"E2.0.10.6");var subQ1=sQuery(id+"F0.wireOp",EDGE,"E2.0.10.5");var subQ2=sQuery(id+"F0.wireOp",EDGE,"E2.0.10.4");var subQ3=sQuery(id+"F0.wireOp",EDGE,"E2.0.10.3");var subQ4=sQuery(id+"F0.wireOp",EDGE,"E2.0.10.2");var subQ5=sQuery(id+"F0.wireOp",EDGE,"E2.0.10.1");var subQ6=sQuery(id+"F0.wireOp",EDGE,"E1.9.6.0");var subQ7=sQuery(id+"F0.wireOp",EDGE,"E1.9.5.0");var subQ8=sQuery(id+"F0.wireOp",EDGE,"E1.9.4.0");var subQ9=sQuery(id+"F0.wireOp",EDGE,"E1.9.3.0");var subQ10=sQuery(id+"F0.wireOp",EDGE,"E1.9.2.0");var subQ11=sQuery(id+"F0.wireOp",EDGE,"E1.9.1.0");var subQ12=sQuery(id+"F0.wireOp",EDGE,"E1.8.6.0");var subQ13=sQuery(id+"F0.wireOp",EDGE,"E1.8.5.0");var subQ14=sQuery(id+"F0.wireOp",EDGE,"E1.8.4.0");var subQ15=sQuery(id+"F0.wireOp",EDGE,"E1.8.3.0");var subQ16=sQuery(id+"F0.wireOp",EDGE,"E1.8.2.0");var subQ17=sQuery(id+"F0.wireOp",EDGE,"E1.8.1.0");var subQ18=sQuery(id+"F0.wireOp",EDGE,"E1.7.6.0");var subQ19=sQuery(id+"F0.wireOp",EDGE,"E1.7.5.0");var subQ20=sQuery(id+"F0.wireOp",EDGE,"E1.7.4.0");var subQ21=sQuery(id+"F0.wireOp",EDGE,"E1.7.3.0");var subQ22=sQuery(id+"F0.wireOp",EDGE,"E1.7.2.0");var subQ23=sQuery(id+"F0.wireOp",EDGE,"E1.7.1.0");var subQ24=sQuery(id+"F0.wireOp",EDGE,"E1.6.6.0");var subQ25=sQuery(id+"F0.wireOp",EDGE,"E1.6.5.0");var subQ26=sQuery(id+"F0.wireOp",EDGE,"E1.6.4.0");var subQ27=sQuery(id+"F0.wireOp",EDGE,"E1.6.3.0");var subQ28=sQuery(id+"F0.wireOp",EDGE,"E1.6.2.0");var subQ29=sQuery(id+"F0.wireOp",EDGE,"E1.6.1.0");var subQ30=sQuery(id+"F0.wireOp",EDGE,"E1.5.6.0");var subQ31=sQuery(id+"F0.wireOp",EDGE,"E1.5.5.0");var subQ32=sQuery(id+"F0.wireOp",EDGE,"E1.5.4.0");var subQ33=sQuery(id+"F0.wireOp",EDGE,"E1.5.3.0");var subQ34=sQuery(id+"F0.wireOp",EDGE,"E1.5.2.0");var subQ35=sQuery(id+"F0.wireOp",EDGE,"E1.5.1.0");var subQ36=sQuery(id+"F0.wireOp",EDGE,"E1.4.6.0");var subQ37=sQuery(id+"F0.wireOp",EDGE,"E1.4.5.0");var subQ38=sQuery(id+"F0.wireOp",EDGE,"E1.4.4.0");var subQ39=sQuery(id+"F0.wireOp",EDGE,"E1.4.3.0");var subQ40=sQuery(id+"F0.wireOp",EDGE,"E1.4.2.0");var subQ41=sQuery(id+"F0.wireOp",EDGE,"E1.4.1.0");var subQ42=sQuery(id+"F0.wireOp",EDGE,"E1.3.6.0");var subQ43=sQuery(id+"F0.wireOp",EDGE,"E1.3.5.0");var subQ44=sQuery(id+"F0.wireOp",EDGE,"E1.3.4.0");var subQ45=sQuery(id+"F0.wireOp",EDGE,"E1.3.3.0");var subQ46=sQuery(id+"F0.wireOp",EDGE,"E1.3.2.0");var subQ47=sQuery(id+"F0.wireOp",EDGE,"E1.3.1.0");var subQ48=sQuery(id+"F0.wireOp",EDGE,"E1.2.6.0");var subQ49=sQuery(id+"F0.wireOp",EDGE,"E1.2.5.0");var subQ50=sQuery(id+"F0.wireOp",EDGE,"E1.2.4.0");var subQ51=sQuery(id+"F0.wireOp",EDGE,"E1.2.3.0");var subQ52=sQuery(id+"F0.wireOp",EDGE,"E1.2.2.0");var subQ53=sQuery(id+"F0.wireOp",EDGE,"E1.2.1.0");var subQ54=sQuery(id+"F0.wireOp",EDGE,"E1.1.6.0");var subQ55=sQuery(id+"F0.wireOp",EDGE,"E1.1.5.0");var subQ56=sQuery(id+"F0.wireOp",EDGE,"E1.1.4.0");var subQ57=sQuery(id+"F0.wireOp",EDGE,"E1.1.3.0");var subQ58=sQuery(id+"F0.wireOp",EDGE,"E1.1.2.0");var subQ59=sQuery(id+"F0.wireOp",EDGE,"E1.1.1.0");var subQ60=sQuery(id+"F0.wireOp",EDGE,"E0.right");var subQ61=sQuery(id+"F0.wireOp",EDGE,"E0.left");var subQ62=sQuery(id+"F0.wireOp",EDGE,"E0.top");var subQ63=sQuery(id+"F0.wireOp",EDGE,"E0.bottom");Q45=makeQuery(id+"F2.opShell","OFFSET_FACE",FACE,{"disambiguationData":[OSD([subQ63,subQ62,subQ61,subQ60,subQ59,subQ58,subQ57,subQ56,subQ55,subQ54,subQ53,subQ52,subQ51,subQ50,subQ49,subQ48,subQ47,subQ46,subQ45,subQ44,subQ43,subQ42,subQ41,subQ40,subQ39,subQ38,subQ37,subQ36,subQ35,subQ34,subQ33,subQ32,subQ31,subQ30,subQ29,subQ28,subQ27,subQ26,subQ25,subQ24,subQ23,subQ22,subQ21,subQ20,subQ19,subQ18,subQ17,subQ16,subQ15,subQ14,subQ13,subQ12,subQ11,subQ10,subQ9,subQ8,subQ7,subQ6,subQ5,subQ4,subQ3,subQ2,subQ1,subQ0]),TDD([makeQuery(id+"F1.opExtrude","CAP_FACE",FACE,{"disambiguationData":[OSD([subQ63,subQ62,subQ61,subQ60,subQ59,subQ58,subQ57,subQ56,subQ55,subQ54,subQ53,subQ52,subQ51,subQ50,subQ49,subQ48,subQ47,subQ46,subQ45,subQ44,subQ43,subQ42,subQ41,subQ40,subQ39,subQ38,subQ37,subQ36,subQ35,subQ34,subQ33,subQ32,subQ31,subQ30,subQ29,subQ28,subQ27,subQ26,subQ25,subQ24,subQ23,subQ22,subQ21,subQ20,subQ19,subQ18,subQ17,subQ16,subQ15,subQ14,subQ13,subQ12,subQ11,subQ10,subQ9,subQ8,subQ7,subQ6,subQ5,subQ4,subQ3,subQ2,subQ1,subQ0])],"isStart":false})]),OD(0.0)]});}
            var Q46;
            {var subQ0=sQuery(id+"F0.wireOp",EDGE,"E2.0.10.6");var subQ1=sQuery(id+"F0.wireOp",EDGE,"E2.0.10.5");var subQ2=sQuery(id+"F0.wireOp",EDGE,"E2.0.10.4");var subQ3=sQuery(id+"F0.wireOp",EDGE,"E2.0.10.3");var subQ4=sQuery(id+"F0.wireOp",EDGE,"E2.0.10.2");var subQ5=sQuery(id+"F0.wireOp",EDGE,"E2.0.10.1");var subQ6=sQuery(id+"F0.wireOp",EDGE,"E1.9.6.0");var subQ7=sQuery(id+"F0.wireOp",EDGE,"E1.9.5.0");var subQ8=sQuery(id+"F0.wireOp",EDGE,"E1.9.4.0");var subQ9=sQuery(id+"F0.wireOp",EDGE,"E1.9.3.0");var subQ10=sQuery(id+"F0.wireOp",EDGE,"E1.9.2.0");var subQ11=sQuery(id+"F0.wireOp",EDGE,"E1.9.1.0");var subQ12=sQuery(id+"F0.wireOp",EDGE,"E1.8.6.0");var subQ13=sQuery(id+"F0.wireOp",EDGE,"E1.8.5.0");var subQ14=sQuery(id+"F0.wireOp",EDGE,"E1.8.4.0");var subQ15=sQuery(id+"F0.wireOp",EDGE,"E1.8.3.0");var subQ16=sQuery(id+"F0.wireOp",EDGE,"E1.8.2.0");var subQ17=sQuery(id+"F0.wireOp",EDGE,"E1.8.1.0");var subQ18=sQuery(id+"F0.wireOp",EDGE,"E1.7.6.0");var subQ19=sQuery(id+"F0.wireOp",EDGE,"E1.7.5.0");var subQ20=sQuery(id+"F0.wireOp",EDGE,"E1.7.4.0");var subQ21=sQuery(id+"F0.wireOp",EDGE,"E1.7.3.0");var subQ22=sQuery(id+"F0.wireOp",EDGE,"E1.7.2.0");var subQ23=sQuery(id+"F0.wireOp",EDGE,"E1.7.1.0");var subQ24=sQuery(id+"F0.wireOp",EDGE,"E1.6.6.0");var subQ25=sQuery(id+"F0.wireOp",EDGE,"E1.6.5.0");var subQ26=sQuery(id+"F0.wireOp",EDGE,"E1.6.4.0");var subQ27=sQuery(id+"F0.wireOp",EDGE,"E1.6.3.0");var subQ28=sQuery(id+"F0.wireOp",EDGE,"E1.6.2.0");var subQ29=sQuery(id+"F0.wireOp",EDGE,"E1.6.1.0");var subQ30=sQuery(id+"F0.wireOp",EDGE,"E1.5.6.0");var subQ31=sQuery(id+"F0.wireOp",EDGE,"E1.5.5.0");var subQ32=sQuery(id+"F0.wireOp",EDGE,"E1.5.4.0");var subQ33=sQuery(id+"F0.wireOp",EDGE,"E1.5.3.0");var subQ34=sQuery(id+"F0.wireOp",EDGE,"E1.5.2.0");var subQ35=sQuery(id+"F0.wireOp",EDGE,"E1.5.1.0");var subQ36=sQuery(id+"F0.wireOp",EDGE,"E1.4.6.0");var subQ37=sQuery(id+"F0.wireOp",EDGE,"E1.4.5.0");var subQ38=sQuery(id+"F0.wireOp",EDGE,"E1.4.4.0");var subQ39=sQuery(id+"F0.wireOp",EDGE,"E1.4.3.0");var subQ40=sQuery(id+"F0.wireOp",EDGE,"E1.4.2.0");var subQ41=sQuery(id+"F0.wireOp",EDGE,"E1.4.1.0");var subQ42=sQuery(id+"F0.wireOp",EDGE,"E1.3.6.0");var subQ43=sQuery(id+"F0.wireOp",EDGE,"E1.3.5.0");var subQ44=sQuery(id+"F0.wireOp",EDGE,"E1.3.4.0");var subQ45=sQuery(id+"F0.wireOp",EDGE,"E1.3.3.0");var subQ46=sQuery(id+"F0.wireOp",EDGE,"E1.3.2.0");var subQ47=sQuery(id+"F0.wireOp",EDGE,"E1.3.1.0");var subQ48=sQuery(id+"F0.wireOp",EDGE,"E1.2.6.0");var subQ49=sQuery(id+"F0.wireOp",EDGE,"E1.2.5.0");var subQ50=sQuery(id+"F0.wireOp",EDGE,"E1.2.4.0");var subQ51=sQuery(id+"F0.wireOp",EDGE,"E1.2.3.0");var subQ52=sQuery(id+"F0.wireOp",EDGE,"E1.2.2.0");var subQ53=sQuery(id+"F0.wireOp",EDGE,"E1.2.1.0");var subQ54=sQuery(id+"F0.wireOp",EDGE,"E1.1.6.0");var subQ55=sQuery(id+"F0.wireOp",EDGE,"E1.1.5.0");var subQ56=sQuery(id+"F0.wireOp",EDGE,"E1.1.4.0");var subQ57=sQuery(id+"F0.wireOp",EDGE,"E1.1.3.0");var subQ58=sQuery(id+"F0.wireOp",EDGE,"E1.1.2.0");var subQ59=sQuery(id+"F0.wireOp",EDGE,"E1.1.1.0");var subQ60=sQuery(id+"F0.wireOp",EDGE,"E0.right");var subQ61=sQuery(id+"F0.wireOp",EDGE,"E0.left");var subQ62=sQuery(id+"F0.wireOp",EDGE,"E0.top");var subQ63=sQuery(id+"F0.wireOp",EDGE,"E0.bottom");Q46=makeQuery(id+"F2.opShell","OFFSET_FACE",FACE,{"disambiguationData":[OSD([subQ63,subQ62,subQ61,subQ60,subQ59,subQ58,subQ57,subQ56,subQ55,subQ54,subQ53,subQ52,subQ51,subQ50,subQ49,subQ48,subQ47,subQ46,subQ45,subQ44,subQ43,subQ42,subQ41,subQ40,subQ39,subQ38,subQ37,subQ36,subQ35,subQ34,subQ33,subQ32,subQ31,subQ30,subQ29,subQ28,subQ27,subQ26,subQ25,subQ24,subQ23,subQ22,subQ21,subQ20,subQ19,subQ18,subQ17,subQ16,subQ15,subQ14,subQ13,subQ12,subQ11,subQ10,subQ9,subQ8,subQ7,subQ6,subQ5,subQ4,subQ3,subQ2,subQ1,subQ0]),TDD([makeQuery(id+"F1.opExtrude","CAP_FACE",FACE,{"disambiguationData":[OSD([subQ63,subQ62,subQ61,subQ60,subQ59,subQ58,subQ57,subQ56,subQ55,subQ54,subQ53,subQ52,subQ51,subQ50,subQ49,subQ48,subQ47,subQ46,subQ45,subQ44,subQ43,subQ42,subQ41,subQ40,subQ39,subQ38,subQ37,subQ36,subQ35,subQ34,subQ33,subQ32,subQ31,subQ30,subQ29,subQ28,subQ27,subQ26,subQ25,subQ24,subQ23,subQ22,subQ21,subQ20,subQ19,subQ18,subQ17,subQ16,subQ15,subQ14,subQ13,subQ12,subQ11,subQ10,subQ9,subQ8,subQ7,subQ6,subQ5,subQ4,subQ3,subQ2,subQ1,subQ0])],"isStart":false})]),OD(18.0)]});}
            var Q47;
            {var subQ0=sQuery(id+"F0.wireOp",EDGE,"E2.0.10.6");var subQ1=sQuery(id+"F0.wireOp",EDGE,"E2.0.10.5");var subQ2=sQuery(id+"F0.wireOp",EDGE,"E2.0.10.4");var subQ3=sQuery(id+"F0.wireOp",EDGE,"E2.0.10.3");var subQ4=sQuery(id+"F0.wireOp",EDGE,"E2.0.10.2");var subQ5=sQuery(id+"F0.wireOp",EDGE,"E2.0.10.1");var subQ6=sQuery(id+"F0.wireOp",EDGE,"E1.9.6.0");var subQ7=sQuery(id+"F0.wireOp",EDGE,"E1.9.5.0");var subQ8=sQuery(id+"F0.wireOp",EDGE,"E1.9.4.0");var subQ9=sQuery(id+"F0.wireOp",EDGE,"E1.9.3.0");var subQ10=sQuery(id+"F0.wireOp",EDGE,"E1.9.2.0");var subQ11=sQuery(id+"F0.wireOp",EDGE,"E1.9.1.0");var subQ12=sQuery(id+"F0.wireOp",EDGE,"E1.8.6.0");var subQ13=sQuery(id+"F0.wireOp",EDGE,"E1.8.5.0");var subQ14=sQuery(id+"F0.wireOp",EDGE,"E1.8.4.0");var subQ15=sQuery(id+"F0.wireOp",EDGE,"E1.8.3.0");var subQ16=sQuery(id+"F0.wireOp",EDGE,"E1.8.2.0");var subQ17=sQuery(id+"F0.wireOp",EDGE,"E1.8.1.0");var subQ18=sQuery(id+"F0.wireOp",EDGE,"E1.7.6.0");var subQ19=sQuery(id+"F0.wireOp",EDGE,"E1.7.5.0");var subQ20=sQuery(id+"F0.wireOp",EDGE,"E1.7.4.0");var subQ21=sQuery(id+"F0.wireOp",EDGE,"E1.7.3.0");var subQ22=sQuery(id+"F0.wireOp",EDGE,"E1.7.2.0");var subQ23=sQuery(id+"F0.wireOp",EDGE,"E1.7.1.0");var subQ24=sQuery(id+"F0.wireOp",EDGE,"E1.6.6.0");var subQ25=sQuery(id+"F0.wireOp",EDGE,"E1.6.5.0");var subQ26=sQuery(id+"F0.wireOp",EDGE,"E1.6.4.0");var subQ27=sQuery(id+"F0.wireOp",EDGE,"E1.6.3.0");var subQ28=sQuery(id+"F0.wireOp",EDGE,"E1.6.2.0");var subQ29=sQuery(id+"F0.wireOp",EDGE,"E1.6.1.0");var subQ30=sQuery(id+"F0.wireOp",EDGE,"E1.5.6.0");var subQ31=sQuery(id+"F0.wireOp",EDGE,"E1.5.5.0");var subQ32=sQuery(id+"F0.wireOp",EDGE,"E1.5.4.0");var subQ33=sQuery(id+"F0.wireOp",EDGE,"E1.5.3.0");var subQ34=sQuery(id+"F0.wireOp",EDGE,"E1.5.2.0");var subQ35=sQuery(id+"F0.wireOp",EDGE,"E1.5.1.0");var subQ36=sQuery(id+"F0.wireOp",EDGE,"E1.4.6.0");var subQ37=sQuery(id+"F0.wireOp",EDGE,"E1.4.5.0");var subQ38=sQuery(id+"F0.wireOp",EDGE,"E1.4.4.0");var subQ39=sQuery(id+"F0.wireOp",EDGE,"E1.4.3.0");var subQ40=sQuery(id+"F0.wireOp",EDGE,"E1.4.2.0");var subQ41=sQuery(id+"F0.wireOp",EDGE,"E1.4.1.0");var subQ42=sQuery(id+"F0.wireOp",EDGE,"E1.3.6.0");var subQ43=sQuery(id+"F0.wireOp",EDGE,"E1.3.5.0");var subQ44=sQuery(id+"F0.wireOp",EDGE,"E1.3.4.0");var subQ45=sQuery(id+"F0.wireOp",EDGE,"E1.3.3.0");var subQ46=sQuery(id+"F0.wireOp",EDGE,"E1.3.2.0");var subQ47=sQuery(id+"F0.wireOp",EDGE,"E1.3.1.0");var subQ48=sQuery(id+"F0.wireOp",EDGE,"E1.2.6.0");var subQ49=sQuery(id+"F0.wireOp",EDGE,"E1.2.5.0");var subQ50=sQuery(id+"F0.wireOp",EDGE,"E1.2.4.0");var subQ51=sQuery(id+"F0.wireOp",EDGE,"E1.2.3.0");var subQ52=sQuery(id+"F0.wireOp",EDGE,"E1.2.2.0");var subQ53=sQuery(id+"F0.wireOp",EDGE,"E1.2.1.0");var subQ54=sQuery(id+"F0.wireOp",EDGE,"E1.1.6.0");var subQ55=sQuery(id+"F0.wireOp",EDGE,"E1.1.5.0");var subQ56=sQuery(id+"F0.wireOp",EDGE,"E1.1.4.0");var subQ57=sQuery(id+"F0.wireOp",EDGE,"E1.1.3.0");var subQ58=sQuery(id+"F0.wireOp",EDGE,"E1.1.2.0");var subQ59=sQuery(id+"F0.wireOp",EDGE,"E1.1.1.0");var subQ60=sQuery(id+"F0.wireOp",EDGE,"E0.right");var subQ61=sQuery(id+"F0.wireOp",EDGE,"E0.left");var subQ62=sQuery(id+"F0.wireOp",EDGE,"E0.top");var subQ63=sQuery(id+"F0.wireOp",EDGE,"E0.bottom");Q47=makeQuery(id+"F2.opShell","OFFSET_FACE",FACE,{"disambiguationData":[OSD([subQ63,subQ62,subQ61,subQ60,subQ59,subQ58,subQ57,subQ56,subQ55,subQ54,subQ53,subQ52,subQ51,subQ50,subQ49,subQ48,subQ47,subQ46,subQ45,subQ44,subQ43,subQ42,subQ41,subQ40,subQ39,subQ38,subQ37,subQ36,subQ35,subQ34,subQ33,subQ32,subQ31,subQ30,subQ29,subQ28,subQ27,subQ26,subQ25,subQ24,subQ23,subQ22,subQ21,subQ20,subQ19,subQ18,subQ17,subQ16,subQ15,subQ14,subQ13,subQ12,subQ11,subQ10,subQ9,subQ8,subQ7,subQ6,subQ5,subQ4,subQ3,subQ2,subQ1,subQ0]),TDD([makeQuery(id+"F1.opExtrude","CAP_FACE",FACE,{"disambiguationData":[OSD([subQ63,subQ62,subQ61,subQ60,subQ59,subQ58,subQ57,subQ56,subQ55,subQ54,subQ53,subQ52,subQ51,subQ50,subQ49,subQ48,subQ47,subQ46,subQ45,subQ44,subQ43,subQ42,subQ41,subQ40,subQ39,subQ38,subQ37,subQ36,subQ35,subQ34,subQ33,subQ32,subQ31,subQ30,subQ29,subQ28,subQ27,subQ26,subQ25,subQ24,subQ23,subQ22,subQ21,subQ20,subQ19,subQ18,subQ17,subQ16,subQ15,subQ14,subQ13,subQ12,subQ11,subQ10,subQ9,subQ8,subQ7,subQ6,subQ5,subQ4,subQ3,subQ2,subQ1,subQ0])],"isStart":false})]),OD(19.0)]});}
            var Q48;
            {var subQ0=sQuery(id+"F0.wireOp",EDGE,"E2.0.10.6");var subQ1=sQuery(id+"F0.wireOp",EDGE,"E2.0.10.5");var subQ2=sQuery(id+"F0.wireOp",EDGE,"E2.0.10.4");var subQ3=sQuery(id+"F0.wireOp",EDGE,"E2.0.10.3");var subQ4=sQuery(id+"F0.wireOp",EDGE,"E2.0.10.2");var subQ5=sQuery(id+"F0.wireOp",EDGE,"E2.0.10.1");var subQ6=sQuery(id+"F0.wireOp",EDGE,"E1.9.6.0");var subQ7=sQuery(id+"F0.wireOp",EDGE,"E1.9.5.0");var subQ8=sQuery(id+"F0.wireOp",EDGE,"E1.9.4.0");var subQ9=sQuery(id+"F0.wireOp",EDGE,"E1.9.3.0");var subQ10=sQuery(id+"F0.wireOp",EDGE,"E1.9.2.0");var subQ11=sQuery(id+"F0.wireOp",EDGE,"E1.9.1.0");var subQ12=sQuery(id+"F0.wireOp",EDGE,"E1.8.6.0");var subQ13=sQuery(id+"F0.wireOp",EDGE,"E1.8.5.0");var subQ14=sQuery(id+"F0.wireOp",EDGE,"E1.8.4.0");var subQ15=sQuery(id+"F0.wireOp",EDGE,"E1.8.3.0");var subQ16=sQuery(id+"F0.wireOp",EDGE,"E1.8.2.0");var subQ17=sQuery(id+"F0.wireOp",EDGE,"E1.8.1.0");var subQ18=sQuery(id+"F0.wireOp",EDGE,"E1.7.6.0");var subQ19=sQuery(id+"F0.wireOp",EDGE,"E1.7.5.0");var subQ20=sQuery(id+"F0.wireOp",EDGE,"E1.7.4.0");var subQ21=sQuery(id+"F0.wireOp",EDGE,"E1.7.3.0");var subQ22=sQuery(id+"F0.wireOp",EDGE,"E1.7.2.0");var subQ23=sQuery(id+"F0.wireOp",EDGE,"E1.7.1.0");var subQ24=sQuery(id+"F0.wireOp",EDGE,"E1.6.6.0");var subQ25=sQuery(id+"F0.wireOp",EDGE,"E1.6.5.0");var subQ26=sQuery(id+"F0.wireOp",EDGE,"E1.6.4.0");var subQ27=sQuery(id+"F0.wireOp",EDGE,"E1.6.3.0");var subQ28=sQuery(id+"F0.wireOp",EDGE,"E1.6.2.0");var subQ29=sQuery(id+"F0.wireOp",EDGE,"E1.6.1.0");var subQ30=sQuery(id+"F0.wireOp",EDGE,"E1.5.6.0");var subQ31=sQuery(id+"F0.wireOp",EDGE,"E1.5.5.0");var subQ32=sQuery(id+"F0.wireOp",EDGE,"E1.5.4.0");var subQ33=sQuery(id+"F0.wireOp",EDGE,"E1.5.3.0");var subQ34=sQuery(id+"F0.wireOp",EDGE,"E1.5.2.0");var subQ35=sQuery(id+"F0.wireOp",EDGE,"E1.5.1.0");var subQ36=sQuery(id+"F0.wireOp",EDGE,"E1.4.6.0");var subQ37=sQuery(id+"F0.wireOp",EDGE,"E1.4.5.0");var subQ38=sQuery(id+"F0.wireOp",EDGE,"E1.4.4.0");var subQ39=sQuery(id+"F0.wireOp",EDGE,"E1.4.3.0");var subQ40=sQuery(id+"F0.wireOp",EDGE,"E1.4.2.0");var subQ41=sQuery(id+"F0.wireOp",EDGE,"E1.4.1.0");var subQ42=sQuery(id+"F0.wireOp",EDGE,"E1.3.6.0");var subQ43=sQuery(id+"F0.wireOp",EDGE,"E1.3.5.0");var subQ44=sQuery(id+"F0.wireOp",EDGE,"E1.3.4.0");var subQ45=sQuery(id+"F0.wireOp",EDGE,"E1.3.3.0");var subQ46=sQuery(id+"F0.wireOp",EDGE,"E1.3.2.0");var subQ47=sQuery(id+"F0.wireOp",EDGE,"E1.3.1.0");var subQ48=sQuery(id+"F0.wireOp",EDGE,"E1.2.6.0");var subQ49=sQuery(id+"F0.wireOp",EDGE,"E1.2.5.0");var subQ50=sQuery(id+"F0.wireOp",EDGE,"E1.2.4.0");var subQ51=sQuery(id+"F0.wireOp",EDGE,"E1.2.3.0");var subQ52=sQuery(id+"F0.wireOp",EDGE,"E1.2.2.0");var subQ53=sQuery(id+"F0.wireOp",EDGE,"E1.2.1.0");var subQ54=sQuery(id+"F0.wireOp",EDGE,"E1.1.6.0");var subQ55=sQuery(id+"F0.wireOp",EDGE,"E1.1.5.0");var subQ56=sQuery(id+"F0.wireOp",EDGE,"E1.1.4.0");var subQ57=sQuery(id+"F0.wireOp",EDGE,"E1.1.3.0");var subQ58=sQuery(id+"F0.wireOp",EDGE,"E1.1.2.0");var subQ59=sQuery(id+"F0.wireOp",EDGE,"E1.1.1.0");var subQ60=sQuery(id+"F0.wireOp",EDGE,"E0.right");var subQ61=sQuery(id+"F0.wireOp",EDGE,"E0.left");var subQ62=sQuery(id+"F0.wireOp",EDGE,"E0.top");var subQ63=sQuery(id+"F0.wireOp",EDGE,"E0.bottom");Q48=makeQuery(id+"F2.opShell","OFFSET_FACE",FACE,{"disambiguationData":[OSD([subQ63,subQ62,subQ61,subQ60,subQ59,subQ58,subQ57,subQ56,subQ55,subQ54,subQ53,subQ52,subQ51,subQ50,subQ49,subQ48,subQ47,subQ46,subQ45,subQ44,subQ43,subQ42,subQ41,subQ40,subQ39,subQ38,subQ37,subQ36,subQ35,subQ34,subQ33,subQ32,subQ31,subQ30,subQ29,subQ28,subQ27,subQ26,subQ25,subQ24,subQ23,subQ22,subQ21,subQ20,subQ19,subQ18,subQ17,subQ16,subQ15,subQ14,subQ13,subQ12,subQ11,subQ10,subQ9,subQ8,subQ7,subQ6,subQ5,subQ4,subQ3,subQ2,subQ1,subQ0]),TDD([makeQuery(id+"F1.opExtrude","CAP_FACE",FACE,{"disambiguationData":[OSD([subQ63,subQ62,subQ61,subQ60,subQ59,subQ58,subQ57,subQ56,subQ55,subQ54,subQ53,subQ52,subQ51,subQ50,subQ49,subQ48,subQ47,subQ46,subQ45,subQ44,subQ43,subQ42,subQ41,subQ40,subQ39,subQ38,subQ37,subQ36,subQ35,subQ34,subQ33,subQ32,subQ31,subQ30,subQ29,subQ28,subQ27,subQ26,subQ25,subQ24,subQ23,subQ22,subQ21,subQ20,subQ19,subQ18,subQ17,subQ16,subQ15,subQ14,subQ13,subQ12,subQ11,subQ10,subQ9,subQ8,subQ7,subQ6,subQ5,subQ4,subQ3,subQ2,subQ1,subQ0])],"isStart":false})]),OD(24.0)]});}
            var Q49;
            {var subQ0=sQuery(id+"F0.wireOp",EDGE,"E2.0.10.6");var subQ1=sQuery(id+"F0.wireOp",EDGE,"E2.0.10.5");var subQ2=sQuery(id+"F0.wireOp",EDGE,"E2.0.10.4");var subQ3=sQuery(id+"F0.wireOp",EDGE,"E2.0.10.3");var subQ4=sQuery(id+"F0.wireOp",EDGE,"E2.0.10.2");var subQ5=sQuery(id+"F0.wireOp",EDGE,"E2.0.10.1");var subQ6=sQuery(id+"F0.wireOp",EDGE,"E1.9.6.0");var subQ7=sQuery(id+"F0.wireOp",EDGE,"E1.9.5.0");var subQ8=sQuery(id+"F0.wireOp",EDGE,"E1.9.4.0");var subQ9=sQuery(id+"F0.wireOp",EDGE,"E1.9.3.0");var subQ10=sQuery(id+"F0.wireOp",EDGE,"E1.9.2.0");var subQ11=sQuery(id+"F0.wireOp",EDGE,"E1.9.1.0");var subQ12=sQuery(id+"F0.wireOp",EDGE,"E1.8.6.0");var subQ13=sQuery(id+"F0.wireOp",EDGE,"E1.8.5.0");var subQ14=sQuery(id+"F0.wireOp",EDGE,"E1.8.4.0");var subQ15=sQuery(id+"F0.wireOp",EDGE,"E1.8.3.0");var subQ16=sQuery(id+"F0.wireOp",EDGE,"E1.8.2.0");var subQ17=sQuery(id+"F0.wireOp",EDGE,"E1.8.1.0");var subQ18=sQuery(id+"F0.wireOp",EDGE,"E1.7.6.0");var subQ19=sQuery(id+"F0.wireOp",EDGE,"E1.7.5.0");var subQ20=sQuery(id+"F0.wireOp",EDGE,"E1.7.4.0");var subQ21=sQuery(id+"F0.wireOp",EDGE,"E1.7.3.0");var subQ22=sQuery(id+"F0.wireOp",EDGE,"E1.7.2.0");var subQ23=sQuery(id+"F0.wireOp",EDGE,"E1.7.1.0");var subQ24=sQuery(id+"F0.wireOp",EDGE,"E1.6.6.0");var subQ25=sQuery(id+"F0.wireOp",EDGE,"E1.6.5.0");var subQ26=sQuery(id+"F0.wireOp",EDGE,"E1.6.4.0");var subQ27=sQuery(id+"F0.wireOp",EDGE,"E1.6.3.0");var subQ28=sQuery(id+"F0.wireOp",EDGE,"E1.6.2.0");var subQ29=sQuery(id+"F0.wireOp",EDGE,"E1.6.1.0");var subQ30=sQuery(id+"F0.wireOp",EDGE,"E1.5.6.0");var subQ31=sQuery(id+"F0.wireOp",EDGE,"E1.5.5.0");var subQ32=sQuery(id+"F0.wireOp",EDGE,"E1.5.4.0");var subQ33=sQuery(id+"F0.wireOp",EDGE,"E1.5.3.0");var subQ34=sQuery(id+"F0.wireOp",EDGE,"E1.5.2.0");var subQ35=sQuery(id+"F0.wireOp",EDGE,"E1.5.1.0");var subQ36=sQuery(id+"F0.wireOp",EDGE,"E1.4.6.0");var subQ37=sQuery(id+"F0.wireOp",EDGE,"E1.4.5.0");var subQ38=sQuery(id+"F0.wireOp",EDGE,"E1.4.4.0");var subQ39=sQuery(id+"F0.wireOp",EDGE,"E1.4.3.0");var subQ40=sQuery(id+"F0.wireOp",EDGE,"E1.4.2.0");var subQ41=sQuery(id+"F0.wireOp",EDGE,"E1.4.1.0");var subQ42=sQuery(id+"F0.wireOp",EDGE,"E1.3.6.0");var subQ43=sQuery(id+"F0.wireOp",EDGE,"E1.3.5.0");var subQ44=sQuery(id+"F0.wireOp",EDGE,"E1.3.4.0");var subQ45=sQuery(id+"F0.wireOp",EDGE,"E1.3.3.0");var subQ46=sQuery(id+"F0.wireOp",EDGE,"E1.3.2.0");var subQ47=sQuery(id+"F0.wireOp",EDGE,"E1.3.1.0");var subQ48=sQuery(id+"F0.wireOp",EDGE,"E1.2.6.0");var subQ49=sQuery(id+"F0.wireOp",EDGE,"E1.2.5.0");var subQ50=sQuery(id+"F0.wireOp",EDGE,"E1.2.4.0");var subQ51=sQuery(id+"F0.wireOp",EDGE,"E1.2.3.0");var subQ52=sQuery(id+"F0.wireOp",EDGE,"E1.2.2.0");var subQ53=sQuery(id+"F0.wireOp",EDGE,"E1.2.1.0");var subQ54=sQuery(id+"F0.wireOp",EDGE,"E1.1.6.0");var subQ55=sQuery(id+"F0.wireOp",EDGE,"E1.1.5.0");var subQ56=sQuery(id+"F0.wireOp",EDGE,"E1.1.4.0");var subQ57=sQuery(id+"F0.wireOp",EDGE,"E1.1.3.0");var subQ58=sQuery(id+"F0.wireOp",EDGE,"E1.1.2.0");var subQ59=sQuery(id+"F0.wireOp",EDGE,"E1.1.1.0");var subQ60=sQuery(id+"F0.wireOp",EDGE,"E0.right");var subQ61=sQuery(id+"F0.wireOp",EDGE,"E0.left");var subQ62=sQuery(id+"F0.wireOp",EDGE,"E0.top");var subQ63=sQuery(id+"F0.wireOp",EDGE,"E0.bottom");Q49=makeQuery(id+"F2.opShell","OFFSET_FACE",FACE,{"disambiguationData":[OSD([subQ63,subQ62,subQ61,subQ60,subQ59,subQ58,subQ57,subQ56,subQ55,subQ54,subQ53,subQ52,subQ51,subQ50,subQ49,subQ48,subQ47,subQ46,subQ45,subQ44,subQ43,subQ42,subQ41,subQ40,subQ39,subQ38,subQ37,subQ36,subQ35,subQ34,subQ33,subQ32,subQ31,subQ30,subQ29,subQ28,subQ27,subQ26,subQ25,subQ24,subQ23,subQ22,subQ21,subQ20,subQ19,subQ18,subQ17,subQ16,subQ15,subQ14,subQ13,subQ12,subQ11,subQ10,subQ9,subQ8,subQ7,subQ6,subQ5,subQ4,subQ3,subQ2,subQ1,subQ0]),TDD([makeQuery(id+"F1.opExtrude","CAP_FACE",FACE,{"disambiguationData":[OSD([subQ63,subQ62,subQ61,subQ60,subQ59,subQ58,subQ57,subQ56,subQ55,subQ54,subQ53,subQ52,subQ51,subQ50,subQ49,subQ48,subQ47,subQ46,subQ45,subQ44,subQ43,subQ42,subQ41,subQ40,subQ39,subQ38,subQ37,subQ36,subQ35,subQ34,subQ33,subQ32,subQ31,subQ30,subQ29,subQ28,subQ27,subQ26,subQ25,subQ24,subQ23,subQ22,subQ21,subQ20,subQ19,subQ18,subQ17,subQ16,subQ15,subQ14,subQ13,subQ12,subQ11,subQ10,subQ9,subQ8,subQ7,subQ6,subQ5,subQ4,subQ3,subQ2,subQ1,subQ0])],"isStart":false})]),OD(31.0)]});}
            var Q50;
            {var subQ0=sQuery(id+"F0.wireOp",EDGE,"E2.0.10.6");var subQ1=sQuery(id+"F0.wireOp",EDGE,"E2.0.10.5");var subQ2=sQuery(id+"F0.wireOp",EDGE,"E2.0.10.4");var subQ3=sQuery(id+"F0.wireOp",EDGE,"E2.0.10.3");var subQ4=sQuery(id+"F0.wireOp",EDGE,"E2.0.10.2");var subQ5=sQuery(id+"F0.wireOp",EDGE,"E2.0.10.1");var subQ6=sQuery(id+"F0.wireOp",EDGE,"E1.9.6.0");var subQ7=sQuery(id+"F0.wireOp",EDGE,"E1.9.5.0");var subQ8=sQuery(id+"F0.wireOp",EDGE,"E1.9.4.0");var subQ9=sQuery(id+"F0.wireOp",EDGE,"E1.9.3.0");var subQ10=sQuery(id+"F0.wireOp",EDGE,"E1.9.2.0");var subQ11=sQuery(id+"F0.wireOp",EDGE,"E1.9.1.0");var subQ12=sQuery(id+"F0.wireOp",EDGE,"E1.8.6.0");var subQ13=sQuery(id+"F0.wireOp",EDGE,"E1.8.5.0");var subQ14=sQuery(id+"F0.wireOp",EDGE,"E1.8.4.0");var subQ15=sQuery(id+"F0.wireOp",EDGE,"E1.8.3.0");var subQ16=sQuery(id+"F0.wireOp",EDGE,"E1.8.2.0");var subQ17=sQuery(id+"F0.wireOp",EDGE,"E1.8.1.0");var subQ18=sQuery(id+"F0.wireOp",EDGE,"E1.7.6.0");var subQ19=sQuery(id+"F0.wireOp",EDGE,"E1.7.5.0");var subQ20=sQuery(id+"F0.wireOp",EDGE,"E1.7.4.0");var subQ21=sQuery(id+"F0.wireOp",EDGE,"E1.7.3.0");var subQ22=sQuery(id+"F0.wireOp",EDGE,"E1.7.2.0");var subQ23=sQuery(id+"F0.wireOp",EDGE,"E1.7.1.0");var subQ24=sQuery(id+"F0.wireOp",EDGE,"E1.6.6.0");var subQ25=sQuery(id+"F0.wireOp",EDGE,"E1.6.5.0");var subQ26=sQuery(id+"F0.wireOp",EDGE,"E1.6.4.0");var subQ27=sQuery(id+"F0.wireOp",EDGE,"E1.6.3.0");var subQ28=sQuery(id+"F0.wireOp",EDGE,"E1.6.2.0");var subQ29=sQuery(id+"F0.wireOp",EDGE,"E1.6.1.0");var subQ30=sQuery(id+"F0.wireOp",EDGE,"E1.5.6.0");var subQ31=sQuery(id+"F0.wireOp",EDGE,"E1.5.5.0");var subQ32=sQuery(id+"F0.wireOp",EDGE,"E1.5.4.0");var subQ33=sQuery(id+"F0.wireOp",EDGE,"E1.5.3.0");var subQ34=sQuery(id+"F0.wireOp",EDGE,"E1.5.2.0");var subQ35=sQuery(id+"F0.wireOp",EDGE,"E1.5.1.0");var subQ36=sQuery(id+"F0.wireOp",EDGE,"E1.4.6.0");var subQ37=sQuery(id+"F0.wireOp",EDGE,"E1.4.5.0");var subQ38=sQuery(id+"F0.wireOp",EDGE,"E1.4.4.0");var subQ39=sQuery(id+"F0.wireOp",EDGE,"E1.4.3.0");var subQ40=sQuery(id+"F0.wireOp",EDGE,"E1.4.2.0");var subQ41=sQuery(id+"F0.wireOp",EDGE,"E1.4.1.0");var subQ42=sQuery(id+"F0.wireOp",EDGE,"E1.3.6.0");var subQ43=sQuery(id+"F0.wireOp",EDGE,"E1.3.5.0");var subQ44=sQuery(id+"F0.wireOp",EDGE,"E1.3.4.0");var subQ45=sQuery(id+"F0.wireOp",EDGE,"E1.3.3.0");var subQ46=sQuery(id+"F0.wireOp",EDGE,"E1.3.2.0");var subQ47=sQuery(id+"F0.wireOp",EDGE,"E1.3.1.0");var subQ48=sQuery(id+"F0.wireOp",EDGE,"E1.2.6.0");var subQ49=sQuery(id+"F0.wireOp",EDGE,"E1.2.5.0");var subQ50=sQuery(id+"F0.wireOp",EDGE,"E1.2.4.0");var subQ51=sQuery(id+"F0.wireOp",EDGE,"E1.2.3.0");var subQ52=sQuery(id+"F0.wireOp",EDGE,"E1.2.2.0");var subQ53=sQuery(id+"F0.wireOp",EDGE,"E1.2.1.0");var subQ54=sQuery(id+"F0.wireOp",EDGE,"E1.1.6.0");var subQ55=sQuery(id+"F0.wireOp",EDGE,"E1.1.5.0");var subQ56=sQuery(id+"F0.wireOp",EDGE,"E1.1.4.0");var subQ57=sQuery(id+"F0.wireOp",EDGE,"E1.1.3.0");var subQ58=sQuery(id+"F0.wireOp",EDGE,"E1.1.2.0");var subQ59=sQuery(id+"F0.wireOp",EDGE,"E1.1.1.0");var subQ60=sQuery(id+"F0.wireOp",EDGE,"E0.right");var subQ61=sQuery(id+"F0.wireOp",EDGE,"E0.left");var subQ62=sQuery(id+"F0.wireOp",EDGE,"E0.top");var subQ63=sQuery(id+"F0.wireOp",EDGE,"E0.bottom");Q50=makeQuery(id+"F2.opShell","OFFSET_FACE",FACE,{"disambiguationData":[OSD([subQ63,subQ62,subQ61,subQ60,subQ59,subQ58,subQ57,subQ56,subQ55,subQ54,subQ53,subQ52,subQ51,subQ50,subQ49,subQ48,subQ47,subQ46,subQ45,subQ44,subQ43,subQ42,subQ41,subQ40,subQ39,subQ38,subQ37,subQ36,subQ35,subQ34,subQ33,subQ32,subQ31,subQ30,subQ29,subQ28,subQ27,subQ26,subQ25,subQ24,subQ23,subQ22,subQ21,subQ20,subQ19,subQ18,subQ17,subQ16,subQ15,subQ14,subQ13,subQ12,subQ11,subQ10,subQ9,subQ8,subQ7,subQ6,subQ5,subQ4,subQ3,subQ2,subQ1,subQ0]),TDD([makeQuery(id+"F1.opExtrude","CAP_FACE",FACE,{"disambiguationData":[OSD([subQ63,subQ62,subQ61,subQ60,subQ59,subQ58,subQ57,subQ56,subQ55,subQ54,subQ53,subQ52,subQ51,subQ50,subQ49,subQ48,subQ47,subQ46,subQ45,subQ44,subQ43,subQ42,subQ41,subQ40,subQ39,subQ38,subQ37,subQ36,subQ35,subQ34,subQ33,subQ32,subQ31,subQ30,subQ29,subQ28,subQ27,subQ26,subQ25,subQ24,subQ23,subQ22,subQ21,subQ20,subQ19,subQ18,subQ17,subQ16,subQ15,subQ14,subQ13,subQ12,subQ11,subQ10,subQ9,subQ8,subQ7,subQ6,subQ5,subQ4,subQ3,subQ2,subQ1,subQ0])],"isStart":false})]),OD(25.0)]});}
            var Q51;
            {var subQ0=sQuery(id+"F0.wireOp",EDGE,"E2.0.10.6");var subQ1=sQuery(id+"F0.wireOp",EDGE,"E2.0.10.5");var subQ2=sQuery(id+"F0.wireOp",EDGE,"E2.0.10.4");var subQ3=sQuery(id+"F0.wireOp",EDGE,"E2.0.10.3");var subQ4=sQuery(id+"F0.wireOp",EDGE,"E2.0.10.2");var subQ5=sQuery(id+"F0.wireOp",EDGE,"E2.0.10.1");var subQ6=sQuery(id+"F0.wireOp",EDGE,"E1.9.6.0");var subQ7=sQuery(id+"F0.wireOp",EDGE,"E1.9.5.0");var subQ8=sQuery(id+"F0.wireOp",EDGE,"E1.9.4.0");var subQ9=sQuery(id+"F0.wireOp",EDGE,"E1.9.3.0");var subQ10=sQuery(id+"F0.wireOp",EDGE,"E1.9.2.0");var subQ11=sQuery(id+"F0.wireOp",EDGE,"E1.9.1.0");var subQ12=sQuery(id+"F0.wireOp",EDGE,"E1.8.6.0");var subQ13=sQuery(id+"F0.wireOp",EDGE,"E1.8.5.0");var subQ14=sQuery(id+"F0.wireOp",EDGE,"E1.8.4.0");var subQ15=sQuery(id+"F0.wireOp",EDGE,"E1.8.3.0");var subQ16=sQuery(id+"F0.wireOp",EDGE,"E1.8.2.0");var subQ17=sQuery(id+"F0.wireOp",EDGE,"E1.8.1.0");var subQ18=sQuery(id+"F0.wireOp",EDGE,"E1.7.6.0");var subQ19=sQuery(id+"F0.wireOp",EDGE,"E1.7.5.0");var subQ20=sQuery(id+"F0.wireOp",EDGE,"E1.7.4.0");var subQ21=sQuery(id+"F0.wireOp",EDGE,"E1.7.3.0");var subQ22=sQuery(id+"F0.wireOp",EDGE,"E1.7.2.0");var subQ23=sQuery(id+"F0.wireOp",EDGE,"E1.7.1.0");var subQ24=sQuery(id+"F0.wireOp",EDGE,"E1.6.6.0");var subQ25=sQuery(id+"F0.wireOp",EDGE,"E1.6.5.0");var subQ26=sQuery(id+"F0.wireOp",EDGE,"E1.6.4.0");var subQ27=sQuery(id+"F0.wireOp",EDGE,"E1.6.3.0");var subQ28=sQuery(id+"F0.wireOp",EDGE,"E1.6.2.0");var subQ29=sQuery(id+"F0.wireOp",EDGE,"E1.6.1.0");var subQ30=sQuery(id+"F0.wireOp",EDGE,"E1.5.6.0");var subQ31=sQuery(id+"F0.wireOp",EDGE,"E1.5.5.0");var subQ32=sQuery(id+"F0.wireOp",EDGE,"E1.5.4.0");var subQ33=sQuery(id+"F0.wireOp",EDGE,"E1.5.3.0");var subQ34=sQuery(id+"F0.wireOp",EDGE,"E1.5.2.0");var subQ35=sQuery(id+"F0.wireOp",EDGE,"E1.5.1.0");var subQ36=sQuery(id+"F0.wireOp",EDGE,"E1.4.6.0");var subQ37=sQuery(id+"F0.wireOp",EDGE,"E1.4.5.0");var subQ38=sQuery(id+"F0.wireOp",EDGE,"E1.4.4.0");var subQ39=sQuery(id+"F0.wireOp",EDGE,"E1.4.3.0");var subQ40=sQuery(id+"F0.wireOp",EDGE,"E1.4.2.0");var subQ41=sQuery(id+"F0.wireOp",EDGE,"E1.4.1.0");var subQ42=sQuery(id+"F0.wireOp",EDGE,"E1.3.6.0");var subQ43=sQuery(id+"F0.wireOp",EDGE,"E1.3.5.0");var subQ44=sQuery(id+"F0.wireOp",EDGE,"E1.3.4.0");var subQ45=sQuery(id+"F0.wireOp",EDGE,"E1.3.3.0");var subQ46=sQuery(id+"F0.wireOp",EDGE,"E1.3.2.0");var subQ47=sQuery(id+"F0.wireOp",EDGE,"E1.3.1.0");var subQ48=sQuery(id+"F0.wireOp",EDGE,"E1.2.6.0");var subQ49=sQuery(id+"F0.wireOp",EDGE,"E1.2.5.0");var subQ50=sQuery(id+"F0.wireOp",EDGE,"E1.2.4.0");var subQ51=sQuery(id+"F0.wireOp",EDGE,"E1.2.3.0");var subQ52=sQuery(id+"F0.wireOp",EDGE,"E1.2.2.0");var subQ53=sQuery(id+"F0.wireOp",EDGE,"E1.2.1.0");var subQ54=sQuery(id+"F0.wireOp",EDGE,"E1.1.6.0");var subQ55=sQuery(id+"F0.wireOp",EDGE,"E1.1.5.0");var subQ56=sQuery(id+"F0.wireOp",EDGE,"E1.1.4.0");var subQ57=sQuery(id+"F0.wireOp",EDGE,"E1.1.3.0");var subQ58=sQuery(id+"F0.wireOp",EDGE,"E1.1.2.0");var subQ59=sQuery(id+"F0.wireOp",EDGE,"E1.1.1.0");var subQ60=sQuery(id+"F0.wireOp",EDGE,"E0.right");var subQ61=sQuery(id+"F0.wireOp",EDGE,"E0.left");var subQ62=sQuery(id+"F0.wireOp",EDGE,"E0.top");var subQ63=sQuery(id+"F0.wireOp",EDGE,"E0.bottom");Q51=makeQuery(id+"F2.opShell","OFFSET_FACE",FACE,{"disambiguationData":[OSD([subQ63,subQ62,subQ61,subQ60,subQ59,subQ58,subQ57,subQ56,subQ55,subQ54,subQ53,subQ52,subQ51,subQ50,subQ49,subQ48,subQ47,subQ46,subQ45,subQ44,subQ43,subQ42,subQ41,subQ40,subQ39,subQ38,subQ37,subQ36,subQ35,subQ34,subQ33,subQ32,subQ31,subQ30,subQ29,subQ28,subQ27,subQ26,subQ25,subQ24,subQ23,subQ22,subQ21,subQ20,subQ19,subQ18,subQ17,subQ16,subQ15,subQ14,subQ13,subQ12,subQ11,subQ10,subQ9,subQ8,subQ7,subQ6,subQ5,subQ4,subQ3,subQ2,subQ1,subQ0]),TDD([makeQuery(id+"F1.opExtrude","CAP_FACE",FACE,{"disambiguationData":[OSD([subQ63,subQ62,subQ61,subQ60,subQ59,subQ58,subQ57,subQ56,subQ55,subQ54,subQ53,subQ52,subQ51,subQ50,subQ49,subQ48,subQ47,subQ46,subQ45,subQ44,subQ43,subQ42,subQ41,subQ40,subQ39,subQ38,subQ37,subQ36,subQ35,subQ34,subQ33,subQ32,subQ31,subQ30,subQ29,subQ28,subQ27,subQ26,subQ25,subQ24,subQ23,subQ22,subQ21,subQ20,subQ19,subQ18,subQ17,subQ16,subQ15,subQ14,subQ13,subQ12,subQ11,subQ10,subQ9,subQ8,subQ7,subQ6,subQ5,subQ4,subQ3,subQ2,subQ1,subQ0])],"isStart":false})]),OD(30.0)]});}
            var Q52;
            {var subQ0=sQuery(id+"F0.wireOp",EDGE,"E2.0.10.6");var subQ1=sQuery(id+"F0.wireOp",EDGE,"E2.0.10.5");var subQ2=sQuery(id+"F0.wireOp",EDGE,"E2.0.10.4");var subQ3=sQuery(id+"F0.wireOp",EDGE,"E2.0.10.3");var subQ4=sQuery(id+"F0.wireOp",EDGE,"E2.0.10.2");var subQ5=sQuery(id+"F0.wireOp",EDGE,"E2.0.10.1");var subQ6=sQuery(id+"F0.wireOp",EDGE,"E1.9.6.0");var subQ7=sQuery(id+"F0.wireOp",EDGE,"E1.9.5.0");var subQ8=sQuery(id+"F0.wireOp",EDGE,"E1.9.4.0");var subQ9=sQuery(id+"F0.wireOp",EDGE,"E1.9.3.0");var subQ10=sQuery(id+"F0.wireOp",EDGE,"E1.9.2.0");var subQ11=sQuery(id+"F0.wireOp",EDGE,"E1.9.1.0");var subQ12=sQuery(id+"F0.wireOp",EDGE,"E1.8.6.0");var subQ13=sQuery(id+"F0.wireOp",EDGE,"E1.8.5.0");var subQ14=sQuery(id+"F0.wireOp",EDGE,"E1.8.4.0");var subQ15=sQuery(id+"F0.wireOp",EDGE,"E1.8.3.0");var subQ16=sQuery(id+"F0.wireOp",EDGE,"E1.8.2.0");var subQ17=sQuery(id+"F0.wireOp",EDGE,"E1.8.1.0");var subQ18=sQuery(id+"F0.wireOp",EDGE,"E1.7.6.0");var subQ19=sQuery(id+"F0.wireOp",EDGE,"E1.7.5.0");var subQ20=sQuery(id+"F0.wireOp",EDGE,"E1.7.4.0");var subQ21=sQuery(id+"F0.wireOp",EDGE,"E1.7.3.0");var subQ22=sQuery(id+"F0.wireOp",EDGE,"E1.7.2.0");var subQ23=sQuery(id+"F0.wireOp",EDGE,"E1.7.1.0");var subQ24=sQuery(id+"F0.wireOp",EDGE,"E1.6.6.0");var subQ25=sQuery(id+"F0.wireOp",EDGE,"E1.6.5.0");var subQ26=sQuery(id+"F0.wireOp",EDGE,"E1.6.4.0");var subQ27=sQuery(id+"F0.wireOp",EDGE,"E1.6.3.0");var subQ28=sQuery(id+"F0.wireOp",EDGE,"E1.6.2.0");var subQ29=sQuery(id+"F0.wireOp",EDGE,"E1.6.1.0");var subQ30=sQuery(id+"F0.wireOp",EDGE,"E1.5.6.0");var subQ31=sQuery(id+"F0.wireOp",EDGE,"E1.5.5.0");var subQ32=sQuery(id+"F0.wireOp",EDGE,"E1.5.4.0");var subQ33=sQuery(id+"F0.wireOp",EDGE,"E1.5.3.0");var subQ34=sQuery(id+"F0.wireOp",EDGE,"E1.5.2.0");var subQ35=sQuery(id+"F0.wireOp",EDGE,"E1.5.1.0");var subQ36=sQuery(id+"F0.wireOp",EDGE,"E1.4.6.0");var subQ37=sQuery(id+"F0.wireOp",EDGE,"E1.4.5.0");var subQ38=sQuery(id+"F0.wireOp",EDGE,"E1.4.4.0");var subQ39=sQuery(id+"F0.wireOp",EDGE,"E1.4.3.0");var subQ40=sQuery(id+"F0.wireOp",EDGE,"E1.4.2.0");var subQ41=sQuery(id+"F0.wireOp",EDGE,"E1.4.1.0");var subQ42=sQuery(id+"F0.wireOp",EDGE,"E1.3.6.0");var subQ43=sQuery(id+"F0.wireOp",EDGE,"E1.3.5.0");var subQ44=sQuery(id+"F0.wireOp",EDGE,"E1.3.4.0");var subQ45=sQuery(id+"F0.wireOp",EDGE,"E1.3.3.0");var subQ46=sQuery(id+"F0.wireOp",EDGE,"E1.3.2.0");var subQ47=sQuery(id+"F0.wireOp",EDGE,"E1.3.1.0");var subQ48=sQuery(id+"F0.wireOp",EDGE,"E1.2.6.0");var subQ49=sQuery(id+"F0.wireOp",EDGE,"E1.2.5.0");var subQ50=sQuery(id+"F0.wireOp",EDGE,"E1.2.4.0");var subQ51=sQuery(id+"F0.wireOp",EDGE,"E1.2.3.0");var subQ52=sQuery(id+"F0.wireOp",EDGE,"E1.2.2.0");var subQ53=sQuery(id+"F0.wireOp",EDGE,"E1.2.1.0");var subQ54=sQuery(id+"F0.wireOp",EDGE,"E1.1.6.0");var subQ55=sQuery(id+"F0.wireOp",EDGE,"E1.1.5.0");var subQ56=sQuery(id+"F0.wireOp",EDGE,"E1.1.4.0");var subQ57=sQuery(id+"F0.wireOp",EDGE,"E1.1.3.0");var subQ58=sQuery(id+"F0.wireOp",EDGE,"E1.1.2.0");var subQ59=sQuery(id+"F0.wireOp",EDGE,"E1.1.1.0");var subQ60=sQuery(id+"F0.wireOp",EDGE,"E0.right");var subQ61=sQuery(id+"F0.wireOp",EDGE,"E0.left");var subQ62=sQuery(id+"F0.wireOp",EDGE,"E0.top");var subQ63=sQuery(id+"F0.wireOp",EDGE,"E0.bottom");Q52=makeQuery(id+"F2.opShell","OFFSET_FACE",FACE,{"disambiguationData":[OSD([subQ63,subQ62,subQ61,subQ60,subQ59,subQ58,subQ57,subQ56,subQ55,subQ54,subQ53,subQ52,subQ51,subQ50,subQ49,subQ48,subQ47,subQ46,subQ45,subQ44,subQ43,subQ42,subQ41,subQ40,subQ39,subQ38,subQ37,subQ36,subQ35,subQ34,subQ33,subQ32,subQ31,subQ30,subQ29,subQ28,subQ27,subQ26,subQ25,subQ24,subQ23,subQ22,subQ21,subQ20,subQ19,subQ18,subQ17,subQ16,subQ15,subQ14,subQ13,subQ12,subQ11,subQ10,subQ9,subQ8,subQ7,subQ6,subQ5,subQ4,subQ3,subQ2,subQ1,subQ0]),TDD([makeQuery(id+"F1.opExtrude","CAP_FACE",FACE,{"disambiguationData":[OSD([subQ63,subQ62,subQ61,subQ60,subQ59,subQ58,subQ57,subQ56,subQ55,subQ54,subQ53,subQ52,subQ51,subQ50,subQ49,subQ48,subQ47,subQ46,subQ45,subQ44,subQ43,subQ42,subQ41,subQ40,subQ39,subQ38,subQ37,subQ36,subQ35,subQ34,subQ33,subQ32,subQ31,subQ30,subQ29,subQ28,subQ27,subQ26,subQ25,subQ24,subQ23,subQ22,subQ21,subQ20,subQ19,subQ18,subQ17,subQ16,subQ15,subQ14,subQ13,subQ12,subQ11,subQ10,subQ9,subQ8,subQ7,subQ6,subQ5,subQ4,subQ3,subQ2,subQ1,subQ0])],"isStart":false})]),OD(37.0)]});}
            var Q53;
            {var subQ0=sQuery(id+"F0.wireOp",EDGE,"E2.0.10.6");var subQ1=sQuery(id+"F0.wireOp",EDGE,"E2.0.10.5");var subQ2=sQuery(id+"F0.wireOp",EDGE,"E2.0.10.4");var subQ3=sQuery(id+"F0.wireOp",EDGE,"E2.0.10.3");var subQ4=sQuery(id+"F0.wireOp",EDGE,"E2.0.10.2");var subQ5=sQuery(id+"F0.wireOp",EDGE,"E2.0.10.1");var subQ6=sQuery(id+"F0.wireOp",EDGE,"E1.9.6.0");var subQ7=sQuery(id+"F0.wireOp",EDGE,"E1.9.5.0");var subQ8=sQuery(id+"F0.wireOp",EDGE,"E1.9.4.0");var subQ9=sQuery(id+"F0.wireOp",EDGE,"E1.9.3.0");var subQ10=sQuery(id+"F0.wireOp",EDGE,"E1.9.2.0");var subQ11=sQuery(id+"F0.wireOp",EDGE,"E1.9.1.0");var subQ12=sQuery(id+"F0.wireOp",EDGE,"E1.8.6.0");var subQ13=sQuery(id+"F0.wireOp",EDGE,"E1.8.5.0");var subQ14=sQuery(id+"F0.wireOp",EDGE,"E1.8.4.0");var subQ15=sQuery(id+"F0.wireOp",EDGE,"E1.8.3.0");var subQ16=sQuery(id+"F0.wireOp",EDGE,"E1.8.2.0");var subQ17=sQuery(id+"F0.wireOp",EDGE,"E1.8.1.0");var subQ18=sQuery(id+"F0.wireOp",EDGE,"E1.7.6.0");var subQ19=sQuery(id+"F0.wireOp",EDGE,"E1.7.5.0");var subQ20=sQuery(id+"F0.wireOp",EDGE,"E1.7.4.0");var subQ21=sQuery(id+"F0.wireOp",EDGE,"E1.7.3.0");var subQ22=sQuery(id+"F0.wireOp",EDGE,"E1.7.2.0");var subQ23=sQuery(id+"F0.wireOp",EDGE,"E1.7.1.0");var subQ24=sQuery(id+"F0.wireOp",EDGE,"E1.6.6.0");var subQ25=sQuery(id+"F0.wireOp",EDGE,"E1.6.5.0");var subQ26=sQuery(id+"F0.wireOp",EDGE,"E1.6.4.0");var subQ27=sQuery(id+"F0.wireOp",EDGE,"E1.6.3.0");var subQ28=sQuery(id+"F0.wireOp",EDGE,"E1.6.2.0");var subQ29=sQuery(id+"F0.wireOp",EDGE,"E1.6.1.0");var subQ30=sQuery(id+"F0.wireOp",EDGE,"E1.5.6.0");var subQ31=sQuery(id+"F0.wireOp",EDGE,"E1.5.5.0");var subQ32=sQuery(id+"F0.wireOp",EDGE,"E1.5.4.0");var subQ33=sQuery(id+"F0.wireOp",EDGE,"E1.5.3.0");var subQ34=sQuery(id+"F0.wireOp",EDGE,"E1.5.2.0");var subQ35=sQuery(id+"F0.wireOp",EDGE,"E1.5.1.0");var subQ36=sQuery(id+"F0.wireOp",EDGE,"E1.4.6.0");var subQ37=sQuery(id+"F0.wireOp",EDGE,"E1.4.5.0");var subQ38=sQuery(id+"F0.wireOp",EDGE,"E1.4.4.0");var subQ39=sQuery(id+"F0.wireOp",EDGE,"E1.4.3.0");var subQ40=sQuery(id+"F0.wireOp",EDGE,"E1.4.2.0");var subQ41=sQuery(id+"F0.wireOp",EDGE,"E1.4.1.0");var subQ42=sQuery(id+"F0.wireOp",EDGE,"E1.3.6.0");var subQ43=sQuery(id+"F0.wireOp",EDGE,"E1.3.5.0");var subQ44=sQuery(id+"F0.wireOp",EDGE,"E1.3.4.0");var subQ45=sQuery(id+"F0.wireOp",EDGE,"E1.3.3.0");var subQ46=sQuery(id+"F0.wireOp",EDGE,"E1.3.2.0");var subQ47=sQuery(id+"F0.wireOp",EDGE,"E1.3.1.0");var subQ48=sQuery(id+"F0.wireOp",EDGE,"E1.2.6.0");var subQ49=sQuery(id+"F0.wireOp",EDGE,"E1.2.5.0");var subQ50=sQuery(id+"F0.wireOp",EDGE,"E1.2.4.0");var subQ51=sQuery(id+"F0.wireOp",EDGE,"E1.2.3.0");var subQ52=sQuery(id+"F0.wireOp",EDGE,"E1.2.2.0");var subQ53=sQuery(id+"F0.wireOp",EDGE,"E1.2.1.0");var subQ54=sQuery(id+"F0.wireOp",EDGE,"E1.1.6.0");var subQ55=sQuery(id+"F0.wireOp",EDGE,"E1.1.5.0");var subQ56=sQuery(id+"F0.wireOp",EDGE,"E1.1.4.0");var subQ57=sQuery(id+"F0.wireOp",EDGE,"E1.1.3.0");var subQ58=sQuery(id+"F0.wireOp",EDGE,"E1.1.2.0");var subQ59=sQuery(id+"F0.wireOp",EDGE,"E1.1.1.0");var subQ60=sQuery(id+"F0.wireOp",EDGE,"E0.right");var subQ61=sQuery(id+"F0.wireOp",EDGE,"E0.left");var subQ62=sQuery(id+"F0.wireOp",EDGE,"E0.top");var subQ63=sQuery(id+"F0.wireOp",EDGE,"E0.bottom");Q53=makeQuery(id+"F2.opShell","OFFSET_FACE",FACE,{"disambiguationData":[OSD([subQ63,subQ62,subQ61,subQ60,subQ59,subQ58,subQ57,subQ56,subQ55,subQ54,subQ53,subQ52,subQ51,subQ50,subQ49,subQ48,subQ47,subQ46,subQ45,subQ44,subQ43,subQ42,subQ41,subQ40,subQ39,subQ38,subQ37,subQ36,subQ35,subQ34,subQ33,subQ32,subQ31,subQ30,subQ29,subQ28,subQ27,subQ26,subQ25,subQ24,subQ23,subQ22,subQ21,subQ20,subQ19,subQ18,subQ17,subQ16,subQ15,subQ14,subQ13,subQ12,subQ11,subQ10,subQ9,subQ8,subQ7,subQ6,subQ5,subQ4,subQ3,subQ2,subQ1,subQ0]),TDD([makeQuery(id+"F1.opExtrude","CAP_FACE",FACE,{"disambiguationData":[OSD([subQ63,subQ62,subQ61,subQ60,subQ59,subQ58,subQ57,subQ56,subQ55,subQ54,subQ53,subQ52,subQ51,subQ50,subQ49,subQ48,subQ47,subQ46,subQ45,subQ44,subQ43,subQ42,subQ41,subQ40,subQ39,subQ38,subQ37,subQ36,subQ35,subQ34,subQ33,subQ32,subQ31,subQ30,subQ29,subQ28,subQ27,subQ26,subQ25,subQ24,subQ23,subQ22,subQ21,subQ20,subQ19,subQ18,subQ17,subQ16,subQ15,subQ14,subQ13,subQ12,subQ11,subQ10,subQ9,subQ8,subQ7,subQ6,subQ5,subQ4,subQ3,subQ2,subQ1,subQ0])],"isStart":false})]),OD(36.0)]});}
            var Q54;
            {var subQ0=sQuery(id+"F0.wireOp",EDGE,"E2.0.10.6");var subQ1=sQuery(id+"F0.wireOp",EDGE,"E2.0.10.5");var subQ2=sQuery(id+"F0.wireOp",EDGE,"E2.0.10.4");var subQ3=sQuery(id+"F0.wireOp",EDGE,"E2.0.10.3");var subQ4=sQuery(id+"F0.wireOp",EDGE,"E2.0.10.2");var subQ5=sQuery(id+"F0.wireOp",EDGE,"E2.0.10.1");var subQ6=sQuery(id+"F0.wireOp",EDGE,"E1.9.6.0");var subQ7=sQuery(id+"F0.wireOp",EDGE,"E1.9.5.0");var subQ8=sQuery(id+"F0.wireOp",EDGE,"E1.9.4.0");var subQ9=sQuery(id+"F0.wireOp",EDGE,"E1.9.3.0");var subQ10=sQuery(id+"F0.wireOp",EDGE,"E1.9.2.0");var subQ11=sQuery(id+"F0.wireOp",EDGE,"E1.9.1.0");var subQ12=sQuery(id+"F0.wireOp",EDGE,"E1.8.6.0");var subQ13=sQuery(id+"F0.wireOp",EDGE,"E1.8.5.0");var subQ14=sQuery(id+"F0.wireOp",EDGE,"E1.8.4.0");var subQ15=sQuery(id+"F0.wireOp",EDGE,"E1.8.3.0");var subQ16=sQuery(id+"F0.wireOp",EDGE,"E1.8.2.0");var subQ17=sQuery(id+"F0.wireOp",EDGE,"E1.8.1.0");var subQ18=sQuery(id+"F0.wireOp",EDGE,"E1.7.6.0");var subQ19=sQuery(id+"F0.wireOp",EDGE,"E1.7.5.0");var subQ20=sQuery(id+"F0.wireOp",EDGE,"E1.7.4.0");var subQ21=sQuery(id+"F0.wireOp",EDGE,"E1.7.3.0");var subQ22=sQuery(id+"F0.wireOp",EDGE,"E1.7.2.0");var subQ23=sQuery(id+"F0.wireOp",EDGE,"E1.7.1.0");var subQ24=sQuery(id+"F0.wireOp",EDGE,"E1.6.6.0");var subQ25=sQuery(id+"F0.wireOp",EDGE,"E1.6.5.0");var subQ26=sQuery(id+"F0.wireOp",EDGE,"E1.6.4.0");var subQ27=sQuery(id+"F0.wireOp",EDGE,"E1.6.3.0");var subQ28=sQuery(id+"F0.wireOp",EDGE,"E1.6.2.0");var subQ29=sQuery(id+"F0.wireOp",EDGE,"E1.6.1.0");var subQ30=sQuery(id+"F0.wireOp",EDGE,"E1.5.6.0");var subQ31=sQuery(id+"F0.wireOp",EDGE,"E1.5.5.0");var subQ32=sQuery(id+"F0.wireOp",EDGE,"E1.5.4.0");var subQ33=sQuery(id+"F0.wireOp",EDGE,"E1.5.3.0");var subQ34=sQuery(id+"F0.wireOp",EDGE,"E1.5.2.0");var subQ35=sQuery(id+"F0.wireOp",EDGE,"E1.5.1.0");var subQ36=sQuery(id+"F0.wireOp",EDGE,"E1.4.6.0");var subQ37=sQuery(id+"F0.wireOp",EDGE,"E1.4.5.0");var subQ38=sQuery(id+"F0.wireOp",EDGE,"E1.4.4.0");var subQ39=sQuery(id+"F0.wireOp",EDGE,"E1.4.3.0");var subQ40=sQuery(id+"F0.wireOp",EDGE,"E1.4.2.0");var subQ41=sQuery(id+"F0.wireOp",EDGE,"E1.4.1.0");var subQ42=sQuery(id+"F0.wireOp",EDGE,"E1.3.6.0");var subQ43=sQuery(id+"F0.wireOp",EDGE,"E1.3.5.0");var subQ44=sQuery(id+"F0.wireOp",EDGE,"E1.3.4.0");var subQ45=sQuery(id+"F0.wireOp",EDGE,"E1.3.3.0");var subQ46=sQuery(id+"F0.wireOp",EDGE,"E1.3.2.0");var subQ47=sQuery(id+"F0.wireOp",EDGE,"E1.3.1.0");var subQ48=sQuery(id+"F0.wireOp",EDGE,"E1.2.6.0");var subQ49=sQuery(id+"F0.wireOp",EDGE,"E1.2.5.0");var subQ50=sQuery(id+"F0.wireOp",EDGE,"E1.2.4.0");var subQ51=sQuery(id+"F0.wireOp",EDGE,"E1.2.3.0");var subQ52=sQuery(id+"F0.wireOp",EDGE,"E1.2.2.0");var subQ53=sQuery(id+"F0.wireOp",EDGE,"E1.2.1.0");var subQ54=sQuery(id+"F0.wireOp",EDGE,"E1.1.6.0");var subQ55=sQuery(id+"F0.wireOp",EDGE,"E1.1.5.0");var subQ56=sQuery(id+"F0.wireOp",EDGE,"E1.1.4.0");var subQ57=sQuery(id+"F0.wireOp",EDGE,"E1.1.3.0");var subQ58=sQuery(id+"F0.wireOp",EDGE,"E1.1.2.0");var subQ59=sQuery(id+"F0.wireOp",EDGE,"E1.1.1.0");var subQ60=sQuery(id+"F0.wireOp",EDGE,"E0.right");var subQ61=sQuery(id+"F0.wireOp",EDGE,"E0.left");var subQ62=sQuery(id+"F0.wireOp",EDGE,"E0.top");var subQ63=sQuery(id+"F0.wireOp",EDGE,"E0.bottom");Q54=makeQuery(id+"F2.opShell","OFFSET_FACE",FACE,{"disambiguationData":[OSD([subQ63,subQ62,subQ61,subQ60,subQ59,subQ58,subQ57,subQ56,subQ55,subQ54,subQ53,subQ52,subQ51,subQ50,subQ49,subQ48,subQ47,subQ46,subQ45,subQ44,subQ43,subQ42,subQ41,subQ40,subQ39,subQ38,subQ37,subQ36,subQ35,subQ34,subQ33,subQ32,subQ31,subQ30,subQ29,subQ28,subQ27,subQ26,subQ25,subQ24,subQ23,subQ22,subQ21,subQ20,subQ19,subQ18,subQ17,subQ16,subQ15,subQ14,subQ13,subQ12,subQ11,subQ10,subQ9,subQ8,subQ7,subQ6,subQ5,subQ4,subQ3,subQ2,subQ1,subQ0]),TDD([makeQuery(id+"F1.opExtrude","CAP_FACE",FACE,{"disambiguationData":[OSD([subQ63,subQ62,subQ61,subQ60,subQ59,subQ58,subQ57,subQ56,subQ55,subQ54,subQ53,subQ52,subQ51,subQ50,subQ49,subQ48,subQ47,subQ46,subQ45,subQ44,subQ43,subQ42,subQ41,subQ40,subQ39,subQ38,subQ37,subQ36,subQ35,subQ34,subQ33,subQ32,subQ31,subQ30,subQ29,subQ28,subQ27,subQ26,subQ25,subQ24,subQ23,subQ22,subQ21,subQ20,subQ19,subQ18,subQ17,subQ16,subQ15,subQ14,subQ13,subQ12,subQ11,subQ10,subQ9,subQ8,subQ7,subQ6,subQ5,subQ4,subQ3,subQ2,subQ1,subQ0])],"isStart":false})]),OD(43.0)]});}
            var Q55;
            {var subQ0=sQuery(id+"F0.wireOp",EDGE,"E2.0.10.6");var subQ1=sQuery(id+"F0.wireOp",EDGE,"E2.0.10.5");var subQ2=sQuery(id+"F0.wireOp",EDGE,"E2.0.10.4");var subQ3=sQuery(id+"F0.wireOp",EDGE,"E2.0.10.3");var subQ4=sQuery(id+"F0.wireOp",EDGE,"E2.0.10.2");var subQ5=sQuery(id+"F0.wireOp",EDGE,"E2.0.10.1");var subQ6=sQuery(id+"F0.wireOp",EDGE,"E1.9.6.0");var subQ7=sQuery(id+"F0.wireOp",EDGE,"E1.9.5.0");var subQ8=sQuery(id+"F0.wireOp",EDGE,"E1.9.4.0");var subQ9=sQuery(id+"F0.wireOp",EDGE,"E1.9.3.0");var subQ10=sQuery(id+"F0.wireOp",EDGE,"E1.9.2.0");var subQ11=sQuery(id+"F0.wireOp",EDGE,"E1.9.1.0");var subQ12=sQuery(id+"F0.wireOp",EDGE,"E1.8.6.0");var subQ13=sQuery(id+"F0.wireOp",EDGE,"E1.8.5.0");var subQ14=sQuery(id+"F0.wireOp",EDGE,"E1.8.4.0");var subQ15=sQuery(id+"F0.wireOp",EDGE,"E1.8.3.0");var subQ16=sQuery(id+"F0.wireOp",EDGE,"E1.8.2.0");var subQ17=sQuery(id+"F0.wireOp",EDGE,"E1.8.1.0");var subQ18=sQuery(id+"F0.wireOp",EDGE,"E1.7.6.0");var subQ19=sQuery(id+"F0.wireOp",EDGE,"E1.7.5.0");var subQ20=sQuery(id+"F0.wireOp",EDGE,"E1.7.4.0");var subQ21=sQuery(id+"F0.wireOp",EDGE,"E1.7.3.0");var subQ22=sQuery(id+"F0.wireOp",EDGE,"E1.7.2.0");var subQ23=sQuery(id+"F0.wireOp",EDGE,"E1.7.1.0");var subQ24=sQuery(id+"F0.wireOp",EDGE,"E1.6.6.0");var subQ25=sQuery(id+"F0.wireOp",EDGE,"E1.6.5.0");var subQ26=sQuery(id+"F0.wireOp",EDGE,"E1.6.4.0");var subQ27=sQuery(id+"F0.wireOp",EDGE,"E1.6.3.0");var subQ28=sQuery(id+"F0.wireOp",EDGE,"E1.6.2.0");var subQ29=sQuery(id+"F0.wireOp",EDGE,"E1.6.1.0");var subQ30=sQuery(id+"F0.wireOp",EDGE,"E1.5.6.0");var subQ31=sQuery(id+"F0.wireOp",EDGE,"E1.5.5.0");var subQ32=sQuery(id+"F0.wireOp",EDGE,"E1.5.4.0");var subQ33=sQuery(id+"F0.wireOp",EDGE,"E1.5.3.0");var subQ34=sQuery(id+"F0.wireOp",EDGE,"E1.5.2.0");var subQ35=sQuery(id+"F0.wireOp",EDGE,"E1.5.1.0");var subQ36=sQuery(id+"F0.wireOp",EDGE,"E1.4.6.0");var subQ37=sQuery(id+"F0.wireOp",EDGE,"E1.4.5.0");var subQ38=sQuery(id+"F0.wireOp",EDGE,"E1.4.4.0");var subQ39=sQuery(id+"F0.wireOp",EDGE,"E1.4.3.0");var subQ40=sQuery(id+"F0.wireOp",EDGE,"E1.4.2.0");var subQ41=sQuery(id+"F0.wireOp",EDGE,"E1.4.1.0");var subQ42=sQuery(id+"F0.wireOp",EDGE,"E1.3.6.0");var subQ43=sQuery(id+"F0.wireOp",EDGE,"E1.3.5.0");var subQ44=sQuery(id+"F0.wireOp",EDGE,"E1.3.4.0");var subQ45=sQuery(id+"F0.wireOp",EDGE,"E1.3.3.0");var subQ46=sQuery(id+"F0.wireOp",EDGE,"E1.3.2.0");var subQ47=sQuery(id+"F0.wireOp",EDGE,"E1.3.1.0");var subQ48=sQuery(id+"F0.wireOp",EDGE,"E1.2.6.0");var subQ49=sQuery(id+"F0.wireOp",EDGE,"E1.2.5.0");var subQ50=sQuery(id+"F0.wireOp",EDGE,"E1.2.4.0");var subQ51=sQuery(id+"F0.wireOp",EDGE,"E1.2.3.0");var subQ52=sQuery(id+"F0.wireOp",EDGE,"E1.2.2.0");var subQ53=sQuery(id+"F0.wireOp",EDGE,"E1.2.1.0");var subQ54=sQuery(id+"F0.wireOp",EDGE,"E1.1.6.0");var subQ55=sQuery(id+"F0.wireOp",EDGE,"E1.1.5.0");var subQ56=sQuery(id+"F0.wireOp",EDGE,"E1.1.4.0");var subQ57=sQuery(id+"F0.wireOp",EDGE,"E1.1.3.0");var subQ58=sQuery(id+"F0.wireOp",EDGE,"E1.1.2.0");var subQ59=sQuery(id+"F0.wireOp",EDGE,"E1.1.1.0");var subQ60=sQuery(id+"F0.wireOp",EDGE,"E0.right");var subQ61=sQuery(id+"F0.wireOp",EDGE,"E0.left");var subQ62=sQuery(id+"F0.wireOp",EDGE,"E0.top");var subQ63=sQuery(id+"F0.wireOp",EDGE,"E0.bottom");Q55=makeQuery(id+"F2.opShell","OFFSET_FACE",FACE,{"disambiguationData":[OSD([subQ63,subQ62,subQ61,subQ60,subQ59,subQ58,subQ57,subQ56,subQ55,subQ54,subQ53,subQ52,subQ51,subQ50,subQ49,subQ48,subQ47,subQ46,subQ45,subQ44,subQ43,subQ42,subQ41,subQ40,subQ39,subQ38,subQ37,subQ36,subQ35,subQ34,subQ33,subQ32,subQ31,subQ30,subQ29,subQ28,subQ27,subQ26,subQ25,subQ24,subQ23,subQ22,subQ21,subQ20,subQ19,subQ18,subQ17,subQ16,subQ15,subQ14,subQ13,subQ12,subQ11,subQ10,subQ9,subQ8,subQ7,subQ6,subQ5,subQ4,subQ3,subQ2,subQ1,subQ0]),TDD([makeQuery(id+"F1.opExtrude","CAP_FACE",FACE,{"disambiguationData":[OSD([subQ63,subQ62,subQ61,subQ60,subQ59,subQ58,subQ57,subQ56,subQ55,subQ54,subQ53,subQ52,subQ51,subQ50,subQ49,subQ48,subQ47,subQ46,subQ45,subQ44,subQ43,subQ42,subQ41,subQ40,subQ39,subQ38,subQ37,subQ36,subQ35,subQ34,subQ33,subQ32,subQ31,subQ30,subQ29,subQ28,subQ27,subQ26,subQ25,subQ24,subQ23,subQ22,subQ21,subQ20,subQ19,subQ18,subQ17,subQ16,subQ15,subQ14,subQ13,subQ12,subQ11,subQ10,subQ9,subQ8,subQ7,subQ6,subQ5,subQ4,subQ3,subQ2,subQ1,subQ0])],"isStart":false})]),OD(42.0)]});}
            var Q56;
            {var subQ0=sQuery(id+"F0.wireOp",EDGE,"E2.0.10.6");var subQ1=sQuery(id+"F0.wireOp",EDGE,"E2.0.10.5");var subQ2=sQuery(id+"F0.wireOp",EDGE,"E2.0.10.4");var subQ3=sQuery(id+"F0.wireOp",EDGE,"E2.0.10.3");var subQ4=sQuery(id+"F0.wireOp",EDGE,"E2.0.10.2");var subQ5=sQuery(id+"F0.wireOp",EDGE,"E2.0.10.1");var subQ6=sQuery(id+"F0.wireOp",EDGE,"E1.9.6.0");var subQ7=sQuery(id+"F0.wireOp",EDGE,"E1.9.5.0");var subQ8=sQuery(id+"F0.wireOp",EDGE,"E1.9.4.0");var subQ9=sQuery(id+"F0.wireOp",EDGE,"E1.9.3.0");var subQ10=sQuery(id+"F0.wireOp",EDGE,"E1.9.2.0");var subQ11=sQuery(id+"F0.wireOp",EDGE,"E1.9.1.0");var subQ12=sQuery(id+"F0.wireOp",EDGE,"E1.8.6.0");var subQ13=sQuery(id+"F0.wireOp",EDGE,"E1.8.5.0");var subQ14=sQuery(id+"F0.wireOp",EDGE,"E1.8.4.0");var subQ15=sQuery(id+"F0.wireOp",EDGE,"E1.8.3.0");var subQ16=sQuery(id+"F0.wireOp",EDGE,"E1.8.2.0");var subQ17=sQuery(id+"F0.wireOp",EDGE,"E1.8.1.0");var subQ18=sQuery(id+"F0.wireOp",EDGE,"E1.7.6.0");var subQ19=sQuery(id+"F0.wireOp",EDGE,"E1.7.5.0");var subQ20=sQuery(id+"F0.wireOp",EDGE,"E1.7.4.0");var subQ21=sQuery(id+"F0.wireOp",EDGE,"E1.7.3.0");var subQ22=sQuery(id+"F0.wireOp",EDGE,"E1.7.2.0");var subQ23=sQuery(id+"F0.wireOp",EDGE,"E1.7.1.0");var subQ24=sQuery(id+"F0.wireOp",EDGE,"E1.6.6.0");var subQ25=sQuery(id+"F0.wireOp",EDGE,"E1.6.5.0");var subQ26=sQuery(id+"F0.wireOp",EDGE,"E1.6.4.0");var subQ27=sQuery(id+"F0.wireOp",EDGE,"E1.6.3.0");var subQ28=sQuery(id+"F0.wireOp",EDGE,"E1.6.2.0");var subQ29=sQuery(id+"F0.wireOp",EDGE,"E1.6.1.0");var subQ30=sQuery(id+"F0.wireOp",EDGE,"E1.5.6.0");var subQ31=sQuery(id+"F0.wireOp",EDGE,"E1.5.5.0");var subQ32=sQuery(id+"F0.wireOp",EDGE,"E1.5.4.0");var subQ33=sQuery(id+"F0.wireOp",EDGE,"E1.5.3.0");var subQ34=sQuery(id+"F0.wireOp",EDGE,"E1.5.2.0");var subQ35=sQuery(id+"F0.wireOp",EDGE,"E1.5.1.0");var subQ36=sQuery(id+"F0.wireOp",EDGE,"E1.4.6.0");var subQ37=sQuery(id+"F0.wireOp",EDGE,"E1.4.5.0");var subQ38=sQuery(id+"F0.wireOp",EDGE,"E1.4.4.0");var subQ39=sQuery(id+"F0.wireOp",EDGE,"E1.4.3.0");var subQ40=sQuery(id+"F0.wireOp",EDGE,"E1.4.2.0");var subQ41=sQuery(id+"F0.wireOp",EDGE,"E1.4.1.0");var subQ42=sQuery(id+"F0.wireOp",EDGE,"E1.3.6.0");var subQ43=sQuery(id+"F0.wireOp",EDGE,"E1.3.5.0");var subQ44=sQuery(id+"F0.wireOp",EDGE,"E1.3.4.0");var subQ45=sQuery(id+"F0.wireOp",EDGE,"E1.3.3.0");var subQ46=sQuery(id+"F0.wireOp",EDGE,"E1.3.2.0");var subQ47=sQuery(id+"F0.wireOp",EDGE,"E1.3.1.0");var subQ48=sQuery(id+"F0.wireOp",EDGE,"E1.2.6.0");var subQ49=sQuery(id+"F0.wireOp",EDGE,"E1.2.5.0");var subQ50=sQuery(id+"F0.wireOp",EDGE,"E1.2.4.0");var subQ51=sQuery(id+"F0.wireOp",EDGE,"E1.2.3.0");var subQ52=sQuery(id+"F0.wireOp",EDGE,"E1.2.2.0");var subQ53=sQuery(id+"F0.wireOp",EDGE,"E1.2.1.0");var subQ54=sQuery(id+"F0.wireOp",EDGE,"E1.1.6.0");var subQ55=sQuery(id+"F0.wireOp",EDGE,"E1.1.5.0");var subQ56=sQuery(id+"F0.wireOp",EDGE,"E1.1.4.0");var subQ57=sQuery(id+"F0.wireOp",EDGE,"E1.1.3.0");var subQ58=sQuery(id+"F0.wireOp",EDGE,"E1.1.2.0");var subQ59=sQuery(id+"F0.wireOp",EDGE,"E1.1.1.0");var subQ60=sQuery(id+"F0.wireOp",EDGE,"E0.right");var subQ61=sQuery(id+"F0.wireOp",EDGE,"E0.left");var subQ62=sQuery(id+"F0.wireOp",EDGE,"E0.top");var subQ63=sQuery(id+"F0.wireOp",EDGE,"E0.bottom");Q56=makeQuery(id+"F2.opShell","OFFSET_FACE",FACE,{"disambiguationData":[OSD([subQ63,subQ62,subQ61,subQ60,subQ59,subQ58,subQ57,subQ56,subQ55,subQ54,subQ53,subQ52,subQ51,subQ50,subQ49,subQ48,subQ47,subQ46,subQ45,subQ44,subQ43,subQ42,subQ41,subQ40,subQ39,subQ38,subQ37,subQ36,subQ35,subQ34,subQ33,subQ32,subQ31,subQ30,subQ29,subQ28,subQ27,subQ26,subQ25,subQ24,subQ23,subQ22,subQ21,subQ20,subQ19,subQ18,subQ17,subQ16,subQ15,subQ14,subQ13,subQ12,subQ11,subQ10,subQ9,subQ8,subQ7,subQ6,subQ5,subQ4,subQ3,subQ2,subQ1,subQ0]),TDD([makeQuery(id+"F1.opExtrude","CAP_FACE",FACE,{"disambiguationData":[OSD([subQ63,subQ62,subQ61,subQ60,subQ59,subQ58,subQ57,subQ56,subQ55,subQ54,subQ53,subQ52,subQ51,subQ50,subQ49,subQ48,subQ47,subQ46,subQ45,subQ44,subQ43,subQ42,subQ41,subQ40,subQ39,subQ38,subQ37,subQ36,subQ35,subQ34,subQ33,subQ32,subQ31,subQ30,subQ29,subQ28,subQ27,subQ26,subQ25,subQ24,subQ23,subQ22,subQ21,subQ20,subQ19,subQ18,subQ17,subQ16,subQ15,subQ14,subQ13,subQ12,subQ11,subQ10,subQ9,subQ8,subQ7,subQ6,subQ5,subQ4,subQ3,subQ2,subQ1,subQ0])],"isStart":false})]),OD(49.0)]});}
            var Q57;
            {var subQ0=sQuery(id+"F0.wireOp",EDGE,"E2.0.10.6");var subQ1=sQuery(id+"F0.wireOp",EDGE,"E2.0.10.5");var subQ2=sQuery(id+"F0.wireOp",EDGE,"E2.0.10.4");var subQ3=sQuery(id+"F0.wireOp",EDGE,"E2.0.10.3");var subQ4=sQuery(id+"F0.wireOp",EDGE,"E2.0.10.2");var subQ5=sQuery(id+"F0.wireOp",EDGE,"E2.0.10.1");var subQ6=sQuery(id+"F0.wireOp",EDGE,"E1.9.6.0");var subQ7=sQuery(id+"F0.wireOp",EDGE,"E1.9.5.0");var subQ8=sQuery(id+"F0.wireOp",EDGE,"E1.9.4.0");var subQ9=sQuery(id+"F0.wireOp",EDGE,"E1.9.3.0");var subQ10=sQuery(id+"F0.wireOp",EDGE,"E1.9.2.0");var subQ11=sQuery(id+"F0.wireOp",EDGE,"E1.9.1.0");var subQ12=sQuery(id+"F0.wireOp",EDGE,"E1.8.6.0");var subQ13=sQuery(id+"F0.wireOp",EDGE,"E1.8.5.0");var subQ14=sQuery(id+"F0.wireOp",EDGE,"E1.8.4.0");var subQ15=sQuery(id+"F0.wireOp",EDGE,"E1.8.3.0");var subQ16=sQuery(id+"F0.wireOp",EDGE,"E1.8.2.0");var subQ17=sQuery(id+"F0.wireOp",EDGE,"E1.8.1.0");var subQ18=sQuery(id+"F0.wireOp",EDGE,"E1.7.6.0");var subQ19=sQuery(id+"F0.wireOp",EDGE,"E1.7.5.0");var subQ20=sQuery(id+"F0.wireOp",EDGE,"E1.7.4.0");var subQ21=sQuery(id+"F0.wireOp",EDGE,"E1.7.3.0");var subQ22=sQuery(id+"F0.wireOp",EDGE,"E1.7.2.0");var subQ23=sQuery(id+"F0.wireOp",EDGE,"E1.7.1.0");var subQ24=sQuery(id+"F0.wireOp",EDGE,"E1.6.6.0");var subQ25=sQuery(id+"F0.wireOp",EDGE,"E1.6.5.0");var subQ26=sQuery(id+"F0.wireOp",EDGE,"E1.6.4.0");var subQ27=sQuery(id+"F0.wireOp",EDGE,"E1.6.3.0");var subQ28=sQuery(id+"F0.wireOp",EDGE,"E1.6.2.0");var subQ29=sQuery(id+"F0.wireOp",EDGE,"E1.6.1.0");var subQ30=sQuery(id+"F0.wireOp",EDGE,"E1.5.6.0");var subQ31=sQuery(id+"F0.wireOp",EDGE,"E1.5.5.0");var subQ32=sQuery(id+"F0.wireOp",EDGE,"E1.5.4.0");var subQ33=sQuery(id+"F0.wireOp",EDGE,"E1.5.3.0");var subQ34=sQuery(id+"F0.wireOp",EDGE,"E1.5.2.0");var subQ35=sQuery(id+"F0.wireOp",EDGE,"E1.5.1.0");var subQ36=sQuery(id+"F0.wireOp",EDGE,"E1.4.6.0");var subQ37=sQuery(id+"F0.wireOp",EDGE,"E1.4.5.0");var subQ38=sQuery(id+"F0.wireOp",EDGE,"E1.4.4.0");var subQ39=sQuery(id+"F0.wireOp",EDGE,"E1.4.3.0");var subQ40=sQuery(id+"F0.wireOp",EDGE,"E1.4.2.0");var subQ41=sQuery(id+"F0.wireOp",EDGE,"E1.4.1.0");var subQ42=sQuery(id+"F0.wireOp",EDGE,"E1.3.6.0");var subQ43=sQuery(id+"F0.wireOp",EDGE,"E1.3.5.0");var subQ44=sQuery(id+"F0.wireOp",EDGE,"E1.3.4.0");var subQ45=sQuery(id+"F0.wireOp",EDGE,"E1.3.3.0");var subQ46=sQuery(id+"F0.wireOp",EDGE,"E1.3.2.0");var subQ47=sQuery(id+"F0.wireOp",EDGE,"E1.3.1.0");var subQ48=sQuery(id+"F0.wireOp",EDGE,"E1.2.6.0");var subQ49=sQuery(id+"F0.wireOp",EDGE,"E1.2.5.0");var subQ50=sQuery(id+"F0.wireOp",EDGE,"E1.2.4.0");var subQ51=sQuery(id+"F0.wireOp",EDGE,"E1.2.3.0");var subQ52=sQuery(id+"F0.wireOp",EDGE,"E1.2.2.0");var subQ53=sQuery(id+"F0.wireOp",EDGE,"E1.2.1.0");var subQ54=sQuery(id+"F0.wireOp",EDGE,"E1.1.6.0");var subQ55=sQuery(id+"F0.wireOp",EDGE,"E1.1.5.0");var subQ56=sQuery(id+"F0.wireOp",EDGE,"E1.1.4.0");var subQ57=sQuery(id+"F0.wireOp",EDGE,"E1.1.3.0");var subQ58=sQuery(id+"F0.wireOp",EDGE,"E1.1.2.0");var subQ59=sQuery(id+"F0.wireOp",EDGE,"E1.1.1.0");var subQ60=sQuery(id+"F0.wireOp",EDGE,"E0.right");var subQ61=sQuery(id+"F0.wireOp",EDGE,"E0.left");var subQ62=sQuery(id+"F0.wireOp",EDGE,"E0.top");var subQ63=sQuery(id+"F0.wireOp",EDGE,"E0.bottom");Q57=makeQuery(id+"F2.opShell","OFFSET_FACE",FACE,{"disambiguationData":[OSD([subQ63,subQ62,subQ61,subQ60,subQ59,subQ58,subQ57,subQ56,subQ55,subQ54,subQ53,subQ52,subQ51,subQ50,subQ49,subQ48,subQ47,subQ46,subQ45,subQ44,subQ43,subQ42,subQ41,subQ40,subQ39,subQ38,subQ37,subQ36,subQ35,subQ34,subQ33,subQ32,subQ31,subQ30,subQ29,subQ28,subQ27,subQ26,subQ25,subQ24,subQ23,subQ22,subQ21,subQ20,subQ19,subQ18,subQ17,subQ16,subQ15,subQ14,subQ13,subQ12,subQ11,subQ10,subQ9,subQ8,subQ7,subQ6,subQ5,subQ4,subQ3,subQ2,subQ1,subQ0]),TDD([makeQuery(id+"F1.opExtrude","CAP_FACE",FACE,{"disambiguationData":[OSD([subQ63,subQ62,subQ61,subQ60,subQ59,subQ58,subQ57,subQ56,subQ55,subQ54,subQ53,subQ52,subQ51,subQ50,subQ49,subQ48,subQ47,subQ46,subQ45,subQ44,subQ43,subQ42,subQ41,subQ40,subQ39,subQ38,subQ37,subQ36,subQ35,subQ34,subQ33,subQ32,subQ31,subQ30,subQ29,subQ28,subQ27,subQ26,subQ25,subQ24,subQ23,subQ22,subQ21,subQ20,subQ19,subQ18,subQ17,subQ16,subQ15,subQ14,subQ13,subQ12,subQ11,subQ10,subQ9,subQ8,subQ7,subQ6,subQ5,subQ4,subQ3,subQ2,subQ1,subQ0])],"isStart":false})]),OD(48.0)]});}
            var Q58;
            {var subQ0=sQuery(id+"F0.wireOp",EDGE,"E2.0.10.6");var subQ1=sQuery(id+"F0.wireOp",EDGE,"E2.0.10.5");var subQ2=sQuery(id+"F0.wireOp",EDGE,"E2.0.10.4");var subQ3=sQuery(id+"F0.wireOp",EDGE,"E2.0.10.3");var subQ4=sQuery(id+"F0.wireOp",EDGE,"E2.0.10.2");var subQ5=sQuery(id+"F0.wireOp",EDGE,"E2.0.10.1");var subQ6=sQuery(id+"F0.wireOp",EDGE,"E1.9.6.0");var subQ7=sQuery(id+"F0.wireOp",EDGE,"E1.9.5.0");var subQ8=sQuery(id+"F0.wireOp",EDGE,"E1.9.4.0");var subQ9=sQuery(id+"F0.wireOp",EDGE,"E1.9.3.0");var subQ10=sQuery(id+"F0.wireOp",EDGE,"E1.9.2.0");var subQ11=sQuery(id+"F0.wireOp",EDGE,"E1.9.1.0");var subQ12=sQuery(id+"F0.wireOp",EDGE,"E1.8.6.0");var subQ13=sQuery(id+"F0.wireOp",EDGE,"E1.8.5.0");var subQ14=sQuery(id+"F0.wireOp",EDGE,"E1.8.4.0");var subQ15=sQuery(id+"F0.wireOp",EDGE,"E1.8.3.0");var subQ16=sQuery(id+"F0.wireOp",EDGE,"E1.8.2.0");var subQ17=sQuery(id+"F0.wireOp",EDGE,"E1.8.1.0");var subQ18=sQuery(id+"F0.wireOp",EDGE,"E1.7.6.0");var subQ19=sQuery(id+"F0.wireOp",EDGE,"E1.7.5.0");var subQ20=sQuery(id+"F0.wireOp",EDGE,"E1.7.4.0");var subQ21=sQuery(id+"F0.wireOp",EDGE,"E1.7.3.0");var subQ22=sQuery(id+"F0.wireOp",EDGE,"E1.7.2.0");var subQ23=sQuery(id+"F0.wireOp",EDGE,"E1.7.1.0");var subQ24=sQuery(id+"F0.wireOp",EDGE,"E1.6.6.0");var subQ25=sQuery(id+"F0.wireOp",EDGE,"E1.6.5.0");var subQ26=sQuery(id+"F0.wireOp",EDGE,"E1.6.4.0");var subQ27=sQuery(id+"F0.wireOp",EDGE,"E1.6.3.0");var subQ28=sQuery(id+"F0.wireOp",EDGE,"E1.6.2.0");var subQ29=sQuery(id+"F0.wireOp",EDGE,"E1.6.1.0");var subQ30=sQuery(id+"F0.wireOp",EDGE,"E1.5.6.0");var subQ31=sQuery(id+"F0.wireOp",EDGE,"E1.5.5.0");var subQ32=sQuery(id+"F0.wireOp",EDGE,"E1.5.4.0");var subQ33=sQuery(id+"F0.wireOp",EDGE,"E1.5.3.0");var subQ34=sQuery(id+"F0.wireOp",EDGE,"E1.5.2.0");var subQ35=sQuery(id+"F0.wireOp",EDGE,"E1.5.1.0");var subQ36=sQuery(id+"F0.wireOp",EDGE,"E1.4.6.0");var subQ37=sQuery(id+"F0.wireOp",EDGE,"E1.4.5.0");var subQ38=sQuery(id+"F0.wireOp",EDGE,"E1.4.4.0");var subQ39=sQuery(id+"F0.wireOp",EDGE,"E1.4.3.0");var subQ40=sQuery(id+"F0.wireOp",EDGE,"E1.4.2.0");var subQ41=sQuery(id+"F0.wireOp",EDGE,"E1.4.1.0");var subQ42=sQuery(id+"F0.wireOp",EDGE,"E1.3.6.0");var subQ43=sQuery(id+"F0.wireOp",EDGE,"E1.3.5.0");var subQ44=sQuery(id+"F0.wireOp",EDGE,"E1.3.4.0");var subQ45=sQuery(id+"F0.wireOp",EDGE,"E1.3.3.0");var subQ46=sQuery(id+"F0.wireOp",EDGE,"E1.3.2.0");var subQ47=sQuery(id+"F0.wireOp",EDGE,"E1.3.1.0");var subQ48=sQuery(id+"F0.wireOp",EDGE,"E1.2.6.0");var subQ49=sQuery(id+"F0.wireOp",EDGE,"E1.2.5.0");var subQ50=sQuery(id+"F0.wireOp",EDGE,"E1.2.4.0");var subQ51=sQuery(id+"F0.wireOp",EDGE,"E1.2.3.0");var subQ52=sQuery(id+"F0.wireOp",EDGE,"E1.2.2.0");var subQ53=sQuery(id+"F0.wireOp",EDGE,"E1.2.1.0");var subQ54=sQuery(id+"F0.wireOp",EDGE,"E1.1.6.0");var subQ55=sQuery(id+"F0.wireOp",EDGE,"E1.1.5.0");var subQ56=sQuery(id+"F0.wireOp",EDGE,"E1.1.4.0");var subQ57=sQuery(id+"F0.wireOp",EDGE,"E1.1.3.0");var subQ58=sQuery(id+"F0.wireOp",EDGE,"E1.1.2.0");var subQ59=sQuery(id+"F0.wireOp",EDGE,"E1.1.1.0");var subQ60=sQuery(id+"F0.wireOp",EDGE,"E0.right");var subQ61=sQuery(id+"F0.wireOp",EDGE,"E0.left");var subQ62=sQuery(id+"F0.wireOp",EDGE,"E0.top");var subQ63=sQuery(id+"F0.wireOp",EDGE,"E0.bottom");Q58=makeQuery(id+"F2.opShell","OFFSET_FACE",FACE,{"disambiguationData":[OSD([subQ63,subQ62,subQ61,subQ60,subQ59,subQ58,subQ57,subQ56,subQ55,subQ54,subQ53,subQ52,subQ51,subQ50,subQ49,subQ48,subQ47,subQ46,subQ45,subQ44,subQ43,subQ42,subQ41,subQ40,subQ39,subQ38,subQ37,subQ36,subQ35,subQ34,subQ33,subQ32,subQ31,subQ30,subQ29,subQ28,subQ27,subQ26,subQ25,subQ24,subQ23,subQ22,subQ21,subQ20,subQ19,subQ18,subQ17,subQ16,subQ15,subQ14,subQ13,subQ12,subQ11,subQ10,subQ9,subQ8,subQ7,subQ6,subQ5,subQ4,subQ3,subQ2,subQ1,subQ0]),TDD([makeQuery(id+"F1.opExtrude","CAP_FACE",FACE,{"disambiguationData":[OSD([subQ63,subQ62,subQ61,subQ60,subQ59,subQ58,subQ57,subQ56,subQ55,subQ54,subQ53,subQ52,subQ51,subQ50,subQ49,subQ48,subQ47,subQ46,subQ45,subQ44,subQ43,subQ42,subQ41,subQ40,subQ39,subQ38,subQ37,subQ36,subQ35,subQ34,subQ33,subQ32,subQ31,subQ30,subQ29,subQ28,subQ27,subQ26,subQ25,subQ24,subQ23,subQ22,subQ21,subQ20,subQ19,subQ18,subQ17,subQ16,subQ15,subQ14,subQ13,subQ12,subQ11,subQ10,subQ9,subQ8,subQ7,subQ6,subQ5,subQ4,subQ3,subQ2,subQ1,subQ0])],"isStart":false})]),OD(55.0)]});}
            var Q59;
            {var subQ0=sQuery(id+"F0.wireOp",EDGE,"E2.0.10.6");var subQ1=sQuery(id+"F0.wireOp",EDGE,"E2.0.10.5");var subQ2=sQuery(id+"F0.wireOp",EDGE,"E2.0.10.4");var subQ3=sQuery(id+"F0.wireOp",EDGE,"E2.0.10.3");var subQ4=sQuery(id+"F0.wireOp",EDGE,"E2.0.10.2");var subQ5=sQuery(id+"F0.wireOp",EDGE,"E2.0.10.1");var subQ6=sQuery(id+"F0.wireOp",EDGE,"E1.9.6.0");var subQ7=sQuery(id+"F0.wireOp",EDGE,"E1.9.5.0");var subQ8=sQuery(id+"F0.wireOp",EDGE,"E1.9.4.0");var subQ9=sQuery(id+"F0.wireOp",EDGE,"E1.9.3.0");var subQ10=sQuery(id+"F0.wireOp",EDGE,"E1.9.2.0");var subQ11=sQuery(id+"F0.wireOp",EDGE,"E1.9.1.0");var subQ12=sQuery(id+"F0.wireOp",EDGE,"E1.8.6.0");var subQ13=sQuery(id+"F0.wireOp",EDGE,"E1.8.5.0");var subQ14=sQuery(id+"F0.wireOp",EDGE,"E1.8.4.0");var subQ15=sQuery(id+"F0.wireOp",EDGE,"E1.8.3.0");var subQ16=sQuery(id+"F0.wireOp",EDGE,"E1.8.2.0");var subQ17=sQuery(id+"F0.wireOp",EDGE,"E1.8.1.0");var subQ18=sQuery(id+"F0.wireOp",EDGE,"E1.7.6.0");var subQ19=sQuery(id+"F0.wireOp",EDGE,"E1.7.5.0");var subQ20=sQuery(id+"F0.wireOp",EDGE,"E1.7.4.0");var subQ21=sQuery(id+"F0.wireOp",EDGE,"E1.7.3.0");var subQ22=sQuery(id+"F0.wireOp",EDGE,"E1.7.2.0");var subQ23=sQuery(id+"F0.wireOp",EDGE,"E1.7.1.0");var subQ24=sQuery(id+"F0.wireOp",EDGE,"E1.6.6.0");var subQ25=sQuery(id+"F0.wireOp",EDGE,"E1.6.5.0");var subQ26=sQuery(id+"F0.wireOp",EDGE,"E1.6.4.0");var subQ27=sQuery(id+"F0.wireOp",EDGE,"E1.6.3.0");var subQ28=sQuery(id+"F0.wireOp",EDGE,"E1.6.2.0");var subQ29=sQuery(id+"F0.wireOp",EDGE,"E1.6.1.0");var subQ30=sQuery(id+"F0.wireOp",EDGE,"E1.5.6.0");var subQ31=sQuery(id+"F0.wireOp",EDGE,"E1.5.5.0");var subQ32=sQuery(id+"F0.wireOp",EDGE,"E1.5.4.0");var subQ33=sQuery(id+"F0.wireOp",EDGE,"E1.5.3.0");var subQ34=sQuery(id+"F0.wireOp",EDGE,"E1.5.2.0");var subQ35=sQuery(id+"F0.wireOp",EDGE,"E1.5.1.0");var subQ36=sQuery(id+"F0.wireOp",EDGE,"E1.4.6.0");var subQ37=sQuery(id+"F0.wireOp",EDGE,"E1.4.5.0");var subQ38=sQuery(id+"F0.wireOp",EDGE,"E1.4.4.0");var subQ39=sQuery(id+"F0.wireOp",EDGE,"E1.4.3.0");var subQ40=sQuery(id+"F0.wireOp",EDGE,"E1.4.2.0");var subQ41=sQuery(id+"F0.wireOp",EDGE,"E1.4.1.0");var subQ42=sQuery(id+"F0.wireOp",EDGE,"E1.3.6.0");var subQ43=sQuery(id+"F0.wireOp",EDGE,"E1.3.5.0");var subQ44=sQuery(id+"F0.wireOp",EDGE,"E1.3.4.0");var subQ45=sQuery(id+"F0.wireOp",EDGE,"E1.3.3.0");var subQ46=sQuery(id+"F0.wireOp",EDGE,"E1.3.2.0");var subQ47=sQuery(id+"F0.wireOp",EDGE,"E1.3.1.0");var subQ48=sQuery(id+"F0.wireOp",EDGE,"E1.2.6.0");var subQ49=sQuery(id+"F0.wireOp",EDGE,"E1.2.5.0");var subQ50=sQuery(id+"F0.wireOp",EDGE,"E1.2.4.0");var subQ51=sQuery(id+"F0.wireOp",EDGE,"E1.2.3.0");var subQ52=sQuery(id+"F0.wireOp",EDGE,"E1.2.2.0");var subQ53=sQuery(id+"F0.wireOp",EDGE,"E1.2.1.0");var subQ54=sQuery(id+"F0.wireOp",EDGE,"E1.1.6.0");var subQ55=sQuery(id+"F0.wireOp",EDGE,"E1.1.5.0");var subQ56=sQuery(id+"F0.wireOp",EDGE,"E1.1.4.0");var subQ57=sQuery(id+"F0.wireOp",EDGE,"E1.1.3.0");var subQ58=sQuery(id+"F0.wireOp",EDGE,"E1.1.2.0");var subQ59=sQuery(id+"F0.wireOp",EDGE,"E1.1.1.0");var subQ60=sQuery(id+"F0.wireOp",EDGE,"E0.right");var subQ61=sQuery(id+"F0.wireOp",EDGE,"E0.left");var subQ62=sQuery(id+"F0.wireOp",EDGE,"E0.top");var subQ63=sQuery(id+"F0.wireOp",EDGE,"E0.bottom");Q59=makeQuery(id+"F2.opShell","OFFSET_FACE",FACE,{"disambiguationData":[OSD([subQ63,subQ62,subQ61,subQ60,subQ59,subQ58,subQ57,subQ56,subQ55,subQ54,subQ53,subQ52,subQ51,subQ50,subQ49,subQ48,subQ47,subQ46,subQ45,subQ44,subQ43,subQ42,subQ41,subQ40,subQ39,subQ38,subQ37,subQ36,subQ35,subQ34,subQ33,subQ32,subQ31,subQ30,subQ29,subQ28,subQ27,subQ26,subQ25,subQ24,subQ23,subQ22,subQ21,subQ20,subQ19,subQ18,subQ17,subQ16,subQ15,subQ14,subQ13,subQ12,subQ11,subQ10,subQ9,subQ8,subQ7,subQ6,subQ5,subQ4,subQ3,subQ2,subQ1,subQ0]),TDD([makeQuery(id+"F1.opExtrude","CAP_FACE",FACE,{"disambiguationData":[OSD([subQ63,subQ62,subQ61,subQ60,subQ59,subQ58,subQ57,subQ56,subQ55,subQ54,subQ53,subQ52,subQ51,subQ50,subQ49,subQ48,subQ47,subQ46,subQ45,subQ44,subQ43,subQ42,subQ41,subQ40,subQ39,subQ38,subQ37,subQ36,subQ35,subQ34,subQ33,subQ32,subQ31,subQ30,subQ29,subQ28,subQ27,subQ26,subQ25,subQ24,subQ23,subQ22,subQ21,subQ20,subQ19,subQ18,subQ17,subQ16,subQ15,subQ14,subQ13,subQ12,subQ11,subQ10,subQ9,subQ8,subQ7,subQ6,subQ5,subQ4,subQ3,subQ2,subQ1,subQ0])],"isStart":false})]),OD(54.0)]});}
            extrude(context, id + "F3", {"entities" : qUnion([Q0, Q1, Q2, Q3, Q4, Q5, Q6, Q7, Q8, Q9, Q10, Q11, Q12, Q13, Q14, Q15, Q16, Q17, Q18, Q19, Q20, Q21, Q22, Q23, Q24, Q25, Q26, Q27, Q28, Q29, Q30, Q31, Q32, Q33, Q34, Q35, Q36, Q37, Q38, Q39, Q40, Q41, Q42, Q43, Q44, Q45, Q46, Q47, Q48, Q49, Q50, Q51, Q52, Q53, Q54, Q55, Q56, Q57, Q58, Q59]), "operationType" : NewBodyOperationType.REMOVE, "oppositeDirection" : true, "depth" : 15 * mm});
        }
    });
